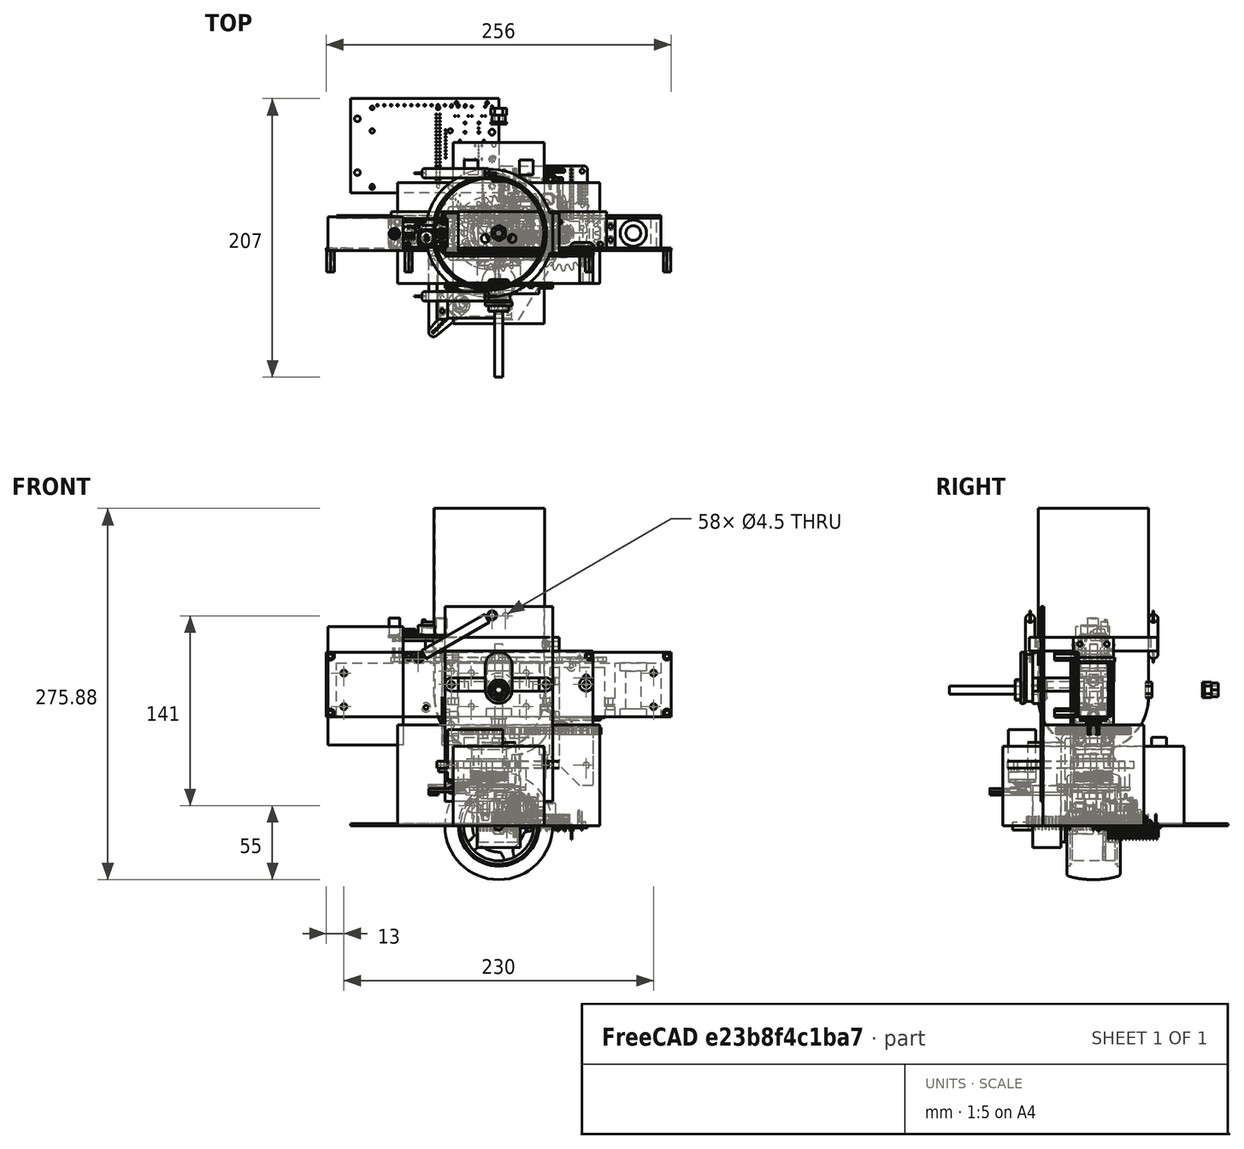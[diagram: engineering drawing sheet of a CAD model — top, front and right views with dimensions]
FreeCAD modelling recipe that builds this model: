
FCSTD DOCUMENT  (FreeCAD 0.19R24276 (Git))
Label: new_wheel_assy
License: All rights reserved
LicenseURL: http://en.wikipedia.org/wiki/All_rights_reserved
objects: Part::Feature×283, Sketcher::SketchObject×273, PartDesign::Pad×176, PartDesign::Body×146, App::Part×107, PartDesign::Pocket×72, PartDesign::FeatureBase×19, PartDesign::Revolution×11, PartDesign::Groove×8, Part::Part2DObjectPython×6, PartDesign::Chamfer×6, TechDraw::DrawViewPart×6, PartDesign::CoordinateSystem×5, TechDraw::DrawViewDimension×5, PartDesign::Plane×4, PartDesign::PolarPattern×4, TechDraw::DrawSVGTemplate×3, TechDraw::DrawPage×3, TechDraw::DrawViewSymbol×2, Mesh::Feature×1, +1 more types
note: 1288 computed .brp shape members not serialized (recipe doc carries the construction recipe); baked Part::Feature solids carry a one-line shape summary decoded from their .brp

FEATURE [Sketcher::SketchObject] Sketch
  FullyConstrained = false
  MapMode = 5
  Placement = pos=(0,0,0) rot=(0.57735,0.57735,0.57735;2.0944rad)
  Support = -> [YZ_Plane]
  sketch-geometry (17):
    g0: LineSegment StartX=16 StartY=28.5 StartZ=0 EndX=16 EndY=26 EndZ=0
    g1: LineSegment StartX=16 StartY=26 StartZ=0 EndX=-16 EndY=26 EndZ=0
    g2: LineSegment StartX=-16 StartY=26 StartZ=0 EndX=-16 EndY=28.5 EndZ=0
    g3: LineSegment StartX=-16 StartY=28.5 StartZ=0 EndX=-17.5 EndY=28.5 EndZ=0
    g4: LineSegment StartX=-17.5 StartY=28.5 StartZ=0 EndX=-17.5 EndY=30 EndZ=0
    g5: LineSegment StartX=-17.5 StartY=30 StartZ=0 EndX=-17.85 EndY=30 EndZ=0
    g6: LineSegment StartX=-19.85 StartY=32 StartZ=0 EndX=-19.85 EndY=35.5078 EndZ=0
    g7: LineSegment StartX=19.85 StartY=35.5078 StartZ=0 EndX=19.85 EndY=32 EndZ=0
    g8: LineSegment StartX=17.85 StartY=30 StartZ=0 EndX=17.5 EndY=30 EndZ=0
    g9: LineSegment StartX=17.5 StartY=30 StartZ=0 EndX=17.5 EndY=28.5 EndZ=0
    g10: LineSegment StartX=17.5 StartY=28.5 StartZ=0 EndX=16 EndY=28.5 EndZ=0
    g11: ArcOfCircle CenterX=5.199e-13 CenterY=-27.17 CenterZ=0 NormalX=0 NormalY=0 NormalZ=1 AngleXU=0 Radius=67.17 StartAngle=1.5708 EndAngle=1.84824
    g12: ArcOfCircle CenterX=5.199e-13 CenterY=-27.17 CenterZ=0 NormalX=0 NormalY=0 NormalZ=1 AngleXU=0 Radius=67.17 StartAngle=1.29335 EndAngle=1.5708
    g13: ArcOfCircle CenterX=-17.85 CenterY=32 CenterZ=0 NormalX=0 NormalY=0 NormalZ=1 AngleXU=0 Radius=2 StartAngle=3.14159 EndAngle=4.71239
    g14: ArcOfCircle CenterX=17.85 CenterY=32 CenterZ=0 NormalX=0 NormalY=0 NormalZ=1 AngleXU=0 Radius=2 StartAngle=4.71239 EndAngle=6.28319
    g15: ArcOfCircle CenterX=-17.85 CenterY=35.5078 CenterZ=0 NormalX=0 NormalY=0 NormalZ=1 AngleXU=0 Radius=2 StartAngle=1.84824 EndAngle=3.14159
    g16: ArcOfCircle CenterX=17.85 CenterY=35.5078 CenterZ=0 NormalX=0 NormalY=0 NormalZ=1 AngleXU=0 Radius=2 StartAngle=-9e-16 EndAngle=1.29335
  constraints (44):
    c: Coincident(g0,g1)
    c: Coincident(g1,g2)
    c: Coincident(g2,g3)
    c: Coincident(g3,g4)
    c: Coincident(g4,g5)
    c: Coincident(g8,g9)
    c: Coincident(g9,g10)
    c: Coincident(g10,g0)
    c: Vertical(g0)
    c: Vertical(g9)
    c: Vertical(g7)
    c: Horizontal(g8)
    c: Horizontal(g10)
    c: Horizontal(g1)
    c: Vertical(g2)
    c: Horizontal(g3)
    c: Horizontal(g5)
    c: Symmetric(g4,g8,g-2)
    c: DistanceX(g4,g8) = 35
    c: Equal(g3,g10)
    c: DistanceX(g10,g10) = 1.5
    c: DistanceY(g-1,g1) = 26
    c: DistanceY(g-1,g3) = 28.5
    c: DistanceY(g-1,g4) = 30
    c: Symmetric(g2,g0,g-2)
    c: Tangent(g11,g12) = -1.5708
    c: PointOnObject(g11,g-2)
    c: Coincident(g12,g11)
    c: DistanceY(g-1,g11) = 40
    c: Tangent(g5,g13) = 1.5708
    c: Tangent(g6,g13) = 1.5708
    c: Tangent(g7,g14) = 1.5708
    c: Tangent(g8,g14) = 1.5708
    c: Radius(g14) = 2
    c: DistanceX(g6,g7) = 39.7
    c: DistanceY(g11,g-1) = 27.17
    c: Tangent(g11,g15) = -1.5708
    c: Tangent(g6,g15) = 1.5708
    c: Tangent(g12,g16) = -1.5708
    c: Tangent(g7,g16) = 1.5708
    c: Symmetric(g6,g7,g-2)
    c: Equal(g16,g15)
    c: Radius(g16) = 2
    c: Symmetric(g6,g7,g-2)
FEATURE [PartDesign::Revolution] Revolution
  AllowMultiFace = false
  Angle = 360
  Axis = (3e-16,1,-2e-16)
  Base = (0,0,0)
  Placement = pos=(0,0,0) rot=(0.57735,0.57735,0.57735;2.0944rad)
  Profile = -> Sketch
  ReferenceAxis = -> Sketch [H_Axis]
FEATURE [PartDesign::Plane] DatumPlane
  AttachmentOffset = pos=(0,0,7) rot=(0,0,1;0rad)
  Length = 95.8516
  MapMode = 4
  Placement = pos=(0,7,0) rot=(0.57735,0.57735,0.57735;4.18879rad)
  ResizeMode = 0
  Support = -> [Revolution]
  Width = 95.8986
FEATURE [Sketcher::SketchObject] Sketch001
  FullyConstrained = false
  MapMode = 5
  Placement = pos=(0,7,0) rot=(0.57735,0.57735,0.57735;4.18879rad)
  Support = -> [DatumPlane]
  sketch-geometry (26):
    g0: LineSegment StartX=7 StartY=-18.2003 StartZ=0 EndX=19.4726 EndY=1.0332 EndZ=0
    g1: LineSegment StartX=19.4726 StartY=1.0332 StartZ=0 EndX=5.03473 EndY=18.8388 EndZ=0
    g2: LineSegment StartX=5.03473 StartY=18.8388 StartZ=0 EndX=-16.361 EndY=10.6098 EndZ=0
    g3: LineSegment StartX=-16.361 StartY=10.6098 StartZ=0 EndX=-15.1464 EndY=-12.2816 EndZ=0
    g4: LineSegment StartX=-15.1464 StartY=-12.2816 StartZ=0 EndX=7 EndY=-18.2003 EndZ=0
    g5: Circle CenterX=0 CenterY=0 CenterZ=0 NormalX=0 NormalY=0 NormalZ=1 AngleXU=0 Radius=19.5
    g6: ArcOfCircle CenterX=0 CenterY=0 CenterZ=0 NormalX=0 NormalY=0 NormalZ=1 AngleXU=0 Radius=19.5 StartAngle=5.60186 EndAngle=6.33619
    g7: ArcOfCircle CenterX=0 CenterY=0 CenterZ=0 NormalX=0 NormalY=0 NormalZ=1 AngleXU=0 Radius=19.5 StartAngle=4.34522 EndAngle=5.07956
    g8: ArcOfCircle CenterX=0 CenterY=0 CenterZ=0 NormalX=0 NormalY=0 NormalZ=1 AngleXU=0 Radius=19.5 StartAngle=3.08858 EndAngle=3.82292
    g9: ArcOfCircle CenterX=0 CenterY=0 CenterZ=0 NormalX=0 NormalY=0 NormalZ=1 AngleXU=0 Radius=19.5 StartAngle=1.83195 EndAngle=2.56628
    g10: ArcOfCircle CenterX=0 CenterY=0 CenterZ=0 NormalX=0 NormalY=0 NormalZ=1 AngleXU=0 Radius=19.5 StartAngle=0.575309 EndAngle=1.30965
    g11: ArcOfCircle CenterX=17.7078 CenterY=24.3726 CenterZ=0 NormalX=0 NormalY=0 NormalZ=1 AngleXU=0 Radius=13.8285 StartAngle=3.00933 EndAngle=3.5533
    g12: ArcOfCircle CenterX=17.7078 CenterY=24.3726 CenterZ=0 NormalX=0 NormalY=0 NormalZ=1 AngleXU=0 Radius=13.8285 StartAngle=4.61484 EndAngle=5.15882
    g13: ArcOfCircle CenterX=0 CenterY=0 CenterZ=0 NormalX=0 NormalY=0 NormalZ=1 AngleXU=0 Radius=26.5 StartAngle=0.162637 EndAngle=0.465682
    g14: ArcOfCircle CenterX=0 CenterY=0 CenterZ=0 NormalX=0 NormalY=0 NormalZ=1 AngleXU=0 Radius=26.5 StartAngle=1.41927 EndAngle=1.72232
    g15: ArcOfCircle CenterX=-17.7078 CenterY=24.3726 CenterZ=0 NormalX=0 NormalY=0 NormalZ=1 AngleXU=0 Radius=13.8285 StartAngle=5.87148 EndAngle=6.41545
    g16: ArcOfCircle CenterX=-17.7078 CenterY=24.3726 CenterZ=0 NormalX=0 NormalY=0 NormalZ=1 AngleXU=0 Radius=13.8285 StartAngle=4.26596 EndAngle=4.80994
    g17: ArcOfCircle CenterX=-28.6518 CenterY=-9.30952 CenterZ=0 NormalX=0 NormalY=0 NormalZ=1 AngleXU=0 Radius=13.8285 StartAngle=0.844931 EndAngle=1.3889
    g18: ArcOfCircle CenterX=-28.6518 CenterY=-9.30952 CenterZ=0 NormalX=0 NormalY=0 NormalZ=1 AngleXU=0 Radius=13.8285 StartAngle=5.5226 EndAngle=6.06657
    g19: ArcOfCircle CenterX=3.8e-15 CenterY=-30.1262 CenterZ=0 NormalX=0 NormalY=0 NormalZ=1 AngleXU=0 Radius=13.8285 StartAngle=2.10157 EndAngle=2.64554
    g20: ArcOfCircle CenterX=3.8e-15 CenterY=-30.1262 CenterZ=0 NormalX=0 NormalY=0 NormalZ=1 AngleXU=0 Radius=13.8285 StartAngle=0.496052 EndAngle=1.04002
    g21: ArcOfCircle CenterX=28.6518 CenterY=-9.30952 CenterZ=0 NormalX=0 NormalY=0 NormalZ=1 AngleXU=0 Radius=13.8285 StartAngle=3.35821 EndAngle=3.90218
    g22: ArcOfCircle CenterX=28.6518 CenterY=-9.30952 CenterZ=0 NormalX=0 NormalY=0 NormalZ=1 AngleXU=0 Radius=13.8285 StartAngle=1.75269 EndAngle=2.29666
    g23: ArcOfCircle CenterX=0 CenterY=0 CenterZ=0 NormalX=0 NormalY=0 NormalZ=1 AngleXU=0 Radius=26.5 StartAngle=2.67591 EndAngle=2.97896
    g24: ArcOfCircle CenterX=0 CenterY=0 CenterZ=0 NormalX=0 NormalY=0 NormalZ=1 AngleXU=0 Radius=26.5 StartAngle=3.93255 EndAngle=4.23559
    g25: ArcOfCircle CenterX=0 CenterY=0 CenterZ=0 NormalX=0 NormalY=0 NormalZ=1 AngleXU=0 Radius=26.5 StartAngle=5.18918 EndAngle=5.49223
  constraints (74):
    c: Coincident(g0,g1)
    c: Coincident(g1,g2)
    c: Coincident(g2,g3)
    c: Coincident(g3,g4)
    c: Coincident(g4,g0)
    c: Equal(g0, g1-g4) x4
    c: PointOnObject(g0,g5)
    c: PointOnObject(g1,g5)
    c: PointOnObject(g2,g5)
    c: PointOnObject(g3,g5)
    c: PointOnObject(g4,g5)
    c: Coincident(g5,g-1)
    c: Coincident(g10,g6)
    c: Coincident(g10,g7)
    c: Coincident(g10,g8)
    c: Coincident(g10,g9)
    c: Coincident(g10,g-1)
    c: Coincident(g10,g1)
    c: Coincident(g6,g0)
    c: Coincident(g7,g0)
    c: Coincident(g8,g3)
    c: Coincident(g9,g2)
    c: Distance(g8,g8) = 14
    c: Distance(g9,g9) = 14
    c: Distance(g10,g10) = 14
    c: Distance(g6,g6) = 14
    c: Distance(g7,g7) = 14
    c: Diameter(g5) = 39
    c: DistanceX(g-2,g7) = -7
    c: Coincident(g11,g10)
    c: Coincident(g12,g10)
    c: Coincident(g12,g11)
    c: Coincident(g14,g13)
    c: Coincident(g14,g6)
    c: Coincident(g14,g11)
    c: Coincident(g13,g12)
    c: Equal(g14,g13)
    c: Diameter(g14) = 53
    c: Equal(g12,g11)
    c: Coincident(g15,g16)
    c: Coincident(g15,g14)
    c: Coincident(g15,g9)
    c: Coincident(g16,g9)
    c: Coincident(g17,g8)
    c: Coincident(g17,g18)
    c: Coincident(g18,g8)
    c: Equal(g18,g17)
    c: Equal(g17,g16)
    c: Equal(g16,g15)
    c: Equal(g15,g11)
    c: Coincident(g22,g21)
    c: Coincident(g20,g19)
    c: Coincident(g19,g7)
    c: Coincident(g20,g7)
    c: Coincident(g21,g6)
    c: Coincident(g22,g6)
    c: Coincident(g22,g13)
    c: Equal(g19,g20)
    c: Equal(g20,g21)
    c: Equal(g21,g22)
    c: Equal(g22,g12)
    c: Coincident(g25,g23)
    c: Coincident(g25,g24)
    c: Coincident(g25,g6)
    c: Coincident(g20,g25)
    c: Coincident(g21,g25)
    c: Coincident(g24,g19)
    c: Coincident(g24,g18)
    c: Coincident(g23,g17)
    c: Coincident(g23,g16)
    c: Equal(g23,g24)
    c: Equal(g24,g25)
    c: Equal(g25,g13)
    c: Distance(g16,g17) = 8
FEATURE [PartDesign::Pad] Pad
  AllowMultiFace = false
  BaseFeature = -> Revolution
  Direction = (1,1,1)
  Length = 2
  Length2 = 100
  Placement = pos=(0,0,0) rot=(0.57735,0.57735,0.57735;2.0944rad)
  Profile = -> Sketch001
  Type = 0
FEATURE [Sketcher::SketchObject] Sketch002
  FullyConstrained = false
  MapMode = 5
  Placement = pos=(0,7,0) rot=(0.57735,0.57735,-0.57735;2.0944rad)
  Support = -> [Pad]
  sketch-geometry (1):
    g0: Circle CenterX=0 CenterY=0 CenterZ=0 NormalX=0 NormalY=0 NormalZ=1 AngleXU=0 Radius=8.5
  constraints (2):
    c: Coincident(g0,g-1)
    c: Diameter(g0) = 17
FEATURE [Sketcher::SketchObject] Sketch004
  FullyConstrained = false
  MapMode = 5
  Placement = pos=(0,0,0) rot=(0.57735,0.57735,0.57735;2.0944rad)
  Support = -> [YZ_Plane]
  sketch-geometry (9):
    g0: LineSegment StartX=9 StartY=-2 StartZ=0 EndX=9 EndY=-19.5 EndZ=0
    g1: LineSegment StartX=9 StartY=-19.5 StartZ=0 EndX=9.5 EndY=-19.5 EndZ=0
    g2: LineSegment StartX=9.5 StartY=-19.5 StartZ=0 EndX=12 EndY=-12.5 EndZ=0
    g3: LineSegment StartX=12 StartY=-12.5 StartZ=0 EndX=11 EndY=-7 EndZ=0
    g4: LineSegment StartX=11 StartY=-7 StartZ=0 EndX=14 EndY=-7 EndZ=0
    g5: LineSegment StartX=14 StartY=-7 StartZ=0 EndX=14 EndY=-5 EndZ=0
    g6: LineSegment StartX=14 StartY=-5 StartZ=0 EndX=12 EndY=-5 EndZ=0
    g7: LineSegment StartX=12 StartY=-5 StartZ=0 EndX=12 EndY=-2 EndZ=0
    g8: LineSegment StartX=12 StartY=-2 StartZ=0 EndX=9 EndY=-2 EndZ=0
  constraints (27):
    c: Coincident(g0,g1)
    c: Coincident(g1,g2)
    c: Coincident(g2,g3)
    c: Coincident(g3,g4)
    c: Coincident(g4,g5)
    c: Coincident(g5,g6)
    c: Coincident(g6,g7)
    c: Coincident(g7,g8)
    c: Coincident(g0,g8)
    c: Vertical(g0)
    c: DistanceX(g-1,g0) = 9
    c: DistanceY(g0,g-1) = 19.5
    c: Horizontal(g1)
    c: DistanceY(g0,g-1) = 2
    c: Horizontal(g8)
    c: Vertical(g7)
    c: DistanceX(g8,g8) = 3
    c: Horizontal(g6)
    c: DistanceX(g6,g6) = 2
    c: DistanceY(g5,g-1) = 5
    c: DistanceY(g4,g-1) = 7
    c: Vertical(g5)
    c: DistanceX(g0,g2) = 3
    c: DistanceX(g1,g1) = 0.5
    c: Horizontal(g4)
    c: DistanceX(g4,g4) = 3
    c: DistanceY(g2,g-1) = 12.5
FEATURE [PartDesign::Revolution] Revolution001
  AllowMultiFace = false
  Angle = 360
  Axis = (3e-16,1,-2e-16)
  Base = (0,0,0)
  BaseFeature = -> Pad
  Placement = pos=(0,0,0) rot=(0.57735,0.57735,0.57735;2.0944rad)
  Profile = -> Sketch004
  ReferenceAxis = -> Sketch004 [H_Axis]
  Reversed = true
FEATURE [Sketcher::SketchObject] Sketch005
  FullyConstrained = false
  MapMode = 5
  Support = -> [XY_Plane]
  sketch-geometry (3):
    g0: LineSegment StartX=7.5 StartY=7 StartZ=0 EndX=17.5 EndY=7 EndZ=0
    g1: LineSegment StartX=17.5 StartY=7 StartZ=0 EndX=12.5 EndY=10 EndZ=0
    g2: LineSegment StartX=12.5 StartY=10 StartZ=0 EndX=7.5 EndY=7 EndZ=0
  constraints (9):
    c: Coincident(g0,g1)
    c: Coincident(g1,g2)
    c: Coincident(g0,g2)
    c: DistanceY(g-1,g0) = 7
    c: Horizontal(g0)
    c: DistanceY(g0,g1) = 3
    c: DistanceX(g-1,g0) = 17.5
    c: DistanceX(g-1,g1) = 12.5
    c: DistanceX(g-1,g0) = 7.5
FEATURE [PartDesign::Groove] Groove
  AllowMultiFace = false
  Angle = 360
  Axis = (0,1,0)
  Base = (0,0,0)
  BaseFeature = -> Revolution001
  Placement = pos=(0,0,0) rot=(0.57735,0.57735,0.57735;2.0944rad)
  Profile = -> Sketch005
  ReferenceAxis = -> Sketch005 [V_Axis]
FEATURE [PartDesign::Pad] Pad001
  AllowMultiFace = false
  BaseFeature = -> Groove
  Direction = (1,1,1)
  Length = 1.5
  Length2 = 100
  Placement = pos=(0,0,0) rot=(0.57735,0.57735,0.57735;2.0944rad)
  Profile = -> Sketch002
  Type = 0
FEATURE [Sketcher::SketchObject] Sketch003
  FullyConstrained = false
  MapMode = 5
  Placement = pos=(0,5.5,0) rot=(0.57735,0.57735,-0.57735;2.0944rad)
  Support = -> [Pad001]
  sketch-geometry (7):
    g0: LineSegment StartX=6 StartY=-3.4641 StartZ=0 EndX=6 EndY=3.4641 EndZ=0
    g1: LineSegment StartX=6 StartY=3.4641 StartZ=0 EndX=9e-16 EndY=6.9282 EndZ=0
    g2: LineSegment StartX=9e-16 StartY=6.9282 StartZ=0 EndX=-6 EndY=3.4641 EndZ=0
    g3: LineSegment StartX=-6 StartY=3.4641 StartZ=0 EndX=-6 EndY=-3.4641 EndZ=0
    g4: LineSegment StartX=-6 StartY=-3.4641 StartZ=0 EndX=0 EndY=-6.9282 EndZ=0
    g5: LineSegment StartX=0 StartY=-6.9282 StartZ=0 EndX=6 EndY=-3.4641 EndZ=0
    g6: Circle CenterX=0 CenterY=0 CenterZ=0 NormalX=0 NormalY=0 NormalZ=1 AngleXU=0 Radius=6.9282
  constraints (16):
    c: Coincident(g0,g1)
    c: Coincident(g1,g2)
    c: Coincident(g2,g3)
    c: Coincident(g3,g4)
    c: Coincident(g4,g5)
    c: Coincident(g5,g0)
    c: Equal(g0, g1-g5) x5
    c: PointOnObject(g0,g6)
    c: PointOnObject(g1,g6)
    c: PointOnObject(g2,g6)
    c: PointOnObject(g3,g6)
    c: PointOnObject(g4,g6)
    c: PointOnObject(g5,g6)
    c: Coincident(g6,g-1)
    c: Vertical(g3)
    c: DistanceX(g2,g0) = 12
FEATURE [Sketcher::SketchObject] Sketch006
  FullyConstrained = false
  MapMode = 5
  Support = -> [XY_Plane]
  sketch-geometry (6):
    g0: LineSegment StartX=26.5 StartY=-6 StartZ=0 EndX=26.5 EndY=8 EndZ=0
    g1: LineSegment StartX=26.5 StartY=8 StartZ=0 EndX=17.5 EndY=8 EndZ=0
    g2: LineSegment StartX=17.5 StartY=8 StartZ=0 EndX=12.5 EndY=12 EndZ=0
    g3: LineSegment StartX=12.5 StartY=12 StartZ=0 EndX=6.25 EndY=14 EndZ=0
    g4: LineSegment StartX=6.25 StartY=14 StartZ=0 EndX=6.25 EndY=6 EndZ=0
    g5: ArcOfCircle CenterX=7.23279 CenterY=-15.4275 CenterZ=0 NormalX=0 NormalY=0 NormalZ=1 AngleXU=0 Radius=21.45 StartAngle=0.455052 EndAngle=1.61663
  constraints (19):
    c: Coincident(g0,g1)
    c: Coincident(g1,g2)
    c: Coincident(g2,g3)
    c: Coincident(g3,g4)
    c: Horizontal(g1)
    c: Vertical(g0)
    c: Vertical(g4)
    c: Coincident(g5,g0)
    c: Coincident(g5,g4)
    c: Diameter(g5) = 42.9
    c: DistanceY(g0,g0) = 14
    c: DistanceY(g4,g4) = 8
    c: DistanceY(g0,g-1) = 6
    c: DistanceX(g-1,g2) = 12.5
    c: DistanceX(g-1,g3) = 6.25
    c: DistanceX(g-1,g1) = 17.5
    c: DistanceX(g-1,g0) = 26.5
    c: DistanceY(g-1,g4) = 6
    c: DistanceY(g2,g3) = 2
FEATURE [PartDesign::Pad] Pad002
  AllowMultiFace = false
  BaseFeature = -> Pad001
  Direction = (1,1,1)
  Length = 1.5
  Length2 = 100
  Midplane = true
  Placement = pos=(0,0,0) rot=(0.57735,0.57735,0.57735;2.0944rad)
  Profile = -> Sketch006
  Type = 0
FEATURE [PartDesign::PolarPattern] PolarPattern
  Angle = 360
  Axis = -> Y_Axis
  BaseFeature = -> Pad002
  Occurrences = 5
  Originals = -> [Pad002]
  Placement = pos=(0,0,0) rot=(0.57735,0.57735,0.57735;2.0944rad)
FEATURE [PartDesign::Pocket] Pocket
  AllowMultiFace = false
  BaseFeature = -> PolarPattern
  Length = 4.8
  Length2 = 100
  Placement = pos=(0,0,0) rot=(0.57735,0.57735,0.57735;2.0944rad)
  Profile = -> Sketch003
  Type = 0
FEATURE [PartDesign::Body] Body  label="Wheel"
  Group = -> [Sketch,Revolution,DatumPlane,Sketch001,Pad,Sketch002,Sketch003,Sketch004,Sketch005,Revolution001,Groove,Pad001,Pad002,PolarPattern,Pocket,Sketch006]
  Origin = -> Origin
  Tip = -> Pad
FEATURE [Sketcher::SketchObject] Sketch007
  FullyConstrained = false
  MapMode = 5
  Support = -> [XY_Plane001]
  sketch-geometry (7):
    g0: LineSegment StartX=6 StartY=3.4641 StartZ=0 EndX=3.87264e-11 EndY=6.9282 EndZ=0
    g1: LineSegment StartX=3.8726e-11 StartY=6.9282 StartZ=0 EndX=-6 EndY=3.4641 EndZ=0
    g2: LineSegment StartX=-6 StartY=3.4641 StartZ=0 EndX=-6 EndY=-3.4641 EndZ=0
    g3: LineSegment StartX=-6 StartY=-3.4641 StartZ=0 EndX=1.74527e-11 EndY=-6.9282 EndZ=0
    g4: LineSegment StartX=1.74523e-11 StartY=-6.9282 StartZ=0 EndX=6 EndY=-3.4641 EndZ=0
    g5: LineSegment StartX=6 StartY=-3.4641 StartZ=0 EndX=6 EndY=3.4641 EndZ=0
    g6: Circle CenterX=0 CenterY=0 CenterZ=0 NormalX=0 NormalY=0 NormalZ=1 AngleXU=0 Radius=6.9282
  constraints (16):
    c: Coincident(g0,g1)
    c: Coincident(g1,g2)
    c: Coincident(g2,g3)
    c: Coincident(g3,g4)
    c: Coincident(g4,g5)
    c: Coincident(g5,g0)
    c: Equal(g0, g1-g5) x5
    c: PointOnObject(g0,g6)
    c: PointOnObject(g1,g6)
    c: PointOnObject(g2,g6)
    c: PointOnObject(g3,g6)
    c: PointOnObject(g4,g6)
    c: PointOnObject(g5,g6)
    c: Coincident(g6,g-1)
    c: Vertical(g5)
    c: DistanceX(g1,g0) = 12
FEATURE [PartDesign::Pad] Pad003
  AllowMultiFace = false
  Direction = (1,1,1)
  Length = 6
  Length2 = 100
  Profile = -> Sketch007
  Type = 0
FEATURE [Sketcher::SketchObject] Sketch008
  FullyConstrained = false
  MapMode = 5
  Placement = pos=(0,0,6) rot=(0,0,1;0rad)
  Support = -> [Pad003]
  sketch-geometry (1):
    g0: Circle CenterX=0 CenterY=0 CenterZ=0 NormalX=0 NormalY=0 NormalZ=1 AngleXU=0 Radius=6
  constraints (2):
    c: Coincident(g0,g-1)
    c: Diameter(g0) = 12
FEATURE [PartDesign::Pad] Pad004
  AllowMultiFace = false
  BaseFeature = -> Pad003
  Direction = (1,1,1)
  Length = 24
  Length2 = 100
  Profile = -> Sketch008
  Type = 0
FEATURE [Sketcher::SketchObject] Sketch009
  FullyConstrained = false
  MapMode = 5
  Placement = pos=(0,0,30) rot=(0,0,1;0rad)
  Support = -> [Pad004]
  sketch-geometry (1):
    g0: Circle CenterX=0 CenterY=0 CenterZ=0 NormalX=0 NormalY=0 NormalZ=1 AngleXU=0 Radius=3
  constraints (2):
    c: Coincident(g0,g-1)
    c: Diameter(g0) = 6
FEATURE [PartDesign::Pocket] Pocket001
  AllowMultiFace = false
  BaseFeature = -> Pad004
  Length = 24.5
  Length2 = 100
  Profile = -> Sketch009
  Type = 0
FEATURE [Sketcher::SketchObject] Sketch010
  FullyConstrained = false
  MapMode = 5
  Placement = pos=(0,0,0) rot=(1,0,0;3.14159rad)
  Support = -> [Pocket001]
  sketch-geometry (1):
    g0: Circle CenterX=0 CenterY=0 CenterZ=0 NormalX=0 NormalY=0 NormalZ=1 AngleXU=0 Radius=1.75
  constraints (2):
    c: Coincident(g0,g-1)
    c: Diameter(g0) = 3.5
FEATURE [PartDesign::Pocket] Pocket002
  AllowMultiFace = false
  BaseFeature = -> Pocket001
  Length = 6
  Length2 = 100
  Profile = -> Sketch010
  Type = 0
FEATURE [Sketcher::SketchObject] Sketch011
  FullyConstrained = false
  MapMode = 5
  Placement = pos=(0,0,0) rot=(1,0,0;1.5708rad)
  Support = -> [XZ_Plane001]
  sketch-geometry (1):
    g0: Circle CenterX=0 CenterY=24.5 CenterZ=0 NormalX=0 NormalY=0 NormalZ=1 AngleXU=0 Radius=1.75
  constraints (3):
    c: PointOnObject(g0,g-2)
    c: DistanceY(g-1,g0) = 24.5
    c: Diameter(g0) = 3.5
FEATURE [PartDesign::Pocket] Pocket003
  AllowMultiFace = false
  BaseFeature = -> Pocket002
  Length = 14
  Length2 = 100
  Midplane = true
  Profile = -> Sketch011
  Type = 0
FEATURE [PartDesign::Body] Body001  label="Axel"
  Group = -> [Sketch007,Pad003,Sketch008,Pad004,Sketch009,Pocket001,Sketch010,Pocket002,Sketch011,Pocket003]
  Origin = -> Origin001
  Placement = pos=(0,10.3,0) rot=(0.935113,-0.250563,0.250563;1.63783rad)
  Tip = -> Pocket003
FEATURE [Sketcher::SketchObject] Sketch026
  FullyConstrained = true
  MapMode = 5
  Support = -> [XY_Plane004]
  sketch-geometry (14):
    g0: LineSegment StartX=-150 StartY=112.5 StartZ=0 EndX=150 EndY=112.5 EndZ=0
    g1: LineSegment StartX=150 StartY=112.5 StartZ=0 EndX=150 EndY=-112.5 EndZ=0
    g2: LineSegment StartX=150 StartY=-112.5 StartZ=0 EndX=-150 EndY=-112.5 EndZ=0
    g3: LineSegment StartX=-150 StartY=-112.5 StartZ=0 EndX=-150 EndY=112.5 EndZ=0
    g4: LineSegment StartX=-150 StartY=1.13e-14 StartZ=0 EndX=150 EndY=1.13e-14 EndZ=0
    g5: LineSegment StartX=-2.91e-14 StartY=112.5 StartZ=0 EndX=-1.61e-14 EndY=-112.5 EndZ=0
    g6: LineSegment StartX=-250 StartY=112.5 StartZ=0 EndX=-150 EndY=112.5 EndZ=0
    g7: LineSegment StartX=-150 StartY=112.5 StartZ=0 EndX=-150 EndY=-112.5 EndZ=0
    g8: LineSegment StartX=-150 StartY=-112.5 StartZ=0 EndX=-250 EndY=-112.5 EndZ=0
    g9: LineSegment StartX=-250 StartY=-112.5 StartZ=0 EndX=-250 EndY=112.5 EndZ=0
    g10: LineSegment StartX=-350 StartY=162.5 StartZ=0 EndX=150 EndY=162.5 EndZ=0
    g11: LineSegment StartX=150 StartY=162.5 StartZ=0 EndX=150 EndY=-162.5 EndZ=0
    g12: LineSegment StartX=150 StartY=-162.5 StartZ=0 EndX=-350 EndY=-162.5 EndZ=0
    g13: LineSegment StartX=-350 StartY=-162.5 StartZ=0 EndX=-350 EndY=162.5 EndZ=0
  constraints (37):
    c: Coincident(g0,g1)
    c: Coincident(g1,g2)
    c: Coincident(g2,g3)
    c: Coincident(g3,g0)
    c: Horizontal(g0)
    c: Horizontal(g2)
    c: Vertical(g1)
    c: Vertical(g3)
    c: DistanceX(g0,g0) = 300
    c: DistanceY(g3,g3) = 225
    c: Symmetric(g0,g1,g4)
    c: Symmetric(g0,g2,g4)
    c: Symmetric(g2,g1,g5)
    c: Symmetric(g0,g0,g5)
    c: Symmetric(g0,g1,g-1)
    c: Coincident(g6,g7)
    c: Coincident(g7,g8)
    c: Coincident(g8,g9)
    c: Coincident(g9,g6)
    c: Horizontal(g6)
    c: Horizontal(g8)
    c: Vertical(g9)
    c: Coincident(g10,g11)
    c: Coincident(g11,g12)
    c: Coincident(g12,g13)
    c: Coincident(g13,g10)
    c: Horizontal(g10)
    c: Horizontal(g12)
    c: Vertical(g11)
    c: Vertical(g13)
    c: Coincident(g7,g2)
    c: Coincident(g0,g6)
    c: DistanceX(g6,g6) = 100
    c: PointOnObject(g0,g11)
    c: DistanceX(g10,g10) = 500
    c: DistanceY(g0,g10) = 50
    c: DistanceY(g11,g1) = 50
FEATURE [PartDesign::Body] Body004  label="Rules"
  Group = -> [Sketch026]
  Origin = -> Origin004
FEATURE [Sketcher::SketchObject] Sketch029
  FullyConstrained = false
  MapMode = 5
  Support = -> [XY_Plane007]
  sketch-geometry (4):
    g0: LineSegment StartX=-16 StartY=16 StartZ=0 EndX=30 EndY=16 EndZ=0
    g1: LineSegment StartX=30 StartY=16 StartZ=0 EndX=30 EndY=-16 EndZ=0
    g2: LineSegment StartX=30 StartY=-16 StartZ=0 EndX=-16 EndY=-16 EndZ=0
    g3: LineSegment StartX=-16 StartY=-16 StartZ=0 EndX=-16 EndY=16 EndZ=0
  constraints (11):
    c: Coincident(g0,g1)
    c: Coincident(g1,g2)
    c: Coincident(g2,g3)
    c: Coincident(g3,g0)
    c: Horizontal(g0)
    c: Horizontal(g2)
    c: Vertical(g1)
    c: DistanceX(g0,g0) = 46
    c: DistanceY(g3,g3) = 32
    c: Symmetric(g0,g2,g-1)
    c: DistanceX(g2,g-1) = 16
FEATURE [PartDesign::Pad] Pad013
  AllowMultiFace = false
  Direction = (1,1,1)
  Length = 21
  Length2 = 100
  Profile = -> Sketch029
  Type = 0
FEATURE [Sketcher::SketchObject] Sketch030
  FullyConstrained = false
  MapMode = 5
  Placement = pos=(30,0,0) rot=(0.57735,0.57735,0.57735;2.0944rad)
  Support = -> [Pad013]
  sketch-geometry (1):
    g0: Circle CenterX=0 CenterY=12.5 CenterZ=0 NormalX=0 NormalY=0 NormalZ=1 AngleXU=0 Radius=12.5
  constraints (3):
    c: Diameter(g0) = 25
    c: PointOnObject(g0,g-2)
    c: DistanceY(g-1,g0) = 12.5
FEATURE [PartDesign::Pad] Pad014
  AllowMultiFace = false
  BaseFeature = -> Pad013
  Direction = (1,1,1)
  Length = 32
  Length2 = 100
  Profile = -> Sketch030
  Type = 0
FEATURE [Sketcher::SketchObject] Sketch031
  FullyConstrained = false
  MapMode = 5
  Placement = pos=(0,0,0) rot=(1,0,0;3.14159rad)
  Support = -> [Pad014]
  sketch-geometry (2):
    g0: ArcOfCircle CenterX=0 CenterY=0 CenterZ=0 NormalX=0 NormalY=0 NormalZ=1 AngleXU=0 Radius=3 StartAngle=0.585686 EndAngle=5.6975
    g1: LineSegment StartX=2.5 StartY=1.65831 StartZ=0 EndX=2.5 EndY=-1.65831 EndZ=0
  constraints (6):
    c: Coincident(g0,g-1)
    c: Diameter(g0) = 6
    c: Coincident(g1,g0)
    c: Coincident(g1,g0)
    c: Vertical(g1)
    c: DistanceX(g0,g0) = 2.5
FEATURE [PartDesign::Pad] Pad015
  AllowMultiFace = false
  BaseFeature = -> Pad014
  Direction = (1,1,1)
  Length = 15
  Length2 = 100
  Profile = -> Sketch031
  Type = 0
FEATURE [Sketcher::SketchObject] Sketch032
  FullyConstrained = false
  MapMode = 5
  Placement = pos=(0,0,21) rot=(0,0,1;0rad)
  Support = -> [Pad015]
  sketch-geometry (2):
    g0: ArcOfCircle CenterX=0 CenterY=0 CenterZ=0 NormalX=0 NormalY=0 NormalZ=1 AngleXU=0 Radius=3 StartAngle=0.585686 EndAngle=5.6975
    g1: LineSegment StartX=2.5 StartY=1.65831 StartZ=0 EndX=2.5 EndY=-1.65831 EndZ=0
  constraints (6):
    c: Coincident(g0,g-1)
    c: Coincident(g1,g0)
    c: Coincident(g1,g0)
    c: Vertical(g1)
    c: DistanceX(g0,g0) = 2.5
    c: Diameter(g0) = 6
FEATURE [PartDesign::Pad] Pad016
  AllowMultiFace = false
  BaseFeature = -> Pad015
  Direction = (1,1,1)
  Length = 15
  Length2 = 100
  Profile = -> Sketch032
  Type = 0
FEATURE [PartDesign::Body] Body007  label="Motor"
  Group = -> [Sketch029,Pad013,Sketch030,Pad014,Sketch031,Pad015,Sketch032,Pad016]
  Origin = -> Origin007
  Placement = pos=(-1.1e-14,-24,0) rot=(0.57735,-0.57735,0.57735;2.0944rad)
  Tip = -> Pad016
FEATURE [Sketcher::SketchObject] Sketch033
  FullyConstrained = false
  MapMode = 5
  Placement = pos=(0,0,0) rot=(0.57735,0.57735,0.57735;2.0944rad)
  Support = -> [YZ_Plane008]
  sketch-geometry (8):
    g0: LineSegment StartX=-24 StartY=64 StartZ=0 EndX=-24 EndY=-12 EndZ=0
    g1: LineSegment StartX=-24 StartY=-12 StartZ=0 EndX=-21 EndY=-12 EndZ=0
    g2: LineSegment StartX=-21 StartY=-12 StartZ=0 EndX=-21 EndY=64 EndZ=0
    g3: LineSegment StartX=-20 StartY=65 StartZ=0 EndX=16 EndY=65 EndZ=0
    g4: LineSegment StartX=16 StartY=65 StartZ=0 EndX=16 EndY=68 EndZ=0
    g5: LineSegment StartX=16 StartY=68 StartZ=0 EndX=-20 EndY=68 EndZ=0
    g6: ArcOfCircle CenterX=-20 CenterY=64 CenterZ=0 NormalX=0 NormalY=0 NormalZ=1 AngleXU=0 Radius=4 StartAngle=1.5708 EndAngle=3.14159
    g7: ArcOfCircle CenterX=-20 CenterY=64 CenterZ=0 NormalX=0 NormalY=0 NormalZ=1 AngleXU=0 Radius=1 StartAngle=1.5708 EndAngle=3.14159
  constraints (21):
    c: Coincident(g0,g1)
    c: Coincident(g1,g2)
    c: Coincident(g3,g4)
    c: Coincident(g4,g5)
    c: Vertical(g0)
    c: Horizontal(g1)
    c: Tangent(g7,g2) = 1.5708
    c: Tangent(g7,g3) = 1.5708
    c: Tangent(g6,g0) = -1.5708
    c: Tangent(g6,g5) = -1.5708
    c: Horizontal(g5)
    c: Vertical(g4)
    c: Equal(g1,g4)
    c: DistanceY(g4,g4) = 3
    c: Diameter(g7) = 2
    c: Horizontal(g3)
    c: DistanceY(g1,g-1) = 12
    c: DistanceY(g-1,g3) = 65
    c: Coincident(g6,g7)
    c: DistanceX(g0,g-1) = 24
    c: DistanceX(g0,g4) = 40
FEATURE [PartDesign::Pad] Pad017
  AllowMultiFace = false
  Direction = (1,1,1)
  Length = 30
  Length2 = 100
  Midplane = true
  Placement = pos=(0,0,0) rot=(0.57735,0.57735,0.57735;2.0944rad)
  Profile = -> Sketch033
  Type = 0
FEATURE [Sketcher::SketchObject] Sketch034
  FullyConstrained = false
  MapMode = 5
  Placement = pos=(-1.9e-14,2.99e-14,68) rot=(0,0,-1;1.5708rad)
  Support = -> [Pad017]
  sketch-geometry (9):
    g0: Circle CenterX=0 CenterY=0 CenterZ=0 NormalX=0 NormalY=0 NormalZ=1 AngleXU=0 Radius=3.25
    g1: LineSegment StartX=-10 StartY=10 StartZ=0 EndX=10 EndY=10 EndZ=0
    g2: LineSegment StartX=10 StartY=10 StartZ=0 EndX=10 EndY=-10 EndZ=0
    g3: LineSegment StartX=10 StartY=-10 StartZ=0 EndX=-10 EndY=-10 EndZ=0
    g4: LineSegment StartX=-10 StartY=-10 StartZ=0 EndX=-10 EndY=10 EndZ=0
    g5: Circle CenterX=10 CenterY=10 CenterZ=0 NormalX=0 NormalY=0 NormalZ=1 AngleXU=0 Radius=1.75
    g6: Circle CenterX=10 CenterY=-10 CenterZ=0 NormalX=0 NormalY=0 NormalZ=1 AngleXU=0 Radius=1.75
    g7: Circle CenterX=-10 CenterY=-10 CenterZ=0 NormalX=0 NormalY=0 NormalZ=1 AngleXU=0 Radius=1.75
    g8: Circle CenterX=-10 CenterY=10 CenterZ=0 NormalX=0 NormalY=0 NormalZ=1 AngleXU=0 Radius=1.75
  constraints (21):
    c: Coincident(g0,g-1)
    c: Diameter(g0) = 6.5
    c: Coincident(g1,g2)
    c: Coincident(g2,g3)
    c: Coincident(g3,g4)
    c: Coincident(g4,g1)
    c: Horizontal(g1)
    c: Horizontal(g3)
    c: Vertical(g2)
    c: Vertical(g4)
    c: DistanceX(g1,g1) = 20
    c: DistanceY(g4,g4) = 20
    c: Symmetric(g1,g2,g0)
    c: Coincident(g8,g1)
    c: Coincident(g5,g1)
    c: Coincident(g6,g2)
    c: Coincident(g7,g3)
    c: Diameter(g7) = 3.5
    c: Equal(g7,g6)
    c: Equal(g7,g5)
    c: Equal(g7,g8)
FEATURE [PartDesign::Pocket] Pocket009
  AllowMultiFace = false
  BaseFeature = -> Pad017
  Length = 5
  Length2 = 100
  Placement = pos=(0,0,0) rot=(0.57735,0.57735,0.57735;2.0944rad)
  Profile = -> Sketch034
  Type = 0
FEATURE [PartDesign::Body] Body008  label="Wheel Bracket"
  Group = -> [Sketch033,Pad017,Sketch034,Pocket009]
  Origin = -> Origin008
  Tip = -> Pocket009
FEATURE [Part::Part2DObjectPython] InvoluteGear  # Draft 2D object (typed FeaturePython)
  ExternalGear = true
  HighPrecision = true
  Modules = 2
  NumberOfTeeth = 26
  PressureAngle = 20
FEATURE [PartDesign::Pad] Pad018
  AllowMultiFace = false
  Direction = (1,1,1)
  Length = 5
  Length2 = 100
  Profile = -> InvoluteGear
  Type = 0
FEATURE [Part::Part2DObjectPython] InvoluteGear001  # Draft 2D object (typed FeaturePython)
  ExternalGear = true
  HighPrecision = true
  Modules = 2
  NumberOfTeeth = 26
  PressureAngle = 20
FEATURE [PartDesign::Pad] Pad019
  AllowMultiFace = false
  Direction = (1,1,1)
  Length = 5
  Length2 = 100
  Profile = -> InvoluteGear001
  Type = 0
FEATURE [Sketcher::SketchObject] Sketch036
  FullyConstrained = false
  MapMode = 5
  Placement = pos=(0,0,5) rot=(0,0,1;0rad)
  Support = -> [Pad019]
  sketch-geometry (1):
    g0: Circle CenterX=0 CenterY=0 CenterZ=0 NormalX=0 NormalY=0 NormalZ=1 AngleXU=0 Radius=18
  constraints (2):
    c: Coincident(g0,g-1)
    c: Diameter(g0) = 36
FEATURE [PartDesign::Pocket] Pocket010
  AllowMultiFace = false
  BaseFeature = -> Pad019
  Length = 2
  Length2 = 100
  Profile = -> Sketch036
  Type = 0
FEATURE [Sketcher::SketchObject] Sketch037
  FullyConstrained = false
  MapMode = 5
  Placement = pos=(0,0,3) rot=(0,0,1;0rad)
  Support = -> [Pocket010]
  sketch-geometry (1):
    g0: Circle CenterX=0 CenterY=0 CenterZ=0 NormalX=0 NormalY=0 NormalZ=1 AngleXU=0 Radius=5.5
  constraints (2):
    c: Coincident(g0,g-1)
    c: Diameter(g0) = 11
FEATURE [PartDesign::Pocket] Pocket011
  AllowMultiFace = false
  BaseFeature = -> Pocket010
  Length = 0.5
  Length2 = 100
  Profile = -> Sketch037
  Type = 0
FEATURE [Sketcher::SketchObject] Sketch038
  FullyConstrained = false
  MapMode = 5
  Placement = pos=(0,0,0) rot=(1,0,0;3.14159rad)
  Support = -> [Pocket011]
  sketch-geometry (6):
    g0: Circle CenterX=0 CenterY=0 CenterZ=0 NormalX=0 NormalY=0 NormalZ=1 AngleXU=0 Radius=4
    g1: Circle CenterX=12.5 CenterY=0 CenterZ=0 NormalX=0 NormalY=0 NormalZ=1 AngleXU=0 Radius=1.75
    g2: Circle CenterX=0 CenterY=-12.5 CenterZ=0 NormalX=0 NormalY=0 NormalZ=1 AngleXU=0 Radius=1.75
    g3: Circle CenterX=-12.5 CenterY=0 CenterZ=0 NormalX=0 NormalY=0 NormalZ=1 AngleXU=0 Radius=1.75
    g4: Circle CenterX=0 CenterY=12.5 CenterZ=0 NormalX=0 NormalY=0 NormalZ=1 AngleXU=0 Radius=1.75
    g5: Circle CenterX=0 CenterY=0 CenterZ=0 NormalX=0 NormalY=0 NormalZ=1 AngleXU=0 Radius=12.5
  constraints (16):
    c: Coincident(g0,g-1)
    c: Diameter(g0) = 8
    c: PointOnObject(g1,g-1)
    c: PointOnObject(g4,g-2)
    c: PointOnObject(g3,g-1)
    c: PointOnObject(g2,g-2)
    c: Diameter(g2) = 3.5
    c: Equal(g2,g1)
    c: Equal(g2,g4)
    c: Equal(g2,g3)
    c: Coincident(g5,g0)
    c: PointOnObject(g1,g5)
    c: PointOnObject(g4,g5)
    c: PointOnObject(g3,g5)
    c: PointOnObject(g2,g5)
    c: Diameter(g5) = 25
FEATURE [PartDesign::Pocket] Pocket012
  AllowMultiFace = false
  BaseFeature = -> Pocket011
  Length = 5
  Length2 = 100
  Profile = -> Sketch038
  Type = 0
FEATURE [PartDesign::Body] Body010  label="Servo Gear"
  Group = -> [InvoluteGear001,Pad019,Sketch036,Pocket010,Sketch037,Pocket011,Sketch038,Pocket012]
  Origin = -> Origin010
  Placement = pos=(-48,-2.22e-14,68) rot=(0,0,-1;1.5708rad)
  Tip = -> Pocket012
FEATURE [Sketcher::SketchObject] Sketch039
  FullyConstrained = false
  MapMode = 5
  Placement = pos=(0,0,0) rot=(1,0,0;1.5708rad)
  Support = -> [XZ_Plane012]
  sketch-geometry (15):
    g0: LineSegment StartX=-1.5 StartY=0 StartZ=0 EndX=-1.5 EndY=-0.85 EndZ=0
    g1: LineSegment StartX=-1.5 StartY=-0.85 StartZ=0 EndX=-3.85 EndY=-0.85 EndZ=0
    g2: LineSegment StartX=-3.85 StartY=-0.85 StartZ=0 EndX=-3.85 EndY=-1.85 EndZ=0
    g3: LineSegment StartX=-3.85 StartY=-1.85 StartZ=0 EndX=-4.85 EndY=-1.85 EndZ=0
    g4: LineSegment StartX=-4.85 StartY=-1.85 StartZ=0 EndX=-5.35 EndY=-1.35 EndZ=0
    g5: LineSegment StartX=-5.35 StartY=-1.35 StartZ=0 EndX=-17.9 EndY=-1.35 EndZ=0
    g6: LineSegment StartX=-17.9 StartY=-1.35 StartZ=0 EndX=-17.9 EndY=0.65 EndZ=0
    g7: LineSegment StartX=-17.9 StartY=0.65 StartZ=0 EndX=-8 EndY=0.65 EndZ=0
    g8: LineSegment StartX=-8 StartY=0.65 StartZ=0 EndX=-6 EndY=1.45 EndZ=0
    g9: LineSegment StartX=-6 StartY=1.45 StartZ=0 EndX=-4.825 EndY=1.45 EndZ=0
    g10: LineSegment StartX=-4.825 StartY=1.45 StartZ=0 EndX=-4.825 EndY=2.625 EndZ=0
    g11: LineSegment StartX=-4.825 StartY=2.625 StartZ=0 EndX=-4 EndY=3.45 EndZ=0
    g12: LineSegment StartX=-4 StartY=3.45 StartZ=0 EndX=-2.85 EndY=3.45 EndZ=0
    g13: LineSegment StartX=-2.85 StartY=3.45 StartZ=0 EndX=-2.85 EndY=0 EndZ=0
    g14: LineSegment StartX=-2.85 StartY=0 StartZ=0 EndX=-1.5 EndY=0 EndZ=0
  constraints (45):
    c: Coincident(g0,g1)
    c: Coincident(g1,g2)
    c: Coincident(g2,g3)
    c: Coincident(g3,g4)
    c: Coincident(g4,g5)
    c: Coincident(g5,g6)
    c: Coincident(g6,g7)
    c: Coincident(g7,g8)
    c: Coincident(g8,g9)
    c: Coincident(g9,g10)
    c: Coincident(g10,g11)
    c: Coincident(g11,g12)
    c: Coincident(g12,g13)
    c: Coincident(g13,g14)
    c: Coincident(g14,g0)
    c: Horizontal(g5)
    c: Horizontal(g7)
    c: Horizontal(g9)
    c: Horizontal(g12)
    c: Vertical(g13)
    c: Horizontal(g14)
    c: Vertical(g0)
    c: Horizontal(g1)
    c: Vertical(g2)
    c: Horizontal(g3)
    c: Vertical(g10)
    c: Vertical(g6)
    c: DistanceY(g6,g6) = 2
    c: DistanceX(g6,g-1) = 17.9
    c: DistanceY(g3,g4) = 0.5
    c: DistanceX(g3,g3) = 1
    c: DistanceY(g2,g2) = 1
    c: DistanceX(g4,g3) = 0.5
    c: DistanceX(g1,g-1) = 3.85
    c: DistanceX(g0,g-1) = 1.5
    c: DistanceX(g7,g-1) = 8
    c: DistanceX(g8,g-1) = 6
    c: DistanceY(g7,g8) = 0.8
    c: DistanceX(g10,g-1) = 4.825
    c: DistanceX(g12,g-1) = 2.85
    c: DistanceX(g11,g-1) = 4
    c: DistanceY(g2,g12) = 5.3
    c: DistanceY(g13,g13) = 3.45
    c: Angle(g11,g12) = 2.35619
    c: PointOnObject(g0,g-1)
FEATURE [PartDesign::Revolution] Revolution004
  AllowMultiFace = false
  Angle = 360
  Axis = (0,2e-16,1)
  Base = (0,0,0)
  Placement = pos=(0,0,0) rot=(1,0,0;1.5708rad)
  Profile = -> Sketch039
  ReferenceAxis = -> Sketch039 [V_Axis]
FEATURE [PartDesign::Body] Body012  label="Servo Horn"
  Group = -> [Sketch039,Revolution004]
  Origin = -> Origin012
  Placement = pos=(-48,0,72.5) rot=(0,0,1;0rad)
  Tip = -> Revolution004
FEATURE [Sketcher::SketchObject] Sketch040
  FullyConstrained = false
  MapMode = 5
  Support = -> [XY_Plane013]
  sketch-geometry (4):
    g0: LineSegment StartX=-20.35 StartY=10.075 StartZ=0 EndX=20.35 EndY=10.075 EndZ=0
    g1: LineSegment StartX=20.35 StartY=10.075 StartZ=0 EndX=20.35 EndY=-10.075 EndZ=0
    g2: LineSegment StartX=20.35 StartY=-10.075 StartZ=0 EndX=-20.35 EndY=-10.075 EndZ=0
    g3: LineSegment StartX=-20.35 StartY=-10.075 StartZ=0 EndX=-20.35 EndY=10.075 EndZ=0
  constraints (11):
    c: Coincident(g0,g1)
    c: Coincident(g1,g2)
    c: Coincident(g2,g3)
    c: Coincident(g3,g0)
    c: Horizontal(g0)
    c: Horizontal(g2)
    c: Vertical(g1)
    c: Vertical(g3)
    c: Symmetric(g0,g1,g-1)
    c: DistanceX(g0,g0) = 40.7
    c: DistanceY(g3,g3) = 20.15
FEATURE [PartDesign::Pad] Pad020
  AllowMultiFace = false
  Direction = (1,1,1)
  Length = 29
  Length2 = 100
  Profile = -> Sketch040
  Reversed = true
  Type = 0
FEATURE [Sketcher::SketchObject] Sketch041
  FullyConstrained = false
  MapMode = 5
  Support = -> [Pad020]
  sketch-geometry (16):
    g0: LineSegment StartX=-27.2 StartY=10.075 StartZ=0 EndX=27.2 EndY=10.075 EndZ=0
    g1: LineSegment StartX=27.2 StartY=10.075 StartZ=0 EndX=27.2 EndY=6 EndZ=0
    g2: LineSegment StartX=-27.2 StartY=10.075 StartZ=0 EndX=-27.2 EndY=6 EndZ=0
    g3: LineSegment StartX=-27.2 StartY=4 StartZ=0 EndX=-27.2 EndY=-4 EndZ=0
    g4: LineSegment StartX=27.2 StartY=4 StartZ=0 EndX=27.2 EndY=-4 EndZ=0
    g5: LineSegment StartX=27.2 StartY=-6 StartZ=0 EndX=27.2 EndY=-10.075 EndZ=0
    g6: LineSegment StartX=27.2 StartY=-10.075 StartZ=0 EndX=-27.2 EndY=-10.075 EndZ=0
    g7: LineSegment StartX=-27.2 StartY=-10.075 StartZ=0 EndX=-27.2 EndY=-6 EndZ=0
    g8: ArcOfCircle CenterX=-24.5 CenterY=5 CenterZ=0 NormalX=0 NormalY=0 NormalZ=1 AngleXU=0 Radius=2.87924 StartAngle=3.4963 EndAngle=9.07007
    g9: ArcOfCircle CenterX=-24.5 CenterY=-5 CenterZ=0 NormalX=0 NormalY=0 NormalZ=1 AngleXU=0 Radius=2.87924 StartAngle=3.4963 EndAngle=9.07007
    g10: ArcOfCircle CenterX=24.5 CenterY=5 CenterZ=0 NormalX=0 NormalY=0 NormalZ=1 AngleXU=0 Radius=2.87924 StartAngle=0.354706 EndAngle=5.92848
    g11: ArcOfCircle CenterX=24.5 CenterY=-5 CenterZ=0 NormalX=0 NormalY=0 NormalZ=1 AngleXU=0 Radius=2.87924 StartAngle=0.354706 EndAngle=5.92848
    g12: LineSegment StartX=-24.5 StartY=5 StartZ=0 EndX=24.5 EndY=5 EndZ=0
    g13: LineSegment StartX=24.5 StartY=5 StartZ=0 EndX=24.5 EndY=-5 EndZ=0
    g14: LineSegment StartX=24.5 StartY=-5 StartZ=0 EndX=-24.5 EndY=-5 EndZ=0
    g15: LineSegment StartX=-24.5 StartY=-5 StartZ=0 EndX=-24.5 EndY=5 EndZ=0
  constraints (46):
    c: Coincident(g0,g1)
    c: Coincident(g5,g6)
    c: Coincident(g6,g7)
    c: Horizontal(g0)
    c: Horizontal(g6)
    c: Vertical(g4)
    c: Vertical(g1)
    c: Vertical(g5)
    c: Vertical(g7)
    c: Vertical(g3)
    c: Vertical(g2)
    c: Vertical(g7,g3)
    c: Vertical(g3,g2)
    c: Coincident(g2,g0)
    c: Vertical(g1,g4)
    c: Vertical(g4,g5)
    c: DistanceX(g0,g0) = 54.4
    c: Coincident(g10,g1)
    c: Coincident(g10,g4)
    c: Coincident(g11,g4)
    c: Coincident(g11,g5)
    c: Coincident(g9,g7)
    c: Coincident(g9,g3)
    c: Coincident(g8,g3)
    c: Coincident(g8,g2)
    c: Symmetric(g0,g5,g-1)
    c: DistanceY(g6,g0) = 20.15
    c: Equal(g9,g8)
    c: Equal(g8,g10)
    c: Equal(g10,g11)
    c: Coincident(g12,g13)
    c: Coincident(g13,g14)
    c: Coincident(g14,g15)
    c: Coincident(g15,g12)
    c: Horizontal(g12)
    c: Horizontal(g14)
    c: Vertical(g13)
    c: Vertical(g15)
    c: Symmetric(g12,g13,g-1)
    c: DistanceX(g12,g12) = 49
    c: Coincident(g8,g12)
    c: Coincident(g9,g14)
    c: Coincident(g11,g13)
    c: Coincident(g10,g12)
    c: DistanceY(g15,g15) = 10
    c: DistanceY(g3,g2) = 2
FEATURE [PartDesign::Pad] Pad021
  AllowMultiFace = false
  BaseFeature = -> Pad020
  Direction = (1,1,1)
  Length = 2.55
  Length2 = 100
  Profile = -> Sketch041
  Type = 0
FEATURE [Sketcher::SketchObject] Sketch042
  FullyConstrained = false
  MapMode = 5
  Placement = pos=(0,0,2.55) rot=(0,0,1;0rad)
  Support = -> [Pad021]
  sketch-geometry (4):
    g0: LineSegment StartX=-20.35 StartY=10.075 StartZ=0 EndX=20.35 EndY=10.075 EndZ=0
    g1: LineSegment StartX=20.35 StartY=10.075 StartZ=0 EndX=20.35 EndY=-10.075 EndZ=0
    g2: LineSegment StartX=20.35 StartY=-10.075 StartZ=0 EndX=-20.35 EndY=-10.075 EndZ=0
    g3: LineSegment StartX=-20.35 StartY=-10.075 StartZ=0 EndX=-20.35 EndY=10.075 EndZ=0
  constraints (11):
    c: Coincident(g0,g1)
    c: Coincident(g1,g2)
    c: Coincident(g2,g3)
    c: Coincident(g3,g0)
    c: Horizontal(g0)
    c: Horizontal(g2)
    c: Vertical(g1)
    c: Vertical(g3)
    c: Symmetric(g1,g0,g-1)
    c: DistanceX(g0,g0) = 40.7
    c: DistanceY(g3,g3) = 20.15
FEATURE [PartDesign::Pad] Pad022
  AllowMultiFace = false
  BaseFeature = -> Pad021
  Direction = (1,1,1)
  Length = 5.5
  Length2 = 100
  Profile = -> Sketch042
  Type = 0
FEATURE [Sketcher::SketchObject] Sketch043
  FullyConstrained = false
  MapMode = 5
  Placement = pos=(0,0,8.05) rot=(0,0,1;0rad)
  Support = -> [Pad022]
  sketch-geometry (7):
    g0: ArcOfCircle CenterX=10.35 CenterY=0 CenterZ=0 NormalX=0 NormalY=0 NormalZ=1 AngleXU=0 Radius=10 StartAngle=4.26136 EndAngle=8.30501
    g1: LineSegment StartX=5.9911 StartY=9 StartZ=0 EndX=-14.85 EndY=9 EndZ=0
    g2: LineSegment StartX=-14.85 StartY=9 StartZ=0 EndX=-14.85 EndY=5 EndZ=0
    g3: LineSegment StartX=-14.85 StartY=-5 StartZ=0 EndX=-14.85 EndY=-9 EndZ=0
    g4: LineSegment StartX=-14.85 StartY=-9 StartZ=0 EndX=5.9911 EndY=-9 EndZ=0
    g5: ArcOfCircle CenterX=-11.1 CenterY=0 CenterZ=0 NormalX=0 NormalY=0 NormalZ=1 AngleXU=0 Radius=6.25 StartAngle=3.14159 EndAngle=4.06889
    g6: ArcOfCircle CenterX=-11.1 CenterY=0 CenterZ=0 NormalX=0 NormalY=0 NormalZ=1 AngleXU=0 Radius=6.25 StartAngle=2.2143 EndAngle=3.14159
  constraints (23):
    c: PointOnObject(g0,g-1)
    c: Diameter(g0) = 20
    c: DistanceX(g-1,g0) = 10.35
    c: Coincident(g1,g2)
    c: Coincident(g3,g4)
    c: Coincident(g1,g0)
    c: Coincident(g4,g0)
    c: Horizontal(g4)
    c: Horizontal(g1)
    c: Vertical(g2)
    c: Vertical(g3)
    c: DistanceX(g3,g-1) = 14.85
    c: Equal(g1,g4)
    c: Vertical(g3,g2)
    c: DistanceY(g3,g1) = 18
    c: Coincident(g6,g2)
    c: Coincident(g5,g3)
    c: Coincident(g6,g5)
    c: Tangent(g6,g5) = -1.5708
    c: PointOnObject(g5,g-1)
    c: PointOnObject(g5,g-1)
    c: DistanceX(g5,g-1) = 17.35
    c: DistanceY(g3,g2) = 10
FEATURE [PartDesign::Pad] Pad023
  AllowMultiFace = false
  BaseFeature = -> Pad022
  Direction = (1,1,1)
  Length = 2
  Length2 = 100
  Profile = -> Sketch043
  Type = 0
FEATURE [Sketcher::SketchObject] Sketch044
  FullyConstrained = false
  MapMode = 5
  Placement = pos=(0,0,10.05) rot=(0,0,1;0rad)
  Support = -> [Pad023]
  sketch-geometry (1):
    g0: Circle CenterX=10.35 CenterY=0 CenterZ=0 NormalX=0 NormalY=0 NormalZ=1 AngleXU=0 Radius=6.5
  constraints (3):
    c: PointOnObject(g0,g-1)
    c: DistanceX(g-1,g0) = 10.35
    c: Diameter(g0) = 13
FEATURE [PartDesign::Pad] Pad024
  AllowMultiFace = false
  BaseFeature = -> Pad023
  Direction = (1,1,1)
  Length = 1.3
  Length2 = 100
  Profile = -> Sketch044
  Type = 0
FEATURE [Sketcher::SketchObject] Sketch045
  FullyConstrained = false
  MapMode = 5
  Placement = pos=(0,0,11.35) rot=(0,0,1;0rad)
  Support = -> [Pad024]
  sketch-geometry (1):
    g0: Circle CenterX=10.35 CenterY=0 CenterZ=0 NormalX=0 NormalY=0 NormalZ=1 AngleXU=0 Radius=5.5
  constraints (3):
    c: PointOnObject(g0,g-1)
    c: Diameter(g0) = 11
    c: DistanceX(g-1,g0) = 10.35
FEATURE [PartDesign::Pad] Pad025
  AllowMultiFace = false
  BaseFeature = -> Pad024
  Direction = (1,1,1)
  Length = 0.7
  Length2 = 100
  Profile = -> Sketch045
  Type = 0
FEATURE [Sketcher::SketchObject] Sketch046
  FullyConstrained = false
  MapMode = 5
  Placement = pos=(0,0,12.05) rot=(0,0,1;0rad)
  Support = -> [Pad025]
  sketch-geometry (1):
    g0: Circle CenterX=10.35 CenterY=0 CenterZ=0 NormalX=0 NormalY=0 NormalZ=1 AngleXU=0 Radius=3
  constraints (3):
    c: PointOnObject(g0,g-1)
    c: DistanceX(g-1,g0) = 10.35
    c: Diameter(g0) = 6
FEATURE [PartDesign::Pad] Pad026
  AllowMultiFace = false
  BaseFeature = -> Pad025
  Direction = (1,1,1)
  Length = 3.5
  Length2 = 100
  Profile = -> Sketch046
  Type = 0
FEATURE [PartDesign::Body] Body013  label="MG996"
  Group = -> [Sketch040,Pad020,Sketch041,Pad021,Sketch042,Pad022,Sketch043,Pad023,Sketch044,Pad024,Sketch045,Pad025,Sketch046,Pad026]
  Origin = -> Origin013
  Placement = pos=(-58.5,-1e-15,88.5) rot=(1,0,0;3.14159rad)
  Tip = -> Pad026
FEATURE [Sketcher::SketchObject] Sketch047
  FullyConstrained = false
  MapMode = 5
  Placement = pos=(0,0,5) rot=(0,0,1;0rad)
  Support = -> [Pad018]
  sketch-geometry (9):
    g0: Circle CenterX=0 CenterY=0 CenterZ=0 NormalX=0 NormalY=0 NormalZ=1 AngleXU=0 Radius=3.25
    g1: LineSegment StartX=-10 StartY=10 StartZ=0 EndX=10 EndY=10 EndZ=0
    g2: LineSegment StartX=10 StartY=10 StartZ=0 EndX=10 EndY=-10 EndZ=0
    g3: LineSegment StartX=10 StartY=-10 StartZ=0 EndX=-10 EndY=-10 EndZ=0
    g4: LineSegment StartX=-10 StartY=-10 StartZ=0 EndX=-10 EndY=10 EndZ=0
    g5: Circle CenterX=-10 CenterY=10 CenterZ=0 NormalX=0 NormalY=0 NormalZ=1 AngleXU=0 Radius=1.75
    g6: Circle CenterX=10 CenterY=10 CenterZ=0 NormalX=0 NormalY=0 NormalZ=1 AngleXU=0 Radius=1.75
    g7: Circle CenterX=10 CenterY=-10 CenterZ=0 NormalX=0 NormalY=0 NormalZ=1 AngleXU=0 Radius=1.75
    g8: Circle CenterX=-10 CenterY=-10 CenterZ=0 NormalX=0 NormalY=0 NormalZ=1 AngleXU=0 Radius=1.75
  constraints (21):
    c: Coincident(g0,g-1)
    c: Diameter(g0) = 6.5
    c: Coincident(g1,g2)
    c: Coincident(g2,g3)
    c: Coincident(g3,g4)
    c: Coincident(g4,g1)
    c: Horizontal(g1)
    c: Horizontal(g3)
    c: Vertical(g2)
    c: Vertical(g4)
    c: DistanceX(g3,g3) = 20
    c: DistanceY(g4,g4) = 20
    c: Symmetric(g2,g1,g0)
    c: Coincident(g8,g3)
    c: Coincident(g7,g2)
    c: Coincident(g6,g1)
    c: Coincident(g5,g1)
    c: Diameter(g5) = 3.5
    c: Equal(g5,g8)
    c: Equal(g5,g6)
    c: Equal(g5,g7)
FEATURE [PartDesign::Pocket] Pocket013
  AllowMultiFace = false
  BaseFeature = -> Pad018
  Length = 5
  Length2 = 100
  Profile = -> Sketch047
  Type = 0
FEATURE [PartDesign::Body] Body009  label="Wheel Gear"
  Group = -> [InvoluteGear,Pad018,Sketch047,Pocket013]
  Origin = -> Origin009
  Placement = pos=(0,0,68) rot=(0,0,1;0rad)
  Tip = -> Pocket013
FEATURE [Sketcher::SketchObject] Sketch048
  FullyConstrained = false
  MapMode = 5
  Support = -> [XY_Plane014]
  sketch-geometry (1):
    g0: Circle CenterX=0 CenterY=0 CenterZ=0 NormalX=0 NormalY=0 NormalZ=1 AngleXU=0 Radius=2.95
  constraints (2):
    c: Coincident(g0,g-1)
    c: Diameter(g0) = 5.9
FEATURE [PartDesign::Pad] Pad027
  AllowMultiFace = false
  Direction = (1,1,1)
  Length = 70
  Length2 = 100
  Profile = -> Sketch048
  Type = 0
FEATURE [Sketcher::SketchObject] Sketch049
  FullyConstrained = false
  MapMode = 5
  Placement = pos=(0,0,0) rot=(1,0,0;3.14159rad)
  Support = -> [Pad027]
  sketch-geometry (7):
    g0: LineSegment StartX=-3.917e-13 StartY=5.7735 StartZ=0 EndX=-5 EndY=2.88675 EndZ=0
    g1: LineSegment StartX=-5 StartY=2.88675 StartZ=0 EndX=-5 EndY=-2.88675 EndZ=0
    g2: LineSegment StartX=-5 StartY=-2.88675 StartZ=0 EndX=0 EndY=-5.7735 EndZ=0
    g3: LineSegment StartX=0 StartY=-5.7735 StartZ=0 EndX=5 EndY=-2.88675 EndZ=0
    g4: LineSegment StartX=5 StartY=-2.88675 StartZ=0 EndX=5 EndY=2.88675 EndZ=0
    g5: LineSegment StartX=5 StartY=2.88675 StartZ=0 EndX=-3.917e-13 EndY=5.7735 EndZ=0
    g6: Circle CenterX=0 CenterY=0 CenterZ=0 NormalX=0 NormalY=0 NormalZ=1 AngleXU=0 Radius=5.7735
  constraints (16):
    c: Coincident(g0,g1)
    c: Coincident(g1,g2)
    c: Coincident(g2,g3)
    c: Coincident(g3,g4)
    c: Coincident(g4,g5)
    c: Coincident(g5,g0)
    c: Equal(g0, g1-g5) x5
    c: PointOnObject(g0,g6)
    c: PointOnObject(g1,g6)
    c: PointOnObject(g2,g6)
    c: PointOnObject(g3,g6)
    c: PointOnObject(g4,g6)
    c: PointOnObject(g5,g6)
    c: Coincident(g6,g-1)
    c: Distance(g0,g4) = 10
    c: PointOnObject(g2,g-2)
FEATURE [PartDesign::Pad] Pad028
  AllowMultiFace = false
  BaseFeature = -> Pad027
  Direction = (1,1,1)
  Length = 4
  Length2 = 100
  Profile = -> Sketch049
  Type = 0
FEATURE [PartDesign::Body] Body014  label="M6x70_Hex_Head"
  Group = -> [Sketch048,Pad027,Sketch049,Pad028]
  Origin = -> Origin014
  Placement = pos=(0,0,65) rot=(0,0,1;0rad)
  Tip = -> Pad028
FEATURE [Sketcher::SketchObject] Sketch050
  FullyConstrained = false
  MapMode = 5
  Support = -> [XY_Plane015]
  sketch-geometry (2):
    g0: Circle CenterX=0 CenterY=0 CenterZ=0 NormalX=0 NormalY=0 NormalZ=1 AngleXU=0 Radius=5.85
    g1: Circle CenterX=0 CenterY=0 CenterZ=0 NormalX=0 NormalY=0 NormalZ=1 AngleXU=0 Radius=3
  constraints (4):
    c: Coincident(g1,g0)
    c: Coincident(g1,g-1)
    c: Diameter(g1) = 6
    c: Diameter(g0) = 11.7
FEATURE [PartDesign::Pad] Pad029
  AllowMultiFace = false
  Direction = (1,1,1)
  Length = 1.5
  Length2 = 100
  Profile = -> Sketch050
  Type = 0
FEATURE [PartDesign::Body] Body015  label="M6_Washer"
  Group = -> [Sketch050,Pad029]
  Origin = -> Origin015
  Placement = pos=(0,0,73) rot=(0,0,1;0rad)
  Tip = -> Pad029
FEATURE [Sketcher::SketchObject] Sketch051
  FullyConstrained = false
  MapMode = 5
  Support = -> [XY_Plane016]
  sketch-geometry (8):
    g0: LineSegment StartX=0 StartY=5.7735 StartZ=0 EndX=-5 EndY=2.88675 EndZ=0
    g1: LineSegment StartX=-5 StartY=2.88675 StartZ=0 EndX=-5 EndY=-2.88675 EndZ=0
    g2: LineSegment StartX=-5 StartY=-2.88675 StartZ=0 EndX=-1.501e-13 EndY=-5.7735 EndZ=0
    g3: LineSegment StartX=-1.501e-13 StartY=-5.7735 StartZ=0 EndX=5 EndY=-2.88675 EndZ=0
    g4: LineSegment StartX=5 StartY=-2.88675 StartZ=0 EndX=5 EndY=2.88675 EndZ=0
    g5: LineSegment StartX=5 StartY=2.88675 StartZ=0 EndX=0 EndY=5.7735 EndZ=0
    g6: Circle CenterX=0 CenterY=0 CenterZ=0 NormalX=0 NormalY=0 NormalZ=1 AngleXU=0 Radius=5.7735
    g7: Circle CenterX=0 CenterY=0 CenterZ=0 NormalX=0 NormalY=0 NormalZ=1 AngleXU=0 Radius=3
  constraints (18):
    c: Coincident(g0,g1)
    c: Coincident(g1,g2)
    c: Coincident(g2,g3)
    c: Coincident(g3,g4)
    c: Coincident(g4,g5)
    c: Coincident(g5,g0)
    c: Equal(g0, g1-g5) x5
    c: PointOnObject(g0,g6)
    c: PointOnObject(g1,g6)
    c: PointOnObject(g2,g6)
    c: PointOnObject(g3,g6)
    c: PointOnObject(g4,g6)
    c: PointOnObject(g5,g6)
    c: Coincident(g6,g-1)
    c: PointOnObject(g0,g-2)
    c: Distance(g0,g4) = 10
    c: Coincident(g7,g-1)
    c: Diameter(g7) = 6
FEATURE [PartDesign::Pad] Pad030
  AllowMultiFace = false
  Direction = (1,1,1)
  Length = 5
  Length2 = 100
  Profile = -> Sketch051
  Type = 0
FEATURE [PartDesign::Body] Body016  label="M6_Full_Nut"
  Group = -> [Sketch051,Pad030]
  Origin = -> Origin016
  Placement = pos=(0,0,74.5) rot=(0,0,1;0rad)
  Tip = -> Pad030
FEATURE [Sketcher::SketchObject] Sketch052
  FullyConstrained = false
  MapMode = 5
  Support = -> [XY_Plane017]
  sketch-geometry (2):
    g0: Circle CenterX=0 CenterY=0 CenterZ=0 NormalX=0 NormalY=0 NormalZ=1 AngleXU=0 Radius=9.5
    g1: Circle CenterX=0 CenterY=0 CenterZ=0 NormalX=0 NormalY=0 NormalZ=1 AngleXU=0 Radius=3
  constraints (4):
    c: Coincident(g0,g-1)
    c: Coincident(g0,g1)
    c: Diameter(g1) = 6
    c: Diameter(g0) = 19
FEATURE [PartDesign::Pad] Pad031
  AllowMultiFace = false
  Direction = (1,1,1)
  Length = 6
  Length2 = 100
  Profile = -> Sketch052
  Type = 0
FEATURE [PartDesign::Body] Body017  label="6mm_bearing"
  Group = -> [Sketch052,Pad031]
  Origin = -> Origin017
  Placement = pos=(0,0,81) rot=(0,0,1;0rad)
  Tip = -> Pad031
FEATURE [Sketcher::SketchObject] Sketch053
  FullyConstrained = false
  MapMode = 5
  Support = -> [XY_Plane018]
  sketch-geometry (2):
    g0: Circle CenterX=0 CenterY=0 CenterZ=0 NormalX=0 NormalY=0 NormalZ=1 AngleXU=0 Radius=5.85
    g1: Circle CenterX=0 CenterY=0 CenterZ=0 NormalX=0 NormalY=0 NormalZ=1 AngleXU=0 Radius=3
  constraints (4):
    c: Coincident(g1,g0)
    c: Coincident(g1,g-1)
    c: Diameter(g1) = 6
    c: Diameter(g0) = 11.7
FEATURE [PartDesign::Pad] Pad032
  AllowMultiFace = false
  Direction = (1,1,1)
  Length = 1.5
  Length2 = 100
  Profile = -> Sketch053
  Type = 0
FEATURE [PartDesign::Body] Body018  label="M6_Washer001"
  Group = -> [Sketch053,Pad032]
  Origin = -> Origin018
  Placement = pos=(0,0,79.5) rot=(0,0,1;0rad)
  Tip = -> Pad032
FEATURE [Sketcher::SketchObject] Sketch054
  FullyConstrained = false
  MapMode = 5
  Placement = pos=(0,0,0) rot=(1,0,0;1.5708rad)
  Support = -> [XZ_Plane019]
  sketch-geometry (8):
    g0: LineSegment StartX=-20.5 StartY=40 StartZ=0 EndX=-20.5 EndY=0 EndZ=0
    g1: LineSegment StartX=-20.5 StartY=0 StartZ=0 EndX=13.5 EndY=0 EndZ=0
    g2: LineSegment StartX=13.5 StartY=0 StartZ=0 EndX=13.5 EndY=9 EndZ=0
    g3: LineSegment StartX=13.5 StartY=9 StartZ=0 EndX=20.8 EndY=9 EndZ=0
    g4: LineSegment StartX=20.8 StartY=9 StartZ=0 EndX=20.8 EndY=14 EndZ=0
    g5: LineSegment StartX=20.8 StartY=14 StartZ=0 EndX=13.5 EndY=14 EndZ=0
    g6: LineSegment StartX=13.5 StartY=14 StartZ=0 EndX=13.5 EndY=40 EndZ=0
    g7: LineSegment StartX=13.5 StartY=40 StartZ=0 EndX=-20.5 EndY=40 EndZ=0
  constraints (24):
    c: Coincident(g0,g1)
    c: Coincident(g1,g2)
    c: Coincident(g2,g3)
    c: Coincident(g3,g4)
    c: Coincident(g4,g5)
    c: Coincident(g5,g6)
    c: Coincident(g6,g7)
    c: Coincident(g7,g0)
    c: Horizontal(g7)
    c: Horizontal(g1)
    c: Horizontal(g3)
    c: Horizontal(g5)
    c: Vertical(g6)
    c: Vertical(g2)
    c: Vertical(g4)
    c: Vertical(g0)
    c: Equal(g1,g7)
    c: PointOnObject(g-1,g1)
    c: DistanceX(g1,g1) = 34
    c: DistanceY(g2,g2) = 9
    c: DistanceX(g-1,g1) = 13.5
    c: DistanceX(g3,g3) = 7.3
    c: DistanceY(g4,g4) = 5
    c: DistanceY(g0,g0) = 40
FEATURE [PartDesign::Pad] Pad033
  AllowMultiFace = false
  Direction = (1,1,1)
  Length = 22
  Length2 = 100
  Midplane = true
  Placement = pos=(0,0,0) rot=(1,0,0;1.5708rad)
  Profile = -> Sketch054
  Type = 0
FEATURE [Sketcher::SketchObject] Sketch055
  FullyConstrained = true
  MapMode = 5
  Placement = pos=(0,0,0) rot=(1,0,0;3.14159rad)
  Support = -> [Pad033]
  sketch-geometry (1):
    g0: Circle CenterX=0 CenterY=0 CenterZ=0 NormalX=0 NormalY=0 NormalZ=1 AngleXU=0 Radius=9.75
  constraints (2):
    c: Coincident(g0,g-1)
    c: Diameter(g0) = 19.5
FEATURE [PartDesign::Pocket] Pocket014
  AllowMultiFace = false
  BaseFeature = -> Pad033
  Length = 6
  Length2 = 100
  Placement = pos=(0,0,0) rot=(1,0,0;1.5708rad)
  Profile = -> Sketch055
  Type = 0
FEATURE [Sketcher::SketchObject] Sketch056
  FullyConstrained = true
  MapMode = 5
  Placement = pos=(0,2.6e-15,6) rot=(1,0,0;3.14159rad)
  Support = -> [Pocket014]
  sketch-geometry (1):
    g0: Circle CenterX=0 CenterY=0 CenterZ=0 NormalX=0 NormalY=0 NormalZ=1 AngleXU=0 Radius=5.5
  constraints (2):
    c: Coincident(g0,g-1)
    c: Diameter(g0) = 11
FEATURE [PartDesign::Pocket] Pocket015
  AllowMultiFace = false
  BaseFeature = -> Pocket014
  Length = 40
  Length2 = 100
  Placement = pos=(0,0,0) rot=(1,0,0;1.5708rad)
  Profile = -> Sketch056
  Type = 0
FEATURE [Sketcher::SketchObject] Sketch057
  FullyConstrained = true
  MapMode = 5
  Placement = pos=(0,1.76e-14,40) rot=(0,0,1;3.14159rad)
  Support = -> [Pocket015]
  sketch-geometry (1):
    g0: Circle CenterX=0 CenterY=0 CenterZ=0 NormalX=0 NormalY=0 NormalZ=1 AngleXU=0 Radius=9.75
  constraints (2):
    c: Coincident(g0,g-1)
    c: Diameter(g0) = 19.5
FEATURE [PartDesign::Pocket] Pocket016
  AllowMultiFace = false
  BaseFeature = -> Pocket015
  Length = 6
  Length2 = 100
  Placement = pos=(0,0,0) rot=(1,0,0;1.5708rad)
  Profile = -> Sketch057
  Type = 0
FEATURE [Sketcher::SketchObject] Sketch058
  FullyConstrained = true
  MapMode = 5
  Placement = pos=(0,-11,2.4e-15) rot=(1,0,0;1.5708rad)
  Support = -> [Pocket016]
  sketch-geometry (3):
    g0: Circle CenterX=-15 CenterY=32.5 CenterZ=0 NormalX=0 NormalY=0 NormalZ=1 AngleXU=0 Radius=2.25
    g1: Circle CenterX=-15 CenterY=7.5 CenterZ=0 NormalX=0 NormalY=0 NormalZ=1 AngleXU=0 Radius=2.25
    g2: LineSegment StartX=-15 StartY=32.5 StartZ=0 EndX=-15 EndY=7.5 EndZ=0
  constraints (8):
    c: Vertical(g2)
    c: Coincident(g2,g0)
    c: Coincident(g1,g2)
    c: DistanceY(g2,g2) = 25
    c: Diameter(g0) = 4.5
    c: Equal(g0,g1)
    c: DistanceX(g1,g-1) = 15
    c: DistanceY(g-1,g1) = 7.5
FEATURE [PartDesign::Pocket] Pocket017
  AllowMultiFace = false
  BaseFeature = -> Pocket016
  Length = 25
  Length2 = 100
  Placement = pos=(0,0,0) rot=(1,0,0;1.5708rad)
  Profile = -> Sketch058
  Type = 0
FEATURE [Sketcher::SketchObject] Sketch059
  FullyConstrained = true
  MapMode = 5
  Placement = pos=(0,4e-15,9) rot=(1,0,0;3.14159rad)
  Support = -> [Pocket017]
  sketch-geometry (6):
    g0: Circle CenterX=16.95 CenterY=5 CenterZ=0 NormalX=0 NormalY=0 NormalZ=1 AngleXU=0 Radius=1.5
    g1: Circle CenterX=16.95 CenterY=-5 CenterZ=0 NormalX=0 NormalY=0 NormalZ=1 AngleXU=0 Radius=1.5
    g2: LineSegment StartX=0 StartY=5 StartZ=0 EndX=16.95 EndY=5 EndZ=0
    g3: LineSegment StartX=16.95 StartY=5 StartZ=0 EndX=16.95 EndY=-5 EndZ=0
    g4: LineSegment StartX=16.95 StartY=-5 StartZ=0 EndX=0 EndY=-5 EndZ=0
    g5: LineSegment StartX=0 StartY=-5 StartZ=0 EndX=0 EndY=5 EndZ=0
  constraints (15):
    c: Coincident(g2,g3)
    c: Coincident(g3,g4)
    c: Coincident(g4,g5)
    c: Coincident(g5,g2)
    c: Horizontal(g2)
    c: Horizontal(g4)
    c: Vertical(g3)
    c: Vertical(g5)
    c: Symmetric(g2,g4,g-1)
    c: DistanceY(g3,g3) = 10
    c: DistanceX(g2,g2) = 16.95
    c: Coincident(g0,g2)
    c: Coincident(g1,g3)
    c: Diameter(g1) = 3
    c: Equal(g1,g0)
FEATURE [PartDesign::Pocket] Pocket018
  AllowMultiFace = false
  BaseFeature = -> Pocket017
  Length = 5
  Length2 = 100
  Placement = pos=(0,0,0) rot=(1,0,0;1.5708rad)
  Profile = -> Sketch059
  Type = 0
FEATURE [PartDesign::Body] Body019  label="End_Bearing_Block"
  Group = -> [Sketch054,Pad033,Sketch055,Pocket014,Sketch056,Pocket015,Sketch057,Pocket016,Sketch058,Pocket017,Sketch059,Pocket018]
  Origin = -> Origin019
  Placement = pos=(-100,0,81) rot=(0,0,1;0rad)
  Tip = -> Pocket018
FEATURE [Sketcher::SketchObject] Sketch060
  FullyConstrained = false
  MapMode = 5
  Support = -> [XY_Plane020]
  sketch-geometry (2):
    g0: Circle CenterX=0 CenterY=0 CenterZ=0 NormalX=0 NormalY=0 NormalZ=1 AngleXU=0 Radius=9.5
    g1: Circle CenterX=0 CenterY=0 CenterZ=0 NormalX=0 NormalY=0 NormalZ=1 AngleXU=0 Radius=3
  constraints (4):
    c: Coincident(g0,g-1)
    c: Coincident(g0,g1)
    c: Diameter(g1) = 6
    c: Diameter(g0) = 19
FEATURE [PartDesign::Pad] Pad034
  AllowMultiFace = false
  Direction = (1,1,1)
  Length = 6
  Length2 = 100
  Profile = -> Sketch060
  Type = 0
FEATURE [PartDesign::Body] Body020  label="6mm_bearing001"
  Group = -> [Sketch060,Pad034]
  Origin = -> Origin020
  Placement = pos=(0,0,115) rot=(0,0,1;0rad)
  Tip = -> Pad034
FEATURE [Sketcher::SketchObject] Sketch061
  FullyConstrained = false
  MapMode = 5
  Support = -> [XY_Plane021]
  sketch-geometry (2):
    g0: Circle CenterX=0 CenterY=0 CenterZ=0 NormalX=0 NormalY=0 NormalZ=1 AngleXU=0 Radius=5.85
    g1: Circle CenterX=0 CenterY=0 CenterZ=0 NormalX=0 NormalY=0 NormalZ=1 AngleXU=0 Radius=3
  constraints (4):
    c: Coincident(g1,g0)
    c: Coincident(g1,g-1)
    c: Diameter(g1) = 6
    c: Diameter(g0) = 11.7
FEATURE [PartDesign::Pad] Pad035
  AllowMultiFace = false
  Direction = (1,1,1)
  Length = 1.5
  Length2 = 100
  Profile = -> Sketch061
  Type = 0
FEATURE [PartDesign::Body] Body021  label="M6_Washer002"
  Group = -> [Sketch061,Pad035]
  Origin = -> Origin021
  Placement = pos=(0,0,121) rot=(0,0,1;0rad)
  Tip = -> Pad035
FEATURE [Sketcher::SketchObject] Sketch062
  FullyConstrained = false
  MapMode = 5
  Support = -> [XY_Plane022]
  sketch-geometry (8):
    g0: LineSegment StartX=0 StartY=5.7735 StartZ=0 EndX=-5 EndY=2.88675 EndZ=0
    g1: LineSegment StartX=-5 StartY=2.88675 StartZ=0 EndX=-5 EndY=-2.88675 EndZ=0
    g2: LineSegment StartX=-5 StartY=-2.88675 StartZ=0 EndX=-1.501e-13 EndY=-5.7735 EndZ=0
    g3: LineSegment StartX=-1.501e-13 StartY=-5.7735 StartZ=0 EndX=5 EndY=-2.88675 EndZ=0
    g4: LineSegment StartX=5 StartY=-2.88675 StartZ=0 EndX=5 EndY=2.88675 EndZ=0
    g5: LineSegment StartX=5 StartY=2.88675 StartZ=0 EndX=0 EndY=5.7735 EndZ=0
    g6: Circle CenterX=0 CenterY=0 CenterZ=0 NormalX=0 NormalY=0 NormalZ=1 AngleXU=0 Radius=5.7735
    g7: Circle CenterX=0 CenterY=0 CenterZ=0 NormalX=0 NormalY=0 NormalZ=1 AngleXU=0 Radius=3
  constraints (18):
    c: Coincident(g0,g1)
    c: Coincident(g1,g2)
    c: Coincident(g2,g3)
    c: Coincident(g3,g4)
    c: Coincident(g4,g5)
    c: Coincident(g5,g0)
    c: Equal(g0, g1-g5) x5
    c: PointOnObject(g0,g6)
    c: PointOnObject(g1,g6)
    c: PointOnObject(g2,g6)
    c: PointOnObject(g3,g6)
    c: PointOnObject(g4,g6)
    c: PointOnObject(g5,g6)
    c: Coincident(g6,g-1)
    c: PointOnObject(g0,g-2)
    c: Distance(g0,g4) = 10
    c: Coincident(g7,g-1)
    c: Diameter(g7) = 6
FEATURE [PartDesign::Pad] Pad036
  AllowMultiFace = false
  Direction = (1,1,1)
  Length = 5
  Length2 = 100
  Profile = -> Sketch062
  Type = 0
FEATURE [PartDesign::Body] Body022  label="M6_Full_Nut001"
  Group = -> [Sketch062,Pad036]
  Origin = -> Origin022
  Placement = pos=(0,0,122.5) rot=(0,0,1;0rad)
  Tip = -> Pad036
FEATURE [Sketcher::SketchObject] Sketch063
  FullyConstrained = true
  MapMode = 5
  Placement = pos=(0,0,0) rot=(1,0,0;1.5708rad)
  Support = -> [XZ_Plane027]
  sketch-geometry (8):
    g0: LineSegment StartX=-1.5 StartY=40 StartZ=0 EndX=-1.5 EndY=0 EndZ=0
    g1: LineSegment StartX=-1.5 StartY=0 StartZ=0 EndX=13.5 EndY=0 EndZ=0
    g2: LineSegment StartX=13.5 StartY=0 StartZ=0 EndX=13.5 EndY=9 EndZ=0
    g3: LineSegment StartX=13.5 StartY=9 StartZ=0 EndX=20.8 EndY=9 EndZ=0
    g4: LineSegment StartX=20.8 StartY=9 StartZ=0 EndX=20.8 EndY=14 EndZ=0
    g5: LineSegment StartX=20.8 StartY=14 StartZ=0 EndX=13.5 EndY=14 EndZ=0
    g6: LineSegment StartX=13.5 StartY=14 StartZ=0 EndX=13.5 EndY=40 EndZ=0
    g7: LineSegment StartX=13.5 StartY=40 StartZ=0 EndX=-1.5 EndY=40 EndZ=0
  constraints (24):
    c: Coincident(g0,g1)
    c: Coincident(g1,g2)
    c: Coincident(g2,g3)
    c: Coincident(g3,g4)
    c: Coincident(g4,g5)
    c: Coincident(g5,g6)
    c: Coincident(g6,g7)
    c: Coincident(g7,g0)
    c: Horizontal(g7)
    c: Horizontal(g1)
    c: Horizontal(g3)
    c: Horizontal(g5)
    c: Vertical(g6)
    c: Vertical(g2)
    c: Vertical(g4)
    c: Vertical(g0)
    c: Equal(g1,g7)
    c: PointOnObject(g-1,g1)
    c: DistanceX(g1,g1) = 15
    c: DistanceY(g2,g2) = 9
    c: DistanceX(g-1,g1) = 13.5
    c: DistanceX(g3,g3) = 7.3
    c: DistanceY(g4,g4) = 5
    c: DistanceY(g0,g0) = 40
FEATURE [PartDesign::Pad] Pad037
  AllowMultiFace = false
  Direction = (1,1,1)
  Length = 22
  Length2 = 100
  Midplane = true
  Placement = pos=(0,0,0) rot=(1,0,0;1.5708rad)
  Profile = -> Sketch063
  Type = 0
FEATURE [Sketcher::SketchObject] Sketch064
  FullyConstrained = true
  MapMode = 5
  Placement = pos=(0,-11,-2.4e-15) rot=(1,0,0;1.5708rad)
  Support = -> [Pad037]
  sketch-geometry (3):
    g0: Circle CenterX=3.4 CenterY=32.5 CenterZ=0 NormalX=0 NormalY=0 NormalZ=1 AngleXU=0 Radius=2.25
    g1: Circle CenterX=3.4 CenterY=7.5 CenterZ=0 NormalX=0 NormalY=0 NormalZ=1 AngleXU=0 Radius=2.25
    g2: LineSegment StartX=3.4 StartY=32.5 StartZ=0 EndX=3.4 EndY=7.5 EndZ=0
  constraints (8):
    c: Vertical(g2)
    c: Coincident(g2,g0)
    c: Coincident(g1,g2)
    c: DistanceY(g2,g2) = 25
    c: Diameter(g0) = 4.5
    c: Equal(g0,g1)
    c: DistanceY(g-1,g1) = 7.5
    c: DistanceX(g-1,g1) = 3.4
FEATURE [PartDesign::Pocket] Pocket019
  AllowMultiFace = false
  BaseFeature = -> Pad037
  Length = 25
  Length2 = 100
  Placement = pos=(0,0,0) rot=(1,0,0;1.5708rad)
  Profile = -> Sketch064
  Type = 0
FEATURE [Sketcher::SketchObject] Sketch065
  FullyConstrained = true
  MapMode = 5
  Placement = pos=(0,0,9) rot=(1,0,0;3.14159rad)
  Support = -> [Pocket019]
  sketch-geometry (6):
    g0: Circle CenterX=16.95 CenterY=5 CenterZ=0 NormalX=0 NormalY=0 NormalZ=1 AngleXU=0 Radius=1.5
    g1: Circle CenterX=16.95 CenterY=-5 CenterZ=0 NormalX=0 NormalY=0 NormalZ=1 AngleXU=0 Radius=1.5
    g2: LineSegment StartX=0 StartY=5 StartZ=0 EndX=16.95 EndY=5 EndZ=0
    g3: LineSegment StartX=16.95 StartY=5 StartZ=0 EndX=16.95 EndY=-5 EndZ=0
    g4: LineSegment StartX=16.95 StartY=-5 StartZ=0 EndX=0 EndY=-5 EndZ=0
    g5: LineSegment StartX=0 StartY=-5 StartZ=0 EndX=0 EndY=5 EndZ=0
  constraints (15):
    c: Coincident(g2,g3)
    c: Coincident(g3,g4)
    c: Coincident(g4,g5)
    c: Coincident(g5,g2)
    c: Horizontal(g2)
    c: Horizontal(g4)
    c: Vertical(g3)
    c: Vertical(g5)
    c: Symmetric(g2,g4,g-1)
    c: DistanceY(g3,g3) = 10
    c: DistanceX(g2,g2) = 16.95
    c: Coincident(g0,g2)
    c: Coincident(g1,g3)
    c: Diameter(g1) = 3
    c: Equal(g1,g0)
FEATURE [PartDesign::Pocket] Pocket020
  AllowMultiFace = false
  BaseFeature = -> Pocket019
  Length = 5
  Length2 = 100
  Placement = pos=(0,0,0) rot=(1,0,0;1.5708rad)
  Profile = -> Sketch065
  Type = 0
FEATURE [PartDesign::Body] Body023  label="Servo_Mount_End"
  Group = -> [Sketch063,Pad037,Sketch064,Pocket019,Sketch065,Pocket020]
  Origin = -> Origin027
  Placement = pos=(-17,-1e-15,81) rot=(0,0,1;3.14159rad)
  Tip = -> Pocket020
FEATURE [Sketcher::SketchObject] Sketch066
  FullyConstrained = true
  MapMode = 5
  Placement = pos=(0,0,0) rot=(1,0,0;1.5708rad)
  Support = -> [XZ_Plane028]
  sketch-geometry (23):
    g0: LineSegment StartX=-120.4 StartY=121 StartZ=0 EndX=120.4 EndY=121 EndZ=0
    g1: LineSegment StartX=120.4 StartY=121 StartZ=0 EndX=120.4 EndY=81 EndZ=0
    g2: LineSegment StartX=120.4 StartY=81 StartZ=0 EndX=-120.4 EndY=81 EndZ=0
    g3: LineSegment StartX=-120.4 StartY=81 StartZ=0 EndX=-120.4 EndY=121 EndZ=0
    g4: LineSegment StartX=0 StartY=121 StartZ=0 EndX=0 EndY=81 EndZ=0
    g5: LineSegment StartX=-115 StartY=113.5 StartZ=0 EndX=-20.4 EndY=113.5 EndZ=0
    g6: LineSegment StartX=-20.4 StartY=113.5 StartZ=0 EndX=-20.4 EndY=88.5 EndZ=0
    g7: LineSegment StartX=-20.4 StartY=88.5 StartZ=0 EndX=-115 EndY=88.5 EndZ=0
    g8: LineSegment StartX=-115 StartY=88.5 StartZ=0 EndX=-115 EndY=113.5 EndZ=0
    g9: Circle CenterX=-115 CenterY=113.5 CenterZ=0 NormalX=0 NormalY=0 NormalZ=1 AngleXU=0 Radius=2.25
    g10: Circle CenterX=-115 CenterY=88.5 CenterZ=0 NormalX=0 NormalY=0 NormalZ=1 AngleXU=0 Radius=2.25
    g11: Circle CenterX=-20.4 CenterY=88.5 CenterZ=0 NormalX=0 NormalY=0 NormalZ=1 AngleXU=0 Radius=2.25
    g12: Circle CenterX=-20.4 CenterY=113.5 CenterZ=0 NormalX=0 NormalY=0 NormalZ=1 AngleXU=0 Radius=2.25
    g13: LineSegment StartX=20.4 StartY=113.5 StartZ=0 EndX=115 EndY=113.5 EndZ=0
    g14: LineSegment StartX=115 StartY=113.5 StartZ=0 EndX=115 EndY=88.5 EndZ=0
    g15: LineSegment StartX=115 StartY=88.5 StartZ=0 EndX=20.4 EndY=88.5 EndZ=0
    g16: LineSegment StartX=20.4 StartY=88.5 StartZ=0 EndX=20.4 EndY=113.5 EndZ=0
    g17: Circle CenterX=20.4 CenterY=113.5 CenterZ=0 NormalX=0 NormalY=0 NormalZ=1 AngleXU=0 Radius=2.25
    g18: Circle CenterX=115 CenterY=113.5 CenterZ=0 NormalX=0 NormalY=0 NormalZ=1 AngleXU=0 Radius=2.25
    g19: Circle CenterX=20.4 CenterY=88.5 CenterZ=0 NormalX=0 NormalY=0 NormalZ=1 AngleXU=0 Radius=2.25
    g20: Circle CenterX=115 CenterY=88.5 CenterZ=0 NormalX=0 NormalY=0 NormalZ=1 AngleXU=0 Radius=2.25
    g21: LineSegment StartX=-20.4 StartY=88.5 StartZ=0 EndX=20.4 EndY=113.5 EndZ=0
    g22: Circle CenterX=0 CenterY=101 CenterZ=0 NormalX=0 NormalY=0 NormalZ=1 AngleXU=0 Radius=3.25
  constraints (58):
    c: Coincident(g0,g1)
    c: Coincident(g1,g2)
    c: Coincident(g2,g3)
    c: Coincident(g3,g0)
    c: Horizontal(g0)
    c: Horizontal(g2)
    c: Vertical(g1)
    c: Vertical(g3)
    c: Symmetric(g0,g0,g4)
    c: Symmetric(g2,g1,g4)
    c: DistanceX(g2,g4) = 120.4
    c: DistanceY(g4,g4) = 40
    c: DistanceY(g-1,g4) = 81
    c: Coincident(g5,g6)
    c: Coincident(g6,g7)
    c: Coincident(g7,g8)
    c: Coincident(g8,g5)
    c: Horizontal(g5)
    c: Horizontal(g7)
    c: Vertical(g6)
    c: Vertical(g8)
    c: DistanceX(g5,g5) = 94.6
    c: DistanceY(g6,g6) = 25
    c: DistanceX(g2,g7) = 5.4
    c: Coincident(g12,g5)
    c: Coincident(g11,g6)
    c: Coincident(g10,g7)
    c: Coincident(g9,g5)
    c: Diameter(g10) = 4.5
    c: Equal(g10,g9)
    c: Equal(g10,g11)
    c: Equal(g10,g12)
    c: DistanceY(g2,g10) = 7.5
    c: Coincident(g13,g14)
    c: Coincident(g14,g15)
    c: Coincident(g15,g16)
    c: Coincident(g16,g13)
    c: Horizontal(g13)
    c: Horizontal(g15)
    c: Vertical(g14)
    c: Vertical(g16)
    c: Symmetric(g13,g12,g4)
    c: Symmetric(g14,g10,g4)
    c: Coincident(g19,g15)
    c: Coincident(g17,g13)
    c: Coincident(g18,g13)
    c: Coincident(g20,g14)
    c: Diameter(g17) = 4.5
    c: Equal(g17,g19)
    c: Equal(g17,g20)
    c: Equal(g17,g18)
    c: Coincident(g21,g11)
    c: Coincident(g21,g17)
    c: PointOnObject(g22,g21)
    c: PointOnObject(g22,g4)
    c: Diameter(g22) = 6.5
    c: PointOnObject(g22,g-2)
    c: DistanceX(g11,g19) = 40.8
FEATURE [PartDesign::Pad] Pad038
  AllowMultiFace = false
  Direction = (1,1,1)
  Length = 2
  Length2 = 100
  Placement = pos=(0,0,0) rot=(1,0,0;1.5708rad)
  Profile = -> Sketch066
  Type = 0
FEATURE [PartDesign::Body] Body024  label="Outer_Side_Plate"
  Group = -> [Sketch066,Pad038]
  Origin = -> Origin028
  Placement = pos=(0,13,0) rot=(0,0,1;0rad)
  Tip = -> Pad038
FEATURE [PartDesign::CoordinateSystem] Local_CS_d4f3
  AttacherType = Attacher::AttachEngine3D
FEATURE [Part::Feature] Pcb_d4f3
  Placement = pos=(-90,100,0) rot=(0,0,1;0rad)
  shape: bbox 66 x 50 x 1.6 mm, 84 faces (baked)
FEATURE [Sketcher::SketchObject] PCB_Sketch_d4f3
  FullyConstrained = false
  sketch-geometry (8):
    g0: LineSegment StartX=4e-16 StartY=3 StartZ=0 EndX=-3.6e-15 EndY=47 EndZ=0
    g1: LineSegment StartX=63 StartY=8.4e-15 StartZ=0 EndX=3 EndY=4e-16 EndZ=0
    g2: LineSegment StartX=66 StartY=47 StartZ=0 EndX=66 EndY=3 EndZ=0
    g3: LineSegment StartX=3 StartY=50 StartZ=0 EndX=63 EndY=50 EndZ=0
    g4: ArcOfCircle CenterX=63 CenterY=47 CenterZ=0 NormalX=0 NormalY=0 NormalZ=1 AngleXU=0 Radius=3 StartAngle=0 EndAngle=1.5708
    g5: ArcOfCircle CenterX=63 CenterY=3 CenterZ=0 NormalX=0 NormalY=0 NormalZ=1 AngleXU=0 Radius=3 StartAngle=4.71239 EndAngle=6.28319
    g6: ArcOfCircle CenterX=3 CenterY=3 CenterZ=0 NormalX=0 NormalY=0 NormalZ=1 AngleXU=0 Radius=3 StartAngle=3.14159 EndAngle=4.71239
    g7: ArcOfCircle CenterX=3 CenterY=47 CenterZ=0 NormalX=0 NormalY=0 NormalZ=1 AngleXU=0 Radius=3 StartAngle=1.5708 EndAngle=3.14159
  constraints (8):
    c: Coincident(g0,g6)
    c: Coincident(g0,g7)
    c: Coincident(g1,g6)
    c: Coincident(g3,g7)
    c: Coincident(g1,g5)
    c: Coincident(g3,g4)
    c: Coincident(g2,g5)
    c: Coincident(g2,g4)
FEATURE [App::Part] Board_Geoms_d4f3
  Group = -> [Local_CS_d4f3,Pcb_d4f3,PCB_Sketch_d4f3]
  Origin = -> Origin029
FEATURE [Part::Feature] Shape  label="C9_C_0603_1608Metric_5F754EF9"
  Placement = pos=(26,17.5,0) rot=(0,0,1;3.14159rad)
  shape: bbox 1.6 x 0.8 x 0.8 mm, 28 faces (baked)
FEATURE [Part::Feature] Shape001  label="C8_C_0603_1608Metric_5F7555CB"
  Placement = pos=(26,13,0) rot=(0,0,1;3.14159rad)
  shape: bbox 1.6 x 0.8 x 0.8 mm, 28 faces (baked)
FEATURE [Part::Feature] Shape002  label="J3_PinHeader_1x15_P254mm_Vertical_5F717813"
  Placement = pos=(54,47,-1.6) rot=(0,1,0;3.14159rad)
  shape: bbox 2.54 x 38.1 x 11.54 mm, 364 faces (baked)
FEATURE [Part::Feature] Shape003  label="U5_SOT_23_5_5F717A8C"
  Placement = pos=(4.5,23,0) rot=(0,0,1;1.5708rad)
  shape: bbox 2.9 x 2.8 x 1.55 mm, 109 faces (baked)
FEATURE [Part::Feature] Shape004  label="U4_SOIC_8_39x49mm_P127mm_5F717A77"
  Placement = pos=(40.25,11.5,0) rot=(0,0,1;0rad)
  shape: bbox 6 x 4.9 x 1.75 mm, 156 faces (baked)
FEATURE [Part::Feature] Shape005  label="U3_LQFP_32_7x7mm_P08mm_5F71845B"
  Placement = pos=(36.5,25.5,0) rot=(0,0,-1;1.5708rad)
  shape: bbox 9 x 9 x 1.5 mm, 516 faces (baked)
FEATURE [Part::Feature] Shape006  label="U2_SOT_353_SC_70_5_5F717A12"
  Placement = pos=(26,15.25,0) rot=(0,0,1;3.14159rad)
  shape: bbox 2 x 2 x 1.05 mm, 104 faces (baked)
FEATURE [Part::Feature] Shape007  label="U1_SOT_353_SC_70_5_5F7179FD"
  Placement = pos=(26,19.75,0) rot=(0,0,1;3.14159rad)
  shape: bbox 2 x 2 x 1.05 mm, 104 faces (baked)
FEATURE [Part::Feature] Shape008  label="SW1_SW_PUSH_6mm_5F7179E8"
  Placement = pos=(41.5,37.75,0) rot=(0,0,1;3.14159rad)
  shape: bbox 7.174 x 6 x 7.8 mm, 105 faces (baked)
FEATURE [Part::Feature] Shape009  label="R7_R_0603_1608Metric_5F7179C9"
  Placement = pos=(44.25,36.5,0) rot=(0,0,1;1.5708rad)
  shape: bbox 0.8 x 1.6 x 0.45 mm, 26 faces (baked)
FEATURE [Part::Feature] Shape010  label="R6_R_0603_1608Metric_5F7179B8"
  Placement = pos=(33.25,15.75,0) rot=(0,0,1;1.5708rad)
  shape: bbox 0.8 x 1.6 x 0.45 mm, 26 faces (baked)
FEATURE [Part::Feature] Shape011  label="R5_R_0603_1608Metric_5F7179A7"
  Placement = pos=(30.75,15.75,0) rot=(0,0,1;1.5708rad)
  shape: bbox 0.8 x 1.6 x 0.45 mm, 26 faces (baked)
FEATURE [Part::Feature] Shape012  label="R4_R_0603_1608Metric_5F717996"
  Placement = pos=(15.175,35.57,0) rot=(0,0,1;3.14159rad)
  shape: bbox 1.6 x 0.8 x 0.45 mm, 26 faces (baked)
FEATURE [Part::Feature] Shape013  label="R3_R_0603_1608Metric_5F717985"
  Placement = pos=(15.175,38.11,0) rot=(0,0,1;3.14159rad)
  shape: bbox 1.6 x 0.8 x 0.45 mm, 26 faces (baked)
FEATURE [Part::Feature] Shape014  label="R2_R_0603_1608Metric_5F717974"
  Placement = pos=(15.175,40.65,0) rot=(0,0,1;3.14159rad)
  shape: bbox 1.6 x 0.8 x 0.45 mm, 26 faces (baked)
FEATURE [Part::Feature] Shape015  label="R1_R_0603_1608Metric_5F717963"
  Placement = pos=(15.175,43.19,0) rot=(0,0,1;3.14159rad)
  shape: bbox 1.6 x 0.8 x 0.45 mm, 26 faces (baked)
FEATURE [Part::Feature] Shape016  label="J13_MSTBA_01x02_G_5_08mm_5F717952"
  Placement = pos=(44,3.5,0) rot=(0,0,1;0rad)
  shape: bbox 12.16 x 12 x 12.6 mm, 63 faces (baked)
FEATURE [Part::Feature] Shape017  label="J12_PinHeader_1x06_P254mm_Vertical_5F71792E"
  Placement = pos=(34.95,46.25,0) rot=(0,0,1;1.5708rad)
  shape: bbox 15.24 x 2.54 x 11.54 mm, 148 faces (baked)
FEATURE [Part::Feature] Shape018  label="J11_PinHeader_1x03_P254mm_Vertical_5F717914"
  Placement = pos=(1.84,13.98,0) rot=(0,0,1;1.5708rad)
  shape: bbox 7.62 x 2.54 x 11.54 mm, 76 faces (baked)
FEATURE [Part::Feature] Shape019  label="J10_PinHeader_1x03_P254mm_Vertical_5F7178FD"
  Placement = pos=(1.84,16.52,0) rot=(0,0,1;1.5708rad)
  shape: bbox 7.62 x 2.54 x 11.54 mm, 76 faces (baked)
FEATURE [Part::Feature] Shape020  label="J9_MSTBA_01x04_G_5_08mm_5F7178E6"
  Placement = pos=(20.5,3.5,0) rot=(0,0,1;0rad)
  shape: bbox 22.32 x 12 x 12.6 mm, 113 faces (baked)
FEATURE [Part::Feature] Shape021  label="J8_PinSocket_1x15_P254mm_Vertical_5F7178B8"
  Placement = pos=(12,47,-1.6) rot=(0,1,0;3.14159rad)
  shape: bbox 2.54 x 38.1 x 10.1 mm, 475 faces (baked)
FEATURE [App::Part] Bot_d4f3
  Group = -> [Shape002,Shape021]
  Origin = -> Origin033
FEATURE [Part::Feature] Shape022  label="J7_SHF-105-01-L-D-SM-K-TR_5F717895"
  Placement = pos=(48,17.25,0) rot=(0.57735,0.57735,0.57735;2.0944rad)
  shape: bbox 6.502 x 12.7 x 5.588 mm, 207 faces, 4 solids (baked)
FEATURE [Part::Feature] Shape023  label="J6_PinHeader_1x03_P254mm_Vertical_5F717875"
  Placement = pos=(1.84,33.03,0) rot=(0,0,1;1.5708rad)
  shape: bbox 7.62 x 2.54 x 11.54 mm, 76 faces (baked)
FEATURE [Part::Feature] Shape024  label="J5_PinHeader_1x03_P254mm_Vertical_5F722997"
  Placement = pos=(1.84,35.57,0) rot=(0,0,1;1.5708rad)
  shape: bbox 7.62 x 2.54 x 11.54 mm, 76 faces (baked)
FEATURE [Part::Feature] Shape025  label="J4_Molex_AE_6410_06A_5F717847"
  Placement = pos=(61.62,35.57,0) rot=(0,0,-1;1.5708rad)
  shape: bbox 5.8 x 15.24 x 15.26 mm, 169 faces (baked)
FEATURE [Part::Feature] Shape026  label="J2_PinHeader_1x03_P254mm_Vertical_5F7177F0"
  Placement = pos=(1.84,38.11,0) rot=(0,0,1;1.5708rad)
  shape: bbox 7.62 x 2.54 x 11.54 mm, 76 faces (baked)
FEATURE [Part::Feature] Shape027  label="J1_PinHeader_1x03_P254mm_Vertical_5F7228CA"
  Placement = pos=(1.84,40.65,0) rot=(0,0,1;1.5708rad)
  shape: bbox 7.62 x 2.54 x 11.54 mm, 76 faces (baked)
FEATURE [Part::Feature] Shape028  label="D6_LED_0603_1608Metric_5F71855F"
  Placement = pos=(33.25,12.25,0) rot=(0,0,1;1.5708rad)
  shape: bbox 0.8 x 1.6 x 1.1 mm, 50 faces (baked)
FEATURE [Part::Feature] Shape029  label="D5_LED_0603_1608Metric_5F71778F"
  Placement = pos=(30.75,12.25,0) rot=(0,0,1;1.5708rad)
  shape: bbox 0.8 x 1.6 x 1.1 mm, 50 faces (baked)
FEATURE [Part::Feature] Shape030  label="D4_SOT_23_5F71777C"
  Placement = pos=(18.985,35.57,0) rot=(0,0,1;0rad)
  shape: bbox 2.5 x 3 x 1.2 mm, 76 faces (baked)
FEATURE [Part::Feature] Shape031  label="D3_SOT_23_5F717767"
  Placement = pos=(22.795,38.11,0) rot=(0,0,1;0rad)
  shape: bbox 2.5 x 3 x 1.2 mm, 76 faces (baked)
FEATURE [Part::Feature] Shape032  label="D2_SOT_23_5F717752"
  Placement = pos=(18.985,40.65,0) rot=(0,0,1;0rad)
  shape: bbox 2.5 x 3 x 1.2 mm, 76 faces (baked)
FEATURE [Part::Feature] Shape033  label="D1_SOT_23_5F71773D"
  Placement = pos=(22.795,43.19,0) rot=(0,0,1;0rad)
  shape: bbox 2.5 x 3 x 1.2 mm, 76 faces (baked)
FEATURE [Part::Feature] Shape034  label="C7_C_0603_1608Metric_5F717728"
  Placement = pos=(4.5,27.5,0) rot=(0,0,1;0rad)
  shape: bbox 1.6 x 0.8 x 0.8 mm, 28 faces (baked)
FEATURE [Part::Feature] Shape035  label="C6_C_0603_1608Metric_5F717717"
  Placement = pos=(6.25,25.75,0) rot=(0,0,1;0rad)
  shape: bbox 1.6 x 0.8 x 0.8 mm, 28 faces (baked)
FEATURE [Part::Feature] Shape036  label="C5_C_0603_1608Metric_5F717706"
  Placement = pos=(4.5,20.25,0) rot=(0,0,1;0rad)
  shape: bbox 1.6 x 0.8 x 0.8 mm, 28 faces (baked)
FEATURE [Part::Feature] Shape037  label="C4_C_0603_1608Metric_5F7176F5"
  Placement = pos=(41.5,15.25,0) rot=(0,0,1;0rad)
  shape: bbox 1.6 x 0.8 x 0.8 mm, 28 faces (baked)
FEATURE [Part::Feature] Shape038  label="C3_C_0603_1608Metric_5F7176E4"
  Placement = pos=(32.5,39.75,0) rot=(0,0,1;1.5708rad)
  shape: bbox 0.8 x 1.6 x 0.8 mm, 28 faces (baked)
FEATURE [Part::Feature] Shape039  label="C2_C_0603_1608Metric_5F7176D3"
  Placement = pos=(38.25,33,0) rot=(0,0,1;0rad)
  shape: bbox 1.6 x 0.8 x 0.8 mm, 28 faces (baked)
FEATURE [Part::Feature] Shape040  label="C1_C_0805_2012Metric_5F7176C2"
  Placement = pos=(38.25,35,0) rot=(0,0,1;0rad)
  shape: bbox 2 x 1.25 x 1.25 mm, 28 faces (baked)
FEATURE [App::Part] Top_d4f3
  Group = -> [Shape,Shape001,Shape003,Shape004,Shape005,Shape006,Shape007,Shape008,Shape009,Shape010,Shape011,Shape012,Shape013,Shape014,Shape015,Shape016,Shape017,Shape018,Shape019,Shape020,Shape022,Shape023,Shape024,Shape025,Shape026,Shape027,Shape028,Shape029,Shape030,Shape031,Shape032,Shape033,Shape034,Shape035,Shape036,Shape037,Shape038,Shape039,Shape040]
  Origin = -> Origin032
FEATURE [App::Part] Step_Models_d4f3
  Group = -> [Top_d4f3,Bot_d4f3]
  Origin = -> Origin031
FEATURE [App::Part] Board_d4f3  label="motor_board"
  Group = -> [Board_Geoms_d4f3,Step_Models_d4f3]
  Origin = -> Origin030
FEATURE [Sketcher::SketchObject] Sketch067
  FullyConstrained = false
  MapMode = 5
  Support = -> [XY_Plane035]
  sketch-geometry (66):
    g0: LineSegment StartX=0 StartY=41.4 StartZ=0 EndX=47.35 EndY=41.4 EndZ=0
    g1: LineSegment StartX=47.35 StartY=41.4 StartZ=0 EndX=47.35 EndY=0 EndZ=0
    g2: LineSegment StartX=47.35 StartY=0 StartZ=0 EndX=0 EndY=0 EndZ=0
    g3: LineSegment StartX=0 StartY=0 StartZ=0 EndX=0 EndY=41.4 EndZ=0
    g4: LineSegment StartX=2.72 StartY=2.92 StartZ=0 EndX=2.72 EndY=5.46 EndZ=0
    g5: LineSegment StartX=2.72 StartY=5.46 StartZ=0 EndX=2.72 EndY=8 EndZ=0
    g6: LineSegment StartX=2.72 StartY=8 StartZ=0 EndX=2.72 EndY=10.54 EndZ=0
    g7: LineSegment StartX=2.72 StartY=10.54 StartZ=0 EndX=2.72 EndY=13.08 EndZ=0
    g8: LineSegment StartX=2.72 StartY=13.08 StartZ=0 EndX=2.72 EndY=15.62 EndZ=0
    g9: LineSegment StartX=2.72 StartY=15.62 StartZ=0 EndX=2.72 EndY=18.16 EndZ=0
    g10: LineSegment StartX=2.72 StartY=18.16 StartZ=0 EndX=2.72 EndY=20.7 EndZ=0
    g11: LineSegment StartX=2.72 StartY=20.7 StartZ=0 EndX=2.72 EndY=23.24 EndZ=0
    g12: LineSegment StartX=2.72 StartY=23.24 StartZ=0 EndX=2.72 EndY=25.78 EndZ=0
    g13: LineSegment StartX=2.72 StartY=25.78 StartZ=0 EndX=2.72 EndY=28.32 EndZ=0
    g14: LineSegment StartX=2.72 StartY=28.32 StartZ=0 EndX=2.72 EndY=30.86 EndZ=0
    g15: LineSegment StartX=2.72 StartY=30.86 StartZ=0 EndX=2.72 EndY=33.4 EndZ=0
    g16: LineSegment StartX=2.72 StartY=33.4 StartZ=0 EndX=2.72 EndY=35.94 EndZ=0
    g17: LineSegment StartX=2.72 StartY=35.94 StartZ=0 EndX=2.72 EndY=38.48 EndZ=0
    g18: LineSegment StartX=44.63 StartY=2.92 StartZ=0 EndX=44.63 EndY=5.46 EndZ=0
    g19: LineSegment StartX=44.63 StartY=5.46 StartZ=0 EndX=44.63 EndY=8 EndZ=0
    g20: LineSegment StartX=44.63 StartY=8 StartZ=0 EndX=44.63 EndY=10.54 EndZ=0
    g21: LineSegment StartX=44.63 StartY=10.54 StartZ=0 EndX=44.63 EndY=13.08 EndZ=0
    g22: LineSegment StartX=44.63 StartY=13.08 StartZ=0 EndX=44.63 EndY=15.62 EndZ=0
    g23: LineSegment StartX=44.63 StartY=15.62 StartZ=0 EndX=44.63 EndY=18.16 EndZ=0
    g24: LineSegment StartX=44.63 StartY=18.16 StartZ=0 EndX=44.63 EndY=20.7 EndZ=0
    g25: LineSegment StartX=44.63 StartY=20.7 StartZ=0 EndX=44.63 EndY=23.24 EndZ=0
    g26: LineSegment StartX=44.63 StartY=23.24 StartZ=0 EndX=44.63 EndY=25.78 EndZ=0
    g27: LineSegment StartX=44.63 StartY=25.78 StartZ=0 EndX=44.63 EndY=28.32 EndZ=0
    g28: LineSegment StartX=44.63 StartY=28.32 StartZ=0 EndX=44.63 EndY=30.86 EndZ=0
    g29: LineSegment StartX=44.63 StartY=30.86 StartZ=0 EndX=44.63 EndY=33.4 EndZ=0
    g30: LineSegment StartX=44.63 StartY=33.4 StartZ=0 EndX=44.63 EndY=35.94 EndZ=0
    g31: LineSegment StartX=44.63 StartY=35.94 StartZ=0 EndX=44.63 EndY=38.48 EndZ=0
    g32: LineSegment StartX=0 StartY=0 StartZ=0 EndX=2.72 EndY=2.92 EndZ=0
    g33: LineSegment StartX=44.63 StartY=2.92 StartZ=0 EndX=47.35 EndY=0 EndZ=0
    g34: LineSegment StartX=44.63 StartY=38.48 StartZ=0 EndX=47.35 EndY=41.4 EndZ=0
    g35: LineSegment StartX=2.72 StartY=38.48 StartZ=0 EndX=0 EndY=41.4 EndZ=0
    g36: Circle CenterX=2.72 CenterY=38.48 CenterZ=0 NormalX=0 NormalY=0 NormalZ=1 AngleXU=0 Radius=0.5
    g37: Circle CenterX=2.72 CenterY=35.94 CenterZ=0 NormalX=0 NormalY=0 NormalZ=1 AngleXU=0 Radius=0.5
    g38: Circle CenterX=2.72 CenterY=33.4 CenterZ=0 NormalX=0 NormalY=0 NormalZ=1 AngleXU=0 Radius=0.5
    g39: Circle CenterX=2.72 CenterY=30.86 CenterZ=0 NormalX=0 NormalY=0 NormalZ=1 AngleXU=0 Radius=0.5
    g40: Circle CenterX=2.72 CenterY=28.32 CenterZ=0 NormalX=0 NormalY=0 NormalZ=1 AngleXU=0 Radius=0.5
    g41: Circle CenterX=2.72 CenterY=25.78 CenterZ=0 NormalX=0 NormalY=0 NormalZ=1 AngleXU=0 Radius=0.5
    g42: Circle CenterX=2.72 CenterY=23.24 CenterZ=0 NormalX=0 NormalY=0 NormalZ=1 AngleXU=0 Radius=0.5
    g43: Circle CenterX=2.72 CenterY=20.7 CenterZ=0 NormalX=0 NormalY=0 NormalZ=1 AngleXU=0 Radius=0.5
    g44: Circle CenterX=2.72 CenterY=18.16 CenterZ=0 NormalX=0 NormalY=0 NormalZ=1 AngleXU=0 Radius=0.5
    g45: Circle CenterX=2.72 CenterY=15.62 CenterZ=0 NormalX=0 NormalY=0 NormalZ=1 AngleXU=0 Radius=0.5
    g46: Circle CenterX=2.72 CenterY=13.08 CenterZ=0 NormalX=0 NormalY=0 NormalZ=1 AngleXU=0 Radius=0.5
    g47: Circle CenterX=2.72 CenterY=10.54 CenterZ=0 NormalX=0 NormalY=0 NormalZ=1 AngleXU=0 Radius=0.5
    g48: Circle CenterX=2.72 CenterY=8 CenterZ=0 NormalX=0 NormalY=0 NormalZ=1 AngleXU=0 Radius=0.5
    g49: Circle CenterX=2.72 CenterY=5.46 CenterZ=0 NormalX=0 NormalY=0 NormalZ=1 AngleXU=0 Radius=0.5
    g50: Circle CenterX=2.72 CenterY=2.92 CenterZ=0 NormalX=0 NormalY=0 NormalZ=1 AngleXU=0 Radius=0.5
    g51: Circle CenterX=44.63 CenterY=38.48 CenterZ=0 NormalX=0 NormalY=0 NormalZ=1 AngleXU=0 Radius=0.5
    g52: Circle CenterX=44.63 CenterY=35.94 CenterZ=0 NormalX=0 NormalY=0 NormalZ=1 AngleXU=0 Radius=0.5
    g53: Circle CenterX=44.63 CenterY=33.4 CenterZ=0 NormalX=0 NormalY=0 NormalZ=1 AngleXU=0 Radius=0.5
    g54: Circle CenterX=44.63 CenterY=30.86 CenterZ=0 NormalX=0 NormalY=0 NormalZ=1 AngleXU=0 Radius=0.5
    g55: Circle CenterX=44.63 CenterY=28.32 CenterZ=0 NormalX=0 NormalY=0 NormalZ=1 AngleXU=0 Radius=0.5
    g56: Circle CenterX=44.63 CenterY=25.78 CenterZ=0 NormalX=0 NormalY=0 NormalZ=1 AngleXU=0 Radius=0.5
    g57: Circle CenterX=44.63 CenterY=23.24 CenterZ=0 NormalX=0 NormalY=0 NormalZ=1 AngleXU=0 Radius=0.5
    g58: Circle CenterX=44.63 CenterY=20.7 CenterZ=0 NormalX=0 NormalY=0 NormalZ=1 AngleXU=0 Radius=0.5
    g59: Circle CenterX=44.63 CenterY=18.16 CenterZ=0 NormalX=0 NormalY=0 NormalZ=1 AngleXU=0 Radius=0.5
    g60: Circle CenterX=44.63 CenterY=15.62 CenterZ=0 NormalX=0 NormalY=0 NormalZ=1 AngleXU=0 Radius=0.5
    g61: Circle CenterX=44.63 CenterY=13.08 CenterZ=0 NormalX=0 NormalY=0 NormalZ=1 AngleXU=0 Radius=0.5
    g62: Circle CenterX=44.63 CenterY=10.54 CenterZ=0 NormalX=0 NormalY=0 NormalZ=1 AngleXU=0 Radius=0.5
    g63: Circle CenterX=44.63 CenterY=8 CenterZ=0 NormalX=0 NormalY=0 NormalZ=1 AngleXU=0 Radius=0.5
    g64: Circle CenterX=44.63 CenterY=5.46 CenterZ=0 NormalX=0 NormalY=0 NormalZ=1 AngleXU=0 Radius=0.5
    g65: Circle CenterX=44.63 CenterY=2.92 CenterZ=0 NormalX=0 NormalY=0 NormalZ=1 AngleXU=0 Radius=0.5
  constraints (152):
    c: Coincident(g0,g1)
    c: Coincident(g1,g2)
    c: Coincident(g2,g3)
    c: Coincident(g3,g0)
    c: Horizontal(g0)
    c: Horizontal(g2)
    c: Vertical(g1)
    c: Vertical(g3)
    c: DistanceX(g0,g0) = 47.35
    c: DistanceY(g1,g1) = 41.4
    c: Coincident(g2,g-1)
    c: Coincident(g4,g5)
    c: Coincident(g5,g6)
    c: Coincident(g6,g7)
    c: Coincident(g7,g8)
    c: Coincident(g8,g9)
    c: Coincident(g9,g10)
    c: Coincident(g10,g11)
    c: Coincident(g11,g12)
    c: Coincident(g12,g13)
    c: Coincident(g13,g14)
    c: Coincident(g14,g15)
    c: Coincident(g15,g16)
    c: Coincident(g16,g17)
    c: Coincident(g18,g19)
    c: Coincident(g19,g20)
    c: Coincident(g20,g21)
    c: Coincident(g21,g22)
    c: Coincident(g22,g23)
    c: Coincident(g23,g24)
    c: Coincident(g24,g25)
    c: Coincident(g25,g26)
    c: Coincident(g26,g27)
    c: Coincident(g27,g28)
    c: Coincident(g28,g29)
    c: Coincident(g29,g30)
    c: Coincident(g30,g31)
    c: Vertical(g17)
    c: Vertical(g16)
    c: Vertical(g15)
    c: Vertical(g14)
    c: Vertical(g13)
    c: Vertical(g12)
    c: Vertical(g11)
    c: Vertical(g10)
    c: Vertical(g9)
    c: Vertical(g8)
    c: Vertical(g7)
    c: Vertical(g6)
    c: Vertical(g5)
    c: Vertical(g4)
    c: Equal(g17,g16)
    c: Equal(g16,g15)
    c: Equal(g15,g14)
    c: Equal(g14,g13)
    c: Equal(g13,g12)
    c: Equal(g12,g11)
    c: Equal(g11,g10)
    c: Equal(g10,g9)
    c: Equal(g9,g8)
    c: Equal(g8,g7)
    c: Equal(g7,g6)
    c: Equal(g6,g5)
    c: Equal(g5,g4)
    c: DistanceY(g4,g4) = 2.54
    c: Vertical(g18)
    c: Vertical(g19)
    c: Vertical(g20)
    c: Vertical(g21)
    c: Vertical(g22)
    c: Vertical(g23)
    c: Vertical(g24)
    c: Vertical(g25)
    c: Vertical(g26)
    c: Vertical(g27)
    c: Vertical(g28)
    c: Vertical(g29)
    c: Vertical(g30)
    c: Vertical(g31)
    c: Equal(g31,g30)
    c: Equal(g30,g29)
    c: Equal(g29,g28)
    c: Equal(g28,g27)
    c: Equal(g27,g26)
    c: Equal(g26,g25)
    c: Equal(g25,g24)
    c: Equal(g24,g23)
    c: Equal(g23,g22)
    c: Equal(g22,g21)
    c: Equal(g21,g20)
    c: Equal(g20,g19)
    c: Equal(g19,g18)
    c: Equal(g18,g4)
    c: DistanceX(g4,g18) = 41.91
    c: Coincident(g33,g1)
    c: Coincident(g33,g18)
    c: Coincident(g4,g32)
    c: Coincident(g32,g2)
    c: Equal(g32,g33)
    c: Coincident(g35,g17)
    c: Coincident(g35,g0)
    c: Coincident(g34,g31)
    c: Coincident(g34,g0)
    c: Equal(g34,g33)
    c: Equal(g33,g35)
    c: Coincident(g50,g4)
    c: Coincident(g49,g4)
    c: Coincident(g48,g5)
    c: Coincident(g47,g6)
    c: Coincident(g46,g7)
    c: Coincident(g45,g8)
    c: Coincident(g44,g9)
    c: Coincident(g43,g10)
    c: Coincident(g42,g11)
    c: Coincident(g41,g12)
    c: Coincident(g40,g13)
    c: Coincident(g39,g14)
    c: Coincident(g38,g15)
    c: Coincident(g37,g16)
    c: Coincident(g36,g17)
    c: Coincident(g65,g18)
    c: Coincident(g64,g18)
    c: Coincident(g63,g19)
    c: Coincident(g62,g20)
    c: Coincident(g61,g21)
    c: Coincident(g60,g22)
    c: Coincident(g59,g23)
    c: Coincident(g58,g24)
    c: Coincident(g57,g25)
    c: Coincident(g56,g26)
    c: Coincident(g55,g27)
    c: Coincident(g54,g28)
    c: Coincident(g53,g29)
    c: Coincident(g52,g30)
    c: Coincident(g51,g31)
    c: Diameter(g36) = 1
    c: Equal(g36, g37-g50) x14
    c: Equal(g36,g65)
    c: Equal(g36,g64)
    c: Equal(g36,g63)
    c: Equal(g36,g62)
    c: Equal(g36,g61)
    c: Equal(g36,g60)
    c: Equal(g36,g59)
    c: Equal(g36,g58)
    c: Equal(g36,g57)
    c: Equal(g36,g56)
    c: Equal(g36,g55)
    c: Equal(g36,g54)
    c: Equal(g36,g53)
    c: Equal(g36,g52)
    c: Equal(g36,g51)
FEATURE [PartDesign::Pad] Pad039
  AllowMultiFace = false
  Direction = (1,1,1)
  Length = 1.6
  Length2 = 100
  Profile = -> Sketch067
  Reversed = true
  Type = 0
FEATURE [PartDesign::Body] Body025  label="PCB"
  Group = -> [Sketch067,Pad039]
  Origin = -> Origin035
  Tip = -> Pad039
FEATURE [Part::Feature] Shape041  label="J3_PinHeader_1x15_P254mm_Vertical_5F717814"
  Placement = pos=(2.75,38.5,-5.2e-15) rot=(0,0,1;0rad)
  shape: bbox 2.54 x 38.1 x 11.54 mm, 364 faces (baked)
FEATURE [Part::Feature] Shape042  label="J8_PinSocket_1x15_P254mm_Vertical_5F7178B009"
  Placement = pos=(44.65,38.5,4e-15) rot=(0,0,1;0rad)
  shape: bbox 2.54 x 38.1 x 10.1 mm, 475 faces (baked)
FEATURE [Sketcher::SketchObject] Sketch068
  FullyConstrained = false
  MapMode = 5
  Support = -> [XY_Plane036]
  sketch-geometry (1):
    g0: Circle CenterX=0 CenterY=0 CenterZ=0 NormalX=0 NormalY=0 NormalZ=1 AngleXU=0 Radius=4.15
  constraints (2):
    c: Coincident(g0,g-1)
    c: Diameter(g0) = 8.3
FEATURE [PartDesign::Pad] Pad040
  AllowMultiFace = false
  Direction = (1,1,1)
  Length = 10.5
  Length2 = 100
  Profile = -> Sketch068
  Type = 0
FEATURE [PartDesign::Body] Body026  label="Capacitor"
  Group = -> [Sketch068,Pad040]
  Origin = -> Origin036
  Placement = pos=(10,14.5,-1.6) rot=(0,1,0;3.14159rad)
  Tip = -> Pad040
FEATURE [Sketcher::SketchObject] Sketch069
  FullyConstrained = false
  MapMode = 5
  Support = -> [XY_Plane039]
  sketch-geometry (4):
    g0: LineSegment StartX=-33.75 StartY=67.25 StartZ=0 EndX=33.75 EndY=67.25 EndZ=0
    g1: LineSegment StartX=33.75 StartY=67.25 StartZ=0 EndX=33.75 EndY=-67.25 EndZ=0
    g2: LineSegment StartX=33.75 StartY=-67.25 StartZ=0 EndX=-33.75 EndY=-67.25 EndZ=0
    g3: LineSegment StartX=-33.75 StartY=-67.25 StartZ=0 EndX=-33.75 EndY=67.25 EndZ=0
  constraints (11):
    c: Coincident(g0,g1)
    c: Coincident(g1,g2)
    c: Coincident(g2,g3)
    c: Coincident(g3,g0)
    c: Horizontal(g0)
    c: Horizontal(g2)
    c: Vertical(g1)
    c: Vertical(g3)
    c: Symmetric(g0,g1,g-1)
    c: DistanceX(g0,g0) = 67.5
    c: DistanceY(g3,g3) = 134.5
FEATURE [PartDesign::Pad] Pad041
  AllowMultiFace = false
  Direction = (1,1,1)
  Length = 59
  Length2 = 100
  Profile = -> Sketch069
  Type = 0
FEATURE [Sketcher::SketchObject] Sketch070
  FullyConstrained = false
  MapMode = 5
  Placement = pos=(0,0,59) rot=(0,0,1;0rad)
  Support = -> [Pad041]
  sketch-geometry (8):
    g0: LineSegment StartX=-25.5 StartY=54.25 StartZ=0 EndX=-15.5 EndY=54.25 EndZ=0
    g1: LineSegment StartX=-15.5 StartY=54.25 StartZ=0 EndX=-15.5 EndY=43.25 EndZ=0
    g2: LineSegment StartX=-15.5 StartY=43.25 StartZ=0 EndX=-25.5 EndY=43.25 EndZ=0
    g3: LineSegment StartX=-25.5 StartY=43.25 StartZ=0 EndX=-25.5 EndY=54.25 EndZ=0
    g4: LineSegment StartX=15.5 StartY=54.25 StartZ=0 EndX=25.5 EndY=54.25 EndZ=0
    g5: LineSegment StartX=25.5 StartY=54.25 StartZ=0 EndX=25.5 EndY=43.25 EndZ=0
    g6: LineSegment StartX=25.5 StartY=43.25 StartZ=0 EndX=15.5 EndY=43.25 EndZ=0
    g7: LineSegment StartX=15.5 StartY=43.25 StartZ=0 EndX=15.5 EndY=54.25 EndZ=0
  constraints (22):
    c: Coincident(g0,g1)
    c: Coincident(g1,g2)
    c: Coincident(g2,g3)
    c: Coincident(g3,g0)
    c: Horizontal(g0)
    c: Horizontal(g2)
    c: Vertical(g1)
    c: Vertical(g3)
    c: Coincident(g4,g5)
    c: Coincident(g5,g6)
    c: Coincident(g6,g7)
    c: Coincident(g7,g4)
    c: Horizontal(g4)
    c: Horizontal(g6)
    c: Vertical(g5)
    c: Vertical(g7)
    c: Symmetric(g1,g6,g-2)
    c: Symmetric(g0,g4,g-2)
    c: DistanceX(g0,g4) = 31
    c: DistanceX(g0,g4) = 51
    c: DistanceY(g3,g3) = 11
    c: DistanceY(g-1,g0) = 54.25
FEATURE [PartDesign::Pad] Pad042
  AllowMultiFace = false
  BaseFeature = -> Pad041
  Direction = (1,1,1)
  Length = 6.7
  Length2 = 100
  Profile = -> Sketch070
  Type = 0
FEATURE [PartDesign::Body] Body027
  Group = -> [Sketch069,Pad041,Sketch070,Pad042]
  Origin = -> Origin039
  Tip = -> Pad042
FEATURE [App::Part] Part002  label="Battery"
  Group = -> [Body027]
  Origin = -> Origin038
  Placement = pos=(29.5,0,92.6) rot=(-0.57735,0.57735,0.57735;4.18879rad)
FEATURE [Sketcher::SketchObject] Sketch071
  FullyConstrained = true
  MapMode = 5
  Placement = pos=(0,0,0) rot=(1,0,0;1.5708rad)
  Support = -> [XZ_Plane040]
  sketch-geometry (35):
    g0: LineSegment StartX=-128 StartY=129 StartZ=0 EndX=128 EndY=129 EndZ=0
    g1: LineSegment StartX=128 StartY=129 StartZ=0 EndX=128 EndY=81 EndZ=0
    g2: LineSegment StartX=128 StartY=81 StartZ=0 EndX=-128 EndY=81 EndZ=0
    g3: LineSegment StartX=-128 StartY=81 StartZ=0 EndX=-128 EndY=129 EndZ=0
    g4: LineSegment StartX=0 StartY=129 StartZ=0 EndX=0 EndY=81 EndZ=0
    g5: LineSegment StartX=-115 StartY=113.5 StartZ=0 EndX=-20.4 EndY=113.5 EndZ=0
    g6: LineSegment StartX=-20.4 StartY=113.5 StartZ=0 EndX=-20.4 EndY=88.5 EndZ=0
    g7: LineSegment StartX=-20.4 StartY=88.5 StartZ=0 EndX=-115 EndY=88.5 EndZ=0
    g8: LineSegment StartX=-115 StartY=88.5 StartZ=0 EndX=-115 EndY=113.5 EndZ=0
    g9: Circle CenterX=-115 CenterY=113.5 CenterZ=0 NormalX=0 NormalY=0 NormalZ=1 AngleXU=0 Radius=2.25
    g10: Circle CenterX=-115 CenterY=88.5 CenterZ=0 NormalX=0 NormalY=0 NormalZ=1 AngleXU=0 Radius=2.25
    g11: Circle CenterX=-20.4 CenterY=88.5 CenterZ=0 NormalX=0 NormalY=0 NormalZ=1 AngleXU=0 Radius=2.25
    g12: Circle CenterX=-20.4 CenterY=113.5 CenterZ=0 NormalX=0 NormalY=0 NormalZ=1 AngleXU=0 Radius=2.25
    g13: LineSegment StartX=20.4 StartY=113.5 StartZ=0 EndX=115 EndY=113.5 EndZ=0
    g14: LineSegment StartX=115 StartY=113.5 StartZ=0 EndX=115 EndY=88.5 EndZ=0
    g15: LineSegment StartX=115 StartY=88.5 StartZ=0 EndX=20.4 EndY=88.5 EndZ=0
    g16: LineSegment StartX=20.4 StartY=88.5 StartZ=0 EndX=20.4 EndY=113.5 EndZ=0
    g17: Circle CenterX=20.4 CenterY=113.5 CenterZ=0 NormalX=0 NormalY=0 NormalZ=1 AngleXU=0 Radius=2.25
    g18: Circle CenterX=115 CenterY=113.5 CenterZ=0 NormalX=0 NormalY=0 NormalZ=1 AngleXU=0 Radius=2.25
    g19: Circle CenterX=20.4 CenterY=88.5 CenterZ=0 NormalX=0 NormalY=0 NormalZ=1 AngleXU=0 Radius=2.25
    g20: Circle CenterX=115 CenterY=88.5 CenterZ=0 NormalX=0 NormalY=0 NormalZ=1 AngleXU=0 Radius=2.25
    g21: Circle CenterX=-125 CenterY=126 CenterZ=0 NormalX=0 NormalY=0 NormalZ=1 AngleXU=0 Radius=1.75
    g22: Circle CenterX=-125 CenterY=84 CenterZ=0 NormalX=0 NormalY=0 NormalZ=1 AngleXU=0 Radius=1.75
    g23: Circle CenterX=-67 CenterY=126 CenterZ=0 NormalX=0 NormalY=0 NormalZ=1 AngleXU=0 Radius=1.75
    g24: Circle CenterX=67 CenterY=126 CenterZ=0 NormalX=0 NormalY=0 NormalZ=1 AngleXU=0 Radius=1.75
    g25: Circle CenterX=125 CenterY=126 CenterZ=0 NormalX=0 NormalY=0 NormalZ=1 AngleXU=0 Radius=1.75
    g26: Circle CenterX=125 CenterY=84 CenterZ=0 NormalX=0 NormalY=0 NormalZ=1 AngleXU=0 Radius=1.75
    g27: Circle CenterX=0 CenterY=101 CenterZ=0 NormalX=0 NormalY=0 NormalZ=1 AngleXU=0 Radius=3.25
    g28: LineSegment StartX=-20.4 StartY=88.5 StartZ=0 EndX=20.4 EndY=113.5 EndZ=0
    g29: Circle CenterX=60 CenterY=124 CenterZ=0 NormalX=0 NormalY=0 NormalZ=1 AngleXU=0 Radius=2.25
    g30: Circle CenterX=-60 CenterY=124 CenterZ=0 NormalX=0 NormalY=0 NormalZ=1 AngleXU=0 Radius=2.25
    g31: Circle CenterX=-37.5 CenterY=118.5 CenterZ=0 NormalX=0 NormalY=0 NormalZ=1 AngleXU=0 Radius=1.6
    g32: Circle CenterX=-54 CenterY=88 CenterZ=0 NormalX=0 NormalY=0 NormalZ=1 AngleXU=0 Radius=1.6
    g33: Circle CenterX=37.5 CenterY=88 CenterZ=0 NormalX=0 NormalY=0 NormalZ=1 AngleXU=0 Radius=1.6
    g34: Circle CenterX=54 CenterY=118.5 CenterZ=0 NormalX=0 NormalY=0 NormalZ=1 AngleXU=0 Radius=1.6
  constraints (89):
    c: Coincident(g0,g1)
    c: Coincident(g1,g2)
    c: Coincident(g2,g3)
    c: Coincident(g3,g0)
    c: Horizontal(g0)
    c: Horizontal(g2)
    c: Vertical(g1)
    c: Vertical(g3)
    c: Symmetric(g0,g0,g4)
    c: Symmetric(g2,g1,g4)
    c: DistanceX(g2,g4) = 128
    c: DistanceY(g4,g4) = 48
    c: DistanceY(g-1,g4) = 81
    c: Coincident(g5,g6)
    c: Coincident(g6,g7)
    c: Coincident(g7,g8)
    c: Coincident(g8,g5)
    c: Horizontal(g5)
    c: Horizontal(g7)
    c: Vertical(g6)
    c: Vertical(g8)
    c: DistanceX(g5,g5) = 94.6
    c: DistanceY(g6,g6) = 25
    c: DistanceX(g2,g7) = 13
    c: Coincident(g12,g5)
    c: Coincident(g11,g6)
    c: Coincident(g10,g7)
    c: Coincident(g9,g5)
    c: Diameter(g10) = 4.5
    c: Equal(g10,g9)
    c: Equal(g10,g11)
    c: Equal(g10,g12)
    c: DistanceY(g2,g10) = 7.5
    c: Coincident(g13,g14)
    c: Coincident(g14,g15)
    c: Coincident(g15,g16)
    c: Coincident(g16,g13)
    c: Horizontal(g13)
    c: Horizontal(g15)
    c: Vertical(g14)
    c: Vertical(g16)
    c: Symmetric(g13,g12,g4)
    c: Symmetric(g14,g10,g4)
    c: Coincident(g19,g15)
    c: Coincident(g17,g13)
    c: Coincident(g18,g13)
    c: Coincident(g20,g14)
    c: Diameter(g17) = 4.5
    c: Equal(g17,g19)
    c: Equal(g17,g20)
    c: Equal(g17,g18)
    c: DistanceY(g22,g21) = 42
    c: Horizontal(g23,g21)
    c: DistanceX(g21,g23) = 58
    c: Vertical(g22,g21)
    c: DistanceX(g22,g10) = 10
    c: DistanceY(g2,g22) = 3
    c: Diameter(g23) = 3.5
    c: Equal(g23,g21)
    c: Equal(g23,g22)
    c: Diameter(g24) = 3.5
    c: Equal(g24,g25)
    c: Equal(g24,g26)
    c: Symmetric(g24,g23,g4)
    c: Symmetric(g25,g21,g4)
    c: Symmetric(g26,g22,g4)
    c: PointOnObject(g27,g4)
    c: Coincident(g28,g11)
    c: Coincident(g28,g17)
    c: PointOnObject(g27,g28)
    c: Diameter(g27) = 6.5
    c: PointOnObject(g27,g-2)
    c: Diameter(g29) = 4.5
    c: DistanceX(g-1,g29) = 60
    c: DistanceY(g-1,g29) = 124
    c: Equal(g29,g30)
    c: Symmetric(g29,g30,g-2)
    c: Diameter(g32) = 3.2
    c: Equal(g32,g31)
    c: Equal(g32,g34)
    c: Equal(g32,g33)
    c: DistanceY(g-1,g32) = 88
    c: DistanceY(g32,g31) = 30.5
    c: DistanceX(g32,g31) = 16.5
    c: DistanceX(g31,g-1) = 37.5
    c: DistanceX(g33,g34) = 16.5
    c: DistanceY(g33,g34) = 30.5
    c: DistanceX(g-1,g33) = 37.5
    c: DistanceY(g-1,g33) = 88
FEATURE [PartDesign::Pad] Pad043
  AllowMultiFace = false
  Direction = (1,1,1)
  Length = 2
  Length2 = 100
  Placement = pos=(0,0,0) rot=(1,0,0;1.5708rad)
  Profile = -> Sketch071
  Type = 0
FEATURE [Sketcher::SketchObject] Sketch072
  FullyConstrained = false
  MapMode = 5
  Support = -> [XY_Plane041]
  sketch-geometry (8):
    g0: LineSegment StartX=2.75 StartY=1.58771 StartZ=0 EndX=-4e-16 EndY=3.17543 EndZ=0
    g1: LineSegment StartX=-4e-16 StartY=3.17543 StartZ=0 EndX=-2.75 EndY=1.58771 EndZ=0
    g2: LineSegment StartX=-2.75 StartY=1.58771 StartZ=0 EndX=-2.75 EndY=-1.58771 EndZ=0
    g3: LineSegment StartX=-2.75 StartY=-1.58771 StartZ=0 EndX=4e-16 EndY=-3.17543 EndZ=0
    g4: LineSegment StartX=4e-16 StartY=-3.17543 StartZ=0 EndX=2.75 EndY=-1.58771 EndZ=0
    g5: LineSegment StartX=2.75 StartY=-1.58771 StartZ=0 EndX=2.75 EndY=1.58771 EndZ=0
    g6: Circle CenterX=0 CenterY=0 CenterZ=0 NormalX=0 NormalY=0 NormalZ=1 AngleXU=0 Radius=3.17543
    g7: Circle CenterX=0 CenterY=0 CenterZ=0 NormalX=0 NormalY=0 NormalZ=1 AngleXU=0 Radius=1.75
  constraints (18):
    c: Coincident(g0,g1)
    c: Coincident(g1,g2)
    c: Coincident(g2,g3)
    c: Coincident(g3,g4)
    c: Coincident(g4,g5)
    c: Coincident(g5,g0)
    c: Equal(g0, g1-g5) x5
    c: PointOnObject(g0,g6)
    c: PointOnObject(g1,g6)
    c: PointOnObject(g2,g6)
    c: PointOnObject(g3,g6)
    c: PointOnObject(g4,g6)
    c: PointOnObject(g5,g6)
    c: Coincident(g6,g-1)
    c: Vertical(g5)
    c: Distance(g1,g0) = 5.5
    c: Coincident(g7,g-1)
    c: Diameter(g7) = 3.5
FEATURE [PartDesign::Pad] Pad044
  AllowMultiFace = false
  Direction = (1,1,1)
  Length = 16
  Length2 = 100
  Profile = -> Sketch072
  Type = 0
FEATURE [PartDesign::Body] Body029  label="16mm Standoff"
  Group = -> [Sketch072,Pad044]
  Origin = -> Origin041
  Placement = pos=(-125,-13,84) rot=(1,0,0;1.5708rad)
  Tip = -> Pad044
FEATURE [Sketcher::SketchObject] Sketch073
  FullyConstrained = false
  MapMode = 5
  Support = -> [XY_Plane042]
  sketch-geometry (8):
    g0: LineSegment StartX=2.75 StartY=1.58771 StartZ=0 EndX=-4e-16 EndY=3.17543 EndZ=0
    g1: LineSegment StartX=-4e-16 StartY=3.17543 StartZ=0 EndX=-2.75 EndY=1.58771 EndZ=0
    g2: LineSegment StartX=-2.75 StartY=1.58771 StartZ=0 EndX=-2.75 EndY=-1.58771 EndZ=0
    g3: LineSegment StartX=-2.75 StartY=-1.58771 StartZ=0 EndX=4e-16 EndY=-3.17543 EndZ=0
    g4: LineSegment StartX=4e-16 StartY=-3.17543 StartZ=0 EndX=2.75 EndY=-1.58771 EndZ=0
    g5: LineSegment StartX=2.75 StartY=-1.58771 StartZ=0 EndX=2.75 EndY=1.58771 EndZ=0
    g6: Circle CenterX=0 CenterY=0 CenterZ=0 NormalX=0 NormalY=0 NormalZ=1 AngleXU=0 Radius=3.17543
    g7: Circle CenterX=0 CenterY=0 CenterZ=0 NormalX=0 NormalY=0 NormalZ=1 AngleXU=0 Radius=1.75
  constraints (18):
    c: Coincident(g0,g1)
    c: Coincident(g1,g2)
    c: Coincident(g2,g3)
    c: Coincident(g3,g4)
    c: Coincident(g4,g5)
    c: Coincident(g5,g0)
    c: Equal(g0, g1-g5) x5
    c: PointOnObject(g0,g6)
    c: PointOnObject(g1,g6)
    c: PointOnObject(g2,g6)
    c: PointOnObject(g3,g6)
    c: PointOnObject(g4,g6)
    c: PointOnObject(g5,g6)
    c: Coincident(g6,g-1)
    c: Vertical(g5)
    c: Distance(g1,g0) = 5.5
    c: Coincident(g7,g-1)
    c: Diameter(g7) = 3.5
FEATURE [PartDesign::Pad] Pad045
  AllowMultiFace = false
  Direction = (1,1,1)
  Length = 16
  Length2 = 100
  Profile = -> Sketch073
  Type = 0
FEATURE [PartDesign::Body] Body030  label="16mm Standoff001"
  Group = -> [Sketch073,Pad045]
  Origin = -> Origin042
  Placement = pos=(-125,-13,126) rot=(1,0,0;1.5708rad)
  Tip = -> Pad045
FEATURE [Sketcher::SketchObject] Sketch074
  FullyConstrained = false
  MapMode = 5
  Support = -> [XY_Plane043]
  sketch-geometry (8):
    g0: LineSegment StartX=2.75 StartY=1.58771 StartZ=0 EndX=-4e-16 EndY=3.17543 EndZ=0
    g1: LineSegment StartX=-4e-16 StartY=3.17543 StartZ=0 EndX=-2.75 EndY=1.58771 EndZ=0
    g2: LineSegment StartX=-2.75 StartY=1.58771 StartZ=0 EndX=-2.75 EndY=-1.58771 EndZ=0
    g3: LineSegment StartX=-2.75 StartY=-1.58771 StartZ=0 EndX=4e-16 EndY=-3.17543 EndZ=0
    g4: LineSegment StartX=4e-16 StartY=-3.17543 StartZ=0 EndX=2.75 EndY=-1.58771 EndZ=0
    g5: LineSegment StartX=2.75 StartY=-1.58771 StartZ=0 EndX=2.75 EndY=1.58771 EndZ=0
    g6: Circle CenterX=0 CenterY=0 CenterZ=0 NormalX=0 NormalY=0 NormalZ=1 AngleXU=0 Radius=3.17543
    g7: Circle CenterX=0 CenterY=0 CenterZ=0 NormalX=0 NormalY=0 NormalZ=1 AngleXU=0 Radius=1.75
  constraints (18):
    c: Coincident(g0,g1)
    c: Coincident(g1,g2)
    c: Coincident(g2,g3)
    c: Coincident(g3,g4)
    c: Coincident(g4,g5)
    c: Coincident(g5,g0)
    c: Equal(g0, g1-g5) x5
    c: PointOnObject(g0,g6)
    c: PointOnObject(g1,g6)
    c: PointOnObject(g2,g6)
    c: PointOnObject(g3,g6)
    c: PointOnObject(g4,g6)
    c: PointOnObject(g5,g6)
    c: Coincident(g6,g-1)
    c: Vertical(g5)
    c: Distance(g1,g0) = 5.5
    c: Coincident(g7,g-1)
    c: Diameter(g7) = 3.5
FEATURE [PartDesign::Pad] Pad046
  AllowMultiFace = false
  Direction = (1,1,1)
  Length = 16
  Length2 = 100
  Profile = -> Sketch074
  Type = 0
FEATURE [PartDesign::Body] Body031  label="16mm Standoff002"
  Group = -> [Sketch074,Pad046]
  Origin = -> Origin043
  Placement = pos=(-67,-13,126) rot=(1,0,0;1.5708rad)
  Tip = -> Pad046
FEATURE [Sketcher::SketchObject] Sketch077
  FullyConstrained = false
  MapMode = 5
  Support = -> [XY_Plane045]
  sketch-geometry (2):
    g0: Circle CenterX=0 CenterY=0 CenterZ=0 NormalX=0 NormalY=0 NormalZ=1 AngleXU=0 Radius=5.85
    g1: Circle CenterX=0 CenterY=0 CenterZ=0 NormalX=0 NormalY=0 NormalZ=1 AngleXU=0 Radius=3
  constraints (4):
    c: Coincident(g1,g0)
    c: Coincident(g1,g-1)
    c: Diameter(g1) = 6
    c: Diameter(g0) = 11.7
FEATURE [PartDesign::Pad] Pad049
  AllowMultiFace = false
  Direction = (1,1,1)
  Length = 1.5
  Length2 = 100
  Profile = -> Sketch077
  Type = 0
FEATURE [PartDesign::Body] Body033  label="M6_Washer003"
  Group = -> [Sketch077,Pad049]
  Origin = -> Origin045
  Placement = pos=(0,81,101) rot=(-1,0,0;1.5708rad)
  Tip = -> Pad049
FEATURE [Sketcher::SketchObject] Sketch078
  FullyConstrained = false
  MapMode = 5
  Support = -> [XY_Plane046]
  sketch-geometry (8):
    g0: LineSegment StartX=0 StartY=5.7735 StartZ=0 EndX=-5 EndY=2.88675 EndZ=0
    g1: LineSegment StartX=-5 StartY=2.88675 StartZ=0 EndX=-5 EndY=-2.88675 EndZ=0
    g2: LineSegment StartX=-5 StartY=-2.88675 StartZ=0 EndX=-1.501e-13 EndY=-5.7735 EndZ=0
    g3: LineSegment StartX=-1.501e-13 StartY=-5.7735 StartZ=0 EndX=5 EndY=-2.88675 EndZ=0
    g4: LineSegment StartX=5 StartY=-2.88675 StartZ=0 EndX=5 EndY=2.88675 EndZ=0
    g5: LineSegment StartX=5 StartY=2.88675 StartZ=0 EndX=0 EndY=5.7735 EndZ=0
    g6: Circle CenterX=0 CenterY=0 CenterZ=0 NormalX=0 NormalY=0 NormalZ=1 AngleXU=0 Radius=5.7735
    g7: Circle CenterX=0 CenterY=0 CenterZ=0 NormalX=0 NormalY=0 NormalZ=1 AngleXU=0 Radius=3
  constraints (18):
    c: Coincident(g0,g1)
    c: Coincident(g1,g2)
    c: Coincident(g2,g3)
    c: Coincident(g3,g4)
    c: Coincident(g4,g5)
    c: Coincident(g5,g0)
    c: Equal(g0, g1-g5) x5
    c: PointOnObject(g0,g6)
    c: PointOnObject(g1,g6)
    c: PointOnObject(g2,g6)
    c: PointOnObject(g3,g6)
    c: PointOnObject(g4,g6)
    c: PointOnObject(g5,g6)
    c: Coincident(g6,g-1)
    c: PointOnObject(g0,g-2)
    c: Distance(g0,g4) = 10
    c: Coincident(g7,g-1)
    c: Diameter(g7) = 6
FEATURE [PartDesign::Pad] Pad050
  AllowMultiFace = false
  Direction = (1,1,1)
  Length = 5
  Length2 = 100
  Profile = -> Sketch078
  Type = 0
FEATURE [PartDesign::Body] Body034  label="M6_Full_Nut002"
  Group = -> [Sketch078,Pad050]
  Origin = -> Origin046
  Placement = pos=(0,82.6,101) rot=(-1,0,0;1.5708rad)
  Tip = -> Pad050
FEATURE [Sketcher::SketchObject] Sketch079
  FullyConstrained = false
  MapMode = 5
  Support = -> [XY_Plane047]
  sketch-geometry (8):
    g0: LineSegment StartX=0 StartY=5.7735 StartZ=0 EndX=-5 EndY=2.88675 EndZ=0
    g1: LineSegment StartX=-5 StartY=2.88675 StartZ=0 EndX=-5 EndY=-2.88675 EndZ=0
    g2: LineSegment StartX=-5 StartY=-2.88675 StartZ=0 EndX=-1.501e-13 EndY=-5.7735 EndZ=0
    g3: LineSegment StartX=-1.501e-13 StartY=-5.7735 StartZ=0 EndX=5 EndY=-2.88675 EndZ=0
    g4: LineSegment StartX=5 StartY=-2.88675 StartZ=0 EndX=5 EndY=2.88675 EndZ=0
    g5: LineSegment StartX=5 StartY=2.88675 StartZ=0 EndX=0 EndY=5.7735 EndZ=0
    g6: Circle CenterX=0 CenterY=0 CenterZ=0 NormalX=0 NormalY=0 NormalZ=1 AngleXU=0 Radius=5.7735
    g7: Circle CenterX=0 CenterY=0 CenterZ=0 NormalX=0 NormalY=0 NormalZ=1 AngleXU=0 Radius=3
  constraints (18):
    c: Coincident(g0,g1)
    c: Coincident(g1,g2)
    c: Coincident(g2,g3)
    c: Coincident(g3,g4)
    c: Coincident(g4,g5)
    c: Coincident(g5,g0)
    c: Equal(g0, g1-g5) x5
    c: PointOnObject(g0,g6)
    c: PointOnObject(g1,g6)
    c: PointOnObject(g2,g6)
    c: PointOnObject(g3,g6)
    c: PointOnObject(g4,g6)
    c: PointOnObject(g5,g6)
    c: Coincident(g6,g-1)
    c: PointOnObject(g0,g-2)
    c: Distance(g0,g4) = 10
    c: Coincident(g7,g-1)
    c: Diameter(g7) = 6
FEATURE [PartDesign::Pad] Pad051
  AllowMultiFace = false
  Direction = (1,1,1)
  Length = 5
  Length2 = 100
  Profile = -> Sketch079
  Type = 0
FEATURE [PartDesign::Body] Body035  label="M6_Full_Nut003"
  Group = -> [Sketch079,Pad051]
  Origin = -> Origin047
  Placement = pos=(0,87.6,101) rot=(-0.935113,-0.250563,-0.250563;1.63783rad)
  Tip = -> Pad051
FEATURE [Sketcher::SketchObject] Sketch080
  FullyConstrained = true
  MapMode = 5
  Placement = pos=(0,0,0) rot=(1,0,0;1.5708rad)
  Support = -> [XZ_Plane048]
  sketch-geometry (20):
    g0: LineSegment StartX=-40 StartY=163 StartZ=0 EndX=40 EndY=163 EndZ=0
    g1: LineSegment StartX=40 StartY=163 StartZ=0 EndX=40 EndY=18 EndZ=0
    g2: LineSegment StartX=40 StartY=18 StartZ=0 EndX=-40 EndY=18 EndZ=0
    g3: LineSegment StartX=-40 StartY=18 StartZ=0 EndX=-40 EndY=163 EndZ=0
    g4: Circle CenterX=0 CenterY=101 CenterZ=0 NormalX=0 NormalY=0 NormalZ=1 AngleXU=0 Radius=3.25
    g5: Circle CenterX=-15 CenterY=23 CenterZ=0 NormalX=0 NormalY=0 NormalZ=1 AngleXU=0 Radius=2.25
    g6: Circle CenterX=15 CenterY=23 CenterZ=0 NormalX=0 NormalY=0 NormalZ=1 AngleXU=0 Radius=2.25
    g7: LineSegment StartX=-40 StartY=23 StartZ=0 EndX=-15 EndY=23 EndZ=0
    g8: LineSegment StartX=-15 StartY=23 StartZ=0 EndX=15 EndY=23 EndZ=0
    g9: LineSegment StartX=15 StartY=23 StartZ=0 EndX=40 EndY=23 EndZ=0
    g10: LineSegment StartX=-35 StartY=105 StartZ=0 EndX=35 EndY=105 EndZ=0
    g11: LineSegment StartX=35 StartY=105 StartZ=0 EndX=35 EndY=45 EndZ=0
    g12: LineSegment StartX=35 StartY=45 StartZ=0 EndX=-35 EndY=45 EndZ=0
    g13: LineSegment StartX=-35 StartY=45 StartZ=0 EndX=-35 EndY=105 EndZ=0
    g14: Circle CenterX=-35 CenterY=105 CenterZ=0 NormalX=0 NormalY=0 NormalZ=1 AngleXU=0 Radius=2.25
    g15: Circle CenterX=35 CenterY=105 CenterZ=0 NormalX=0 NormalY=0 NormalZ=1 AngleXU=0 Radius=2.25
    g16: Circle CenterX=35 CenterY=45 CenterZ=0 NormalX=0 NormalY=0 NormalZ=1 AngleXU=0 Radius=2.25
    g17: Circle CenterX=-35 CenterY=45 CenterZ=0 NormalX=0 NormalY=0 NormalZ=1 AngleXU=0 Radius=2.25
    g18: Circle CenterX=5 CenterY=156 CenterZ=0 NormalX=0 NormalY=0 NormalZ=1 AngleXU=0 Radius=2.25
    g19: Circle CenterX=-5 CenterY=156 CenterZ=0 NormalX=0 NormalY=0 NormalZ=1 AngleXU=0 Radius=2.25
  constraints (53):
    c: Coincident(g0,g1)
    c: Coincident(g1,g2)
    c: Coincident(g2,g3)
    c: Coincident(g3,g0)
    c: Horizontal(g0)
    c: Vertical(g1)
    c: Vertical(g3)
    c: DistanceY(g-1,g2) = 18
    c: Coincident(g7,g8)
    c: Coincident(g8,g9)
    c: Horizontal(g9)
    c: Horizontal(g8)
    c: Horizontal(g7)
    c: Equal(g7,g9)
    c: PointOnObject(g7,g3)
    c: PointOnObject(g9,g1)
    c: Diameter(g5) = 4.5
    c: Equal(g5,g6)
    c: Coincident(g5,g7)
    c: Coincident(g6,g8)
    c: DistanceX(g8,g8) = 30
    c: DistanceY(g1,g9) = 5
    c: DistanceX(g2,g2) = 80
    c: DistanceY(g1,g1) = 145
    c: DistanceY(g2,g4) = 83
    c: DistanceX(g2,g4) = 40
    c: Diameter(g4) = 6.5
    c: Coincident(g10,g11)
    c: Coincident(g11,g12)
    c: Coincident(g12,g13)
    c: Coincident(g13,g10)
    c: Horizontal(g10)
    c: Horizontal(g12)
    c: Vertical(g11)
    c: Vertical(g13)
    c: Coincident(g16,g11)
    c: Coincident(g15,g10)
    c: Coincident(g14,g10)
    c: Coincident(g12,g17)
    c: Diameter(g17) = 4.5
    c: Equal(g17,g14)
    c: Equal(g17,g15)
    c: Equal(g17,g16)
    c: DistanceX(g12,g12) = 70
    c: DistanceY(g13,g13) = 60
    c: DistanceY(g2,g17) = 27
    c: DistanceX(g2,g17) = 5
    c: Symmetric(g2,g1,g-2)
    c: DistanceX(g-1,g18) = 5
    c: DistanceY(g-1,g18) = 156
    c: Diameter(g18) = 4.5
    c: Equal(g19,g18)
    c: Symmetric(g19,g18,g-2)
FEATURE [PartDesign::Pad] Pad052
  AllowMultiFace = false
  Direction = (1,1,1)
  Length = 2
  Length2 = 100
  Placement = pos=(0,0,0) rot=(1,0,0;1.5708rad)
  Profile = -> Sketch080
  Type = 0
FEATURE [PartDesign::Body] Body036  label="Battery_Side_Plate"
  Group = -> [Sketch080,Pad052]
  Origin = -> Origin048
  Placement = pos=(0,39,0) rot=(0,0,1;0rad)
  Tip = -> Pad052
FEATURE [Sketcher::SketchObject] Sketch084
  FullyConstrained = false
  MapMode = 5
  Support = -> [XY_Plane051]
  sketch-geometry (8):
    g0: LineSegment StartX=0 StartY=5.7735 StartZ=0 EndX=-5 EndY=2.88675 EndZ=0
    g1: LineSegment StartX=-5 StartY=2.88675 StartZ=0 EndX=-5 EndY=-2.88675 EndZ=0
    g2: LineSegment StartX=-5 StartY=-2.88675 StartZ=0 EndX=-1.501e-13 EndY=-5.7735 EndZ=0
    g3: LineSegment StartX=-1.501e-13 StartY=-5.7735 StartZ=0 EndX=5 EndY=-2.88675 EndZ=0
    g4: LineSegment StartX=5 StartY=-2.88675 StartZ=0 EndX=5 EndY=2.88675 EndZ=0
    g5: LineSegment StartX=5 StartY=2.88675 StartZ=0 EndX=0 EndY=5.7735 EndZ=0
    g6: Circle CenterX=0 CenterY=0 CenterZ=0 NormalX=0 NormalY=0 NormalZ=1 AngleXU=0 Radius=5.7735
    g7: Circle CenterX=0 CenterY=0 CenterZ=0 NormalX=0 NormalY=0 NormalZ=1 AngleXU=0 Radius=3
  constraints (18):
    c: Coincident(g0,g1)
    c: Coincident(g1,g2)
    c: Coincident(g2,g3)
    c: Coincident(g3,g4)
    c: Coincident(g4,g5)
    c: Coincident(g5,g0)
    c: Equal(g0, g1-g5) x5
    c: PointOnObject(g0,g6)
    c: PointOnObject(g1,g6)
    c: PointOnObject(g2,g6)
    c: PointOnObject(g3,g6)
    c: PointOnObject(g4,g6)
    c: PointOnObject(g5,g6)
    c: Coincident(g6,g-1)
    c: PointOnObject(g0,g-2)
    c: Distance(g0,g4) = 10
    c: Coincident(g7,g-1)
    c: Diameter(g7) = 6
FEATURE [PartDesign::Pad] Pad056
  AllowMultiFace = false
  Direction = (1,1,1)
  Length = 5
  Length2 = 100
  Profile = -> Sketch084
  Type = 0
FEATURE [PartDesign::Body] Body039  label="M6_Full_Nut004"
  Group = -> [Sketch084,Pad056]
  Origin = -> Origin051
  Placement = pos=(1e-15,38.6,101) rot=(-1,0,0;1.5708rad)
  Tip = -> Pad056
FEATURE [Sketcher::SketchObject] Sketch085
  FullyConstrained = false
  MapMode = 5
  Placement = pos=(0,0,0) rot=(1,0,0;1.5708rad)
  Support = -> [XZ_Plane052]
  sketch-geometry (15):
    g0: LineSegment StartX=-40 StartY=130 StartZ=0 EndX=70 EndY=130 EndZ=0
    g1: LineSegment StartX=70 StartY=130 StartZ=0 EndX=70 EndY=30 EndZ=0
    g2: LineSegment StartX=70 StartY=30 StartZ=0 EndX=60 EndY=30 EndZ=0
    g3: LineSegment StartX=60 StartY=30 StartZ=0 EndX=30 EndY=60 EndZ=0
    g4: LineSegment StartX=30 StartY=60 StartZ=0 EndX=-40 EndY=60 EndZ=0
    g5: LineSegment StartX=-40 StartY=60 StartZ=0 EndX=-40 EndY=130 EndZ=0
    g6: Circle CenterX=65 CenterY=110 CenterZ=0 NormalX=0 NormalY=0 NormalZ=1 AngleXU=0 Radius=2.25
    g7: Circle CenterX=65 CenterY=45 CenterZ=0 NormalX=0 NormalY=0 NormalZ=1 AngleXU=0 Radius=2.25
    g8: LineSegment StartX=65 StartY=105 StartZ=0 EndX=65 EndY=45 EndZ=0
    g9: LineSegment StartX=65 StartY=45 StartZ=0 EndX=70 EndY=30 EndZ=0
    g10: LineSegment StartX=-40 StartY=130 StartZ=0 EndX=-35 EndY=115 EndZ=0
    g11: LineSegment StartX=-35 StartY=115 StartZ=0 EndX=-35 EndY=74.9999 EndZ=0
    g12: LineSegment StartX=-35 StartY=74.9999 StartZ=0 EndX=-40 EndY=59.9999 EndZ=0
    g13: Circle CenterX=-35 CenterY=115 CenterZ=0 NormalX=0 NormalY=0 NormalZ=1 AngleXU=0 Radius=2.25
    g14: Circle CenterX=-35 CenterY=74.9999 CenterZ=0 NormalX=0 NormalY=0 NormalZ=1 AngleXU=0 Radius=2.25
  constraints (37):
    c: Coincident(g0,g1)
    c: Coincident(g1,g2)
    c: Coincident(g2,g3)
    c: Coincident(g3,g4)
    c: Coincident(g5,g0)
    c: Vertical(g5)
    c: Horizontal(g0)
    c: Horizontal(g4)
    c: Horizontal(g2)
    c: Vertical(g1)
    c: DistanceY(g-1,g0) = 130
    c: DistanceY(g5,g5) = 70
    c: DistanceX(g0,g0) = 110
    c: DistanceY(g1,g1) = 100
    c: DistanceX(g2,g2) = 10
    c: DistanceX(g4,g4) = 70
    c: DistanceX(g4,g-1) = 40
    c: Diameter(g6) = 4.5
    c: Equal(g6,g7)
    c: Coincident(g8,g9)
    c: Coincident(g9,g1)
    c: Vertical(g8)
    c: DistanceX(g8,g1) = 5
    c: DistanceY(g8,g8) = 60
    c: Coincident(g7,g8)
    c: Coincident(g10,g11)
    c: Coincident(g11,g12)
    c: Coincident(g10,g0)
    c: Vertical(g11)
    c: Equal(g10,g12)
    c: DistanceX(g0,g10) = 5
    c: DistanceY(g11,g11) = 40
    c: Coincident(g11,g14)
    c: Coincident(g13,g10)
    c: Diameter(g13) = 4.5
    c: Equal(g13,g14)
    c: DistanceY(g1,g7) = 15
FEATURE [PartDesign::Pad] Pad057
  AllowMultiFace = false
  Direction = (1,1,1)
  Length = 2
  Length2 = 100
  Placement = pos=(0,0,0) rot=(1,0,0;1.5708rad)
  Profile = -> Sketch085
  Type = 0
FEATURE [PartDesign::Body] Body040  label="attach_plate"
  Group = -> [Sketch085,Pad057]
  Origin = -> Origin052
  Placement = pos=(0,17,0) rot=(0,0,1;0rad)
  Tip = -> Pad057
FEATURE [PartDesign::FeatureBase] Clone
  BaseFeature = -> Body040
FEATURE [PartDesign::Body] Body041  label="attach_plate2"
  BaseFeature = -> Body040
  Group = -> [Clone]
  Origin = -> Origin054
  Placement = pos=(0,-15,0) rot=(0,0,1;0rad)
  Tip = -> Clone
FEATURE [PartDesign::FeatureBase] Clone001
  BaseFeature = -> Body036
FEATURE [PartDesign::Body] Body042  label="Battery_Side_Plate2"
  BaseFeature = -> Body036
  Group = -> [Clone001]
  Origin = -> Origin056
  Placement = pos=(0,-37,0) rot=(0,0,1;0rad)
  Tip = -> Clone001
FEATURE [Sketcher::SketchObject] Sketch086
  FullyConstrained = false
  MapMode = 5
  Placement = pos=(0,0,0) rot=(1,0,0;1.5708rad)
  Support = -> [XZ_Plane058]
  sketch-geometry (9):
    g0: LineSegment StartX=-5.01868 StartY=40 StartZ=0 EndX=4.98132 EndY=40 EndZ=0
    g1: LineSegment StartX=4.98132 StartY=40 StartZ=0 EndX=4.98132 EndY=-30 EndZ=0
    g2: LineSegment StartX=4.98132 StartY=-30 StartZ=0 EndX=-5.01868 EndY=-30 EndZ=0
    g3: LineSegment StartX=-5.01868 StartY=-30 StartZ=0 EndX=-5.01868 EndY=40 EndZ=0
    g4: LineSegment StartX=-5.01868 StartY=40 StartZ=0 EndX=-0.0186846 EndY=25 EndZ=0
    g5: LineSegment StartX=-0.0186846 StartY=25 StartZ=0 EndX=-0.0186846 EndY=-15 EndZ=0
    g6: LineSegment StartX=-0.0186846 StartY=-15 StartZ=0 EndX=-5.01868 EndY=-30 EndZ=0
    g7: Circle CenterX=-0.0186846 CenterY=25 CenterZ=0 NormalX=0 NormalY=0 NormalZ=1 AngleXU=0 Radius=2.25
    g8: Circle CenterX=-0.0186846 CenterY=-15 CenterZ=0 NormalX=0 NormalY=0 NormalZ=1 AngleXU=0 Radius=2.25
  constraints (23):
    c: Coincident(g0,g1)
    c: Coincident(g1,g2)
    c: Coincident(g2,g3)
    c: Coincident(g3,g0)
    c: Horizontal(g0)
    c: Horizontal(g2)
    c: Vertical(g1)
    c: Vertical(g3)
    c: DistanceY(g3,g3) = 70
    c: DistanceX(g2,g2) = 10
    c: Coincident(g4,g5)
    c: Coincident(g5,g6)
    c: Coincident(g6,g2)
    c: Coincident(g4,g0)
    c: Equal(g4,g6)
    c: DistanceX(g2,g5) = 5
    c: Vertical(g5)
    c: DistanceY(g5,g5) = 40
    c: Coincident(g7,g4)
    c: Coincident(g8,g5)
    c: Diameter(g8) = 4.5
    c: Equal(g8,g7)
    c: DistanceY(g2,g-1) = 30
FEATURE [PartDesign::Pad] Pad058
  AllowMultiFace = false
  Direction = (1,1,1)
  Length = 30
  Length2 = 100
  Midplane = true
  Placement = pos=(0,0,0) rot=(1,0,0;1.5708rad)
  Profile = -> Sketch086
  Type = 0
FEATURE [Sketcher::SketchObject] Sketch087
  FullyConstrained = false
  MapMode = 5
  Placement = pos=(-5.01868,0,0) rot=(0.707107,0,-0.707107;3.14159rad)
  Support = -> [Pad058]
  sketch-geometry (10):
    g0: Circle CenterX=-17.5 CenterY=0 CenterZ=0 NormalX=0 NormalY=0 NormalZ=1 AngleXU=0 Radius=2.25
    g1: Circle CenterX=7.5 CenterY=0 CenterZ=0 NormalX=0 NormalY=0 NormalZ=1 AngleXU=0 Radius=2.25
    g2: Circle CenterX=-35 CenterY=10 CenterZ=0 NormalX=0 NormalY=0 NormalZ=1 AngleXU=0 Radius=1.75
    g3: Circle CenterX=-35 CenterY=-10 CenterZ=0 NormalX=0 NormalY=0 NormalZ=1 AngleXU=0 Radius=1.75
    g4: Circle CenterX=25 CenterY=10 CenterZ=0 NormalX=0 NormalY=0 NormalZ=1 AngleXU=0 Radius=1.75
    g5: Circle CenterX=25 CenterY=-10 CenterZ=0 NormalX=0 NormalY=0 NormalZ=1 AngleXU=0 Radius=1.75
    g6: LineSegment StartX=-35 StartY=10 StartZ=0 EndX=25 EndY=10 EndZ=0
    g7: LineSegment StartX=25 StartY=10 StartZ=0 EndX=25 EndY=-10 EndZ=0
    g8: LineSegment StartX=25 StartY=-10 StartZ=0 EndX=-35 EndY=-10 EndZ=0
    g9: LineSegment StartX=-35 StartY=-10 StartZ=0 EndX=-35 EndY=10 EndZ=0
  constraints (25):
    c: Diameter(g0) = 4.5
    c: Equal(g0,g1)
    c: PointOnObject(g1,g-1)
    c: DistanceX(g0,g1) = 25
    c: DistanceX(g-1,g1) = 7.5
    c: Coincident(g6,g7)
    c: Coincident(g7,g8)
    c: Coincident(g8,g9)
    c: Coincident(g9,g6)
    c: Horizontal(g6)
    c: Horizontal(g8)
    c: Vertical(g7)
    c: Coincident(g6,g4)
    c: Coincident(g7,g5)
    c: Coincident(g3,g8)
    c: Coincident(g2,g6)
    c: Symmetric(g2,g3,g-1)
    c: DistanceX(g8,g8) = 60
    c: DistanceX(g-1,g5) = 25
    c: Diameter(g3) = 3.5
    c: Equal(g3,g2)
    c: Equal(g3,g4)
    c: Equal(g3,g5)
    c: DistanceY(g9,g9) = 20
    c: PointOnObject(g0,g-1)
FEATURE [PartDesign::Pocket] Pocket021
  AllowMultiFace = false
  BaseFeature = -> Pad058
  Length = 25
  Length2 = 100
  Placement = pos=(0,0,0) rot=(1,0,0;1.5708rad)
  Profile = -> Sketch087
  Type = 0
FEATURE [Sketcher::SketchObject] Sketch088
  FullyConstrained = false
  MapMode = 5
  Support = -> [XY_Plane059]
  sketch-geometry (4):
    g0: LineSegment StartX=-75 StartY=37.5 StartZ=0 EndX=75 EndY=37.5 EndZ=0
    g1: LineSegment StartX=75 StartY=37.5 StartZ=0 EndX=75 EndY=-37.5 EndZ=0
    g2: LineSegment StartX=75 StartY=-37.5 StartZ=0 EndX=-75 EndY=-37.5 EndZ=0
    g3: LineSegment StartX=-75 StartY=-37.5 StartZ=0 EndX=-75 EndY=37.5 EndZ=0
  constraints (11):
    c: Coincident(g0,g1)
    c: Coincident(g1,g2)
    c: Coincident(g2,g3)
    c: Coincident(g3,g0)
    c: Horizontal(g0)
    c: Horizontal(g2)
    c: Vertical(g1)
    c: Vertical(g3)
    c: DistanceX(g0,g0) = 150
    c: DistanceY(g3,g3) = 75
    c: Symmetric(g0,g1,g-1)
FEATURE [PartDesign::Pad] Pad059
  AllowMultiFace = false
  Direction = (1,1,1)
  Length = 75
  Length2 = 100
  Profile = -> Sketch088
  Type = 0
FEATURE [PartDesign::Body] Body044  label="Sheep001"
  Group = -> [Sketch088,Pad059]
  Origin = -> Origin059
  Tip = -> Pad059
FEATURE [App::Part] Part005  label="Sheep"
  Group = -> [Body044]
  Origin = -> Origin057
  Placement = pos=(-225,0,-39) rot=(0,0,1;0rad)
FEATURE [PartDesign::FeatureBase] Clone002
  BaseFeature = -> Body023
  Placement = pos=(-17,-1e-15,81) rot=(0,0,1;3.14159rad)
FEATURE [PartDesign::Body] Body045  label="Servo_Mount_End2"
  BaseFeature = -> Body023
  Group = -> [Clone002]
  Origin = -> Origin061
  Placement = pos=(0,0,0) rot=(0,0,1;3.14159rad)
  Tip = -> Clone002
FEATURE [PartDesign::FeatureBase] Clone003
  BaseFeature = -> Body013
  Placement = pos=(-58.5,-1e-15,88.5) rot=(1,0,0;3.14159rad)
FEATURE [PartDesign::Body] Body046  label="MG996_2"
  BaseFeature = -> Body013
  Group = -> [Clone003]
  Origin = -> Origin062
  Placement = pos=(0,0,0) rot=(0,0,1;3.14159rad)
  Tip = -> Clone003
FEATURE [PartDesign::FeatureBase] Clone004
  BaseFeature = -> Body019
  Placement = pos=(-100,0,81) rot=(0,0,1;0rad)
FEATURE [PartDesign::Body] Body047  label="End_Bearing_Block2"
  BaseFeature = -> Body019
  Group = -> [Clone004]
  Origin = -> Origin063
  Placement = pos=(0,0,0) rot=(0,0,1;3.14159rad)
  Tip = -> Clone004
FEATURE [PartDesign::FeatureBase] Clone005
  BaseFeature = -> Body010
  Placement = pos=(-48,-2.22e-14,68) rot=(0,0,-1;1.5708rad)
FEATURE [PartDesign::Body] Body048  label="Servo Gear2"
  BaseFeature = -> Body010
  Group = -> [Clone005]
  Origin = -> Origin064
  Placement = pos=(96,0,0) rot=(0,0,1;0rad)
  Tip = -> Clone005
FEATURE [PartDesign::FeatureBase] Clone006
  BaseFeature = -> Body012
  Placement = pos=(-48,0,72.5) rot=(0,0,1;0rad)
FEATURE [PartDesign::Body] Body049  label="Servo Horn2"
  BaseFeature = -> Body012
  Group = -> [Clone006]
  Origin = -> Origin065
  Placement = pos=(96,0,0) rot=(0,0,1;0rad)
  Tip = -> Clone006
FEATURE [Sketcher::SketchObject] Sketch089
  FullyConstrained = false
  MapMode = 5
  Support = -> [XY_Plane067]
  sketch-geometry (1):
    g0: Circle CenterX=0 CenterY=0 CenterZ=0 NormalX=0 NormalY=0 NormalZ=1 AngleXU=0 Radius=41.6542
  constraints (1):
    c: Coincident(g0,g-1)
FEATURE [PartDesign::Body] Body050
  Group = -> [Sketch089]
  Origin = -> Origin067
FEATURE [App::Part] Part007  label="wheel"
  Group = -> [Body,Body001,Body007,Body008,Body009,Body014,Body017,Body020,Body015,Body016,Body018,Body021,Body022,Body050]
  Origin = -> Origin066
  Placement = pos=(-100,72,0) rot=(0,0,1;0rad)
FEATURE [Sketcher::SketchObject] Sketch090
  FullyConstrained = false
  MapMode = 5
  Support = -> [XY_Plane068]
  sketch-geometry (1):
    g0: Circle CenterX=0 CenterY=0 CenterZ=0 NormalX=0 NormalY=0 NormalZ=1 AngleXU=0 Radius=7.5
  constraints (2):
    c: Coincident(g0,g-1)
    c: Diameter(g0) = 15
FEATURE [PartDesign::Pad] Pad060
  AllowMultiFace = false
  Direction = (1,1,1)
  Length = 2.5
  Length2 = 100
  Profile = -> Sketch090
  Type = 0
FEATURE [PartDesign::Chamfer] Chamfer
  Angle = 45
  Base = -> Pad060 [Edge3]
  BaseFeature = -> Pad060
  ChamferType = 0
  FlipDirection = false
  Size = 1
  Size2 = 1
  SupportTransform = false
FEATURE [Sketcher::SketchObject] Sketch091
  FullyConstrained = false
  MapMode = 5
  Placement = pos=(0,0,2.5) rot=(0,0,1;0rad)
  Support = -> [Chamfer]
  sketch-geometry (7):
    g0: LineSegment StartX=1.1547 StartY=2 StartZ=0 EndX=-1.1547 EndY=2 EndZ=0
    g1: LineSegment StartX=-1.1547 StartY=2 StartZ=0 EndX=-2.3094 EndY=7.81568e-11 EndZ=0
    g2: LineSegment StartX=-2.3094 StartY=7.81569e-11 StartZ=0 EndX=-1.1547 EndY=-2 EndZ=0
    g3: LineSegment StartX=-1.1547 StartY=-2 StartZ=0 EndX=1.1547 EndY=-2 EndZ=0
    g4: LineSegment StartX=1.1547 StartY=-2 StartZ=0 EndX=2.3094 EndY=0 EndZ=0
    g5: LineSegment StartX=2.3094 StartY=0 StartZ=0 EndX=1.1547 EndY=2 EndZ=0
    g6: Circle CenterX=0 CenterY=0 CenterZ=0 NormalX=0 NormalY=0 NormalZ=1 AngleXU=0 Radius=2.3094
  constraints (16):
    c: Coincident(g0,g1)
    c: Coincident(g1,g2)
    c: Coincident(g2,g3)
    c: Coincident(g3,g4)
    c: Coincident(g4,g5)
    c: Coincident(g5,g0)
    c: Equal(g0, g1-g5) x5
    c: PointOnObject(g0,g6)
    c: PointOnObject(g1,g6)
    c: PointOnObject(g2,g6)
    c: PointOnObject(g3,g6)
    c: PointOnObject(g4,g6)
    c: PointOnObject(g5,g6)
    c: Coincident(g6,g-1)
    c: Distance(g0,g4) = 4
    c: PointOnObject(g4,g-1)
FEATURE [PartDesign::Pocket] Pocket022
  AllowMultiFace = false
  BaseFeature = -> Chamfer
  Length = 2
  Length2 = 100
  Profile = -> Sketch091
  Type = 0
FEATURE [Sketcher::SketchObject] Sketch092
  FullyConstrained = false
  MapMode = 5
  Placement = pos=(0,0,0) rot=(1,0,0;3.14159rad)
  Support = -> [Pocket022]
  sketch-geometry (1):
    g0: Circle CenterX=0 CenterY=0 CenterZ=0 NormalX=0 NormalY=0 NormalZ=1 AngleXU=0 Radius=3
  constraints (2):
    c: Coincident(g0,g-1)
    c: Diameter(g0) = 6
FEATURE [PartDesign::Pad] Pad061
  AllowMultiFace = false
  BaseFeature = -> Pocket022
  Direction = (1,1,1)
  Length = 70
  Length2 = 100
  Profile = -> Sketch092
  Type = 0
FEATURE [PartDesign::Body] Body051  label="M6x70_Furniture_Bolt"
  Group = -> [Sketch090,Pad060,Chamfer,Sketch091,Pocket022,Sketch092,Pad061]
  Origin = -> Origin068
  Placement = pos=(0,37,101) rot=(1,0,0;1.5708rad)
  Tip = -> Pad061
FEATURE [PartDesign::FeatureBase] Clone007
  BaseFeature = -> Body051
  Placement = pos=(0,37,101) rot=(1,0,0;1.5708rad)
FEATURE [PartDesign::Body] Body052  label="M6x70_Furniture_Bolt2"
  BaseFeature = -> Body051
  Group = -> [Clone007]
  Origin = -> Origin069
  Placement = pos=(0,0,0) rot=(0,0,1;3.14159rad)
  Tip = -> Clone007
FEATURE [Sketcher::SketchObject] Sketch093
  FullyConstrained = false
  MapMode = 5
  Placement = pos=(0,0,0) rot=(0.57735,0.57735,0.57735;2.0944rad)
  Support = -> [YZ_Plane070]
  sketch-geometry (17):
    g0: LineSegment StartX=16 StartY=28.5 StartZ=0 EndX=16 EndY=26 EndZ=0
    g1: LineSegment StartX=16 StartY=26 StartZ=0 EndX=-16 EndY=26 EndZ=0
    g2: LineSegment StartX=-16 StartY=26 StartZ=0 EndX=-16 EndY=28.5 EndZ=0
    g3: LineSegment StartX=-16 StartY=28.5 StartZ=0 EndX=-17.5 EndY=28.5 EndZ=0
    g4: LineSegment StartX=-17.5 StartY=28.5 StartZ=0 EndX=-17.5 EndY=30 EndZ=0
    g5: LineSegment StartX=-17.5 StartY=30 StartZ=0 EndX=-17.85 EndY=30 EndZ=0
    g6: LineSegment StartX=-19.85 StartY=32 StartZ=0 EndX=-19.85 EndY=35.5078 EndZ=0
    g7: LineSegment StartX=19.85 StartY=35.5078 StartZ=0 EndX=19.85 EndY=32 EndZ=0
    g8: LineSegment StartX=17.85 StartY=30 StartZ=0 EndX=17.5 EndY=30 EndZ=0
    g9: LineSegment StartX=17.5 StartY=30 StartZ=0 EndX=17.5 EndY=28.5 EndZ=0
    g10: LineSegment StartX=17.5 StartY=28.5 StartZ=0 EndX=16 EndY=28.5 EndZ=0
    g11: ArcOfCircle CenterX=5.199e-13 CenterY=-27.17 CenterZ=0 NormalX=0 NormalY=0 NormalZ=1 AngleXU=0 Radius=67.17 StartAngle=1.5708 EndAngle=1.84824
    g12: ArcOfCircle CenterX=5.199e-13 CenterY=-27.17 CenterZ=0 NormalX=0 NormalY=0 NormalZ=1 AngleXU=0 Radius=67.17 StartAngle=1.29335 EndAngle=1.5708
    g13: ArcOfCircle CenterX=-17.85 CenterY=32 CenterZ=0 NormalX=0 NormalY=0 NormalZ=1 AngleXU=0 Radius=2 StartAngle=3.14159 EndAngle=4.71239
    g14: ArcOfCircle CenterX=17.85 CenterY=32 CenterZ=0 NormalX=0 NormalY=0 NormalZ=1 AngleXU=0 Radius=2 StartAngle=4.71239 EndAngle=6.28319
    g15: ArcOfCircle CenterX=-17.85 CenterY=35.5078 CenterZ=0 NormalX=0 NormalY=0 NormalZ=1 AngleXU=0 Radius=2 StartAngle=1.84824 EndAngle=3.14159
    g16: ArcOfCircle CenterX=17.85 CenterY=35.5078 CenterZ=0 NormalX=0 NormalY=0 NormalZ=1 AngleXU=0 Radius=2 StartAngle=-9e-16 EndAngle=1.29335
  constraints (44):
    c: Coincident(g0,g1)
    c: Coincident(g1,g2)
    c: Coincident(g2,g3)
    c: Coincident(g3,g4)
    c: Coincident(g4,g5)
    c: Coincident(g8,g9)
    c: Coincident(g9,g10)
    c: Coincident(g10,g0)
    c: Vertical(g0)
    c: Vertical(g9)
    c: Vertical(g7)
    c: Horizontal(g8)
    c: Horizontal(g10)
    c: Horizontal(g1)
    c: Vertical(g2)
    c: Horizontal(g3)
    c: Horizontal(g5)
    c: Symmetric(g4,g8,g-2)
    c: DistanceX(g4,g8) = 35
    c: Equal(g3,g10)
    c: DistanceX(g10,g10) = 1.5
    c: DistanceY(g-1,g1) = 26
    c: DistanceY(g-1,g3) = 28.5
    c: DistanceY(g-1,g4) = 30
    c: Symmetric(g2,g0,g-2)
    c: Tangent(g11,g12) = -1.5708
    c: PointOnObject(g11,g-2)
    c: Coincident(g12,g11)
    c: DistanceY(g-1,g11) = 40
    c: Tangent(g5,g13) = 1.5708
    c: Tangent(g6,g13) = 1.5708
    c: Tangent(g7,g14) = 1.5708
    c: Tangent(g8,g14) = 1.5708
    c: Radius(g14) = 2
    c: DistanceX(g6,g7) = 39.7
    c: DistanceY(g11,g-1) = 27.17
    c: Tangent(g11,g15) = -1.5708
    c: Tangent(g6,g15) = 1.5708
    c: Tangent(g12,g16) = -1.5708
    c: Tangent(g7,g16) = 1.5708
    c: Symmetric(g6,g7,g-2)
    c: Equal(g16,g15)
    c: Radius(g16) = 2
    c: Symmetric(g6,g7,g-2)
FEATURE [PartDesign::Revolution] Revolution005
  AllowMultiFace = false
  Angle = 360
  Axis = (3e-16,1,-2e-16)
  Base = (0,0,0)
  Placement = pos=(0,0,0) rot=(0.57735,0.57735,0.57735;2.0944rad)
  Profile = -> Sketch093
  ReferenceAxis = -> Sketch093 [H_Axis]
FEATURE [PartDesign::Plane] DatumPlane001
  AttachmentOffset = pos=(0,0,7) rot=(0,0,1;0rad)
  Length = 95.8516
  MapMode = 4
  Placement = pos=(0,7,0) rot=(0.57735,0.57735,0.57735;4.18879rad)
  ResizeMode = 0
  Support = -> [Revolution005]
  Width = 95.8986
FEATURE [Sketcher::SketchObject] Sketch094
  FullyConstrained = false
  MapMode = 5
  Placement = pos=(0,7,0) rot=(0.57735,0.57735,0.57735;4.18879rad)
  Support = -> [DatumPlane001]
  sketch-geometry (26):
    g0: LineSegment StartX=7 StartY=-18.2003 StartZ=0 EndX=19.4726 EndY=1.0332 EndZ=0
    g1: LineSegment StartX=19.4726 StartY=1.0332 StartZ=0 EndX=5.03473 EndY=18.8388 EndZ=0
    g2: LineSegment StartX=5.03473 StartY=18.8388 StartZ=0 EndX=-16.361 EndY=10.6098 EndZ=0
    g3: LineSegment StartX=-16.361 StartY=10.6098 StartZ=0 EndX=-15.1464 EndY=-12.2816 EndZ=0
    g4: LineSegment StartX=-15.1464 StartY=-12.2816 StartZ=0 EndX=7 EndY=-18.2003 EndZ=0
    g5: Circle CenterX=0 CenterY=0 CenterZ=0 NormalX=0 NormalY=0 NormalZ=1 AngleXU=0 Radius=19.5
    g6: ArcOfCircle CenterX=0 CenterY=0 CenterZ=0 NormalX=0 NormalY=0 NormalZ=1 AngleXU=0 Radius=19.5 StartAngle=5.60186 EndAngle=6.33619
    g7: ArcOfCircle CenterX=0 CenterY=0 CenterZ=0 NormalX=0 NormalY=0 NormalZ=1 AngleXU=0 Radius=19.5 StartAngle=4.34522 EndAngle=5.07956
    g8: ArcOfCircle CenterX=0 CenterY=0 CenterZ=0 NormalX=0 NormalY=0 NormalZ=1 AngleXU=0 Radius=19.5 StartAngle=3.08858 EndAngle=3.82292
    g9: ArcOfCircle CenterX=0 CenterY=0 CenterZ=0 NormalX=0 NormalY=0 NormalZ=1 AngleXU=0 Radius=19.5 StartAngle=1.83195 EndAngle=2.56628
    g10: ArcOfCircle CenterX=0 CenterY=0 CenterZ=0 NormalX=0 NormalY=0 NormalZ=1 AngleXU=0 Radius=19.5 StartAngle=0.575309 EndAngle=1.30965
    g11: ArcOfCircle CenterX=17.7078 CenterY=24.3726 CenterZ=0 NormalX=0 NormalY=0 NormalZ=1 AngleXU=0 Radius=13.8285 StartAngle=3.00933 EndAngle=3.5533
    g12: ArcOfCircle CenterX=17.7078 CenterY=24.3726 CenterZ=0 NormalX=0 NormalY=0 NormalZ=1 AngleXU=0 Radius=13.8285 StartAngle=4.61484 EndAngle=5.15882
    g13: ArcOfCircle CenterX=0 CenterY=0 CenterZ=0 NormalX=0 NormalY=0 NormalZ=1 AngleXU=0 Radius=26.5 StartAngle=0.162637 EndAngle=0.465682
    g14: ArcOfCircle CenterX=0 CenterY=0 CenterZ=0 NormalX=0 NormalY=0 NormalZ=1 AngleXU=0 Radius=26.5 StartAngle=1.41927 EndAngle=1.72232
    g15: ArcOfCircle CenterX=-17.7078 CenterY=24.3726 CenterZ=0 NormalX=0 NormalY=0 NormalZ=1 AngleXU=0 Radius=13.8285 StartAngle=5.87148 EndAngle=6.41545
    g16: ArcOfCircle CenterX=-17.7078 CenterY=24.3726 CenterZ=0 NormalX=0 NormalY=0 NormalZ=1 AngleXU=0 Radius=13.8285 StartAngle=4.26596 EndAngle=4.80994
    g17: ArcOfCircle CenterX=-28.6518 CenterY=-9.30952 CenterZ=0 NormalX=0 NormalY=0 NormalZ=1 AngleXU=0 Radius=13.8285 StartAngle=0.844931 EndAngle=1.3889
    g18: ArcOfCircle CenterX=-28.6518 CenterY=-9.30952 CenterZ=0 NormalX=0 NormalY=0 NormalZ=1 AngleXU=0 Radius=13.8285 StartAngle=5.5226 EndAngle=6.06657
    g19: ArcOfCircle CenterX=3.8e-15 CenterY=-30.1262 CenterZ=0 NormalX=0 NormalY=0 NormalZ=1 AngleXU=0 Radius=13.8285 StartAngle=2.10157 EndAngle=2.64554
    g20: ArcOfCircle CenterX=3.8e-15 CenterY=-30.1262 CenterZ=0 NormalX=0 NormalY=0 NormalZ=1 AngleXU=0 Radius=13.8285 StartAngle=0.496052 EndAngle=1.04002
    g21: ArcOfCircle CenterX=28.6518 CenterY=-9.30952 CenterZ=0 NormalX=0 NormalY=0 NormalZ=1 AngleXU=0 Radius=13.8285 StartAngle=3.35821 EndAngle=3.90218
    g22: ArcOfCircle CenterX=28.6518 CenterY=-9.30952 CenterZ=0 NormalX=0 NormalY=0 NormalZ=1 AngleXU=0 Radius=13.8285 StartAngle=1.75269 EndAngle=2.29666
    g23: ArcOfCircle CenterX=0 CenterY=0 CenterZ=0 NormalX=0 NormalY=0 NormalZ=1 AngleXU=0 Radius=26.5 StartAngle=2.67591 EndAngle=2.97896
    g24: ArcOfCircle CenterX=0 CenterY=0 CenterZ=0 NormalX=0 NormalY=0 NormalZ=1 AngleXU=0 Radius=26.5 StartAngle=3.93255 EndAngle=4.23559
    g25: ArcOfCircle CenterX=0 CenterY=0 CenterZ=0 NormalX=0 NormalY=0 NormalZ=1 AngleXU=0 Radius=26.5 StartAngle=5.18918 EndAngle=5.49223
  constraints (74):
    c: Coincident(g0,g1)
    c: Coincident(g1,g2)
    c: Coincident(g2,g3)
    c: Coincident(g3,g4)
    c: Coincident(g4,g0)
    c: Equal(g0, g1-g4) x4
    c: PointOnObject(g0,g5)
    c: PointOnObject(g1,g5)
    c: PointOnObject(g2,g5)
    c: PointOnObject(g3,g5)
    c: PointOnObject(g4,g5)
    c: Coincident(g5,g-1)
    c: Coincident(g10,g6)
    c: Coincident(g10,g7)
    c: Coincident(g10,g8)
    c: Coincident(g10,g9)
    c: Coincident(g10,g-1)
    c: Coincident(g10,g1)
    c: Coincident(g6,g0)
    c: Coincident(g7,g0)
    c: Coincident(g8,g3)
    c: Coincident(g9,g2)
    c: Distance(g8,g8) = 14
    c: Distance(g9,g9) = 14
    c: Distance(g10,g10) = 14
    c: Distance(g6,g6) = 14
    c: Distance(g7,g7) = 14
    c: Diameter(g5) = 39
    c: DistanceX(g-2,g7) = -7
    c: Coincident(g11,g10)
    c: Coincident(g12,g10)
    c: Coincident(g12,g11)
    c: Coincident(g14,g13)
    c: Coincident(g14,g6)
    c: Coincident(g14,g11)
    c: Coincident(g13,g12)
    c: Equal(g14,g13)
    c: Diameter(g14) = 53
    c: Equal(g12,g11)
    c: Coincident(g15,g16)
    c: Coincident(g15,g14)
    c: Coincident(g15,g9)
    c: Coincident(g16,g9)
    c: Coincident(g17,g8)
    c: Coincident(g17,g18)
    c: Coincident(g18,g8)
    c: Equal(g18,g17)
    c: Equal(g17,g16)
    c: Equal(g16,g15)
    c: Equal(g15,g11)
    c: Coincident(g22,g21)
    c: Coincident(g20,g19)
    c: Coincident(g19,g7)
    c: Coincident(g20,g7)
    c: Coincident(g21,g6)
    c: Coincident(g22,g6)
    c: Coincident(g22,g13)
    c: Equal(g19,g20)
    c: Equal(g20,g21)
    c: Equal(g21,g22)
    c: Equal(g22,g12)
    c: Coincident(g25,g23)
    c: Coincident(g25,g24)
    c: Coincident(g25,g6)
    c: Coincident(g20,g25)
    c: Coincident(g21,g25)
    c: Coincident(g24,g19)
    c: Coincident(g24,g18)
    c: Coincident(g23,g17)
    c: Coincident(g23,g16)
    c: Equal(g23,g24)
    c: Equal(g24,g25)
    c: Equal(g25,g13)
    c: Distance(g16,g17) = 8
FEATURE [PartDesign::Pad] Pad062
  AllowMultiFace = false
  BaseFeature = -> Revolution005
  Direction = (1,1,1)
  Length = 2
  Length2 = 100
  Placement = pos=(0,0,0) rot=(0.57735,0.57735,0.57735;2.0944rad)
  Profile = -> Sketch094
  Type = 0
FEATURE [Sketcher::SketchObject] Sketch095
  FullyConstrained = false
  MapMode = 5
  Placement = pos=(0,7,0) rot=(0.57735,0.57735,-0.57735;2.0944rad)
  Support = -> [Pad062]
  sketch-geometry (1):
    g0: Circle CenterX=0 CenterY=0 CenterZ=0 NormalX=0 NormalY=0 NormalZ=1 AngleXU=0 Radius=8.5
  constraints (2):
    c: Coincident(g0,g-1)
    c: Diameter(g0) = 17
FEATURE [Sketcher::SketchObject] Sketch097
  FullyConstrained = false
  MapMode = 5
  Placement = pos=(0,0,0) rot=(0.57735,0.57735,0.57735;2.0944rad)
  Support = -> [YZ_Plane070]
  sketch-geometry (9):
    g0: LineSegment StartX=9 StartY=-2 StartZ=0 EndX=9 EndY=-19.5 EndZ=0
    g1: LineSegment StartX=9 StartY=-19.5 StartZ=0 EndX=9.5 EndY=-19.5 EndZ=0
    g2: LineSegment StartX=9.5 StartY=-19.5 StartZ=0 EndX=12 EndY=-12.5 EndZ=0
    g3: LineSegment StartX=12 StartY=-12.5 StartZ=0 EndX=11 EndY=-7 EndZ=0
    g4: LineSegment StartX=11 StartY=-7 StartZ=0 EndX=14 EndY=-7 EndZ=0
    g5: LineSegment StartX=14 StartY=-7 StartZ=0 EndX=14 EndY=-5 EndZ=0
    g6: LineSegment StartX=14 StartY=-5 StartZ=0 EndX=12 EndY=-5 EndZ=0
    g7: LineSegment StartX=12 StartY=-5 StartZ=0 EndX=12 EndY=-2 EndZ=0
    g8: LineSegment StartX=12 StartY=-2 StartZ=0 EndX=9 EndY=-2 EndZ=0
  constraints (27):
    c: Coincident(g0,g1)
    c: Coincident(g1,g2)
    c: Coincident(g2,g3)
    c: Coincident(g3,g4)
    c: Coincident(g4,g5)
    c: Coincident(g5,g6)
    c: Coincident(g6,g7)
    c: Coincident(g7,g8)
    c: Coincident(g0,g8)
    c: Vertical(g0)
    c: DistanceX(g-1,g0) = 9
    c: DistanceY(g0,g-1) = 19.5
    c: Horizontal(g1)
    c: DistanceY(g0,g-1) = 2
    c: Horizontal(g8)
    c: Vertical(g7)
    c: DistanceX(g8,g8) = 3
    c: Horizontal(g6)
    c: DistanceX(g6,g6) = 2
    c: DistanceY(g5,g-1) = 5
    c: DistanceY(g4,g-1) = 7
    c: Vertical(g5)
    c: DistanceX(g0,g2) = 3
    c: DistanceX(g1,g1) = 0.5
    c: Horizontal(g4)
    c: DistanceX(g4,g4) = 3
    c: DistanceY(g2,g-1) = 12.5
FEATURE [PartDesign::Revolution] Revolution006
  AllowMultiFace = false
  Angle = 360
  Axis = (3e-16,1,-2e-16)
  Base = (0,0,0)
  BaseFeature = -> Pad062
  Placement = pos=(0,0,0) rot=(0.57735,0.57735,0.57735;2.0944rad)
  Profile = -> Sketch097
  ReferenceAxis = -> Sketch097 [H_Axis]
  Reversed = true
FEATURE [Sketcher::SketchObject] Sketch098
  FullyConstrained = false
  MapMode = 5
  Support = -> [XY_Plane070]
  sketch-geometry (3):
    g0: LineSegment StartX=7.5 StartY=7 StartZ=0 EndX=17.5 EndY=7 EndZ=0
    g1: LineSegment StartX=17.5 StartY=7 StartZ=0 EndX=12.5 EndY=10 EndZ=0
    g2: LineSegment StartX=12.5 StartY=10 StartZ=0 EndX=7.5 EndY=7 EndZ=0
  constraints (9):
    c: Coincident(g0,g1)
    c: Coincident(g1,g2)
    c: Coincident(g0,g2)
    c: DistanceY(g-1,g0) = 7
    c: Horizontal(g0)
    c: DistanceY(g0,g1) = 3
    c: DistanceX(g-1,g0) = 17.5
    c: DistanceX(g-1,g1) = 12.5
    c: DistanceX(g-1,g0) = 7.5
FEATURE [PartDesign::Groove] Groove001
  AllowMultiFace = false
  Angle = 360
  Axis = (0,1,0)
  Base = (0,0,0)
  BaseFeature = -> Revolution006
  Placement = pos=(0,0,0) rot=(0.57735,0.57735,0.57735;2.0944rad)
  Profile = -> Sketch098
  ReferenceAxis = -> Sketch098 [V_Axis]
FEATURE [PartDesign::Pad] Pad063
  AllowMultiFace = false
  BaseFeature = -> Groove001
  Direction = (1,1,1)
  Length = 1.5
  Length2 = 100
  Placement = pos=(0,0,0) rot=(0.57735,0.57735,0.57735;2.0944rad)
  Profile = -> Sketch095
  Type = 0
FEATURE [Sketcher::SketchObject] Sketch096
  FullyConstrained = false
  MapMode = 5
  Placement = pos=(0,5.5,0) rot=(0.57735,0.57735,-0.57735;2.0944rad)
  Support = -> [Pad063]
  sketch-geometry (7):
    g0: LineSegment StartX=6 StartY=-3.4641 StartZ=0 EndX=6 EndY=3.4641 EndZ=0
    g1: LineSegment StartX=6 StartY=3.4641 StartZ=0 EndX=9e-16 EndY=6.9282 EndZ=0
    g2: LineSegment StartX=9e-16 StartY=6.9282 StartZ=0 EndX=-6 EndY=3.4641 EndZ=0
    g3: LineSegment StartX=-6 StartY=3.4641 StartZ=0 EndX=-6 EndY=-3.4641 EndZ=0
    g4: LineSegment StartX=-6 StartY=-3.4641 StartZ=0 EndX=0 EndY=-6.9282 EndZ=0
    g5: LineSegment StartX=0 StartY=-6.9282 StartZ=0 EndX=6 EndY=-3.4641 EndZ=0
    g6: Circle CenterX=0 CenterY=0 CenterZ=0 NormalX=0 NormalY=0 NormalZ=1 AngleXU=0 Radius=6.9282
  constraints (16):
    c: Coincident(g0,g1)
    c: Coincident(g1,g2)
    c: Coincident(g2,g3)
    c: Coincident(g3,g4)
    c: Coincident(g4,g5)
    c: Coincident(g5,g0)
    c: Equal(g0, g1-g5) x5
    c: PointOnObject(g0,g6)
    c: PointOnObject(g1,g6)
    c: PointOnObject(g2,g6)
    c: PointOnObject(g3,g6)
    c: PointOnObject(g4,g6)
    c: PointOnObject(g5,g6)
    c: Coincident(g6,g-1)
    c: Vertical(g3)
    c: DistanceX(g2,g0) = 12
FEATURE [Sketcher::SketchObject] Sketch099
  FullyConstrained = false
  MapMode = 5
  Support = -> [XY_Plane070]
  sketch-geometry (6):
    g0: LineSegment StartX=26.5 StartY=-6 StartZ=0 EndX=26.5 EndY=8 EndZ=0
    g1: LineSegment StartX=26.5 StartY=8 StartZ=0 EndX=17.5 EndY=8 EndZ=0
    g2: LineSegment StartX=17.5 StartY=8 StartZ=0 EndX=12.5 EndY=12 EndZ=0
    g3: LineSegment StartX=12.5 StartY=12 StartZ=0 EndX=6.25 EndY=14 EndZ=0
    g4: LineSegment StartX=6.25 StartY=14 StartZ=0 EndX=6.25 EndY=6 EndZ=0
    g5: ArcOfCircle CenterX=7.23279 CenterY=-15.4275 CenterZ=0 NormalX=0 NormalY=0 NormalZ=1 AngleXU=0 Radius=21.45 StartAngle=0.455052 EndAngle=1.61663
  constraints (19):
    c: Coincident(g0,g1)
    c: Coincident(g1,g2)
    c: Coincident(g2,g3)
    c: Coincident(g3,g4)
    c: Horizontal(g1)
    c: Vertical(g0)
    c: Vertical(g4)
    c: Coincident(g5,g0)
    c: Coincident(g5,g4)
    c: Diameter(g5) = 42.9
    c: DistanceY(g0,g0) = 14
    c: DistanceY(g4,g4) = 8
    c: DistanceY(g0,g-1) = 6
    c: DistanceX(g-1,g2) = 12.5
    c: DistanceX(g-1,g3) = 6.25
    c: DistanceX(g-1,g1) = 17.5
    c: DistanceX(g-1,g0) = 26.5
    c: DistanceY(g-1,g4) = 6
    c: DistanceY(g2,g3) = 2
FEATURE [PartDesign::Pad] Pad064
  AllowMultiFace = false
  BaseFeature = -> Pad063
  Direction = (1,1,1)
  Length = 1.5
  Length2 = 100
  Midplane = true
  Placement = pos=(0,0,0) rot=(0.57735,0.57735,0.57735;2.0944rad)
  Profile = -> Sketch099
  Type = 0
FEATURE [PartDesign::PolarPattern] PolarPattern001
  Angle = 360
  Axis = -> Y_Axis070
  BaseFeature = -> Pad064
  Occurrences = 5
  Originals = -> [Pad064]
  Placement = pos=(0,0,0) rot=(0.57735,0.57735,0.57735;2.0944rad)
FEATURE [PartDesign::Pocket] Pocket023
  AllowMultiFace = false
  BaseFeature = -> PolarPattern001
  Length = 4.8
  Length2 = 100
  Placement = pos=(0,0,0) rot=(0.57735,0.57735,0.57735;2.0944rad)
  Profile = -> Sketch096
  Type = 0
FEATURE [PartDesign::Body] Body056  label="Wheel001"
  Group = -> [Sketch093,Revolution005,DatumPlane001,Sketch094,Pad062,Sketch095,Sketch096,Sketch097,Sketch098,Revolution006,Groove001,Pad063,Pad064,PolarPattern001,Pocket023,Sketch099]
  Origin = -> Origin071
  Tip = -> Pad062
FEATURE [Sketcher::SketchObject] Sketch100
  FullyConstrained = false
  MapMode = 5
  Support = -> [XY_Plane071]
  sketch-geometry (7):
    g0: LineSegment StartX=6 StartY=3.4641 StartZ=0 EndX=3.87264e-11 EndY=6.9282 EndZ=0
    g1: LineSegment StartX=3.8726e-11 StartY=6.9282 StartZ=0 EndX=-6 EndY=3.4641 EndZ=0
    g2: LineSegment StartX=-6 StartY=3.4641 StartZ=0 EndX=-6 EndY=-3.4641 EndZ=0
    g3: LineSegment StartX=-6 StartY=-3.4641 StartZ=0 EndX=1.74527e-11 EndY=-6.9282 EndZ=0
    g4: LineSegment StartX=1.74523e-11 StartY=-6.9282 StartZ=0 EndX=6 EndY=-3.4641 EndZ=0
    g5: LineSegment StartX=6 StartY=-3.4641 StartZ=0 EndX=6 EndY=3.4641 EndZ=0
    g6: Circle CenterX=0 CenterY=0 CenterZ=0 NormalX=0 NormalY=0 NormalZ=1 AngleXU=0 Radius=6.9282
  constraints (16):
    c: Coincident(g0,g1)
    c: Coincident(g1,g2)
    c: Coincident(g2,g3)
    c: Coincident(g3,g4)
    c: Coincident(g4,g5)
    c: Coincident(g5,g0)
    c: Equal(g0, g1-g5) x5
    c: PointOnObject(g0,g6)
    c: PointOnObject(g1,g6)
    c: PointOnObject(g2,g6)
    c: PointOnObject(g3,g6)
    c: PointOnObject(g4,g6)
    c: PointOnObject(g5,g6)
    c: Coincident(g6,g-1)
    c: Vertical(g5)
    c: DistanceX(g1,g0) = 12
FEATURE [PartDesign::Pad] Pad065
  AllowMultiFace = false
  Direction = (1,1,1)
  Length = 6
  Length2 = 100
  Profile = -> Sketch100
  Type = 0
FEATURE [Sketcher::SketchObject] Sketch101
  FullyConstrained = false
  MapMode = 5
  Placement = pos=(0,0,6) rot=(0,0,1;0rad)
  Support = -> [Pad065]
  sketch-geometry (1):
    g0: Circle CenterX=0 CenterY=0 CenterZ=0 NormalX=0 NormalY=0 NormalZ=1 AngleXU=0 Radius=6
  constraints (2):
    c: Coincident(g0,g-1)
    c: Diameter(g0) = 12
FEATURE [PartDesign::Pad] Pad066
  AllowMultiFace = false
  BaseFeature = -> Pad065
  Direction = (1,1,1)
  Length = 24
  Length2 = 100
  Profile = -> Sketch101
  Type = 0
FEATURE [Sketcher::SketchObject] Sketch102
  FullyConstrained = false
  MapMode = 5
  Placement = pos=(0,0,30) rot=(0,0,1;0rad)
  Support = -> [Pad066]
  sketch-geometry (1):
    g0: Circle CenterX=0 CenterY=0 CenterZ=0 NormalX=0 NormalY=0 NormalZ=1 AngleXU=0 Radius=3
  constraints (2):
    c: Coincident(g0,g-1)
    c: Diameter(g0) = 6
FEATURE [PartDesign::Pocket] Pocket024
  AllowMultiFace = false
  BaseFeature = -> Pad066
  Length = 24.5
  Length2 = 100
  Profile = -> Sketch102
  Type = 0
FEATURE [Sketcher::SketchObject] Sketch103
  FullyConstrained = false
  MapMode = 5
  Placement = pos=(0,0,0) rot=(1,0,0;3.14159rad)
  Support = -> [Pocket024]
  sketch-geometry (1):
    g0: Circle CenterX=0 CenterY=0 CenterZ=0 NormalX=0 NormalY=0 NormalZ=1 AngleXU=0 Radius=1.75
  constraints (2):
    c: Coincident(g0,g-1)
    c: Diameter(g0) = 3.5
FEATURE [PartDesign::Pocket] Pocket025
  AllowMultiFace = false
  BaseFeature = -> Pocket024
  Length = 6
  Length2 = 100
  Profile = -> Sketch103
  Type = 0
FEATURE [Sketcher::SketchObject] Sketch104
  FullyConstrained = false
  MapMode = 5
  Placement = pos=(0,0,0) rot=(1,0,0;1.5708rad)
  Support = -> [XZ_Plane071]
  sketch-geometry (1):
    g0: Circle CenterX=0 CenterY=24.5 CenterZ=0 NormalX=0 NormalY=0 NormalZ=1 AngleXU=0 Radius=1.75
  constraints (3):
    c: PointOnObject(g0,g-2)
    c: DistanceY(g-1,g0) = 24.5
    c: Diameter(g0) = 3.5
FEATURE [PartDesign::Pocket] Pocket026
  AllowMultiFace = false
  BaseFeature = -> Pocket025
  Length = 14
  Length2 = 100
  Midplane = true
  Profile = -> Sketch104
  Type = 0
FEATURE [PartDesign::Body] Body057  label="Axel001"
  Group = -> [Sketch100,Pad065,Sketch101,Pad066,Sketch102,Pocket024,Sketch103,Pocket025,Sketch104,Pocket026]
  Origin = -> Origin070
  Placement = pos=(0,10.3,0) rot=(0.935113,-0.250563,0.250563;1.63783rad)
  Tip = -> Pocket026
FEATURE [Sketcher::SketchObject] Sketch105
  FullyConstrained = false
  MapMode = 5
  Support = -> [XY_Plane072]
  sketch-geometry (4):
    g0: LineSegment StartX=-16 StartY=16 StartZ=0 EndX=30 EndY=16 EndZ=0
    g1: LineSegment StartX=30 StartY=16 StartZ=0 EndX=30 EndY=-16 EndZ=0
    g2: LineSegment StartX=30 StartY=-16 StartZ=0 EndX=-16 EndY=-16 EndZ=0
    g3: LineSegment StartX=-16 StartY=-16 StartZ=0 EndX=-16 EndY=16 EndZ=0
  constraints (11):
    c: Coincident(g0,g1)
    c: Coincident(g1,g2)
    c: Coincident(g2,g3)
    c: Coincident(g3,g0)
    c: Horizontal(g0)
    c: Horizontal(g2)
    c: Vertical(g1)
    c: DistanceX(g0,g0) = 46
    c: DistanceY(g3,g3) = 32
    c: Symmetric(g0,g2,g-1)
    c: DistanceX(g2,g-1) = 16
FEATURE [PartDesign::Pad] Pad067
  AllowMultiFace = false
  Direction = (1,1,1)
  Length = 21
  Length2 = 100
  Profile = -> Sketch105
  Type = 0
FEATURE [Sketcher::SketchObject] Sketch106
  FullyConstrained = false
  MapMode = 5
  Placement = pos=(30,0,0) rot=(0.57735,0.57735,0.57735;2.0944rad)
  Support = -> [Pad067]
  sketch-geometry (1):
    g0: Circle CenterX=0 CenterY=12.5 CenterZ=0 NormalX=0 NormalY=0 NormalZ=1 AngleXU=0 Radius=12.5
  constraints (3):
    c: Diameter(g0) = 25
    c: PointOnObject(g0,g-2)
    c: DistanceY(g-1,g0) = 12.5
FEATURE [PartDesign::Pad] Pad068
  AllowMultiFace = false
  BaseFeature = -> Pad067
  Direction = (1,1,1)
  Length = 32
  Length2 = 100
  Profile = -> Sketch106
  Type = 0
FEATURE [Sketcher::SketchObject] Sketch107
  FullyConstrained = false
  MapMode = 5
  Placement = pos=(0,0,0) rot=(1,0,0;3.14159rad)
  Support = -> [Pad068]
  sketch-geometry (2):
    g0: ArcOfCircle CenterX=0 CenterY=0 CenterZ=0 NormalX=0 NormalY=0 NormalZ=1 AngleXU=0 Radius=3 StartAngle=0.585686 EndAngle=5.6975
    g1: LineSegment StartX=2.5 StartY=1.65831 StartZ=0 EndX=2.5 EndY=-1.65831 EndZ=0
  constraints (6):
    c: Coincident(g0,g-1)
    c: Diameter(g0) = 6
    c: Coincident(g1,g0)
    c: Coincident(g1,g0)
    c: Vertical(g1)
    c: DistanceX(g0,g0) = 2.5
FEATURE [PartDesign::Pad] Pad069
  AllowMultiFace = false
  BaseFeature = -> Pad068
  Direction = (1,1,1)
  Length = 15
  Length2 = 100
  Profile = -> Sketch107
  Type = 0
FEATURE [Sketcher::SketchObject] Sketch108
  FullyConstrained = false
  MapMode = 5
  Placement = pos=(0,0,21) rot=(0,0,1;0rad)
  Support = -> [Pad069]
  sketch-geometry (2):
    g0: ArcOfCircle CenterX=0 CenterY=0 CenterZ=0 NormalX=0 NormalY=0 NormalZ=1 AngleXU=0 Radius=3 StartAngle=0.585686 EndAngle=5.6975
    g1: LineSegment StartX=2.5 StartY=1.65831 StartZ=0 EndX=2.5 EndY=-1.65831 EndZ=0
  constraints (6):
    c: Coincident(g0,g-1)
    c: Coincident(g1,g0)
    c: Coincident(g1,g0)
    c: Vertical(g1)
    c: DistanceX(g0,g0) = 2.5
    c: Diameter(g0) = 6
FEATURE [PartDesign::Pad] Pad070
  AllowMultiFace = false
  BaseFeature = -> Pad069
  Direction = (1,1,1)
  Length = 15
  Length2 = 100
  Profile = -> Sketch108
  Type = 0
FEATURE [PartDesign::Body] Body054  label="Motor001"
  Group = -> [Sketch105,Pad067,Sketch106,Pad068,Sketch107,Pad069,Sketch108,Pad070]
  Origin = -> Origin073
  Placement = pos=(-1.1e-14,-24,0) rot=(0.57735,-0.57735,0.57735;2.0944rad)
  Tip = -> Pad070
FEATURE [Sketcher::SketchObject] Sketch109
  FullyConstrained = false
  MapMode = 5
  Placement = pos=(0,0,0) rot=(0.57735,0.57735,0.57735;2.0944rad)
  Support = -> [YZ_Plane073]
  sketch-geometry (8):
    g0: LineSegment StartX=-24 StartY=64 StartZ=0 EndX=-24 EndY=-12 EndZ=0
    g1: LineSegment StartX=-24 StartY=-12 StartZ=0 EndX=-21 EndY=-12 EndZ=0
    g2: LineSegment StartX=-21 StartY=-12 StartZ=0 EndX=-21 EndY=64 EndZ=0
    g3: LineSegment StartX=-20 StartY=65 StartZ=0 EndX=16 EndY=65 EndZ=0
    g4: LineSegment StartX=16 StartY=65 StartZ=0 EndX=16 EndY=68 EndZ=0
    g5: LineSegment StartX=16 StartY=68 StartZ=0 EndX=-20 EndY=68 EndZ=0
    g6: ArcOfCircle CenterX=-20 CenterY=64 CenterZ=0 NormalX=0 NormalY=0 NormalZ=1 AngleXU=0 Radius=4 StartAngle=1.5708 EndAngle=3.14159
    g7: ArcOfCircle CenterX=-20 CenterY=64 CenterZ=0 NormalX=0 NormalY=0 NormalZ=1 AngleXU=0 Radius=1 StartAngle=1.5708 EndAngle=3.14159
  constraints (21):
    c: Coincident(g0,g1)
    c: Coincident(g1,g2)
    c: Coincident(g3,g4)
    c: Coincident(g4,g5)
    c: Vertical(g0)
    c: Horizontal(g1)
    c: Tangent(g7,g2) = 1.5708
    c: Tangent(g7,g3) = 1.5708
    c: Tangent(g6,g0) = -1.5708
    c: Tangent(g6,g5) = -1.5708
    c: Horizontal(g5)
    c: Vertical(g4)
    c: Equal(g1,g4)
    c: DistanceY(g4,g4) = 3
    c: Diameter(g7) = 2
    c: Horizontal(g3)
    c: DistanceY(g1,g-1) = 12
    c: DistanceY(g-1,g3) = 65
    c: Coincident(g6,g7)
    c: DistanceX(g0,g-1) = 24
    c: DistanceX(g0,g4) = 40
FEATURE [PartDesign::Pad] Pad071
  AllowMultiFace = false
  Direction = (1,1,1)
  Length = 30
  Length2 = 100
  Midplane = true
  Placement = pos=(0,0,0) rot=(0.57735,0.57735,0.57735;2.0944rad)
  Profile = -> Sketch109
  Type = 0
FEATURE [Sketcher::SketchObject] Sketch110
  FullyConstrained = false
  MapMode = 5
  Placement = pos=(-1.9e-14,2.99e-14,68) rot=(0,0,-1;1.5708rad)
  Support = -> [Pad071]
  sketch-geometry (9):
    g0: Circle CenterX=0 CenterY=0 CenterZ=0 NormalX=0 NormalY=0 NormalZ=1 AngleXU=0 Radius=3.25
    g1: LineSegment StartX=-10 StartY=10 StartZ=0 EndX=10 EndY=10 EndZ=0
    g2: LineSegment StartX=10 StartY=10 StartZ=0 EndX=10 EndY=-10 EndZ=0
    g3: LineSegment StartX=10 StartY=-10 StartZ=0 EndX=-10 EndY=-10 EndZ=0
    g4: LineSegment StartX=-10 StartY=-10 StartZ=0 EndX=-10 EndY=10 EndZ=0
    g5: Circle CenterX=10 CenterY=10 CenterZ=0 NormalX=0 NormalY=0 NormalZ=1 AngleXU=0 Radius=1.75
    g6: Circle CenterX=10 CenterY=-10 CenterZ=0 NormalX=0 NormalY=0 NormalZ=1 AngleXU=0 Radius=1.75
    g7: Circle CenterX=-10 CenterY=-10 CenterZ=0 NormalX=0 NormalY=0 NormalZ=1 AngleXU=0 Radius=1.75
    g8: Circle CenterX=-10 CenterY=10 CenterZ=0 NormalX=0 NormalY=0 NormalZ=1 AngleXU=0 Radius=1.75
  constraints (21):
    c: Coincident(g0,g-1)
    c: Diameter(g0) = 6.5
    c: Coincident(g1,g2)
    c: Coincident(g2,g3)
    c: Coincident(g3,g4)
    c: Coincident(g4,g1)
    c: Horizontal(g1)
    c: Horizontal(g3)
    c: Vertical(g2)
    c: Vertical(g4)
    c: DistanceX(g1,g1) = 20
    c: DistanceY(g4,g4) = 20
    c: Symmetric(g1,g2,g0)
    c: Coincident(g8,g1)
    c: Coincident(g5,g1)
    c: Coincident(g6,g2)
    c: Coincident(g7,g3)
    c: Diameter(g7) = 3.5
    c: Equal(g7,g6)
    c: Equal(g7,g5)
    c: Equal(g7,g8)
FEATURE [PartDesign::Pocket] Pocket027
  AllowMultiFace = false
  BaseFeature = -> Pad071
  Length = 5
  Length2 = 100
  Placement = pos=(0,0,0) rot=(0.57735,0.57735,0.57735;2.0944rad)
  Profile = -> Sketch110
  Type = 0
FEATURE [PartDesign::Body] Body055  label="Wheel Bracket001"
  Group = -> [Sketch109,Pad071,Sketch110,Pocket027]
  Origin = -> Origin072
  Tip = -> Pocket027
FEATURE [Part::Part2DObjectPython] InvoluteGear002  # Draft 2D object (typed FeaturePython)
  ExternalGear = true
  HighPrecision = true
  Modules = 2
  NumberOfTeeth = 26
  PressureAngle = 20
FEATURE [PartDesign::Pad] Pad072
  AllowMultiFace = false
  Direction = (1,1,1)
  Length = 5
  Length2 = 100
  Profile = -> InvoluteGear002
  Type = 0
FEATURE [Sketcher::SketchObject] Sketch111
  FullyConstrained = false
  MapMode = 5
  Placement = pos=(0,0,5) rot=(0,0,1;0rad)
  Support = -> [Pad072]
  sketch-geometry (9):
    g0: Circle CenterX=0 CenterY=0 CenterZ=0 NormalX=0 NormalY=0 NormalZ=1 AngleXU=0 Radius=3.25
    g1: LineSegment StartX=-10 StartY=10 StartZ=0 EndX=10 EndY=10 EndZ=0
    g2: LineSegment StartX=10 StartY=10 StartZ=0 EndX=10 EndY=-10 EndZ=0
    g3: LineSegment StartX=10 StartY=-10 StartZ=0 EndX=-10 EndY=-10 EndZ=0
    g4: LineSegment StartX=-10 StartY=-10 StartZ=0 EndX=-10 EndY=10 EndZ=0
    g5: Circle CenterX=-10 CenterY=10 CenterZ=0 NormalX=0 NormalY=0 NormalZ=1 AngleXU=0 Radius=1.75
    g6: Circle CenterX=10 CenterY=10 CenterZ=0 NormalX=0 NormalY=0 NormalZ=1 AngleXU=0 Radius=1.75
    g7: Circle CenterX=10 CenterY=-10 CenterZ=0 NormalX=0 NormalY=0 NormalZ=1 AngleXU=0 Radius=1.75
    g8: Circle CenterX=-10 CenterY=-10 CenterZ=0 NormalX=0 NormalY=0 NormalZ=1 AngleXU=0 Radius=1.75
  constraints (21):
    c: Coincident(g0,g-1)
    c: Diameter(g0) = 6.5
    c: Coincident(g1,g2)
    c: Coincident(g2,g3)
    c: Coincident(g3,g4)
    c: Coincident(g4,g1)
    c: Horizontal(g1)
    c: Horizontal(g3)
    c: Vertical(g2)
    c: Vertical(g4)
    c: DistanceX(g3,g3) = 20
    c: DistanceY(g4,g4) = 20
    c: Symmetric(g2,g1,g0)
    c: Coincident(g8,g3)
    c: Coincident(g7,g2)
    c: Coincident(g6,g1)
    c: Coincident(g5,g1)
    c: Diameter(g5) = 3.5
    c: Equal(g5,g8)
    c: Equal(g5,g6)
    c: Equal(g5,g7)
FEATURE [PartDesign::Pocket] Pocket028
  AllowMultiFace = false
  BaseFeature = -> Pad072
  Length = 5
  Length2 = 100
  Profile = -> Sketch111
  Type = 0
FEATURE [PartDesign::Body] Body053  label="Wheel Gear001"
  Group = -> [InvoluteGear002,Pad072,Sketch111,Pocket028]
  Origin = -> Origin074
  Placement = pos=(0,0,68) rot=(0,0,1;0rad)
  Tip = -> Pocket028
FEATURE [Sketcher::SketchObject] Sketch112
  FullyConstrained = false
  MapMode = 5
  Support = -> [XY_Plane075]
  sketch-geometry (1):
    g0: Circle CenterX=0 CenterY=0 CenterZ=0 NormalX=0 NormalY=0 NormalZ=1 AngleXU=0 Radius=2.95
  constraints (2):
    c: Coincident(g0,g-1)
    c: Diameter(g0) = 5.9
FEATURE [PartDesign::Pad] Pad073
  AllowMultiFace = false
  Direction = (1,1,1)
  Length = 70
  Length2 = 100
  Profile = -> Sketch112
  Type = 0
FEATURE [Sketcher::SketchObject] Sketch113
  FullyConstrained = false
  MapMode = 5
  Placement = pos=(0,0,0) rot=(1,0,0;3.14159rad)
  Support = -> [Pad073]
  sketch-geometry (7):
    g0: LineSegment StartX=-3.917e-13 StartY=5.7735 StartZ=0 EndX=-5 EndY=2.88675 EndZ=0
    g1: LineSegment StartX=-5 StartY=2.88675 StartZ=0 EndX=-5 EndY=-2.88675 EndZ=0
    g2: LineSegment StartX=-5 StartY=-2.88675 StartZ=0 EndX=0 EndY=-5.7735 EndZ=0
    g3: LineSegment StartX=0 StartY=-5.7735 StartZ=0 EndX=5 EndY=-2.88675 EndZ=0
    g4: LineSegment StartX=5 StartY=-2.88675 StartZ=0 EndX=5 EndY=2.88675 EndZ=0
    g5: LineSegment StartX=5 StartY=2.88675 StartZ=0 EndX=-3.917e-13 EndY=5.7735 EndZ=0
    g6: Circle CenterX=0 CenterY=0 CenterZ=0 NormalX=0 NormalY=0 NormalZ=1 AngleXU=0 Radius=5.7735
  constraints (16):
    c: Coincident(g0,g1)
    c: Coincident(g1,g2)
    c: Coincident(g2,g3)
    c: Coincident(g3,g4)
    c: Coincident(g4,g5)
    c: Coincident(g5,g0)
    c: Equal(g0, g1-g5) x5
    c: PointOnObject(g0,g6)
    c: PointOnObject(g1,g6)
    c: PointOnObject(g2,g6)
    c: PointOnObject(g3,g6)
    c: PointOnObject(g4,g6)
    c: PointOnObject(g5,g6)
    c: Coincident(g6,g-1)
    c: Distance(g0,g4) = 10
    c: PointOnObject(g2,g-2)
FEATURE [PartDesign::Pad] Pad074
  AllowMultiFace = false
  BaseFeature = -> Pad073
  Direction = (1,1,1)
  Length = 4
  Length2 = 100
  Profile = -> Sketch113
  Type = 0
FEATURE [PartDesign::Body] Body058  label="M6x70_Hex_Head001"
  Group = -> [Sketch112,Pad073,Sketch113,Pad074]
  Origin = -> Origin075
  Placement = pos=(0,0,65) rot=(0,0,1;0rad)
  Tip = -> Pad074
FEATURE [Sketcher::SketchObject] Sketch114
  FullyConstrained = false
  MapMode = 5
  Support = -> [XY_Plane076]
  sketch-geometry (2):
    g0: Circle CenterX=0 CenterY=0 CenterZ=0 NormalX=0 NormalY=0 NormalZ=1 AngleXU=0 Radius=5.85
    g1: Circle CenterX=0 CenterY=0 CenterZ=0 NormalX=0 NormalY=0 NormalZ=1 AngleXU=0 Radius=3
  constraints (4):
    c: Coincident(g1,g0)
    c: Coincident(g1,g-1)
    c: Diameter(g1) = 6
    c: Diameter(g0) = 11.7
FEATURE [PartDesign::Pad] Pad075
  AllowMultiFace = false
  Direction = (1,1,1)
  Length = 1.5
  Length2 = 100
  Profile = -> Sketch114
  Type = 0
FEATURE [PartDesign::Body] Body059  label="M6_Washer004"
  Group = -> [Sketch114,Pad075]
  Origin = -> Origin076
  Placement = pos=(0,0,73) rot=(0,0,1;0rad)
  Tip = -> Pad075
FEATURE [Sketcher::SketchObject] Sketch115
  FullyConstrained = false
  MapMode = 5
  Support = -> [XY_Plane077]
  sketch-geometry (8):
    g0: LineSegment StartX=0 StartY=5.7735 StartZ=0 EndX=-5 EndY=2.88675 EndZ=0
    g1: LineSegment StartX=-5 StartY=2.88675 StartZ=0 EndX=-5 EndY=-2.88675 EndZ=0
    g2: LineSegment StartX=-5 StartY=-2.88675 StartZ=0 EndX=-1.501e-13 EndY=-5.7735 EndZ=0
    g3: LineSegment StartX=-1.501e-13 StartY=-5.7735 StartZ=0 EndX=5 EndY=-2.88675 EndZ=0
    g4: LineSegment StartX=5 StartY=-2.88675 StartZ=0 EndX=5 EndY=2.88675 EndZ=0
    g5: LineSegment StartX=5 StartY=2.88675 StartZ=0 EndX=0 EndY=5.7735 EndZ=0
    g6: Circle CenterX=0 CenterY=0 CenterZ=0 NormalX=0 NormalY=0 NormalZ=1 AngleXU=0 Radius=5.7735
    g7: Circle CenterX=0 CenterY=0 CenterZ=0 NormalX=0 NormalY=0 NormalZ=1 AngleXU=0 Radius=3
  constraints (18):
    c: Coincident(g0,g1)
    c: Coincident(g1,g2)
    c: Coincident(g2,g3)
    c: Coincident(g3,g4)
    c: Coincident(g4,g5)
    c: Coincident(g5,g0)
    c: Equal(g0, g1-g5) x5
    c: PointOnObject(g0,g6)
    c: PointOnObject(g1,g6)
    c: PointOnObject(g2,g6)
    c: PointOnObject(g3,g6)
    c: PointOnObject(g4,g6)
    c: PointOnObject(g5,g6)
    c: Coincident(g6,g-1)
    c: PointOnObject(g0,g-2)
    c: Distance(g0,g4) = 10
    c: Coincident(g7,g-1)
    c: Diameter(g7) = 6
FEATURE [PartDesign::Pad] Pad076
  AllowMultiFace = false
  Direction = (1,1,1)
  Length = 5
  Length2 = 100
  Profile = -> Sketch115
  Type = 0
FEATURE [PartDesign::Body] Body060  label="M6_Full_Nut005"
  Group = -> [Sketch115,Pad076]
  Origin = -> Origin077
  Placement = pos=(0,0,74.5) rot=(0,0,1;0rad)
  Tip = -> Pad076
FEATURE [Sketcher::SketchObject] Sketch116
  FullyConstrained = false
  MapMode = 5
  Support = -> [XY_Plane078]
  sketch-geometry (2):
    g0: Circle CenterX=0 CenterY=0 CenterZ=0 NormalX=0 NormalY=0 NormalZ=1 AngleXU=0 Radius=9.5
    g1: Circle CenterX=0 CenterY=0 CenterZ=0 NormalX=0 NormalY=0 NormalZ=1 AngleXU=0 Radius=3
  constraints (4):
    c: Coincident(g0,g-1)
    c: Coincident(g0,g1)
    c: Diameter(g1) = 6
    c: Diameter(g0) = 19
FEATURE [PartDesign::Pad] Pad077
  AllowMultiFace = false
  Direction = (1,1,1)
  Length = 6
  Length2 = 100
  Profile = -> Sketch116
  Type = 0
FEATURE [PartDesign::Body] Body061  label="6mm_bearing002"
  Group = -> [Sketch116,Pad077]
  Origin = -> Origin078
  Placement = pos=(0,0,81) rot=(0,0,1;0rad)
  Tip = -> Pad077
FEATURE [Sketcher::SketchObject] Sketch117
  FullyConstrained = false
  MapMode = 5
  Support = -> [XY_Plane079]
  sketch-geometry (2):
    g0: Circle CenterX=0 CenterY=0 CenterZ=0 NormalX=0 NormalY=0 NormalZ=1 AngleXU=0 Radius=5.85
    g1: Circle CenterX=0 CenterY=0 CenterZ=0 NormalX=0 NormalY=0 NormalZ=1 AngleXU=0 Radius=3
  constraints (4):
    c: Coincident(g1,g0)
    c: Coincident(g1,g-1)
    c: Diameter(g1) = 6
    c: Diameter(g0) = 11.7
FEATURE [PartDesign::Pad] Pad078
  AllowMultiFace = false
  Direction = (1,1,1)
  Length = 1.5
  Length2 = 100
  Profile = -> Sketch117
  Type = 0
FEATURE [PartDesign::Body] Body062  label="M6_Washer005"
  Group = -> [Sketch117,Pad078]
  Origin = -> Origin079
  Placement = pos=(0,0,79.5) rot=(0,0,1;0rad)
  Tip = -> Pad078
FEATURE [Sketcher::SketchObject] Sketch118
  FullyConstrained = false
  MapMode = 5
  Support = -> [XY_Plane080]
  sketch-geometry (2):
    g0: Circle CenterX=0 CenterY=0 CenterZ=0 NormalX=0 NormalY=0 NormalZ=1 AngleXU=0 Radius=9.5
    g1: Circle CenterX=0 CenterY=0 CenterZ=0 NormalX=0 NormalY=0 NormalZ=1 AngleXU=0 Radius=3
  constraints (4):
    c: Coincident(g0,g-1)
    c: Coincident(g0,g1)
    c: Diameter(g1) = 6
    c: Diameter(g0) = 19
FEATURE [PartDesign::Pad] Pad079
  AllowMultiFace = false
  Direction = (1,1,1)
  Length = 6
  Length2 = 100
  Profile = -> Sketch118
  Type = 0
FEATURE [PartDesign::Body] Body063  label="6mm_bearing003"
  Group = -> [Sketch118,Pad079]
  Origin = -> Origin080
  Placement = pos=(0,0,115) rot=(0,0,1;0rad)
  Tip = -> Pad079
FEATURE [Sketcher::SketchObject] Sketch119
  FullyConstrained = false
  MapMode = 5
  Support = -> [XY_Plane081]
  sketch-geometry (2):
    g0: Circle CenterX=0 CenterY=0 CenterZ=0 NormalX=0 NormalY=0 NormalZ=1 AngleXU=0 Radius=5.85
    g1: Circle CenterX=0 CenterY=0 CenterZ=0 NormalX=0 NormalY=0 NormalZ=1 AngleXU=0 Radius=3
  constraints (4):
    c: Coincident(g1,g0)
    c: Coincident(g1,g-1)
    c: Diameter(g1) = 6
    c: Diameter(g0) = 11.7
FEATURE [PartDesign::Pad] Pad080
  AllowMultiFace = false
  Direction = (1,1,1)
  Length = 1.5
  Length2 = 100
  Profile = -> Sketch119
  Type = 0
FEATURE [PartDesign::Body] Body064  label="M6_Washer006"
  Group = -> [Sketch119,Pad080]
  Origin = -> Origin081
  Placement = pos=(0,0,121) rot=(0,0,1;0rad)
  Tip = -> Pad080
FEATURE [Sketcher::SketchObject] Sketch120
  FullyConstrained = false
  MapMode = 5
  Support = -> [XY_Plane082]
  sketch-geometry (8):
    g0: LineSegment StartX=0 StartY=5.7735 StartZ=0 EndX=-5 EndY=2.88675 EndZ=0
    g1: LineSegment StartX=-5 StartY=2.88675 StartZ=0 EndX=-5 EndY=-2.88675 EndZ=0
    g2: LineSegment StartX=-5 StartY=-2.88675 StartZ=0 EndX=-1.501e-13 EndY=-5.7735 EndZ=0
    g3: LineSegment StartX=-1.501e-13 StartY=-5.7735 StartZ=0 EndX=5 EndY=-2.88675 EndZ=0
    g4: LineSegment StartX=5 StartY=-2.88675 StartZ=0 EndX=5 EndY=2.88675 EndZ=0
    g5: LineSegment StartX=5 StartY=2.88675 StartZ=0 EndX=0 EndY=5.7735 EndZ=0
    g6: Circle CenterX=0 CenterY=0 CenterZ=0 NormalX=0 NormalY=0 NormalZ=1 AngleXU=0 Radius=5.7735
    g7: Circle CenterX=0 CenterY=0 CenterZ=0 NormalX=0 NormalY=0 NormalZ=1 AngleXU=0 Radius=3
  constraints (18):
    c: Coincident(g0,g1)
    c: Coincident(g1,g2)
    c: Coincident(g2,g3)
    c: Coincident(g3,g4)
    c: Coincident(g4,g5)
    c: Coincident(g5,g0)
    c: Equal(g0, g1-g5) x5
    c: PointOnObject(g0,g6)
    c: PointOnObject(g1,g6)
    c: PointOnObject(g2,g6)
    c: PointOnObject(g3,g6)
    c: PointOnObject(g4,g6)
    c: PointOnObject(g5,g6)
    c: Coincident(g6,g-1)
    c: PointOnObject(g0,g-2)
    c: Distance(g0,g4) = 10
    c: Coincident(g7,g-1)
    c: Diameter(g7) = 6
FEATURE [PartDesign::Pad] Pad081
  AllowMultiFace = false
  Direction = (1,1,1)
  Length = 5
  Length2 = 100
  Profile = -> Sketch120
  Type = 0
FEATURE [PartDesign::Body] Body065  label="M6_Full_Nut006"
  Group = -> [Sketch120,Pad081]
  Origin = -> Origin082
  Placement = pos=(0,0,122.5) rot=(0,0,1;0rad)
  Tip = -> Pad081
FEATURE [Sketcher::SketchObject] Sketch121
  FullyConstrained = false
  MapMode = 5
  Support = -> [XY_Plane084]
  sketch-geometry (1):
    g0: Circle CenterX=0 CenterY=0 CenterZ=0 NormalX=0 NormalY=0 NormalZ=1 AngleXU=0 Radius=41.6542
  constraints (1):
    c: Coincident(g0,g-1)
FEATURE [PartDesign::Body] Body066
  Group = -> [Sketch121]
  Origin = -> Origin084
FEATURE [App::Part] Part008  label="wheel001"
  Group = -> [Body056,Body057,Body054,Body055,Body053,Body058,Body061,Body063,Body059,Body060,Body062,Body064,Body065,Body066]
  Origin = -> Origin083
  Placement = pos=(100,72,0) rot=(0,0,1;0rad)
FEATURE [Sketcher::SketchObject] Sketch149
  FullyConstrained = false
  MapMode = 5
  Placement = pos=(0,0,0) rot=(0.57735,0.57735,0.57735;2.0944rad)
  Support = -> [YZ_Plane110]
  sketch-geometry (17):
    g0: LineSegment StartX=16 StartY=28.5 StartZ=0 EndX=16 EndY=26 EndZ=0
    g1: LineSegment StartX=16 StartY=26 StartZ=0 EndX=-16 EndY=26 EndZ=0
    g2: LineSegment StartX=-16 StartY=26 StartZ=0 EndX=-16 EndY=28.5 EndZ=0
    g3: LineSegment StartX=-16 StartY=28.5 StartZ=0 EndX=-17.5 EndY=28.5 EndZ=0
    g4: LineSegment StartX=-17.5 StartY=28.5 StartZ=0 EndX=-17.5 EndY=30 EndZ=0
    g5: LineSegment StartX=-17.5 StartY=30 StartZ=0 EndX=-17.85 EndY=30 EndZ=0
    g6: LineSegment StartX=-19.85 StartY=32 StartZ=0 EndX=-19.85 EndY=35.5078 EndZ=0
    g7: LineSegment StartX=19.85 StartY=35.5078 StartZ=0 EndX=19.85 EndY=32 EndZ=0
    g8: LineSegment StartX=17.85 StartY=30 StartZ=0 EndX=17.5 EndY=30 EndZ=0
    g9: LineSegment StartX=17.5 StartY=30 StartZ=0 EndX=17.5 EndY=28.5 EndZ=0
    g10: LineSegment StartX=17.5 StartY=28.5 StartZ=0 EndX=16 EndY=28.5 EndZ=0
    g11: ArcOfCircle CenterX=5.199e-13 CenterY=-27.17 CenterZ=0 NormalX=0 NormalY=0 NormalZ=1 AngleXU=0 Radius=67.17 StartAngle=1.5708 EndAngle=1.84824
    g12: ArcOfCircle CenterX=5.199e-13 CenterY=-27.17 CenterZ=0 NormalX=0 NormalY=0 NormalZ=1 AngleXU=0 Radius=67.17 StartAngle=1.29335 EndAngle=1.5708
    g13: ArcOfCircle CenterX=-17.85 CenterY=32 CenterZ=0 NormalX=0 NormalY=0 NormalZ=1 AngleXU=0 Radius=2 StartAngle=3.14159 EndAngle=4.71239
    g14: ArcOfCircle CenterX=17.85 CenterY=32 CenterZ=0 NormalX=0 NormalY=0 NormalZ=1 AngleXU=0 Radius=2 StartAngle=4.71239 EndAngle=6.28319
    g15: ArcOfCircle CenterX=-17.85 CenterY=35.5078 CenterZ=0 NormalX=0 NormalY=0 NormalZ=1 AngleXU=0 Radius=2 StartAngle=1.84824 EndAngle=3.14159
    g16: ArcOfCircle CenterX=17.85 CenterY=35.5078 CenterZ=0 NormalX=0 NormalY=0 NormalZ=1 AngleXU=0 Radius=2 StartAngle=-9e-16 EndAngle=1.29335
  constraints (44):
    c: Coincident(g0,g1)
    c: Coincident(g1,g2)
    c: Coincident(g2,g3)
    c: Coincident(g3,g4)
    c: Coincident(g4,g5)
    c: Coincident(g8,g9)
    c: Coincident(g9,g10)
    c: Coincident(g10,g0)
    c: Vertical(g0)
    c: Vertical(g9)
    c: Vertical(g7)
    c: Horizontal(g8)
    c: Horizontal(g10)
    c: Horizontal(g1)
    c: Vertical(g2)
    c: Horizontal(g3)
    c: Horizontal(g5)
    c: Symmetric(g4,g8,g-2)
    c: DistanceX(g4,g8) = 35
    c: Equal(g3,g10)
    c: DistanceX(g10,g10) = 1.5
    c: DistanceY(g-1,g1) = 26
    c: DistanceY(g-1,g3) = 28.5
    c: DistanceY(g-1,g4) = 30
    c: Symmetric(g2,g0,g-2)
    c: Tangent(g11,g12) = -1.5708
    c: PointOnObject(g11,g-2)
    c: Coincident(g12,g11)
    c: DistanceY(g-1,g11) = 40
    c: Tangent(g5,g13) = 1.5708
    c: Tangent(g6,g13) = 1.5708
    c: Tangent(g7,g14) = 1.5708
    c: Tangent(g8,g14) = 1.5708
    c: Radius(g14) = 2
    c: DistanceX(g6,g7) = 39.7
    c: DistanceY(g11,g-1) = 27.17
    c: Tangent(g11,g15) = -1.5708
    c: Tangent(g6,g15) = 1.5708
    c: Tangent(g12,g16) = -1.5708
    c: Tangent(g7,g16) = 1.5708
    c: Symmetric(g6,g7,g-2)
    c: Equal(g16,g15)
    c: Radius(g16) = 2
    c: Symmetric(g6,g7,g-2)
FEATURE [PartDesign::Revolution] Revolution008
  AllowMultiFace = false
  Angle = 360
  Axis = (3e-16,1,-2e-16)
  Base = (0,0,0)
  Placement = pos=(0,0,0) rot=(0.57735,0.57735,0.57735;2.0944rad)
  Profile = -> Sketch149
  ReferenceAxis = -> Sketch149 [H_Axis]
FEATURE [PartDesign::Plane] DatumPlane002
  AttachmentOffset = pos=(0,0,7) rot=(0,0,1;0rad)
  Length = 95.8516
  MapMode = 4
  Placement = pos=(0,7,0) rot=(0.57735,0.57735,0.57735;4.18879rad)
  ResizeMode = 0
  Support = -> [Revolution008]
  Width = 95.8986
FEATURE [Sketcher::SketchObject] Sketch150
  FullyConstrained = false
  MapMode = 5
  Placement = pos=(0,7,0) rot=(0.57735,0.57735,0.57735;4.18879rad)
  Support = -> [DatumPlane002]
  sketch-geometry (26):
    g0: LineSegment StartX=7 StartY=-18.2003 StartZ=0 EndX=19.4726 EndY=1.0332 EndZ=0
    g1: LineSegment StartX=19.4726 StartY=1.0332 StartZ=0 EndX=5.03473 EndY=18.8388 EndZ=0
    g2: LineSegment StartX=5.03473 StartY=18.8388 StartZ=0 EndX=-16.361 EndY=10.6098 EndZ=0
    g3: LineSegment StartX=-16.361 StartY=10.6098 StartZ=0 EndX=-15.1464 EndY=-12.2816 EndZ=0
    g4: LineSegment StartX=-15.1464 StartY=-12.2816 StartZ=0 EndX=7 EndY=-18.2003 EndZ=0
    g5: Circle CenterX=0 CenterY=0 CenterZ=0 NormalX=0 NormalY=0 NormalZ=1 AngleXU=0 Radius=19.5
    g6: ArcOfCircle CenterX=0 CenterY=0 CenterZ=0 NormalX=0 NormalY=0 NormalZ=1 AngleXU=0 Radius=19.5 StartAngle=5.60186 EndAngle=6.33619
    g7: ArcOfCircle CenterX=0 CenterY=0 CenterZ=0 NormalX=0 NormalY=0 NormalZ=1 AngleXU=0 Radius=19.5 StartAngle=4.34522 EndAngle=5.07956
    g8: ArcOfCircle CenterX=0 CenterY=0 CenterZ=0 NormalX=0 NormalY=0 NormalZ=1 AngleXU=0 Radius=19.5 StartAngle=3.08858 EndAngle=3.82292
    g9: ArcOfCircle CenterX=0 CenterY=0 CenterZ=0 NormalX=0 NormalY=0 NormalZ=1 AngleXU=0 Radius=19.5 StartAngle=1.83195 EndAngle=2.56628
    g10: ArcOfCircle CenterX=0 CenterY=0 CenterZ=0 NormalX=0 NormalY=0 NormalZ=1 AngleXU=0 Radius=19.5 StartAngle=0.575309 EndAngle=1.30965
    g11: ArcOfCircle CenterX=17.7078 CenterY=24.3726 CenterZ=0 NormalX=0 NormalY=0 NormalZ=1 AngleXU=0 Radius=13.8285 StartAngle=3.00933 EndAngle=3.5533
    g12: ArcOfCircle CenterX=17.7078 CenterY=24.3726 CenterZ=0 NormalX=0 NormalY=0 NormalZ=1 AngleXU=0 Radius=13.8285 StartAngle=4.61484 EndAngle=5.15882
    g13: ArcOfCircle CenterX=0 CenterY=0 CenterZ=0 NormalX=0 NormalY=0 NormalZ=1 AngleXU=0 Radius=26.5 StartAngle=0.162637 EndAngle=0.465682
    g14: ArcOfCircle CenterX=0 CenterY=0 CenterZ=0 NormalX=0 NormalY=0 NormalZ=1 AngleXU=0 Radius=26.5 StartAngle=1.41927 EndAngle=1.72232
    g15: ArcOfCircle CenterX=-17.7078 CenterY=24.3726 CenterZ=0 NormalX=0 NormalY=0 NormalZ=1 AngleXU=0 Radius=13.8285 StartAngle=5.87148 EndAngle=6.41545
    g16: ArcOfCircle CenterX=-17.7078 CenterY=24.3726 CenterZ=0 NormalX=0 NormalY=0 NormalZ=1 AngleXU=0 Radius=13.8285 StartAngle=4.26596 EndAngle=4.80994
    g17: ArcOfCircle CenterX=-28.6518 CenterY=-9.30952 CenterZ=0 NormalX=0 NormalY=0 NormalZ=1 AngleXU=0 Radius=13.8285 StartAngle=0.844931 EndAngle=1.3889
    g18: ArcOfCircle CenterX=-28.6518 CenterY=-9.30952 CenterZ=0 NormalX=0 NormalY=0 NormalZ=1 AngleXU=0 Radius=13.8285 StartAngle=5.5226 EndAngle=6.06657
    g19: ArcOfCircle CenterX=3.8e-15 CenterY=-30.1262 CenterZ=0 NormalX=0 NormalY=0 NormalZ=1 AngleXU=0 Radius=13.8285 StartAngle=2.10157 EndAngle=2.64554
    g20: ArcOfCircle CenterX=3.8e-15 CenterY=-30.1262 CenterZ=0 NormalX=0 NormalY=0 NormalZ=1 AngleXU=0 Radius=13.8285 StartAngle=0.496052 EndAngle=1.04002
    g21: ArcOfCircle CenterX=28.6518 CenterY=-9.30952 CenterZ=0 NormalX=0 NormalY=0 NormalZ=1 AngleXU=0 Radius=13.8285 StartAngle=3.35821 EndAngle=3.90218
    g22: ArcOfCircle CenterX=28.6518 CenterY=-9.30952 CenterZ=0 NormalX=0 NormalY=0 NormalZ=1 AngleXU=0 Radius=13.8285 StartAngle=1.75269 EndAngle=2.29666
    g23: ArcOfCircle CenterX=0 CenterY=0 CenterZ=0 NormalX=0 NormalY=0 NormalZ=1 AngleXU=0 Radius=26.5 StartAngle=2.67591 EndAngle=2.97896
    g24: ArcOfCircle CenterX=0 CenterY=0 CenterZ=0 NormalX=0 NormalY=0 NormalZ=1 AngleXU=0 Radius=26.5 StartAngle=3.93255 EndAngle=4.23559
    g25: ArcOfCircle CenterX=0 CenterY=0 CenterZ=0 NormalX=0 NormalY=0 NormalZ=1 AngleXU=0 Radius=26.5 StartAngle=5.18918 EndAngle=5.49223
  constraints (74):
    c: Coincident(g0,g1)
    c: Coincident(g1,g2)
    c: Coincident(g2,g3)
    c: Coincident(g3,g4)
    c: Coincident(g4,g0)
    c: Equal(g0, g1-g4) x4
    c: PointOnObject(g0,g5)
    c: PointOnObject(g1,g5)
    c: PointOnObject(g2,g5)
    c: PointOnObject(g3,g5)
    c: PointOnObject(g4,g5)
    c: Coincident(g5,g-1)
    c: Coincident(g10,g6)
    c: Coincident(g10,g7)
    c: Coincident(g10,g8)
    c: Coincident(g10,g9)
    c: Coincident(g10,g-1)
    c: Coincident(g10,g1)
    c: Coincident(g6,g0)
    c: Coincident(g7,g0)
    c: Coincident(g8,g3)
    c: Coincident(g9,g2)
    c: Distance(g8,g8) = 14
    c: Distance(g9,g9) = 14
    c: Distance(g10,g10) = 14
    c: Distance(g6,g6) = 14
    c: Distance(g7,g7) = 14
    c: Diameter(g5) = 39
    c: DistanceX(g-2,g7) = -7
    c: Coincident(g11,g10)
    c: Coincident(g12,g10)
    c: Coincident(g12,g11)
    c: Coincident(g14,g13)
    c: Coincident(g14,g6)
    c: Coincident(g14,g11)
    c: Coincident(g13,g12)
    c: Equal(g14,g13)
    c: Diameter(g14) = 53
    c: Equal(g12,g11)
    c: Coincident(g15,g16)
    c: Coincident(g15,g14)
    c: Coincident(g15,g9)
    c: Coincident(g16,g9)
    c: Coincident(g17,g8)
    c: Coincident(g17,g18)
    c: Coincident(g18,g8)
    c: Equal(g18,g17)
    c: Equal(g17,g16)
    c: Equal(g16,g15)
    c: Equal(g15,g11)
    c: Coincident(g22,g21)
    c: Coincident(g20,g19)
    c: Coincident(g19,g7)
    c: Coincident(g20,g7)
    c: Coincident(g21,g6)
    c: Coincident(g22,g6)
    c: Coincident(g22,g13)
    c: Equal(g19,g20)
    c: Equal(g20,g21)
    c: Equal(g21,g22)
    c: Equal(g22,g12)
    c: Coincident(g25,g23)
    c: Coincident(g25,g24)
    c: Coincident(g25,g6)
    c: Coincident(g20,g25)
    c: Coincident(g21,g25)
    c: Coincident(g24,g19)
    c: Coincident(g24,g18)
    c: Coincident(g23,g17)
    c: Coincident(g23,g16)
    c: Equal(g23,g24)
    c: Equal(g24,g25)
    c: Equal(g25,g13)
    c: Distance(g16,g17) = 8
FEATURE [PartDesign::Pad] Pad099
  AllowMultiFace = false
  BaseFeature = -> Revolution008
  Direction = (1,1,1)
  Length = 2
  Length2 = 100
  Placement = pos=(0,0,0) rot=(0.57735,0.57735,0.57735;2.0944rad)
  Profile = -> Sketch150
  Type = 0
FEATURE [Sketcher::SketchObject] Sketch151
  FullyConstrained = false
  MapMode = 5
  Placement = pos=(0,7,0) rot=(0.57735,0.57735,-0.57735;2.0944rad)
  Support = -> [Pad099]
  sketch-geometry (1):
    g0: Circle CenterX=0 CenterY=0 CenterZ=0 NormalX=0 NormalY=0 NormalZ=1 AngleXU=0 Radius=8.5
  constraints (2):
    c: Coincident(g0,g-1)
    c: Diameter(g0) = 17
FEATURE [Sketcher::SketchObject] Sketch153
  FullyConstrained = false
  MapMode = 5
  Placement = pos=(0,0,0) rot=(0.57735,0.57735,0.57735;2.0944rad)
  Support = -> [YZ_Plane110]
  sketch-geometry (9):
    g0: LineSegment StartX=9 StartY=-2 StartZ=0 EndX=9 EndY=-19.5 EndZ=0
    g1: LineSegment StartX=9 StartY=-19.5 StartZ=0 EndX=9.5 EndY=-19.5 EndZ=0
    g2: LineSegment StartX=9.5 StartY=-19.5 StartZ=0 EndX=12 EndY=-12.5 EndZ=0
    g3: LineSegment StartX=12 StartY=-12.5 StartZ=0 EndX=11 EndY=-7 EndZ=0
    g4: LineSegment StartX=11 StartY=-7 StartZ=0 EndX=14 EndY=-7 EndZ=0
    g5: LineSegment StartX=14 StartY=-7 StartZ=0 EndX=14 EndY=-5 EndZ=0
    g6: LineSegment StartX=14 StartY=-5 StartZ=0 EndX=12 EndY=-5 EndZ=0
    g7: LineSegment StartX=12 StartY=-5 StartZ=0 EndX=12 EndY=-2 EndZ=0
    g8: LineSegment StartX=12 StartY=-2 StartZ=0 EndX=9 EndY=-2 EndZ=0
  constraints (27):
    c: Coincident(g0,g1)
    c: Coincident(g1,g2)
    c: Coincident(g2,g3)
    c: Coincident(g3,g4)
    c: Coincident(g4,g5)
    c: Coincident(g5,g6)
    c: Coincident(g6,g7)
    c: Coincident(g7,g8)
    c: Coincident(g0,g8)
    c: Vertical(g0)
    c: DistanceX(g-1,g0) = 9
    c: DistanceY(g0,g-1) = 19.5
    c: Horizontal(g1)
    c: DistanceY(g0,g-1) = 2
    c: Horizontal(g8)
    c: Vertical(g7)
    c: DistanceX(g8,g8) = 3
    c: Horizontal(g6)
    c: DistanceX(g6,g6) = 2
    c: DistanceY(g5,g-1) = 5
    c: DistanceY(g4,g-1) = 7
    c: Vertical(g5)
    c: DistanceX(g0,g2) = 3
    c: DistanceX(g1,g1) = 0.5
    c: Horizontal(g4)
    c: DistanceX(g4,g4) = 3
    c: DistanceY(g2,g-1) = 12.5
FEATURE [PartDesign::Revolution] Revolution009
  AllowMultiFace = false
  Angle = 360
  Axis = (3e-16,1,-2e-16)
  Base = (0,0,0)
  BaseFeature = -> Pad099
  Placement = pos=(0,0,0) rot=(0.57735,0.57735,0.57735;2.0944rad)
  Profile = -> Sketch153
  ReferenceAxis = -> Sketch153 [H_Axis]
  Reversed = true
FEATURE [Sketcher::SketchObject] Sketch154
  FullyConstrained = false
  MapMode = 5
  Support = -> [XY_Plane110]
  sketch-geometry (3):
    g0: LineSegment StartX=7.5 StartY=7 StartZ=0 EndX=17.5 EndY=7 EndZ=0
    g1: LineSegment StartX=17.5 StartY=7 StartZ=0 EndX=12.5 EndY=10 EndZ=0
    g2: LineSegment StartX=12.5 StartY=10 StartZ=0 EndX=7.5 EndY=7 EndZ=0
  constraints (9):
    c: Coincident(g0,g1)
    c: Coincident(g1,g2)
    c: Coincident(g0,g2)
    c: DistanceY(g-1,g0) = 7
    c: Horizontal(g0)
    c: DistanceY(g0,g1) = 3
    c: DistanceX(g-1,g0) = 17.5
    c: DistanceX(g-1,g1) = 12.5
    c: DistanceX(g-1,g0) = 7.5
FEATURE [PartDesign::Groove] Groove002
  AllowMultiFace = false
  Angle = 360
  Axis = (0,1,0)
  Base = (0,0,0)
  BaseFeature = -> Revolution009
  Placement = pos=(0,0,0) rot=(0.57735,0.57735,0.57735;2.0944rad)
  Profile = -> Sketch154
  ReferenceAxis = -> Sketch154 [V_Axis]
FEATURE [PartDesign::Pad] Pad100
  AllowMultiFace = false
  BaseFeature = -> Groove002
  Direction = (1,1,1)
  Length = 1.5
  Length2 = 100
  Placement = pos=(0,0,0) rot=(0.57735,0.57735,0.57735;2.0944rad)
  Profile = -> Sketch151
  Type = 0
FEATURE [Sketcher::SketchObject] Sketch152
  FullyConstrained = false
  MapMode = 5
  Placement = pos=(0,5.5,0) rot=(0.57735,0.57735,-0.57735;2.0944rad)
  Support = -> [Pad100]
  sketch-geometry (7):
    g0: LineSegment StartX=6 StartY=-3.4641 StartZ=0 EndX=6 EndY=3.4641 EndZ=0
    g1: LineSegment StartX=6 StartY=3.4641 StartZ=0 EndX=9e-16 EndY=6.9282 EndZ=0
    g2: LineSegment StartX=9e-16 StartY=6.9282 StartZ=0 EndX=-6 EndY=3.4641 EndZ=0
    g3: LineSegment StartX=-6 StartY=3.4641 StartZ=0 EndX=-6 EndY=-3.4641 EndZ=0
    g4: LineSegment StartX=-6 StartY=-3.4641 StartZ=0 EndX=0 EndY=-6.9282 EndZ=0
    g5: LineSegment StartX=0 StartY=-6.9282 StartZ=0 EndX=6 EndY=-3.4641 EndZ=0
    g6: Circle CenterX=0 CenterY=0 CenterZ=0 NormalX=0 NormalY=0 NormalZ=1 AngleXU=0 Radius=6.9282
  constraints (16):
    c: Coincident(g0,g1)
    c: Coincident(g1,g2)
    c: Coincident(g2,g3)
    c: Coincident(g3,g4)
    c: Coincident(g4,g5)
    c: Coincident(g5,g0)
    c: Equal(g0, g1-g5) x5
    c: PointOnObject(g0,g6)
    c: PointOnObject(g1,g6)
    c: PointOnObject(g2,g6)
    c: PointOnObject(g3,g6)
    c: PointOnObject(g4,g6)
    c: PointOnObject(g5,g6)
    c: Coincident(g6,g-1)
    c: Vertical(g3)
    c: DistanceX(g2,g0) = 12
FEATURE [Sketcher::SketchObject] Sketch155
  FullyConstrained = false
  MapMode = 5
  Support = -> [XY_Plane110]
  sketch-geometry (6):
    g0: LineSegment StartX=26.5 StartY=-6 StartZ=0 EndX=26.5 EndY=8 EndZ=0
    g1: LineSegment StartX=26.5 StartY=8 StartZ=0 EndX=17.5 EndY=8 EndZ=0
    g2: LineSegment StartX=17.5 StartY=8 StartZ=0 EndX=12.5 EndY=12 EndZ=0
    g3: LineSegment StartX=12.5 StartY=12 StartZ=0 EndX=6.25 EndY=14 EndZ=0
    g4: LineSegment StartX=6.25 StartY=14 StartZ=0 EndX=6.25 EndY=6 EndZ=0
    g5: ArcOfCircle CenterX=7.23279 CenterY=-15.4275 CenterZ=0 NormalX=0 NormalY=0 NormalZ=1 AngleXU=0 Radius=21.45 StartAngle=0.455052 EndAngle=1.61663
  constraints (19):
    c: Coincident(g0,g1)
    c: Coincident(g1,g2)
    c: Coincident(g2,g3)
    c: Coincident(g3,g4)
    c: Horizontal(g1)
    c: Vertical(g0)
    c: Vertical(g4)
    c: Coincident(g5,g0)
    c: Coincident(g5,g4)
    c: Diameter(g5) = 42.9
    c: DistanceY(g0,g0) = 14
    c: DistanceY(g4,g4) = 8
    c: DistanceY(g0,g-1) = 6
    c: DistanceX(g-1,g2) = 12.5
    c: DistanceX(g-1,g3) = 6.25
    c: DistanceX(g-1,g1) = 17.5
    c: DistanceX(g-1,g0) = 26.5
    c: DistanceY(g-1,g4) = 6
    c: DistanceY(g2,g3) = 2
FEATURE [PartDesign::Pad] Pad101
  AllowMultiFace = false
  BaseFeature = -> Pad100
  Direction = (1,1,1)
  Length = 1.5
  Length2 = 100
  Midplane = true
  Placement = pos=(0,0,0) rot=(0.57735,0.57735,0.57735;2.0944rad)
  Profile = -> Sketch155
  Type = 0
FEATURE [PartDesign::PolarPattern] PolarPattern002
  Angle = 360
  Axis = -> Y_Axis110
  BaseFeature = -> Pad101
  Occurrences = 5
  Originals = -> [Pad101]
  Placement = pos=(0,0,0) rot=(0.57735,0.57735,0.57735;2.0944rad)
FEATURE [PartDesign::Pocket] Pocket039
  AllowMultiFace = false
  BaseFeature = -> PolarPattern002
  Length = 4.8
  Length2 = 100
  Placement = pos=(0,0,0) rot=(0.57735,0.57735,0.57735;2.0944rad)
  Profile = -> Sketch152
  Type = 0
FEATURE [PartDesign::Body] Body087  label="Wheel002"
  Group = -> [Sketch149,Revolution008,DatumPlane002,Sketch150,Pad099,Sketch151,Sketch152,Sketch153,Sketch154,Revolution009,Groove002,Pad100,Pad101,PolarPattern002,Pocket039,Sketch155]
  Origin = -> Origin111
  Tip = -> Pad099
FEATURE [Sketcher::SketchObject] Sketch156
  FullyConstrained = false
  MapMode = 5
  Support = -> [XY_Plane111]
  sketch-geometry (7):
    g0: LineSegment StartX=6 StartY=3.4641 StartZ=0 EndX=3.87264e-11 EndY=6.9282 EndZ=0
    g1: LineSegment StartX=3.8726e-11 StartY=6.9282 StartZ=0 EndX=-6 EndY=3.4641 EndZ=0
    g2: LineSegment StartX=-6 StartY=3.4641 StartZ=0 EndX=-6 EndY=-3.4641 EndZ=0
    g3: LineSegment StartX=-6 StartY=-3.4641 StartZ=0 EndX=1.74527e-11 EndY=-6.9282 EndZ=0
    g4: LineSegment StartX=1.74523e-11 StartY=-6.9282 StartZ=0 EndX=6 EndY=-3.4641 EndZ=0
    g5: LineSegment StartX=6 StartY=-3.4641 StartZ=0 EndX=6 EndY=3.4641 EndZ=0
    g6: Circle CenterX=0 CenterY=0 CenterZ=0 NormalX=0 NormalY=0 NormalZ=1 AngleXU=0 Radius=6.9282
  constraints (16):
    c: Coincident(g0,g1)
    c: Coincident(g1,g2)
    c: Coincident(g2,g3)
    c: Coincident(g3,g4)
    c: Coincident(g4,g5)
    c: Coincident(g5,g0)
    c: Equal(g0, g1-g5) x5
    c: PointOnObject(g0,g6)
    c: PointOnObject(g1,g6)
    c: PointOnObject(g2,g6)
    c: PointOnObject(g3,g6)
    c: PointOnObject(g4,g6)
    c: PointOnObject(g5,g6)
    c: Coincident(g6,g-1)
    c: Vertical(g5)
    c: DistanceX(g1,g0) = 12
FEATURE [PartDesign::Pad] Pad102
  AllowMultiFace = false
  Direction = (1,1,1)
  Length = 6
  Length2 = 100
  Profile = -> Sketch156
  Type = 0
FEATURE [Sketcher::SketchObject] Sketch157
  FullyConstrained = false
  MapMode = 5
  Placement = pos=(0,0,6) rot=(0,0,1;0rad)
  Support = -> [Pad102]
  sketch-geometry (1):
    g0: Circle CenterX=0 CenterY=0 CenterZ=0 NormalX=0 NormalY=0 NormalZ=1 AngleXU=0 Radius=6
  constraints (2):
    c: Coincident(g0,g-1)
    c: Diameter(g0) = 12
FEATURE [PartDesign::Pad] Pad103
  AllowMultiFace = false
  BaseFeature = -> Pad102
  Direction = (1,1,1)
  Length = 24
  Length2 = 100
  Profile = -> Sketch157
  Type = 0
FEATURE [Sketcher::SketchObject] Sketch158
  FullyConstrained = false
  MapMode = 5
  Placement = pos=(0,0,30) rot=(0,0,1;0rad)
  Support = -> [Pad103]
  sketch-geometry (1):
    g0: Circle CenterX=0 CenterY=0 CenterZ=0 NormalX=0 NormalY=0 NormalZ=1 AngleXU=0 Radius=3
  constraints (2):
    c: Coincident(g0,g-1)
    c: Diameter(g0) = 6
FEATURE [PartDesign::Pocket] Pocket040
  AllowMultiFace = false
  BaseFeature = -> Pad103
  Length = 24.5
  Length2 = 100
  Profile = -> Sketch158
  Type = 0
FEATURE [Sketcher::SketchObject] Sketch159
  FullyConstrained = false
  MapMode = 5
  Placement = pos=(0,0,0) rot=(1,0,0;3.14159rad)
  Support = -> [Pocket040]
  sketch-geometry (1):
    g0: Circle CenterX=0 CenterY=0 CenterZ=0 NormalX=0 NormalY=0 NormalZ=1 AngleXU=0 Radius=1.75
  constraints (2):
    c: Coincident(g0,g-1)
    c: Diameter(g0) = 3.5
FEATURE [PartDesign::Pocket] Pocket041
  AllowMultiFace = false
  BaseFeature = -> Pocket040
  Length = 6
  Length2 = 100
  Profile = -> Sketch159
  Type = 0
FEATURE [Sketcher::SketchObject] Sketch160
  FullyConstrained = false
  MapMode = 5
  Placement = pos=(0,0,0) rot=(1,0,0;1.5708rad)
  Support = -> [XZ_Plane111]
  sketch-geometry (1):
    g0: Circle CenterX=0 CenterY=24.5 CenterZ=0 NormalX=0 NormalY=0 NormalZ=1 AngleXU=0 Radius=1.75
  constraints (3):
    c: PointOnObject(g0,g-2)
    c: DistanceY(g-1,g0) = 24.5
    c: Diameter(g0) = 3.5
FEATURE [PartDesign::Pocket] Pocket042
  AllowMultiFace = false
  BaseFeature = -> Pocket041
  Length = 14
  Length2 = 100
  Midplane = true
  Profile = -> Sketch160
  Type = 0
FEATURE [PartDesign::Body] Body088  label="Axel002"
  Group = -> [Sketch156,Pad102,Sketch157,Pad103,Sketch158,Pocket040,Sketch159,Pocket041,Sketch160,Pocket042]
  Origin = -> Origin110
  Placement = pos=(0,10.3,0) rot=(0.935113,-0.250563,0.250563;1.63783rad)
  Tip = -> Pocket042
FEATURE [Sketcher::SketchObject] Sketch161
  FullyConstrained = false
  MapMode = 5
  Support = -> [XY_Plane112]
  sketch-geometry (4):
    g0: LineSegment StartX=-16 StartY=16 StartZ=0 EndX=30 EndY=16 EndZ=0
    g1: LineSegment StartX=30 StartY=16 StartZ=0 EndX=30 EndY=-16 EndZ=0
    g2: LineSegment StartX=30 StartY=-16 StartZ=0 EndX=-16 EndY=-16 EndZ=0
    g3: LineSegment StartX=-16 StartY=-16 StartZ=0 EndX=-16 EndY=16 EndZ=0
  constraints (11):
    c: Coincident(g0,g1)
    c: Coincident(g1,g2)
    c: Coincident(g2,g3)
    c: Coincident(g3,g0)
    c: Horizontal(g0)
    c: Horizontal(g2)
    c: Vertical(g1)
    c: DistanceX(g0,g0) = 46
    c: DistanceY(g3,g3) = 32
    c: Symmetric(g0,g2,g-1)
    c: DistanceX(g2,g-1) = 16
FEATURE [PartDesign::Pad] Pad104
  AllowMultiFace = false
  Direction = (1,1,1)
  Length = 21
  Length2 = 100
  Profile = -> Sketch161
  Type = 0
FEATURE [Sketcher::SketchObject] Sketch162
  FullyConstrained = false
  MapMode = 5
  Placement = pos=(30,0,0) rot=(0.57735,0.57735,0.57735;2.0944rad)
  Support = -> [Pad104]
  sketch-geometry (1):
    g0: Circle CenterX=0 CenterY=12.5 CenterZ=0 NormalX=0 NormalY=0 NormalZ=1 AngleXU=0 Radius=12.5
  constraints (3):
    c: Diameter(g0) = 25
    c: PointOnObject(g0,g-2)
    c: DistanceY(g-1,g0) = 12.5
FEATURE [PartDesign::Pad] Pad105
  AllowMultiFace = false
  BaseFeature = -> Pad104
  Direction = (1,1,1)
  Length = 32
  Length2 = 100
  Profile = -> Sketch162
  Type = 0
FEATURE [Sketcher::SketchObject] Sketch163
  FullyConstrained = false
  MapMode = 5
  Placement = pos=(0,0,0) rot=(1,0,0;3.14159rad)
  Support = -> [Pad105]
  sketch-geometry (2):
    g0: ArcOfCircle CenterX=0 CenterY=0 CenterZ=0 NormalX=0 NormalY=0 NormalZ=1 AngleXU=0 Radius=3 StartAngle=0.585686 EndAngle=5.6975
    g1: LineSegment StartX=2.5 StartY=1.65831 StartZ=0 EndX=2.5 EndY=-1.65831 EndZ=0
  constraints (6):
    c: Coincident(g0,g-1)
    c: Diameter(g0) = 6
    c: Coincident(g1,g0)
    c: Coincident(g1,g0)
    c: Vertical(g1)
    c: DistanceX(g0,g0) = 2.5
FEATURE [PartDesign::Pad] Pad106
  AllowMultiFace = false
  BaseFeature = -> Pad105
  Direction = (1,1,1)
  Length = 15
  Length2 = 100
  Profile = -> Sketch163
  Type = 0
FEATURE [Sketcher::SketchObject] Sketch164
  FullyConstrained = false
  MapMode = 5
  Placement = pos=(0,0,21) rot=(0,0,1;0rad)
  Support = -> [Pad106]
  sketch-geometry (2):
    g0: ArcOfCircle CenterX=0 CenterY=0 CenterZ=0 NormalX=0 NormalY=0 NormalZ=1 AngleXU=0 Radius=3 StartAngle=0.585686 EndAngle=5.6975
    g1: LineSegment StartX=2.5 StartY=1.65831 StartZ=0 EndX=2.5 EndY=-1.65831 EndZ=0
  constraints (6):
    c: Coincident(g0,g-1)
    c: Coincident(g1,g0)
    c: Coincident(g1,g0)
    c: Vertical(g1)
    c: DistanceX(g0,g0) = 2.5
    c: Diameter(g0) = 6
FEATURE [PartDesign::Pad] Pad107
  AllowMultiFace = false
  BaseFeature = -> Pad106
  Direction = (1,1,1)
  Length = 15
  Length2 = 100
  Profile = -> Sketch164
  Type = 0
FEATURE [PartDesign::Body] Body085  label="Motor002"
  Group = -> [Sketch161,Pad104,Sketch162,Pad105,Sketch163,Pad106,Sketch164,Pad107]
  Origin = -> Origin113
  Placement = pos=(-1.1e-14,-24,0) rot=(0.57735,-0.57735,0.57735;2.0944rad)
  Tip = -> Pad107
FEATURE [Sketcher::SketchObject] Sketch165
  FullyConstrained = false
  MapMode = 5
  Placement = pos=(0,0,0) rot=(0.57735,0.57735,0.57735;2.0944rad)
  Support = -> [YZ_Plane113]
  sketch-geometry (8):
    g0: LineSegment StartX=-24 StartY=64 StartZ=0 EndX=-24 EndY=-12 EndZ=0
    g1: LineSegment StartX=-24 StartY=-12 StartZ=0 EndX=-21 EndY=-12 EndZ=0
    g2: LineSegment StartX=-21 StartY=-12 StartZ=0 EndX=-21 EndY=64 EndZ=0
    g3: LineSegment StartX=-20 StartY=65 StartZ=0 EndX=16 EndY=65 EndZ=0
    g4: LineSegment StartX=16 StartY=65 StartZ=0 EndX=16 EndY=68 EndZ=0
    g5: LineSegment StartX=16 StartY=68 StartZ=0 EndX=-20 EndY=68 EndZ=0
    g6: ArcOfCircle CenterX=-20 CenterY=64 CenterZ=0 NormalX=0 NormalY=0 NormalZ=1 AngleXU=0 Radius=4 StartAngle=1.5708 EndAngle=3.14159
    g7: ArcOfCircle CenterX=-20 CenterY=64 CenterZ=0 NormalX=0 NormalY=0 NormalZ=1 AngleXU=0 Radius=1 StartAngle=1.5708 EndAngle=3.14159
  constraints (21):
    c: Coincident(g0,g1)
    c: Coincident(g1,g2)
    c: Coincident(g3,g4)
    c: Coincident(g4,g5)
    c: Vertical(g0)
    c: Horizontal(g1)
    c: Tangent(g7,g2) = 1.5708
    c: Tangent(g7,g3) = 1.5708
    c: Tangent(g6,g0) = -1.5708
    c: Tangent(g6,g5) = -1.5708
    c: Horizontal(g5)
    c: Vertical(g4)
    c: Equal(g1,g4)
    c: DistanceY(g4,g4) = 3
    c: Diameter(g7) = 2
    c: Horizontal(g3)
    c: DistanceY(g1,g-1) = 12
    c: DistanceY(g-1,g3) = 65
    c: Coincident(g6,g7)
    c: DistanceX(g0,g-1) = 24
    c: DistanceX(g0,g4) = 40
FEATURE [PartDesign::Pad] Pad108
  AllowMultiFace = false
  Direction = (1,1,1)
  Length = 30
  Length2 = 100
  Midplane = true
  Placement = pos=(0,0,0) rot=(0.57735,0.57735,0.57735;2.0944rad)
  Profile = -> Sketch165
  Type = 0
FEATURE [Sketcher::SketchObject] Sketch166
  FullyConstrained = false
  MapMode = 5
  Placement = pos=(-1.9e-14,2.99e-14,68) rot=(0,0,-1;1.5708rad)
  Support = -> [Pad108]
  sketch-geometry (9):
    g0: Circle CenterX=0 CenterY=0 CenterZ=0 NormalX=0 NormalY=0 NormalZ=1 AngleXU=0 Radius=3.25
    g1: LineSegment StartX=-10 StartY=10 StartZ=0 EndX=10 EndY=10 EndZ=0
    g2: LineSegment StartX=10 StartY=10 StartZ=0 EndX=10 EndY=-10 EndZ=0
    g3: LineSegment StartX=10 StartY=-10 StartZ=0 EndX=-10 EndY=-10 EndZ=0
    g4: LineSegment StartX=-10 StartY=-10 StartZ=0 EndX=-10 EndY=10 EndZ=0
    g5: Circle CenterX=10 CenterY=10 CenterZ=0 NormalX=0 NormalY=0 NormalZ=1 AngleXU=0 Radius=1.75
    g6: Circle CenterX=10 CenterY=-10 CenterZ=0 NormalX=0 NormalY=0 NormalZ=1 AngleXU=0 Radius=1.75
    g7: Circle CenterX=-10 CenterY=-10 CenterZ=0 NormalX=0 NormalY=0 NormalZ=1 AngleXU=0 Radius=1.75
    g8: Circle CenterX=-10 CenterY=10 CenterZ=0 NormalX=0 NormalY=0 NormalZ=1 AngleXU=0 Radius=1.75
  constraints (21):
    c: Coincident(g0,g-1)
    c: Diameter(g0) = 6.5
    c: Coincident(g1,g2)
    c: Coincident(g2,g3)
    c: Coincident(g3,g4)
    c: Coincident(g4,g1)
    c: Horizontal(g1)
    c: Horizontal(g3)
    c: Vertical(g2)
    c: Vertical(g4)
    c: DistanceX(g1,g1) = 20
    c: DistanceY(g4,g4) = 20
    c: Symmetric(g1,g2,g0)
    c: Coincident(g8,g1)
    c: Coincident(g5,g1)
    c: Coincident(g6,g2)
    c: Coincident(g7,g3)
    c: Diameter(g7) = 3.5
    c: Equal(g7,g6)
    c: Equal(g7,g5)
    c: Equal(g7,g8)
FEATURE [PartDesign::Pocket] Pocket043
  AllowMultiFace = false
  BaseFeature = -> Pad108
  Length = 5
  Length2 = 100
  Placement = pos=(0,0,0) rot=(0.57735,0.57735,0.57735;2.0944rad)
  Profile = -> Sketch166
  Type = 0
FEATURE [PartDesign::Body] Body086  label="Wheel Bracket002"
  Group = -> [Sketch165,Pad108,Sketch166,Pocket043]
  Origin = -> Origin112
  Tip = -> Pocket043
FEATURE [Part::Part2DObjectPython] InvoluteGear004  # Draft 2D object (typed FeaturePython)
  ExternalGear = true
  HighPrecision = true
  Modules = 2
  NumberOfTeeth = 26
  PressureAngle = 20
FEATURE [PartDesign::Pad] Pad109
  AllowMultiFace = false
  Direction = (1,1,1)
  Length = 5
  Length2 = 100
  Profile = -> InvoluteGear004
  Type = 0
FEATURE [Sketcher::SketchObject] Sketch167
  FullyConstrained = false
  MapMode = 5
  Placement = pos=(0,0,5) rot=(0,0,1;0rad)
  Support = -> [Pad109]
  sketch-geometry (9):
    g0: Circle CenterX=0 CenterY=0 CenterZ=0 NormalX=0 NormalY=0 NormalZ=1 AngleXU=0 Radius=3.25
    g1: LineSegment StartX=-10 StartY=10 StartZ=0 EndX=10 EndY=10 EndZ=0
    g2: LineSegment StartX=10 StartY=10 StartZ=0 EndX=10 EndY=-10 EndZ=0
    g3: LineSegment StartX=10 StartY=-10 StartZ=0 EndX=-10 EndY=-10 EndZ=0
    g4: LineSegment StartX=-10 StartY=-10 StartZ=0 EndX=-10 EndY=10 EndZ=0
    g5: Circle CenterX=-10 CenterY=10 CenterZ=0 NormalX=0 NormalY=0 NormalZ=1 AngleXU=0 Radius=1.75
    g6: Circle CenterX=10 CenterY=10 CenterZ=0 NormalX=0 NormalY=0 NormalZ=1 AngleXU=0 Radius=1.75
    g7: Circle CenterX=10 CenterY=-10 CenterZ=0 NormalX=0 NormalY=0 NormalZ=1 AngleXU=0 Radius=1.75
    g8: Circle CenterX=-10 CenterY=-10 CenterZ=0 NormalX=0 NormalY=0 NormalZ=1 AngleXU=0 Radius=1.75
  constraints (21):
    c: Coincident(g0,g-1)
    c: Diameter(g0) = 6.5
    c: Coincident(g1,g2)
    c: Coincident(g2,g3)
    c: Coincident(g3,g4)
    c: Coincident(g4,g1)
    c: Horizontal(g1)
    c: Horizontal(g3)
    c: Vertical(g2)
    c: Vertical(g4)
    c: DistanceX(g3,g3) = 20
    c: DistanceY(g4,g4) = 20
    c: Symmetric(g2,g1,g0)
    c: Coincident(g8,g3)
    c: Coincident(g7,g2)
    c: Coincident(g6,g1)
    c: Coincident(g5,g1)
    c: Diameter(g5) = 3.5
    c: Equal(g5,g8)
    c: Equal(g5,g6)
    c: Equal(g5,g7)
FEATURE [PartDesign::Pocket] Pocket044
  AllowMultiFace = false
  BaseFeature = -> Pad109
  Length = 5
  Length2 = 100
  Profile = -> Sketch167
  Type = 0
FEATURE [PartDesign::Body] Body084  label="Wheel Gear002"
  Group = -> [InvoluteGear004,Pad109,Sketch167,Pocket044]
  Origin = -> Origin114
  Placement = pos=(0,0,68) rot=(0,0,1;0rad)
  Tip = -> Pocket044
FEATURE [Sketcher::SketchObject] Sketch168
  FullyConstrained = false
  MapMode = 5
  Support = -> [XY_Plane115]
  sketch-geometry (1):
    g0: Circle CenterX=0 CenterY=0 CenterZ=0 NormalX=0 NormalY=0 NormalZ=1 AngleXU=0 Radius=2.95
  constraints (2):
    c: Coincident(g0,g-1)
    c: Diameter(g0) = 5.9
FEATURE [PartDesign::Pad] Pad110
  AllowMultiFace = false
  Direction = (1,1,1)
  Length = 70
  Length2 = 100
  Profile = -> Sketch168
  Type = 0
FEATURE [Sketcher::SketchObject] Sketch169
  FullyConstrained = false
  MapMode = 5
  Placement = pos=(0,0,0) rot=(1,0,0;3.14159rad)
  Support = -> [Pad110]
  sketch-geometry (7):
    g0: LineSegment StartX=-3.917e-13 StartY=5.7735 StartZ=0 EndX=-5 EndY=2.88675 EndZ=0
    g1: LineSegment StartX=-5 StartY=2.88675 StartZ=0 EndX=-5 EndY=-2.88675 EndZ=0
    g2: LineSegment StartX=-5 StartY=-2.88675 StartZ=0 EndX=0 EndY=-5.7735 EndZ=0
    g3: LineSegment StartX=0 StartY=-5.7735 StartZ=0 EndX=5 EndY=-2.88675 EndZ=0
    g4: LineSegment StartX=5 StartY=-2.88675 StartZ=0 EndX=5 EndY=2.88675 EndZ=0
    g5: LineSegment StartX=5 StartY=2.88675 StartZ=0 EndX=-3.917e-13 EndY=5.7735 EndZ=0
    g6: Circle CenterX=0 CenterY=0 CenterZ=0 NormalX=0 NormalY=0 NormalZ=1 AngleXU=0 Radius=5.7735
  constraints (16):
    c: Coincident(g0,g1)
    c: Coincident(g1,g2)
    c: Coincident(g2,g3)
    c: Coincident(g3,g4)
    c: Coincident(g4,g5)
    c: Coincident(g5,g0)
    c: Equal(g0, g1-g5) x5
    c: PointOnObject(g0,g6)
    c: PointOnObject(g1,g6)
    c: PointOnObject(g2,g6)
    c: PointOnObject(g3,g6)
    c: PointOnObject(g4,g6)
    c: PointOnObject(g5,g6)
    c: Coincident(g6,g-1)
    c: Distance(g0,g4) = 10
    c: PointOnObject(g2,g-2)
FEATURE [PartDesign::Pad] Pad111
  AllowMultiFace = false
  BaseFeature = -> Pad110
  Direction = (1,1,1)
  Length = 4
  Length2 = 100
  Profile = -> Sketch169
  Type = 0
FEATURE [PartDesign::Body] Body089  label="M6x70_Hex_Head002"
  Group = -> [Sketch168,Pad110,Sketch169,Pad111]
  Origin = -> Origin115
  Placement = pos=(0,0,65) rot=(0,0,1;0rad)
  Tip = -> Pad111
FEATURE [Sketcher::SketchObject] Sketch170
  FullyConstrained = false
  MapMode = 5
  Support = -> [XY_Plane116]
  sketch-geometry (2):
    g0: Circle CenterX=0 CenterY=0 CenterZ=0 NormalX=0 NormalY=0 NormalZ=1 AngleXU=0 Radius=5.85
    g1: Circle CenterX=0 CenterY=0 CenterZ=0 NormalX=0 NormalY=0 NormalZ=1 AngleXU=0 Radius=3
  constraints (4):
    c: Coincident(g1,g0)
    c: Coincident(g1,g-1)
    c: Diameter(g1) = 6
    c: Diameter(g0) = 11.7
FEATURE [PartDesign::Pad] Pad112
  AllowMultiFace = false
  Direction = (1,1,1)
  Length = 1.5
  Length2 = 100
  Profile = -> Sketch170
  Type = 0
FEATURE [PartDesign::Body] Body090  label="M6_Washer007"
  Group = -> [Sketch170,Pad112]
  Origin = -> Origin116
  Placement = pos=(0,0,73) rot=(0,0,1;0rad)
  Tip = -> Pad112
FEATURE [Sketcher::SketchObject] Sketch171
  FullyConstrained = false
  MapMode = 5
  Support = -> [XY_Plane117]
  sketch-geometry (8):
    g0: LineSegment StartX=0 StartY=5.7735 StartZ=0 EndX=-5 EndY=2.88675 EndZ=0
    g1: LineSegment StartX=-5 StartY=2.88675 StartZ=0 EndX=-5 EndY=-2.88675 EndZ=0
    g2: LineSegment StartX=-5 StartY=-2.88675 StartZ=0 EndX=-1.501e-13 EndY=-5.7735 EndZ=0
    g3: LineSegment StartX=-1.501e-13 StartY=-5.7735 StartZ=0 EndX=5 EndY=-2.88675 EndZ=0
    g4: LineSegment StartX=5 StartY=-2.88675 StartZ=0 EndX=5 EndY=2.88675 EndZ=0
    g5: LineSegment StartX=5 StartY=2.88675 StartZ=0 EndX=0 EndY=5.7735 EndZ=0
    g6: Circle CenterX=0 CenterY=0 CenterZ=0 NormalX=0 NormalY=0 NormalZ=1 AngleXU=0 Radius=5.7735
    g7: Circle CenterX=0 CenterY=0 CenterZ=0 NormalX=0 NormalY=0 NormalZ=1 AngleXU=0 Radius=3
  constraints (18):
    c: Coincident(g0,g1)
    c: Coincident(g1,g2)
    c: Coincident(g2,g3)
    c: Coincident(g3,g4)
    c: Coincident(g4,g5)
    c: Coincident(g5,g0)
    c: Equal(g0, g1-g5) x5
    c: PointOnObject(g0,g6)
    c: PointOnObject(g1,g6)
    c: PointOnObject(g2,g6)
    c: PointOnObject(g3,g6)
    c: PointOnObject(g4,g6)
    c: PointOnObject(g5,g6)
    c: Coincident(g6,g-1)
    c: PointOnObject(g0,g-2)
    c: Distance(g0,g4) = 10
    c: Coincident(g7,g-1)
    c: Diameter(g7) = 6
FEATURE [PartDesign::Pad] Pad113
  AllowMultiFace = false
  Direction = (1,1,1)
  Length = 5
  Length2 = 100
  Profile = -> Sketch171
  Type = 0
FEATURE [PartDesign::Body] Body091  label="M6_Full_Nut007"
  Group = -> [Sketch171,Pad113]
  Origin = -> Origin117
  Placement = pos=(0,0,74.5) rot=(0,0,1;0rad)
  Tip = -> Pad113
FEATURE [Sketcher::SketchObject] Sketch172
  FullyConstrained = false
  MapMode = 5
  Support = -> [XY_Plane118]
  sketch-geometry (2):
    g0: Circle CenterX=0 CenterY=0 CenterZ=0 NormalX=0 NormalY=0 NormalZ=1 AngleXU=0 Radius=9.5
    g1: Circle CenterX=0 CenterY=0 CenterZ=0 NormalX=0 NormalY=0 NormalZ=1 AngleXU=0 Radius=3
  constraints (4):
    c: Coincident(g0,g-1)
    c: Coincident(g0,g1)
    c: Diameter(g1) = 6
    c: Diameter(g0) = 19
FEATURE [PartDesign::Pad] Pad114
  AllowMultiFace = false
  Direction = (1,1,1)
  Length = 6
  Length2 = 100
  Profile = -> Sketch172
  Type = 0
FEATURE [PartDesign::Body] Body092  label="6mm_bearing004"
  Group = -> [Sketch172,Pad114]
  Origin = -> Origin118
  Placement = pos=(0,0,81) rot=(0,0,1;0rad)
  Tip = -> Pad114
FEATURE [Sketcher::SketchObject] Sketch173
  FullyConstrained = false
  MapMode = 5
  Support = -> [XY_Plane119]
  sketch-geometry (2):
    g0: Circle CenterX=0 CenterY=0 CenterZ=0 NormalX=0 NormalY=0 NormalZ=1 AngleXU=0 Radius=5.85
    g1: Circle CenterX=0 CenterY=0 CenterZ=0 NormalX=0 NormalY=0 NormalZ=1 AngleXU=0 Radius=3
  constraints (4):
    c: Coincident(g1,g0)
    c: Coincident(g1,g-1)
    c: Diameter(g1) = 6
    c: Diameter(g0) = 11.7
FEATURE [PartDesign::Pad] Pad115
  AllowMultiFace = false
  Direction = (1,1,1)
  Length = 1.5
  Length2 = 100
  Profile = -> Sketch173
  Type = 0
FEATURE [PartDesign::Body] Body093  label="M6_Washer008"
  Group = -> [Sketch173,Pad115]
  Origin = -> Origin119
  Placement = pos=(0,0,79.5) rot=(0,0,1;0rad)
  Tip = -> Pad115
FEATURE [Sketcher::SketchObject] Sketch174
  FullyConstrained = false
  MapMode = 5
  Support = -> [XY_Plane120]
  sketch-geometry (2):
    g0: Circle CenterX=0 CenterY=0 CenterZ=0 NormalX=0 NormalY=0 NormalZ=1 AngleXU=0 Radius=9.5
    g1: Circle CenterX=0 CenterY=0 CenterZ=0 NormalX=0 NormalY=0 NormalZ=1 AngleXU=0 Radius=3
  constraints (4):
    c: Coincident(g0,g-1)
    c: Coincident(g0,g1)
    c: Diameter(g1) = 6
    c: Diameter(g0) = 19
FEATURE [PartDesign::Pad] Pad116
  AllowMultiFace = false
  Direction = (1,1,1)
  Length = 6
  Length2 = 100
  Profile = -> Sketch174
  Type = 0
FEATURE [PartDesign::Body] Body094  label="6mm_bearing005"
  Group = -> [Sketch174,Pad116]
  Origin = -> Origin120
  Placement = pos=(0,0,115) rot=(0,0,1;0rad)
  Tip = -> Pad116
FEATURE [Sketcher::SketchObject] Sketch175
  FullyConstrained = false
  MapMode = 5
  Support = -> [XY_Plane121]
  sketch-geometry (2):
    g0: Circle CenterX=0 CenterY=0 CenterZ=0 NormalX=0 NormalY=0 NormalZ=1 AngleXU=0 Radius=5.85
    g1: Circle CenterX=0 CenterY=0 CenterZ=0 NormalX=0 NormalY=0 NormalZ=1 AngleXU=0 Radius=3
  constraints (4):
    c: Coincident(g1,g0)
    c: Coincident(g1,g-1)
    c: Diameter(g1) = 6
    c: Diameter(g0) = 11.7
FEATURE [PartDesign::Pad] Pad117
  AllowMultiFace = false
  Direction = (1,1,1)
  Length = 1.5
  Length2 = 100
  Profile = -> Sketch175
  Type = 0
FEATURE [PartDesign::Body] Body095  label="M6_Washer009"
  Group = -> [Sketch175,Pad117]
  Origin = -> Origin121
  Placement = pos=(0,0,121) rot=(0,0,1;0rad)
  Tip = -> Pad117
FEATURE [Sketcher::SketchObject] Sketch176
  FullyConstrained = false
  MapMode = 5
  Support = -> [XY_Plane122]
  sketch-geometry (8):
    g0: LineSegment StartX=0 StartY=5.7735 StartZ=0 EndX=-5 EndY=2.88675 EndZ=0
    g1: LineSegment StartX=-5 StartY=2.88675 StartZ=0 EndX=-5 EndY=-2.88675 EndZ=0
    g2: LineSegment StartX=-5 StartY=-2.88675 StartZ=0 EndX=-1.501e-13 EndY=-5.7735 EndZ=0
    g3: LineSegment StartX=-1.501e-13 StartY=-5.7735 StartZ=0 EndX=5 EndY=-2.88675 EndZ=0
    g4: LineSegment StartX=5 StartY=-2.88675 StartZ=0 EndX=5 EndY=2.88675 EndZ=0
    g5: LineSegment StartX=5 StartY=2.88675 StartZ=0 EndX=0 EndY=5.7735 EndZ=0
    g6: Circle CenterX=0 CenterY=0 CenterZ=0 NormalX=0 NormalY=0 NormalZ=1 AngleXU=0 Radius=5.7735
    g7: Circle CenterX=0 CenterY=0 CenterZ=0 NormalX=0 NormalY=0 NormalZ=1 AngleXU=0 Radius=3
  constraints (18):
    c: Coincident(g0,g1)
    c: Coincident(g1,g2)
    c: Coincident(g2,g3)
    c: Coincident(g3,g4)
    c: Coincident(g4,g5)
    c: Coincident(g5,g0)
    c: Equal(g0, g1-g5) x5
    c: PointOnObject(g0,g6)
    c: PointOnObject(g1,g6)
    c: PointOnObject(g2,g6)
    c: PointOnObject(g3,g6)
    c: PointOnObject(g4,g6)
    c: PointOnObject(g5,g6)
    c: Coincident(g6,g-1)
    c: PointOnObject(g0,g-2)
    c: Distance(g0,g4) = 10
    c: Coincident(g7,g-1)
    c: Diameter(g7) = 6
FEATURE [PartDesign::Pad] Pad118
  AllowMultiFace = false
  Direction = (1,1,1)
  Length = 5
  Length2 = 100
  Profile = -> Sketch176
  Type = 0
FEATURE [PartDesign::Body] Body096  label="M6_Full_Nut008"
  Group = -> [Sketch176,Pad118]
  Origin = -> Origin122
  Placement = pos=(0,0,122.5) rot=(0,0,1;0rad)
  Tip = -> Pad118
FEATURE [Sketcher::SketchObject] Sketch177
  FullyConstrained = false
  MapMode = 5
  Support = -> [XY_Plane124]
  sketch-geometry (1):
    g0: Circle CenterX=0 CenterY=0 CenterZ=0 NormalX=0 NormalY=0 NormalZ=1 AngleXU=0 Radius=41.6542
  constraints (1):
    c: Coincident(g0,g-1)
FEATURE [PartDesign::Body] Body097
  Group = -> [Sketch177]
  Origin = -> Origin124
FEATURE [App::Part] Part012  label="wheel002"
  Group = -> [Body087,Body088,Body085,Body086,Body084,Body089,Body092,Body094,Body090,Body091,Body093,Body095,Body096,Body097]
  Origin = -> Origin123
  Placement = pos=(-100,-72,0) rot=(0,0,1;3.14159rad)
FEATURE [Sketcher::SketchObject] Sketch178
  FullyConstrained = false
  MapMode = 5
  Placement = pos=(0,0,0) rot=(0.57735,0.57735,0.57735;2.0944rad)
  Support = -> [YZ_Plane125]
  sketch-geometry (17):
    g0: LineSegment StartX=16 StartY=28.5 StartZ=0 EndX=16 EndY=26 EndZ=0
    g1: LineSegment StartX=16 StartY=26 StartZ=0 EndX=-16 EndY=26 EndZ=0
    g2: LineSegment StartX=-16 StartY=26 StartZ=0 EndX=-16 EndY=28.5 EndZ=0
    g3: LineSegment StartX=-16 StartY=28.5 StartZ=0 EndX=-17.5 EndY=28.5 EndZ=0
    g4: LineSegment StartX=-17.5 StartY=28.5 StartZ=0 EndX=-17.5 EndY=30 EndZ=0
    g5: LineSegment StartX=-17.5 StartY=30 StartZ=0 EndX=-17.85 EndY=30 EndZ=0
    g6: LineSegment StartX=-19.85 StartY=32 StartZ=0 EndX=-19.85 EndY=35.5078 EndZ=0
    g7: LineSegment StartX=19.85 StartY=35.5078 StartZ=0 EndX=19.85 EndY=32 EndZ=0
    g8: LineSegment StartX=17.85 StartY=30 StartZ=0 EndX=17.5 EndY=30 EndZ=0
    g9: LineSegment StartX=17.5 StartY=30 StartZ=0 EndX=17.5 EndY=28.5 EndZ=0
    g10: LineSegment StartX=17.5 StartY=28.5 StartZ=0 EndX=16 EndY=28.5 EndZ=0
    g11: ArcOfCircle CenterX=5.199e-13 CenterY=-27.17 CenterZ=0 NormalX=0 NormalY=0 NormalZ=1 AngleXU=0 Radius=67.17 StartAngle=1.5708 EndAngle=1.84824
    g12: ArcOfCircle CenterX=5.199e-13 CenterY=-27.17 CenterZ=0 NormalX=0 NormalY=0 NormalZ=1 AngleXU=0 Radius=67.17 StartAngle=1.29335 EndAngle=1.5708
    g13: ArcOfCircle CenterX=-17.85 CenterY=32 CenterZ=0 NormalX=0 NormalY=0 NormalZ=1 AngleXU=0 Radius=2 StartAngle=3.14159 EndAngle=4.71239
    g14: ArcOfCircle CenterX=17.85 CenterY=32 CenterZ=0 NormalX=0 NormalY=0 NormalZ=1 AngleXU=0 Radius=2 StartAngle=4.71239 EndAngle=6.28319
    g15: ArcOfCircle CenterX=-17.85 CenterY=35.5078 CenterZ=0 NormalX=0 NormalY=0 NormalZ=1 AngleXU=0 Radius=2 StartAngle=1.84824 EndAngle=3.14159
    g16: ArcOfCircle CenterX=17.85 CenterY=35.5078 CenterZ=0 NormalX=0 NormalY=0 NormalZ=1 AngleXU=0 Radius=2 StartAngle=-9e-16 EndAngle=1.29335
  constraints (44):
    c: Coincident(g0,g1)
    c: Coincident(g1,g2)
    c: Coincident(g2,g3)
    c: Coincident(g3,g4)
    c: Coincident(g4,g5)
    c: Coincident(g8,g9)
    c: Coincident(g9,g10)
    c: Coincident(g10,g0)
    c: Vertical(g0)
    c: Vertical(g9)
    c: Vertical(g7)
    c: Horizontal(g8)
    c: Horizontal(g10)
    c: Horizontal(g1)
    c: Vertical(g2)
    c: Horizontal(g3)
    c: Horizontal(g5)
    c: Symmetric(g4,g8,g-2)
    c: DistanceX(g4,g8) = 35
    c: Equal(g3,g10)
    c: DistanceX(g10,g10) = 1.5
    c: DistanceY(g-1,g1) = 26
    c: DistanceY(g-1,g3) = 28.5
    c: DistanceY(g-1,g4) = 30
    c: Symmetric(g2,g0,g-2)
    c: Tangent(g11,g12) = -1.5708
    c: PointOnObject(g11,g-2)
    c: Coincident(g12,g11)
    c: DistanceY(g-1,g11) = 40
    c: Tangent(g5,g13) = 1.5708
    c: Tangent(g6,g13) = 1.5708
    c: Tangent(g7,g14) = 1.5708
    c: Tangent(g8,g14) = 1.5708
    c: Radius(g14) = 2
    c: DistanceX(g6,g7) = 39.7
    c: DistanceY(g11,g-1) = 27.17
    c: Tangent(g11,g15) = -1.5708
    c: Tangent(g6,g15) = 1.5708
    c: Tangent(g12,g16) = -1.5708
    c: Tangent(g7,g16) = 1.5708
    c: Symmetric(g6,g7,g-2)
    c: Equal(g16,g15)
    c: Radius(g16) = 2
    c: Symmetric(g6,g7,g-2)
FEATURE [PartDesign::Revolution] Revolution010
  AllowMultiFace = false
  Angle = 360
  Axis = (3e-16,1,-2e-16)
  Base = (0,0,0)
  Placement = pos=(0,0,0) rot=(0.57735,0.57735,0.57735;2.0944rad)
  Profile = -> Sketch178
  ReferenceAxis = -> Sketch178 [H_Axis]
FEATURE [PartDesign::Plane] DatumPlane003
  AttachmentOffset = pos=(0,0,7) rot=(0,0,1;0rad)
  Length = 95.8516
  MapMode = 4
  Placement = pos=(0,7,0) rot=(0.57735,0.57735,0.57735;4.18879rad)
  ResizeMode = 0
  Support = -> [Revolution010]
  Width = 95.8986
FEATURE [Sketcher::SketchObject] Sketch179
  FullyConstrained = false
  MapMode = 5
  Placement = pos=(0,7,0) rot=(0.57735,0.57735,0.57735;4.18879rad)
  Support = -> [DatumPlane003]
  sketch-geometry (26):
    g0: LineSegment StartX=7 StartY=-18.2003 StartZ=0 EndX=19.4726 EndY=1.0332 EndZ=0
    g1: LineSegment StartX=19.4726 StartY=1.0332 StartZ=0 EndX=5.03473 EndY=18.8388 EndZ=0
    g2: LineSegment StartX=5.03473 StartY=18.8388 StartZ=0 EndX=-16.361 EndY=10.6098 EndZ=0
    g3: LineSegment StartX=-16.361 StartY=10.6098 StartZ=0 EndX=-15.1464 EndY=-12.2816 EndZ=0
    g4: LineSegment StartX=-15.1464 StartY=-12.2816 StartZ=0 EndX=7 EndY=-18.2003 EndZ=0
    g5: Circle CenterX=0 CenterY=0 CenterZ=0 NormalX=0 NormalY=0 NormalZ=1 AngleXU=0 Radius=19.5
    g6: ArcOfCircle CenterX=0 CenterY=0 CenterZ=0 NormalX=0 NormalY=0 NormalZ=1 AngleXU=0 Radius=19.5 StartAngle=5.60186 EndAngle=6.33619
    g7: ArcOfCircle CenterX=0 CenterY=0 CenterZ=0 NormalX=0 NormalY=0 NormalZ=1 AngleXU=0 Radius=19.5 StartAngle=4.34522 EndAngle=5.07956
    g8: ArcOfCircle CenterX=0 CenterY=0 CenterZ=0 NormalX=0 NormalY=0 NormalZ=1 AngleXU=0 Radius=19.5 StartAngle=3.08858 EndAngle=3.82292
    g9: ArcOfCircle CenterX=0 CenterY=0 CenterZ=0 NormalX=0 NormalY=0 NormalZ=1 AngleXU=0 Radius=19.5 StartAngle=1.83195 EndAngle=2.56628
    g10: ArcOfCircle CenterX=0 CenterY=0 CenterZ=0 NormalX=0 NormalY=0 NormalZ=1 AngleXU=0 Radius=19.5 StartAngle=0.575309 EndAngle=1.30965
    g11: ArcOfCircle CenterX=17.7078 CenterY=24.3726 CenterZ=0 NormalX=0 NormalY=0 NormalZ=1 AngleXU=0 Radius=13.8285 StartAngle=3.00933 EndAngle=3.5533
    g12: ArcOfCircle CenterX=17.7078 CenterY=24.3726 CenterZ=0 NormalX=0 NormalY=0 NormalZ=1 AngleXU=0 Radius=13.8285 StartAngle=4.61484 EndAngle=5.15882
    g13: ArcOfCircle CenterX=0 CenterY=0 CenterZ=0 NormalX=0 NormalY=0 NormalZ=1 AngleXU=0 Radius=26.5 StartAngle=0.162637 EndAngle=0.465682
    g14: ArcOfCircle CenterX=0 CenterY=0 CenterZ=0 NormalX=0 NormalY=0 NormalZ=1 AngleXU=0 Radius=26.5 StartAngle=1.41927 EndAngle=1.72232
    g15: ArcOfCircle CenterX=-17.7078 CenterY=24.3726 CenterZ=0 NormalX=0 NormalY=0 NormalZ=1 AngleXU=0 Radius=13.8285 StartAngle=5.87148 EndAngle=6.41545
    g16: ArcOfCircle CenterX=-17.7078 CenterY=24.3726 CenterZ=0 NormalX=0 NormalY=0 NormalZ=1 AngleXU=0 Radius=13.8285 StartAngle=4.26596 EndAngle=4.80994
    g17: ArcOfCircle CenterX=-28.6518 CenterY=-9.30952 CenterZ=0 NormalX=0 NormalY=0 NormalZ=1 AngleXU=0 Radius=13.8285 StartAngle=0.844931 EndAngle=1.3889
    g18: ArcOfCircle CenterX=-28.6518 CenterY=-9.30952 CenterZ=0 NormalX=0 NormalY=0 NormalZ=1 AngleXU=0 Radius=13.8285 StartAngle=5.5226 EndAngle=6.06657
    g19: ArcOfCircle CenterX=3.8e-15 CenterY=-30.1262 CenterZ=0 NormalX=0 NormalY=0 NormalZ=1 AngleXU=0 Radius=13.8285 StartAngle=2.10157 EndAngle=2.64554
    g20: ArcOfCircle CenterX=3.8e-15 CenterY=-30.1262 CenterZ=0 NormalX=0 NormalY=0 NormalZ=1 AngleXU=0 Radius=13.8285 StartAngle=0.496052 EndAngle=1.04002
    g21: ArcOfCircle CenterX=28.6518 CenterY=-9.30952 CenterZ=0 NormalX=0 NormalY=0 NormalZ=1 AngleXU=0 Radius=13.8285 StartAngle=3.35821 EndAngle=3.90218
    g22: ArcOfCircle CenterX=28.6518 CenterY=-9.30952 CenterZ=0 NormalX=0 NormalY=0 NormalZ=1 AngleXU=0 Radius=13.8285 StartAngle=1.75269 EndAngle=2.29666
    g23: ArcOfCircle CenterX=0 CenterY=0 CenterZ=0 NormalX=0 NormalY=0 NormalZ=1 AngleXU=0 Radius=26.5 StartAngle=2.67591 EndAngle=2.97896
    g24: ArcOfCircle CenterX=0 CenterY=0 CenterZ=0 NormalX=0 NormalY=0 NormalZ=1 AngleXU=0 Radius=26.5 StartAngle=3.93255 EndAngle=4.23559
    g25: ArcOfCircle CenterX=0 CenterY=0 CenterZ=0 NormalX=0 NormalY=0 NormalZ=1 AngleXU=0 Radius=26.5 StartAngle=5.18918 EndAngle=5.49223
  constraints (74):
    c: Coincident(g0,g1)
    c: Coincident(g1,g2)
    c: Coincident(g2,g3)
    c: Coincident(g3,g4)
    c: Coincident(g4,g0)
    c: Equal(g0, g1-g4) x4
    c: PointOnObject(g0,g5)
    c: PointOnObject(g1,g5)
    c: PointOnObject(g2,g5)
    c: PointOnObject(g3,g5)
    c: PointOnObject(g4,g5)
    c: Coincident(g5,g-1)
    c: Coincident(g10,g6)
    c: Coincident(g10,g7)
    c: Coincident(g10,g8)
    c: Coincident(g10,g9)
    c: Coincident(g10,g-1)
    c: Coincident(g10,g1)
    c: Coincident(g6,g0)
    c: Coincident(g7,g0)
    c: Coincident(g8,g3)
    c: Coincident(g9,g2)
    c: Distance(g8,g8) = 14
    c: Distance(g9,g9) = 14
    c: Distance(g10,g10) = 14
    c: Distance(g6,g6) = 14
    c: Distance(g7,g7) = 14
    c: Diameter(g5) = 39
    c: DistanceX(g-2,g7) = -7
    c: Coincident(g11,g10)
    c: Coincident(g12,g10)
    c: Coincident(g12,g11)
    c: Coincident(g14,g13)
    c: Coincident(g14,g6)
    c: Coincident(g14,g11)
    c: Coincident(g13,g12)
    c: Equal(g14,g13)
    c: Diameter(g14) = 53
    c: Equal(g12,g11)
    c: Coincident(g15,g16)
    c: Coincident(g15,g14)
    c: Coincident(g15,g9)
    c: Coincident(g16,g9)
    c: Coincident(g17,g8)
    c: Coincident(g17,g18)
    c: Coincident(g18,g8)
    c: Equal(g18,g17)
    c: Equal(g17,g16)
    c: Equal(g16,g15)
    c: Equal(g15,g11)
    c: Coincident(g22,g21)
    c: Coincident(g20,g19)
    c: Coincident(g19,g7)
    c: Coincident(g20,g7)
    c: Coincident(g21,g6)
    c: Coincident(g22,g6)
    c: Coincident(g22,g13)
    c: Equal(g19,g20)
    c: Equal(g20,g21)
    c: Equal(g21,g22)
    c: Equal(g22,g12)
    c: Coincident(g25,g23)
    c: Coincident(g25,g24)
    c: Coincident(g25,g6)
    c: Coincident(g20,g25)
    c: Coincident(g21,g25)
    c: Coincident(g24,g19)
    c: Coincident(g24,g18)
    c: Coincident(g23,g17)
    c: Coincident(g23,g16)
    c: Equal(g23,g24)
    c: Equal(g24,g25)
    c: Equal(g25,g13)
    c: Distance(g16,g17) = 8
FEATURE [PartDesign::Pad] Pad119
  AllowMultiFace = false
  BaseFeature = -> Revolution010
  Direction = (1,1,1)
  Length = 2
  Length2 = 100
  Placement = pos=(0,0,0) rot=(0.57735,0.57735,0.57735;2.0944rad)
  Profile = -> Sketch179
  Type = 0
FEATURE [Sketcher::SketchObject] Sketch180
  FullyConstrained = false
  MapMode = 5
  Placement = pos=(0,7,0) rot=(0.57735,0.57735,-0.57735;2.0944rad)
  Support = -> [Pad119]
  sketch-geometry (1):
    g0: Circle CenterX=0 CenterY=0 CenterZ=0 NormalX=0 NormalY=0 NormalZ=1 AngleXU=0 Radius=8.5
  constraints (2):
    c: Coincident(g0,g-1)
    c: Diameter(g0) = 17
FEATURE [Sketcher::SketchObject] Sketch182
  FullyConstrained = false
  MapMode = 5
  Placement = pos=(0,0,0) rot=(0.57735,0.57735,0.57735;2.0944rad)
  Support = -> [YZ_Plane125]
  sketch-geometry (9):
    g0: LineSegment StartX=9 StartY=-2 StartZ=0 EndX=9 EndY=-19.5 EndZ=0
    g1: LineSegment StartX=9 StartY=-19.5 StartZ=0 EndX=9.5 EndY=-19.5 EndZ=0
    g2: LineSegment StartX=9.5 StartY=-19.5 StartZ=0 EndX=12 EndY=-12.5 EndZ=0
    g3: LineSegment StartX=12 StartY=-12.5 StartZ=0 EndX=11 EndY=-7 EndZ=0
    g4: LineSegment StartX=11 StartY=-7 StartZ=0 EndX=14 EndY=-7 EndZ=0
    g5: LineSegment StartX=14 StartY=-7 StartZ=0 EndX=14 EndY=-5 EndZ=0
    g6: LineSegment StartX=14 StartY=-5 StartZ=0 EndX=12 EndY=-5 EndZ=0
    g7: LineSegment StartX=12 StartY=-5 StartZ=0 EndX=12 EndY=-2 EndZ=0
    g8: LineSegment StartX=12 StartY=-2 StartZ=0 EndX=9 EndY=-2 EndZ=0
  constraints (27):
    c: Coincident(g0,g1)
    c: Coincident(g1,g2)
    c: Coincident(g2,g3)
    c: Coincident(g3,g4)
    c: Coincident(g4,g5)
    c: Coincident(g5,g6)
    c: Coincident(g6,g7)
    c: Coincident(g7,g8)
    c: Coincident(g0,g8)
    c: Vertical(g0)
    c: DistanceX(g-1,g0) = 9
    c: DistanceY(g0,g-1) = 19.5
    c: Horizontal(g1)
    c: DistanceY(g0,g-1) = 2
    c: Horizontal(g8)
    c: Vertical(g7)
    c: DistanceX(g8,g8) = 3
    c: Horizontal(g6)
    c: DistanceX(g6,g6) = 2
    c: DistanceY(g5,g-1) = 5
    c: DistanceY(g4,g-1) = 7
    c: Vertical(g5)
    c: DistanceX(g0,g2) = 3
    c: DistanceX(g1,g1) = 0.5
    c: Horizontal(g4)
    c: DistanceX(g4,g4) = 3
    c: DistanceY(g2,g-1) = 12.5
FEATURE [PartDesign::Revolution] Revolution011
  AllowMultiFace = false
  Angle = 360
  Axis = (3e-16,1,-2e-16)
  Base = (0,0,0)
  BaseFeature = -> Pad119
  Placement = pos=(0,0,0) rot=(0.57735,0.57735,0.57735;2.0944rad)
  Profile = -> Sketch182
  ReferenceAxis = -> Sketch182 [H_Axis]
  Reversed = true
FEATURE [Sketcher::SketchObject] Sketch183
  FullyConstrained = false
  MapMode = 5
  Support = -> [XY_Plane125]
  sketch-geometry (3):
    g0: LineSegment StartX=7.5 StartY=7 StartZ=0 EndX=17.5 EndY=7 EndZ=0
    g1: LineSegment StartX=17.5 StartY=7 StartZ=0 EndX=12.5 EndY=10 EndZ=0
    g2: LineSegment StartX=12.5 StartY=10 StartZ=0 EndX=7.5 EndY=7 EndZ=0
  constraints (9):
    c: Coincident(g0,g1)
    c: Coincident(g1,g2)
    c: Coincident(g0,g2)
    c: DistanceY(g-1,g0) = 7
    c: Horizontal(g0)
    c: DistanceY(g0,g1) = 3
    c: DistanceX(g-1,g0) = 17.5
    c: DistanceX(g-1,g1) = 12.5
    c: DistanceX(g-1,g0) = 7.5
FEATURE [PartDesign::Groove] Groove003
  AllowMultiFace = false
  Angle = 360
  Axis = (0,1,0)
  Base = (0,0,0)
  BaseFeature = -> Revolution011
  Placement = pos=(0,0,0) rot=(0.57735,0.57735,0.57735;2.0944rad)
  Profile = -> Sketch183
  ReferenceAxis = -> Sketch183 [V_Axis]
FEATURE [PartDesign::Pad] Pad120
  AllowMultiFace = false
  BaseFeature = -> Groove003
  Direction = (1,1,1)
  Length = 1.5
  Length2 = 100
  Placement = pos=(0,0,0) rot=(0.57735,0.57735,0.57735;2.0944rad)
  Profile = -> Sketch180
  Type = 0
FEATURE [Sketcher::SketchObject] Sketch181
  FullyConstrained = false
  MapMode = 5
  Placement = pos=(0,5.5,0) rot=(0.57735,0.57735,-0.57735;2.0944rad)
  Support = -> [Pad120]
  sketch-geometry (7):
    g0: LineSegment StartX=6 StartY=-3.4641 StartZ=0 EndX=6 EndY=3.4641 EndZ=0
    g1: LineSegment StartX=6 StartY=3.4641 StartZ=0 EndX=9e-16 EndY=6.9282 EndZ=0
    g2: LineSegment StartX=9e-16 StartY=6.9282 StartZ=0 EndX=-6 EndY=3.4641 EndZ=0
    g3: LineSegment StartX=-6 StartY=3.4641 StartZ=0 EndX=-6 EndY=-3.4641 EndZ=0
    g4: LineSegment StartX=-6 StartY=-3.4641 StartZ=0 EndX=0 EndY=-6.9282 EndZ=0
    g5: LineSegment StartX=0 StartY=-6.9282 StartZ=0 EndX=6 EndY=-3.4641 EndZ=0
    g6: Circle CenterX=0 CenterY=0 CenterZ=0 NormalX=0 NormalY=0 NormalZ=1 AngleXU=0 Radius=6.9282
  constraints (16):
    c: Coincident(g0,g1)
    c: Coincident(g1,g2)
    c: Coincident(g2,g3)
    c: Coincident(g3,g4)
    c: Coincident(g4,g5)
    c: Coincident(g5,g0)
    c: Equal(g0, g1-g5) x5
    c: PointOnObject(g0,g6)
    c: PointOnObject(g1,g6)
    c: PointOnObject(g2,g6)
    c: PointOnObject(g3,g6)
    c: PointOnObject(g4,g6)
    c: PointOnObject(g5,g6)
    c: Coincident(g6,g-1)
    c: Vertical(g3)
    c: DistanceX(g2,g0) = 12
FEATURE [Sketcher::SketchObject] Sketch184
  FullyConstrained = false
  MapMode = 5
  Support = -> [XY_Plane125]
  sketch-geometry (6):
    g0: LineSegment StartX=26.5 StartY=-6 StartZ=0 EndX=26.5 EndY=8 EndZ=0
    g1: LineSegment StartX=26.5 StartY=8 StartZ=0 EndX=17.5 EndY=8 EndZ=0
    g2: LineSegment StartX=17.5 StartY=8 StartZ=0 EndX=12.5 EndY=12 EndZ=0
    g3: LineSegment StartX=12.5 StartY=12 StartZ=0 EndX=6.25 EndY=14 EndZ=0
    g4: LineSegment StartX=6.25 StartY=14 StartZ=0 EndX=6.25 EndY=6 EndZ=0
    g5: ArcOfCircle CenterX=7.23279 CenterY=-15.4275 CenterZ=0 NormalX=0 NormalY=0 NormalZ=1 AngleXU=0 Radius=21.45 StartAngle=0.455052 EndAngle=1.61663
  constraints (19):
    c: Coincident(g0,g1)
    c: Coincident(g1,g2)
    c: Coincident(g2,g3)
    c: Coincident(g3,g4)
    c: Horizontal(g1)
    c: Vertical(g0)
    c: Vertical(g4)
    c: Coincident(g5,g0)
    c: Coincident(g5,g4)
    c: Diameter(g5) = 42.9
    c: DistanceY(g0,g0) = 14
    c: DistanceY(g4,g4) = 8
    c: DistanceY(g0,g-1) = 6
    c: DistanceX(g-1,g2) = 12.5
    c: DistanceX(g-1,g3) = 6.25
    c: DistanceX(g-1,g1) = 17.5
    c: DistanceX(g-1,g0) = 26.5
    c: DistanceY(g-1,g4) = 6
    c: DistanceY(g2,g3) = 2
FEATURE [PartDesign::Pad] Pad121
  AllowMultiFace = false
  BaseFeature = -> Pad120
  Direction = (1,1,1)
  Length = 1.5
  Length2 = 100
  Midplane = true
  Placement = pos=(0,0,0) rot=(0.57735,0.57735,0.57735;2.0944rad)
  Profile = -> Sketch184
  Type = 0
FEATURE [PartDesign::PolarPattern] PolarPattern003
  Angle = 360
  Axis = -> Y_Axis125
  BaseFeature = -> Pad121
  Occurrences = 5
  Originals = -> [Pad121]
  Placement = pos=(0,0,0) rot=(0.57735,0.57735,0.57735;2.0944rad)
FEATURE [PartDesign::Pocket] Pocket045
  AllowMultiFace = false
  BaseFeature = -> PolarPattern003
  Length = 4.8
  Length2 = 100
  Placement = pos=(0,0,0) rot=(0.57735,0.57735,0.57735;2.0944rad)
  Profile = -> Sketch181
  Type = 0
FEATURE [PartDesign::Body] Body101  label="Wheel003"
  Group = -> [Sketch178,Revolution010,DatumPlane003,Sketch179,Pad119,Sketch180,Sketch181,Sketch182,Sketch183,Revolution011,Groove003,Pad120,Pad121,PolarPattern003,Pocket045,Sketch184]
  Origin = -> Origin126
  Tip = -> Pad119
FEATURE [Sketcher::SketchObject] Sketch185
  FullyConstrained = false
  MapMode = 5
  Support = -> [XY_Plane126]
  sketch-geometry (7):
    g0: LineSegment StartX=6 StartY=3.4641 StartZ=0 EndX=3.87264e-11 EndY=6.9282 EndZ=0
    g1: LineSegment StartX=3.8726e-11 StartY=6.9282 StartZ=0 EndX=-6 EndY=3.4641 EndZ=0
    g2: LineSegment StartX=-6 StartY=3.4641 StartZ=0 EndX=-6 EndY=-3.4641 EndZ=0
    g3: LineSegment StartX=-6 StartY=-3.4641 StartZ=0 EndX=1.74527e-11 EndY=-6.9282 EndZ=0
    g4: LineSegment StartX=1.74523e-11 StartY=-6.9282 StartZ=0 EndX=6 EndY=-3.4641 EndZ=0
    g5: LineSegment StartX=6 StartY=-3.4641 StartZ=0 EndX=6 EndY=3.4641 EndZ=0
    g6: Circle CenterX=0 CenterY=0 CenterZ=0 NormalX=0 NormalY=0 NormalZ=1 AngleXU=0 Radius=6.9282
  constraints (16):
    c: Coincident(g0,g1)
    c: Coincident(g1,g2)
    c: Coincident(g2,g3)
    c: Coincident(g3,g4)
    c: Coincident(g4,g5)
    c: Coincident(g5,g0)
    c: Equal(g0, g1-g5) x5
    c: PointOnObject(g0,g6)
    c: PointOnObject(g1,g6)
    c: PointOnObject(g2,g6)
    c: PointOnObject(g3,g6)
    c: PointOnObject(g4,g6)
    c: PointOnObject(g5,g6)
    c: Coincident(g6,g-1)
    c: Vertical(g5)
    c: DistanceX(g1,g0) = 12
FEATURE [PartDesign::Pad] Pad122
  AllowMultiFace = false
  Direction = (1,1,1)
  Length = 6
  Length2 = 100
  Profile = -> Sketch185
  Type = 0
FEATURE [Sketcher::SketchObject] Sketch186
  FullyConstrained = false
  MapMode = 5
  Placement = pos=(0,0,6) rot=(0,0,1;0rad)
  Support = -> [Pad122]
  sketch-geometry (1):
    g0: Circle CenterX=0 CenterY=0 CenterZ=0 NormalX=0 NormalY=0 NormalZ=1 AngleXU=0 Radius=6
  constraints (2):
    c: Coincident(g0,g-1)
    c: Diameter(g0) = 12
FEATURE [PartDesign::Pad] Pad123
  AllowMultiFace = false
  BaseFeature = -> Pad122
  Direction = (1,1,1)
  Length = 24
  Length2 = 100
  Profile = -> Sketch186
  Type = 0
FEATURE [Sketcher::SketchObject] Sketch187
  FullyConstrained = false
  MapMode = 5
  Placement = pos=(0,0,30) rot=(0,0,1;0rad)
  Support = -> [Pad123]
  sketch-geometry (1):
    g0: Circle CenterX=0 CenterY=0 CenterZ=0 NormalX=0 NormalY=0 NormalZ=1 AngleXU=0 Radius=3
  constraints (2):
    c: Coincident(g0,g-1)
    c: Diameter(g0) = 6
FEATURE [PartDesign::Pocket] Pocket046
  AllowMultiFace = false
  BaseFeature = -> Pad123
  Length = 24.5
  Length2 = 100
  Profile = -> Sketch187
  Type = 0
FEATURE [Sketcher::SketchObject] Sketch188
  FullyConstrained = false
  MapMode = 5
  Placement = pos=(0,0,0) rot=(1,0,0;3.14159rad)
  Support = -> [Pocket046]
  sketch-geometry (1):
    g0: Circle CenterX=0 CenterY=0 CenterZ=0 NormalX=0 NormalY=0 NormalZ=1 AngleXU=0 Radius=1.75
  constraints (2):
    c: Coincident(g0,g-1)
    c: Diameter(g0) = 3.5
FEATURE [PartDesign::Pocket] Pocket047
  AllowMultiFace = false
  BaseFeature = -> Pocket046
  Length = 6
  Length2 = 100
  Profile = -> Sketch188
  Type = 0
FEATURE [Sketcher::SketchObject] Sketch189
  FullyConstrained = false
  MapMode = 5
  Placement = pos=(0,0,0) rot=(1,0,0;1.5708rad)
  Support = -> [XZ_Plane126]
  sketch-geometry (1):
    g0: Circle CenterX=0 CenterY=24.5 CenterZ=0 NormalX=0 NormalY=0 NormalZ=1 AngleXU=0 Radius=1.75
  constraints (3):
    c: PointOnObject(g0,g-2)
    c: DistanceY(g-1,g0) = 24.5
    c: Diameter(g0) = 3.5
FEATURE [PartDesign::Pocket] Pocket048
  AllowMultiFace = false
  BaseFeature = -> Pocket047
  Length = 14
  Length2 = 100
  Midplane = true
  Profile = -> Sketch189
  Type = 0
FEATURE [PartDesign::Body] Body102  label="Axel003"
  Group = -> [Sketch185,Pad122,Sketch186,Pad123,Sketch187,Pocket046,Sketch188,Pocket047,Sketch189,Pocket048]
  Origin = -> Origin125
  Placement = pos=(0,10.3,0) rot=(0.935113,-0.250563,0.250563;1.63783rad)
  Tip = -> Pocket048
FEATURE [Sketcher::SketchObject] Sketch190
  FullyConstrained = false
  MapMode = 5
  Support = -> [XY_Plane127]
  sketch-geometry (4):
    g0: LineSegment StartX=-16 StartY=16 StartZ=0 EndX=30 EndY=16 EndZ=0
    g1: LineSegment StartX=30 StartY=16 StartZ=0 EndX=30 EndY=-16 EndZ=0
    g2: LineSegment StartX=30 StartY=-16 StartZ=0 EndX=-16 EndY=-16 EndZ=0
    g3: LineSegment StartX=-16 StartY=-16 StartZ=0 EndX=-16 EndY=16 EndZ=0
  constraints (11):
    c: Coincident(g0,g1)
    c: Coincident(g1,g2)
    c: Coincident(g2,g3)
    c: Coincident(g3,g0)
    c: Horizontal(g0)
    c: Horizontal(g2)
    c: Vertical(g1)
    c: DistanceX(g0,g0) = 46
    c: DistanceY(g3,g3) = 32
    c: Symmetric(g0,g2,g-1)
    c: DistanceX(g2,g-1) = 16
FEATURE [PartDesign::Pad] Pad124
  AllowMultiFace = false
  Direction = (1,1,1)
  Length = 21
  Length2 = 100
  Profile = -> Sketch190
  Type = 0
FEATURE [Sketcher::SketchObject] Sketch191
  FullyConstrained = false
  MapMode = 5
  Placement = pos=(30,0,0) rot=(0.57735,0.57735,0.57735;2.0944rad)
  Support = -> [Pad124]
  sketch-geometry (1):
    g0: Circle CenterX=0 CenterY=12.5 CenterZ=0 NormalX=0 NormalY=0 NormalZ=1 AngleXU=0 Radius=12.5
  constraints (3):
    c: Diameter(g0) = 25
    c: PointOnObject(g0,g-2)
    c: DistanceY(g-1,g0) = 12.5
FEATURE [PartDesign::Pad] Pad125
  AllowMultiFace = false
  BaseFeature = -> Pad124
  Direction = (1,1,1)
  Length = 32
  Length2 = 100
  Profile = -> Sketch191
  Type = 0
FEATURE [Sketcher::SketchObject] Sketch192
  FullyConstrained = false
  MapMode = 5
  Placement = pos=(0,0,0) rot=(1,0,0;3.14159rad)
  Support = -> [Pad125]
  sketch-geometry (2):
    g0: ArcOfCircle CenterX=0 CenterY=0 CenterZ=0 NormalX=0 NormalY=0 NormalZ=1 AngleXU=0 Radius=3 StartAngle=0.585686 EndAngle=5.6975
    g1: LineSegment StartX=2.5 StartY=1.65831 StartZ=0 EndX=2.5 EndY=-1.65831 EndZ=0
  constraints (6):
    c: Coincident(g0,g-1)
    c: Diameter(g0) = 6
    c: Coincident(g1,g0)
    c: Coincident(g1,g0)
    c: Vertical(g1)
    c: DistanceX(g0,g0) = 2.5
FEATURE [PartDesign::Pad] Pad126
  AllowMultiFace = false
  BaseFeature = -> Pad125
  Direction = (1,1,1)
  Length = 15
  Length2 = 100
  Profile = -> Sketch192
  Type = 0
FEATURE [Sketcher::SketchObject] Sketch193
  FullyConstrained = false
  MapMode = 5
  Placement = pos=(0,0,21) rot=(0,0,1;0rad)
  Support = -> [Pad126]
  sketch-geometry (2):
    g0: ArcOfCircle CenterX=0 CenterY=0 CenterZ=0 NormalX=0 NormalY=0 NormalZ=1 AngleXU=0 Radius=3 StartAngle=0.585686 EndAngle=5.6975
    g1: LineSegment StartX=2.5 StartY=1.65831 StartZ=0 EndX=2.5 EndY=-1.65831 EndZ=0
  constraints (6):
    c: Coincident(g0,g-1)
    c: Coincident(g1,g0)
    c: Coincident(g1,g0)
    c: Vertical(g1)
    c: DistanceX(g0,g0) = 2.5
    c: Diameter(g0) = 6
FEATURE [PartDesign::Pad] Pad127
  AllowMultiFace = false
  BaseFeature = -> Pad126
  Direction = (1,1,1)
  Length = 15
  Length2 = 100
  Profile = -> Sketch193
  Type = 0
FEATURE [PartDesign::Body] Body099  label="Motor003"
  Group = -> [Sketch190,Pad124,Sketch191,Pad125,Sketch192,Pad126,Sketch193,Pad127]
  Origin = -> Origin128
  Placement = pos=(-1.1e-14,-24,0) rot=(0.57735,-0.57735,0.57735;2.0944rad)
  Tip = -> Pad127
FEATURE [Sketcher::SketchObject] Sketch194
  FullyConstrained = false
  MapMode = 5
  Placement = pos=(0,0,0) rot=(0.57735,0.57735,0.57735;2.0944rad)
  Support = -> [YZ_Plane128]
  sketch-geometry (8):
    g0: LineSegment StartX=-24 StartY=64 StartZ=0 EndX=-24 EndY=-12 EndZ=0
    g1: LineSegment StartX=-24 StartY=-12 StartZ=0 EndX=-21 EndY=-12 EndZ=0
    g2: LineSegment StartX=-21 StartY=-12 StartZ=0 EndX=-21 EndY=64 EndZ=0
    g3: LineSegment StartX=-20 StartY=65 StartZ=0 EndX=16 EndY=65 EndZ=0
    g4: LineSegment StartX=16 StartY=65 StartZ=0 EndX=16 EndY=68 EndZ=0
    g5: LineSegment StartX=16 StartY=68 StartZ=0 EndX=-20 EndY=68 EndZ=0
    g6: ArcOfCircle CenterX=-20 CenterY=64 CenterZ=0 NormalX=0 NormalY=0 NormalZ=1 AngleXU=0 Radius=4 StartAngle=1.5708 EndAngle=3.14159
    g7: ArcOfCircle CenterX=-20 CenterY=64 CenterZ=0 NormalX=0 NormalY=0 NormalZ=1 AngleXU=0 Radius=1 StartAngle=1.5708 EndAngle=3.14159
  constraints (21):
    c: Coincident(g0,g1)
    c: Coincident(g1,g2)
    c: Coincident(g3,g4)
    c: Coincident(g4,g5)
    c: Vertical(g0)
    c: Horizontal(g1)
    c: Tangent(g7,g2) = 1.5708
    c: Tangent(g7,g3) = 1.5708
    c: Tangent(g6,g0) = -1.5708
    c: Tangent(g6,g5) = -1.5708
    c: Horizontal(g5)
    c: Vertical(g4)
    c: Equal(g1,g4)
    c: DistanceY(g4,g4) = 3
    c: Diameter(g7) = 2
    c: Horizontal(g3)
    c: DistanceY(g1,g-1) = 12
    c: DistanceY(g-1,g3) = 65
    c: Coincident(g6,g7)
    c: DistanceX(g0,g-1) = 24
    c: DistanceX(g0,g4) = 40
FEATURE [PartDesign::Pad] Pad128
  AllowMultiFace = false
  Direction = (1,1,1)
  Length = 30
  Length2 = 100
  Midplane = true
  Placement = pos=(0,0,0) rot=(0.57735,0.57735,0.57735;2.0944rad)
  Profile = -> Sketch194
  Type = 0
FEATURE [Sketcher::SketchObject] Sketch195
  FullyConstrained = false
  MapMode = 5
  Placement = pos=(-1.9e-14,2.99e-14,68) rot=(0,0,-1;1.5708rad)
  Support = -> [Pad128]
  sketch-geometry (9):
    g0: Circle CenterX=0 CenterY=0 CenterZ=0 NormalX=0 NormalY=0 NormalZ=1 AngleXU=0 Radius=3.25
    g1: LineSegment StartX=-10 StartY=10 StartZ=0 EndX=10 EndY=10 EndZ=0
    g2: LineSegment StartX=10 StartY=10 StartZ=0 EndX=10 EndY=-10 EndZ=0
    g3: LineSegment StartX=10 StartY=-10 StartZ=0 EndX=-10 EndY=-10 EndZ=0
    g4: LineSegment StartX=-10 StartY=-10 StartZ=0 EndX=-10 EndY=10 EndZ=0
    g5: Circle CenterX=10 CenterY=10 CenterZ=0 NormalX=0 NormalY=0 NormalZ=1 AngleXU=0 Radius=1.75
    g6: Circle CenterX=10 CenterY=-10 CenterZ=0 NormalX=0 NormalY=0 NormalZ=1 AngleXU=0 Radius=1.75
    g7: Circle CenterX=-10 CenterY=-10 CenterZ=0 NormalX=0 NormalY=0 NormalZ=1 AngleXU=0 Radius=1.75
    g8: Circle CenterX=-10 CenterY=10 CenterZ=0 NormalX=0 NormalY=0 NormalZ=1 AngleXU=0 Radius=1.75
  constraints (21):
    c: Coincident(g0,g-1)
    c: Diameter(g0) = 6.5
    c: Coincident(g1,g2)
    c: Coincident(g2,g3)
    c: Coincident(g3,g4)
    c: Coincident(g4,g1)
    c: Horizontal(g1)
    c: Horizontal(g3)
    c: Vertical(g2)
    c: Vertical(g4)
    c: DistanceX(g1,g1) = 20
    c: DistanceY(g4,g4) = 20
    c: Symmetric(g1,g2,g0)
    c: Coincident(g8,g1)
    c: Coincident(g5,g1)
    c: Coincident(g6,g2)
    c: Coincident(g7,g3)
    c: Diameter(g7) = 3.5
    c: Equal(g7,g6)
    c: Equal(g7,g5)
    c: Equal(g7,g8)
FEATURE [PartDesign::Pocket] Pocket049
  AllowMultiFace = false
  BaseFeature = -> Pad128
  Length = 5
  Length2 = 100
  Placement = pos=(0,0,0) rot=(0.57735,0.57735,0.57735;2.0944rad)
  Profile = -> Sketch195
  Type = 0
FEATURE [PartDesign::Body] Body100  label="Wheel Bracket003"
  Group = -> [Sketch194,Pad128,Sketch195,Pocket049]
  Origin = -> Origin127
  Tip = -> Pocket049
FEATURE [Part::Part2DObjectPython] InvoluteGear005  # Draft 2D object (typed FeaturePython)
  ExternalGear = true
  HighPrecision = true
  Modules = 2
  NumberOfTeeth = 26
  PressureAngle = 20
FEATURE [PartDesign::Pad] Pad129
  AllowMultiFace = false
  Direction = (1,1,1)
  Length = 5
  Length2 = 100
  Profile = -> InvoluteGear005
  Type = 0
FEATURE [Sketcher::SketchObject] Sketch196
  FullyConstrained = false
  MapMode = 5
  Placement = pos=(0,0,5) rot=(0,0,1;0rad)
  Support = -> [Pad129]
  sketch-geometry (9):
    g0: Circle CenterX=0 CenterY=0 CenterZ=0 NormalX=0 NormalY=0 NormalZ=1 AngleXU=0 Radius=3.25
    g1: LineSegment StartX=-10 StartY=10 StartZ=0 EndX=10 EndY=10 EndZ=0
    g2: LineSegment StartX=10 StartY=10 StartZ=0 EndX=10 EndY=-10 EndZ=0
    g3: LineSegment StartX=10 StartY=-10 StartZ=0 EndX=-10 EndY=-10 EndZ=0
    g4: LineSegment StartX=-10 StartY=-10 StartZ=0 EndX=-10 EndY=10 EndZ=0
    g5: Circle CenterX=-10 CenterY=10 CenterZ=0 NormalX=0 NormalY=0 NormalZ=1 AngleXU=0 Radius=1.75
    g6: Circle CenterX=10 CenterY=10 CenterZ=0 NormalX=0 NormalY=0 NormalZ=1 AngleXU=0 Radius=1.75
    g7: Circle CenterX=10 CenterY=-10 CenterZ=0 NormalX=0 NormalY=0 NormalZ=1 AngleXU=0 Radius=1.75
    g8: Circle CenterX=-10 CenterY=-10 CenterZ=0 NormalX=0 NormalY=0 NormalZ=1 AngleXU=0 Radius=1.75
  constraints (21):
    c: Coincident(g0,g-1)
    c: Diameter(g0) = 6.5
    c: Coincident(g1,g2)
    c: Coincident(g2,g3)
    c: Coincident(g3,g4)
    c: Coincident(g4,g1)
    c: Horizontal(g1)
    c: Horizontal(g3)
    c: Vertical(g2)
    c: Vertical(g4)
    c: DistanceX(g3,g3) = 20
    c: DistanceY(g4,g4) = 20
    c: Symmetric(g2,g1,g0)
    c: Coincident(g8,g3)
    c: Coincident(g7,g2)
    c: Coincident(g6,g1)
    c: Coincident(g5,g1)
    c: Diameter(g5) = 3.5
    c: Equal(g5,g8)
    c: Equal(g5,g6)
    c: Equal(g5,g7)
FEATURE [PartDesign::Pocket] Pocket050
  AllowMultiFace = false
  BaseFeature = -> Pad129
  Length = 5
  Length2 = 100
  Profile = -> Sketch196
  Type = 0
FEATURE [PartDesign::Body] Body098  label="Wheel Gear003"
  Group = -> [InvoluteGear005,Pad129,Sketch196,Pocket050]
  Origin = -> Origin129
  Placement = pos=(0,0,68) rot=(0,0,1;0rad)
  Tip = -> Pocket050
FEATURE [Sketcher::SketchObject] Sketch197
  FullyConstrained = false
  MapMode = 5
  Support = -> [XY_Plane130]
  sketch-geometry (1):
    g0: Circle CenterX=0 CenterY=0 CenterZ=0 NormalX=0 NormalY=0 NormalZ=1 AngleXU=0 Radius=2.95
  constraints (2):
    c: Coincident(g0,g-1)
    c: Diameter(g0) = 5.9
FEATURE [PartDesign::Pad] Pad130
  AllowMultiFace = false
  Direction = (1,1,1)
  Length = 70
  Length2 = 100
  Profile = -> Sketch197
  Type = 0
FEATURE [Sketcher::SketchObject] Sketch198
  FullyConstrained = false
  MapMode = 5
  Placement = pos=(0,0,0) rot=(1,0,0;3.14159rad)
  Support = -> [Pad130]
  sketch-geometry (7):
    g0: LineSegment StartX=-3.917e-13 StartY=5.7735 StartZ=0 EndX=-5 EndY=2.88675 EndZ=0
    g1: LineSegment StartX=-5 StartY=2.88675 StartZ=0 EndX=-5 EndY=-2.88675 EndZ=0
    g2: LineSegment StartX=-5 StartY=-2.88675 StartZ=0 EndX=0 EndY=-5.7735 EndZ=0
    g3: LineSegment StartX=0 StartY=-5.7735 StartZ=0 EndX=5 EndY=-2.88675 EndZ=0
    g4: LineSegment StartX=5 StartY=-2.88675 StartZ=0 EndX=5 EndY=2.88675 EndZ=0
    g5: LineSegment StartX=5 StartY=2.88675 StartZ=0 EndX=-3.917e-13 EndY=5.7735 EndZ=0
    g6: Circle CenterX=0 CenterY=0 CenterZ=0 NormalX=0 NormalY=0 NormalZ=1 AngleXU=0 Radius=5.7735
  constraints (16):
    c: Coincident(g0,g1)
    c: Coincident(g1,g2)
    c: Coincident(g2,g3)
    c: Coincident(g3,g4)
    c: Coincident(g4,g5)
    c: Coincident(g5,g0)
    c: Equal(g0, g1-g5) x5
    c: PointOnObject(g0,g6)
    c: PointOnObject(g1,g6)
    c: PointOnObject(g2,g6)
    c: PointOnObject(g3,g6)
    c: PointOnObject(g4,g6)
    c: PointOnObject(g5,g6)
    c: Coincident(g6,g-1)
    c: Distance(g0,g4) = 10
    c: PointOnObject(g2,g-2)
FEATURE [PartDesign::Pad] Pad131
  AllowMultiFace = false
  BaseFeature = -> Pad130
  Direction = (1,1,1)
  Length = 4
  Length2 = 100
  Profile = -> Sketch198
  Type = 0
FEATURE [PartDesign::Body] Body103  label="M6x70_Hex_Head003"
  Group = -> [Sketch197,Pad130,Sketch198,Pad131]
  Origin = -> Origin130
  Placement = pos=(0,0,65) rot=(0,0,1;0rad)
  Tip = -> Pad131
FEATURE [Sketcher::SketchObject] Sketch199
  FullyConstrained = false
  MapMode = 5
  Support = -> [XY_Plane131]
  sketch-geometry (2):
    g0: Circle CenterX=0 CenterY=0 CenterZ=0 NormalX=0 NormalY=0 NormalZ=1 AngleXU=0 Radius=5.85
    g1: Circle CenterX=0 CenterY=0 CenterZ=0 NormalX=0 NormalY=0 NormalZ=1 AngleXU=0 Radius=3
  constraints (4):
    c: Coincident(g1,g0)
    c: Coincident(g1,g-1)
    c: Diameter(g1) = 6
    c: Diameter(g0) = 11.7
FEATURE [PartDesign::Pad] Pad132
  AllowMultiFace = false
  Direction = (1,1,1)
  Length = 1.5
  Length2 = 100
  Profile = -> Sketch199
  Type = 0
FEATURE [PartDesign::Body] Body104  label="M6_Washer010"
  Group = -> [Sketch199,Pad132]
  Origin = -> Origin131
  Placement = pos=(0,0,73) rot=(0,0,1;0rad)
  Tip = -> Pad132
FEATURE [Sketcher::SketchObject] Sketch200
  FullyConstrained = false
  MapMode = 5
  Support = -> [XY_Plane132]
  sketch-geometry (8):
    g0: LineSegment StartX=0 StartY=5.7735 StartZ=0 EndX=-5 EndY=2.88675 EndZ=0
    g1: LineSegment StartX=-5 StartY=2.88675 StartZ=0 EndX=-5 EndY=-2.88675 EndZ=0
    g2: LineSegment StartX=-5 StartY=-2.88675 StartZ=0 EndX=-1.501e-13 EndY=-5.7735 EndZ=0
    g3: LineSegment StartX=-1.501e-13 StartY=-5.7735 StartZ=0 EndX=5 EndY=-2.88675 EndZ=0
    g4: LineSegment StartX=5 StartY=-2.88675 StartZ=0 EndX=5 EndY=2.88675 EndZ=0
    g5: LineSegment StartX=5 StartY=2.88675 StartZ=0 EndX=0 EndY=5.7735 EndZ=0
    g6: Circle CenterX=0 CenterY=0 CenterZ=0 NormalX=0 NormalY=0 NormalZ=1 AngleXU=0 Radius=5.7735
    g7: Circle CenterX=0 CenterY=0 CenterZ=0 NormalX=0 NormalY=0 NormalZ=1 AngleXU=0 Radius=3
  constraints (18):
    c: Coincident(g0,g1)
    c: Coincident(g1,g2)
    c: Coincident(g2,g3)
    c: Coincident(g3,g4)
    c: Coincident(g4,g5)
    c: Coincident(g5,g0)
    c: Equal(g0, g1-g5) x5
    c: PointOnObject(g0,g6)
    c: PointOnObject(g1,g6)
    c: PointOnObject(g2,g6)
    c: PointOnObject(g3,g6)
    c: PointOnObject(g4,g6)
    c: PointOnObject(g5,g6)
    c: Coincident(g6,g-1)
    c: PointOnObject(g0,g-2)
    c: Distance(g0,g4) = 10
    c: Coincident(g7,g-1)
    c: Diameter(g7) = 6
FEATURE [PartDesign::Pad] Pad133
  AllowMultiFace = false
  Direction = (1,1,1)
  Length = 5
  Length2 = 100
  Profile = -> Sketch200
  Type = 0
FEATURE [PartDesign::Body] Body105  label="M6_Full_Nut009"
  Group = -> [Sketch200,Pad133]
  Origin = -> Origin132
  Placement = pos=(0,0,74.5) rot=(0,0,1;0rad)
  Tip = -> Pad133
FEATURE [Sketcher::SketchObject] Sketch201
  FullyConstrained = false
  MapMode = 5
  Support = -> [XY_Plane133]
  sketch-geometry (2):
    g0: Circle CenterX=0 CenterY=0 CenterZ=0 NormalX=0 NormalY=0 NormalZ=1 AngleXU=0 Radius=9.5
    g1: Circle CenterX=0 CenterY=0 CenterZ=0 NormalX=0 NormalY=0 NormalZ=1 AngleXU=0 Radius=3
  constraints (4):
    c: Coincident(g0,g-1)
    c: Coincident(g0,g1)
    c: Diameter(g1) = 6
    c: Diameter(g0) = 19
FEATURE [PartDesign::Pad] Pad134
  AllowMultiFace = false
  Direction = (1,1,1)
  Length = 6
  Length2 = 100
  Profile = -> Sketch201
  Type = 0
FEATURE [PartDesign::Body] Body106  label="6mm_bearing006"
  Group = -> [Sketch201,Pad134]
  Origin = -> Origin133
  Placement = pos=(0,0,81) rot=(0,0,1;0rad)
  Tip = -> Pad134
FEATURE [Sketcher::SketchObject] Sketch202
  FullyConstrained = false
  MapMode = 5
  Support = -> [XY_Plane134]
  sketch-geometry (2):
    g0: Circle CenterX=0 CenterY=0 CenterZ=0 NormalX=0 NormalY=0 NormalZ=1 AngleXU=0 Radius=5.85
    g1: Circle CenterX=0 CenterY=0 CenterZ=0 NormalX=0 NormalY=0 NormalZ=1 AngleXU=0 Radius=3
  constraints (4):
    c: Coincident(g1,g0)
    c: Coincident(g1,g-1)
    c: Diameter(g1) = 6
    c: Diameter(g0) = 11.7
FEATURE [PartDesign::Pad] Pad135
  AllowMultiFace = false
  Direction = (1,1,1)
  Length = 1.5
  Length2 = 100
  Profile = -> Sketch202
  Type = 0
FEATURE [PartDesign::Body] Body107  label="M6_Washer011"
  Group = -> [Sketch202,Pad135]
  Origin = -> Origin134
  Placement = pos=(0,0,79.5) rot=(0,0,1;0rad)
  Tip = -> Pad135
FEATURE [Sketcher::SketchObject] Sketch203
  FullyConstrained = false
  MapMode = 5
  Support = -> [XY_Plane135]
  sketch-geometry (2):
    g0: Circle CenterX=0 CenterY=0 CenterZ=0 NormalX=0 NormalY=0 NormalZ=1 AngleXU=0 Radius=9.5
    g1: Circle CenterX=0 CenterY=0 CenterZ=0 NormalX=0 NormalY=0 NormalZ=1 AngleXU=0 Radius=3
  constraints (4):
    c: Coincident(g0,g-1)
    c: Coincident(g0,g1)
    c: Diameter(g1) = 6
    c: Diameter(g0) = 19
FEATURE [PartDesign::Pad] Pad136
  AllowMultiFace = false
  Direction = (1,1,1)
  Length = 6
  Length2 = 100
  Profile = -> Sketch203
  Type = 0
FEATURE [PartDesign::Body] Body108  label="6mm_bearing007"
  Group = -> [Sketch203,Pad136]
  Origin = -> Origin135
  Placement = pos=(0,0,115) rot=(0,0,1;0rad)
  Tip = -> Pad136
FEATURE [Sketcher::SketchObject] Sketch204
  FullyConstrained = false
  MapMode = 5
  Support = -> [XY_Plane136]
  sketch-geometry (2):
    g0: Circle CenterX=0 CenterY=0 CenterZ=0 NormalX=0 NormalY=0 NormalZ=1 AngleXU=0 Radius=5.85
    g1: Circle CenterX=0 CenterY=0 CenterZ=0 NormalX=0 NormalY=0 NormalZ=1 AngleXU=0 Radius=3
  constraints (4):
    c: Coincident(g1,g0)
    c: Coincident(g1,g-1)
    c: Diameter(g1) = 6
    c: Diameter(g0) = 11.7
FEATURE [PartDesign::Pad] Pad137
  AllowMultiFace = false
  Direction = (1,1,1)
  Length = 1.5
  Length2 = 100
  Profile = -> Sketch204
  Type = 0
FEATURE [PartDesign::Body] Body109  label="M6_Washer012"
  Group = -> [Sketch204,Pad137]
  Origin = -> Origin136
  Placement = pos=(0,0,121) rot=(0,0,1;0rad)
  Tip = -> Pad137
FEATURE [Sketcher::SketchObject] Sketch205
  FullyConstrained = false
  MapMode = 5
  Support = -> [XY_Plane137]
  sketch-geometry (8):
    g0: LineSegment StartX=0 StartY=5.7735 StartZ=0 EndX=-5 EndY=2.88675 EndZ=0
    g1: LineSegment StartX=-5 StartY=2.88675 StartZ=0 EndX=-5 EndY=-2.88675 EndZ=0
    g2: LineSegment StartX=-5 StartY=-2.88675 StartZ=0 EndX=-1.501e-13 EndY=-5.7735 EndZ=0
    g3: LineSegment StartX=-1.501e-13 StartY=-5.7735 StartZ=0 EndX=5 EndY=-2.88675 EndZ=0
    g4: LineSegment StartX=5 StartY=-2.88675 StartZ=0 EndX=5 EndY=2.88675 EndZ=0
    g5: LineSegment StartX=5 StartY=2.88675 StartZ=0 EndX=0 EndY=5.7735 EndZ=0
    g6: Circle CenterX=0 CenterY=0 CenterZ=0 NormalX=0 NormalY=0 NormalZ=1 AngleXU=0 Radius=5.7735
    g7: Circle CenterX=0 CenterY=0 CenterZ=0 NormalX=0 NormalY=0 NormalZ=1 AngleXU=0 Radius=3
  constraints (18):
    c: Coincident(g0,g1)
    c: Coincident(g1,g2)
    c: Coincident(g2,g3)
    c: Coincident(g3,g4)
    c: Coincident(g4,g5)
    c: Coincident(g5,g0)
    c: Equal(g0, g1-g5) x5
    c: PointOnObject(g0,g6)
    c: PointOnObject(g1,g6)
    c: PointOnObject(g2,g6)
    c: PointOnObject(g3,g6)
    c: PointOnObject(g4,g6)
    c: PointOnObject(g5,g6)
    c: Coincident(g6,g-1)
    c: PointOnObject(g0,g-2)
    c: Distance(g0,g4) = 10
    c: Coincident(g7,g-1)
    c: Diameter(g7) = 6
FEATURE [PartDesign::Pad] Pad138
  AllowMultiFace = false
  Direction = (1,1,1)
  Length = 5
  Length2 = 100
  Profile = -> Sketch205
  Type = 0
FEATURE [PartDesign::Body] Body110  label="M6_Full_Nut010"
  Group = -> [Sketch205,Pad138]
  Origin = -> Origin137
  Placement = pos=(0,0,122.5) rot=(0,0,1;0rad)
  Tip = -> Pad138
FEATURE [Sketcher::SketchObject] Sketch206
  FullyConstrained = false
  MapMode = 5
  Support = -> [XY_Plane139]
  sketch-geometry (1):
    g0: Circle CenterX=0 CenterY=0 CenterZ=0 NormalX=0 NormalY=0 NormalZ=1 AngleXU=0 Radius=41.6542
  constraints (1):
    c: Coincident(g0,g-1)
FEATURE [PartDesign::Body] Body111
  Group = -> [Sketch206]
  Origin = -> Origin139
FEATURE [App::Part] Part013  label="wheel003"
  Group = -> [Body101,Body102,Body099,Body100,Body098,Body103,Body106,Body108,Body104,Body105,Body107,Body109,Body110,Body111]
  Origin = -> Origin138
  Placement = pos=(100,-72,0) rot=(0,0,1;3.14159rad)
FEATURE [Sketcher::SketchObject] Sketch207
  FullyConstrained = false
  MapMode = 5
  Support = -> [XY_Plane140]
  sketch-geometry (4):
    g0: LineSegment StartX=-44 StartY=28 StartZ=0 EndX=44 EndY=28 EndZ=0
    g1: LineSegment StartX=44 StartY=28 StartZ=0 EndX=44 EndY=-28 EndZ=0
    g2: LineSegment StartX=44 StartY=-28 StartZ=0 EndX=-44 EndY=-28 EndZ=0
    g3: LineSegment StartX=-44 StartY=-28 StartZ=0 EndX=-44 EndY=28 EndZ=0
  constraints (11):
    c: Coincident(g0,g1)
    c: Coincident(g1,g2)
    c: Coincident(g2,g3)
    c: Coincident(g3,g0)
    c: Horizontal(g0)
    c: Horizontal(g2)
    c: Vertical(g1)
    c: Vertical(g3)
    c: DistanceX(g0,g0) = 88
    c: DistanceY(g3,g3) = 56
    c: Symmetric(g0,g1,g-1)
FEATURE [PartDesign::Pad] Pad139
  AllowMultiFace = false
  Direction = (1,1,1)
  Length = 25
  Length2 = 100
  Profile = -> Sketch207
  Type = 0
FEATURE [PartDesign::Body] Body112
  Group = -> [Sketch207,Pad139]
  Origin = -> Origin140
  Placement = pos=(-99,12,104) rot=(0.57735,-0.57735,0.57735;2.0944rad)
  Tip = -> Pad139
FEATURE [Part::Feature] Shape086  label="C9_C_0603_1608Metric_5F754EF011"
  Placement = pos=(26,17.5,0) rot=(0,0,1;3.14159rad)
  shape: bbox 1.6 x 0.8 x 0.8 mm, 28 faces (baked)
FEATURE [Part::Feature] Shape087  label="U4_SOIC_8_39x49mm_P127mm_5F717A079"
  Placement = pos=(40.25,11.5,0) rot=(0,0,1;0rad)
  shape: bbox 6 x 4.9 x 1.75 mm, 156 faces (baked)
FEATURE [Part::Feature] Shape088  label="U3_LQFP_32_7x7mm_P08mm_5F71845B002"
  Placement = pos=(36.5,25.5,0) rot=(0,0,-1;1.5708rad)
  shape: bbox 9 x 9 x 1.5 mm, 516 faces (baked)
FEATURE [Part::Feature] Shape089  label="J3_PinHeader_1x15_P254mm_Vertical_5F717817"
  Placement = pos=(54,47,-1.6) rot=(0,1,0;3.14159rad)
  shape: bbox 2.54 x 38.1 x 11.54 mm, 364 faces (baked)
FEATURE [Part::Feature] Shape090  label="U5_SOT_23_5_5F717A8C002"
  Placement = pos=(4.5,23,0) rot=(0,0,1;1.5708rad)
  shape: bbox 2.9 x 2.8 x 1.55 mm, 109 faces (baked)
FEATURE [Part::Feature] Shape091  label="C8_C_0603_1608Metric_5F7555CB002"
  Placement = pos=(26,13,0) rot=(0,0,1;3.14159rad)
  shape: bbox 1.6 x 0.8 x 0.8 mm, 28 faces (baked)
FEATURE [PartDesign::CoordinateSystem] Local_CS_d4f005
  AttacherType = Attacher::AttachEngine3D
FEATURE [Part::Feature] Pcb_d4f005
  Placement = pos=(-90,100,0) rot=(0,0,1;0rad)
  shape: bbox 66 x 50 x 1.6 mm, 84 faces (baked)
FEATURE [Sketcher::SketchObject] PCB_Sketch_d4f005
  FullyConstrained = false
  sketch-geometry (8):
    g0: LineSegment StartX=4e-16 StartY=3 StartZ=0 EndX=-3.6e-15 EndY=47 EndZ=0
    g1: LineSegment StartX=63 StartY=8.4e-15 StartZ=0 EndX=3 EndY=4e-16 EndZ=0
    g2: LineSegment StartX=66 StartY=47 StartZ=0 EndX=66 EndY=3 EndZ=0
    g3: LineSegment StartX=3 StartY=50 StartZ=0 EndX=63 EndY=50 EndZ=0
    g4: ArcOfCircle CenterX=63 CenterY=47 CenterZ=0 NormalX=0 NormalY=0 NormalZ=1 AngleXU=0 Radius=3 StartAngle=0 EndAngle=1.5708
    g5: ArcOfCircle CenterX=63 CenterY=3 CenterZ=0 NormalX=0 NormalY=0 NormalZ=1 AngleXU=0 Radius=3 StartAngle=4.71239 EndAngle=6.28319
    g6: ArcOfCircle CenterX=3 CenterY=3 CenterZ=0 NormalX=0 NormalY=0 NormalZ=1 AngleXU=0 Radius=3 StartAngle=3.14159 EndAngle=4.71239
    g7: ArcOfCircle CenterX=3 CenterY=47 CenterZ=0 NormalX=0 NormalY=0 NormalZ=1 AngleXU=0 Radius=3 StartAngle=1.5708 EndAngle=3.14159
  constraints (8):
    c: Coincident(g0,g6)
    c: Coincident(g0,g7)
    c: Coincident(g1,g6)
    c: Coincident(g3,g7)
    c: Coincident(g1,g5)
    c: Coincident(g3,g4)
    c: Coincident(g2,g5)
    c: Coincident(g2,g4)
FEATURE [App::Part] Board_Geoms_d4f005  label="Board_Geoms_d4f007"
  Group = -> [Local_CS_d4f005,Pcb_d4f005,PCB_Sketch_d4f005]
  Origin = -> Origin177
FEATURE [Part::Feature] Shape092  label="U2_SOT_353_SC_70_5_5F717A014"
  Placement = pos=(26,15.25,0) rot=(0,0,1;3.14159rad)
  shape: bbox 2 x 2 x 1.05 mm, 104 faces (baked)
FEATURE [Part::Feature] Shape093  label="U1_SOT_353_SC_70_5_5F7179FD002"
  Placement = pos=(26,19.75,0) rot=(0,0,1;3.14159rad)
  shape: bbox 2 x 2 x 1.05 mm, 104 faces (baked)
FEATURE [Part::Feature] Shape094  label="SW1_SW_PUSH_6mm_5F7179E010"
  Placement = pos=(41.5,37.75,0) rot=(0,0,1;3.14159rad)
  shape: bbox 7.174 x 6 x 7.8 mm, 105 faces (baked)
FEATURE [Part::Feature] Shape095  label="R7_R_0603_1608Metric_5F7179C011"
  Placement = pos=(44.25,36.5,0) rot=(0,0,1;1.5708rad)
  shape: bbox 0.8 x 1.6 x 0.45 mm, 26 faces (baked)
FEATURE [Part::Feature] Shape096  label="R6_R_0603_1608Metric_5F7179B010"
  Placement = pos=(33.25,15.75,0) rot=(0,0,1;1.5708rad)
  shape: bbox 0.8 x 1.6 x 0.45 mm, 26 faces (baked)
FEATURE [Part::Feature] Shape097  label="R5_R_0603_1608Metric_5F7179A009"
  Placement = pos=(30.75,15.75,0) rot=(0,0,1;1.5708rad)
  shape: bbox 0.8 x 1.6 x 0.45 mm, 26 faces (baked)
FEATURE [Part::Feature] Shape098  label="R4_R_0603_1608Metric_5F717998"
  Placement = pos=(15.175,35.57,0) rot=(0,0,1;3.14159rad)
  shape: bbox 1.6 x 0.8 x 0.45 mm, 26 faces (baked)
FEATURE [Part::Feature] Shape099  label="R3_R_0603_1608Metric_5F717987"
  Placement = pos=(15.175,38.11,0) rot=(0,0,1;3.14159rad)
  shape: bbox 1.6 x 0.8 x 0.45 mm, 26 faces (baked)
FEATURE [Part::Feature] Shape100  label="R2_R_0603_1608Metric_5F717976"
  Placement = pos=(15.175,40.65,0) rot=(0,0,1;3.14159rad)
  shape: bbox 1.6 x 0.8 x 0.45 mm, 26 faces (baked)
FEATURE [Part::Feature] Shape101  label="R1_R_0603_1608Metric_5F717965"
  Placement = pos=(15.175,43.19,0) rot=(0,0,1;3.14159rad)
  shape: bbox 1.6 x 0.8 x 0.45 mm, 26 faces (baked)
FEATURE [Part::Feature] Shape102  label="J13_MSTBA_01x02_G_5_08mm_5F717954"
  Placement = pos=(44,3.5,0) rot=(0,0,1;0rad)
  shape: bbox 12.16 x 12 x 12.6 mm, 63 faces (baked)
FEATURE [Part::Feature] Shape103  label="J12_PinHeader_1x06_P254mm_Vertical_5F71792E002"
  Placement = pos=(34.95,46.25,0) rot=(0,0,1;1.5708rad)
  shape: bbox 15.24 x 2.54 x 11.54 mm, 148 faces (baked)
FEATURE [Part::Feature] Shape104  label="J11_PinHeader_1x03_P254mm_Vertical_5F717916"
  Placement = pos=(1.84,13.98,0) rot=(0,0,1;1.5708rad)
  shape: bbox 7.62 x 2.54 x 11.54 mm, 76 faces (baked)
FEATURE [Part::Feature] Shape105  label="J10_PinHeader_1x03_P254mm_Vertical_5F7178FD002"
  Placement = pos=(1.84,16.52,0) rot=(0,0,1;1.5708rad)
  shape: bbox 7.62 x 2.54 x 11.54 mm, 76 faces (baked)
FEATURE [Part::Feature] Shape106  label="J9_MSTBA_01x04_G_5_08mm_5F7178E008"
  Placement = pos=(20.5,3.5,0) rot=(0,0,1;0rad)
  shape: bbox 22.32 x 12 x 12.6 mm, 113 faces (baked)
FEATURE [Part::Feature] Shape107  label="J8_PinSocket_1x15_P254mm_Vertical_5F7178B012"
  Placement = pos=(12,47,-1.6) rot=(0,1,0;3.14159rad)
  shape: bbox 2.54 x 38.1 x 10.1 mm, 475 faces (baked)
FEATURE [App::Part] Bot_d4f005  label="Bot_d4f007"
  Group = -> [Shape089,Shape107]
  Origin = -> Origin181
FEATURE [Part::Feature] Shape108  label="J7_SHF-105-01-L-D-SM-K-TR_5F717897"
  Placement = pos=(48,17.25,0) rot=(0.57735,0.57735,0.57735;2.0944rad)
  shape: bbox 6.502 x 12.7 x 5.588 mm, 207 faces, 4 solids (baked)
FEATURE [Part::Feature] Shape109  label="J6_PinHeader_1x03_P254mm_Vertical_5F717877"
  Placement = pos=(1.84,33.03,0) rot=(0,0,1;1.5708rad)
  shape: bbox 7.62 x 2.54 x 11.54 mm, 76 faces (baked)
FEATURE [Part::Feature] Shape110  label="J5_PinHeader_1x03_P254mm_Vertical_5F722999"
  Placement = pos=(1.84,35.57,0) rot=(0,0,1;1.5708rad)
  shape: bbox 7.62 x 2.54 x 11.54 mm, 76 faces (baked)
FEATURE [Part::Feature] Shape111  label="J4_Molex_AE_6410_06A_5F717849"
  Placement = pos=(61.62,35.57,0) rot=(0,0,-1;1.5708rad)
  shape: bbox 5.8 x 15.24 x 15.26 mm, 169 faces (baked)
FEATURE [Part::Feature] Shape112  label="J2_PinHeader_1x03_P254mm_Vertical_5F7177F002"
  Placement = pos=(1.84,38.11,0) rot=(0,0,1;1.5708rad)
  shape: bbox 7.62 x 2.54 x 11.54 mm, 76 faces (baked)
FEATURE [Part::Feature] Shape113  label="J1_PinHeader_1x03_P254mm_Vertical_5F7228CA002"
  Placement = pos=(1.84,40.65,0) rot=(0,0,1;1.5708rad)
  shape: bbox 7.62 x 2.54 x 11.54 mm, 76 faces (baked)
FEATURE [Part::Feature] Shape114  label="D6_LED_0603_1608Metric_5F71855F002"
  Placement = pos=(33.25,12.25,0) rot=(0,0,1;1.5708rad)
  shape: bbox 0.8 x 1.6 x 1.1 mm, 50 faces (baked)
FEATURE [Part::Feature] Shape115  label="D5_LED_0603_1608Metric_5F71778F002"
  Placement = pos=(30.75,12.25,0) rot=(0,0,1;1.5708rad)
  shape: bbox 0.8 x 1.6 x 1.1 mm, 50 faces (baked)
FEATURE [Part::Feature] Shape116  label="D4_SOT_23_5F71777C002"
  Placement = pos=(18.985,35.57,0) rot=(0,0,1;0rad)
  shape: bbox 2.5 x 3 x 1.2 mm, 76 faces (baked)
FEATURE [Part::Feature] Shape117  label="D3_SOT_23_5F717769"
  Placement = pos=(22.795,38.11,0) rot=(0,0,1;0rad)
  shape: bbox 2.5 x 3 x 1.2 mm, 76 faces (baked)
FEATURE [Part::Feature] Shape118  label="D2_SOT_23_5F717754"
  Placement = pos=(18.985,40.65,0) rot=(0,0,1;0rad)
  shape: bbox 2.5 x 3 x 1.2 mm, 76 faces (baked)
FEATURE [Part::Feature] Shape119  label="D1_SOT_23_5F71773D002"
  Placement = pos=(22.795,43.19,0) rot=(0,0,1;0rad)
  shape: bbox 2.5 x 3 x 1.2 mm, 76 faces (baked)
FEATURE [Part::Feature] Shape120  label="C7_C_0603_1608Metric_5F717730"
  Placement = pos=(4.5,27.5,0) rot=(0,0,1;0rad)
  shape: bbox 1.6 x 0.8 x 0.8 mm, 28 faces (baked)
FEATURE [Part::Feature] Shape121  label="C6_C_0603_1608Metric_5F717719"
  Placement = pos=(6.25,25.75,0) rot=(0,0,1;0rad)
  shape: bbox 1.6 x 0.8 x 0.8 mm, 28 faces (baked)
FEATURE [Part::Feature] Shape122  label="C5_C_0603_1608Metric_5F717708"
  Placement = pos=(4.5,20.25,0) rot=(0,0,1;0rad)
  shape: bbox 1.6 x 0.8 x 0.8 mm, 28 faces (baked)
FEATURE [Part::Feature] Shape123  label="C4_C_0603_1608Metric_5F7176F007"
  Placement = pos=(41.5,15.25,0) rot=(0,0,1;0rad)
  shape: bbox 1.6 x 0.8 x 0.8 mm, 28 faces (baked)
FEATURE [Part::Feature] Shape124  label="C3_C_0603_1608Metric_5F7176E006"
  Placement = pos=(32.5,39.75,0) rot=(0,0,1;1.5708rad)
  shape: bbox 0.8 x 1.6 x 0.8 mm, 28 faces (baked)
FEATURE [Part::Feature] Shape125  label="C2_C_0603_1608Metric_5F7176D005"
  Placement = pos=(38.25,33,0) rot=(0,0,1;0rad)
  shape: bbox 1.6 x 0.8 x 0.8 mm, 28 faces (baked)
FEATURE [Part::Feature] Shape126  label="C1_C_0805_2012Metric_5F7176C004"
  Placement = pos=(38.25,35,0) rot=(0,0,1;0rad)
  shape: bbox 2 x 1.25 x 1.25 mm, 28 faces (baked)
FEATURE [App::Part] Top_d4f005  label="Top_d4f007"
  Group = -> [Shape086,Shape091,Shape090,Shape087,Shape088,Shape092,Shape093,Shape094,Shape095,Shape096,Shape097,Shape098,Shape099,Shape100,Shape101,Shape102,Shape103,Shape104,Shape105,Shape106,Shape108,Shape109,Shape110,Shape111,Shape112,Shape113,Shape114,Shape115,Shape116,Shape117,Shape118,Shape119,Shape120,Shape121,Shape122,Shape123,Shape124,Shape125,Shape126]
  Origin = -> Origin180
FEATURE [App::Part] Step_Models_d4f005  label="Step_Models_d4f007"
  Group = -> [Top_d4f005,Bot_d4f005]
  Origin = -> Origin179
FEATURE [App::Part] Board_d4f005  label="motor_board002"
  Group = -> [Board_Geoms_d4f005,Step_Models_d4f005]
  Origin = -> Origin178
FEATURE [Sketcher::SketchObject] Sketch208
  FullyConstrained = false
  MapMode = 5
  Support = -> [XY_Plane183]
  sketch-geometry (66):
    g0: LineSegment StartX=0 StartY=41.4 StartZ=0 EndX=47.35 EndY=41.4 EndZ=0
    g1: LineSegment StartX=47.35 StartY=41.4 StartZ=0 EndX=47.35 EndY=0 EndZ=0
    g2: LineSegment StartX=47.35 StartY=0 StartZ=0 EndX=0 EndY=0 EndZ=0
    g3: LineSegment StartX=0 StartY=0 StartZ=0 EndX=0 EndY=41.4 EndZ=0
    g4: LineSegment StartX=2.72 StartY=2.92 StartZ=0 EndX=2.72 EndY=5.46 EndZ=0
    g5: LineSegment StartX=2.72 StartY=5.46 StartZ=0 EndX=2.72 EndY=8 EndZ=0
    g6: LineSegment StartX=2.72 StartY=8 StartZ=0 EndX=2.72 EndY=10.54 EndZ=0
    g7: LineSegment StartX=2.72 StartY=10.54 StartZ=0 EndX=2.72 EndY=13.08 EndZ=0
    g8: LineSegment StartX=2.72 StartY=13.08 StartZ=0 EndX=2.72 EndY=15.62 EndZ=0
    g9: LineSegment StartX=2.72 StartY=15.62 StartZ=0 EndX=2.72 EndY=18.16 EndZ=0
    g10: LineSegment StartX=2.72 StartY=18.16 StartZ=0 EndX=2.72 EndY=20.7 EndZ=0
    g11: LineSegment StartX=2.72 StartY=20.7 StartZ=0 EndX=2.72 EndY=23.24 EndZ=0
    g12: LineSegment StartX=2.72 StartY=23.24 StartZ=0 EndX=2.72 EndY=25.78 EndZ=0
    g13: LineSegment StartX=2.72 StartY=25.78 StartZ=0 EndX=2.72 EndY=28.32 EndZ=0
    g14: LineSegment StartX=2.72 StartY=28.32 StartZ=0 EndX=2.72 EndY=30.86 EndZ=0
    g15: LineSegment StartX=2.72 StartY=30.86 StartZ=0 EndX=2.72 EndY=33.4 EndZ=0
    g16: LineSegment StartX=2.72 StartY=33.4 StartZ=0 EndX=2.72 EndY=35.94 EndZ=0
    g17: LineSegment StartX=2.72 StartY=35.94 StartZ=0 EndX=2.72 EndY=38.48 EndZ=0
    g18: LineSegment StartX=44.63 StartY=2.92 StartZ=0 EndX=44.63 EndY=5.46 EndZ=0
    g19: LineSegment StartX=44.63 StartY=5.46 StartZ=0 EndX=44.63 EndY=8 EndZ=0
    g20: LineSegment StartX=44.63 StartY=8 StartZ=0 EndX=44.63 EndY=10.54 EndZ=0
    g21: LineSegment StartX=44.63 StartY=10.54 StartZ=0 EndX=44.63 EndY=13.08 EndZ=0
    g22: LineSegment StartX=44.63 StartY=13.08 StartZ=0 EndX=44.63 EndY=15.62 EndZ=0
    g23: LineSegment StartX=44.63 StartY=15.62 StartZ=0 EndX=44.63 EndY=18.16 EndZ=0
    g24: LineSegment StartX=44.63 StartY=18.16 StartZ=0 EndX=44.63 EndY=20.7 EndZ=0
    g25: LineSegment StartX=44.63 StartY=20.7 StartZ=0 EndX=44.63 EndY=23.24 EndZ=0
    g26: LineSegment StartX=44.63 StartY=23.24 StartZ=0 EndX=44.63 EndY=25.78 EndZ=0
    g27: LineSegment StartX=44.63 StartY=25.78 StartZ=0 EndX=44.63 EndY=28.32 EndZ=0
    g28: LineSegment StartX=44.63 StartY=28.32 StartZ=0 EndX=44.63 EndY=30.86 EndZ=0
    g29: LineSegment StartX=44.63 StartY=30.86 StartZ=0 EndX=44.63 EndY=33.4 EndZ=0
    g30: LineSegment StartX=44.63 StartY=33.4 StartZ=0 EndX=44.63 EndY=35.94 EndZ=0
    g31: LineSegment StartX=44.63 StartY=35.94 StartZ=0 EndX=44.63 EndY=38.48 EndZ=0
    g32: LineSegment StartX=0 StartY=0 StartZ=0 EndX=2.72 EndY=2.92 EndZ=0
    g33: LineSegment StartX=44.63 StartY=2.92 StartZ=0 EndX=47.35 EndY=0 EndZ=0
    g34: LineSegment StartX=44.63 StartY=38.48 StartZ=0 EndX=47.35 EndY=41.4 EndZ=0
    g35: LineSegment StartX=2.72 StartY=38.48 StartZ=0 EndX=0 EndY=41.4 EndZ=0
    g36: Circle CenterX=2.72 CenterY=38.48 CenterZ=0 NormalX=0 NormalY=0 NormalZ=1 AngleXU=0 Radius=0.5
    g37: Circle CenterX=2.72 CenterY=35.94 CenterZ=0 NormalX=0 NormalY=0 NormalZ=1 AngleXU=0 Radius=0.5
    g38: Circle CenterX=2.72 CenterY=33.4 CenterZ=0 NormalX=0 NormalY=0 NormalZ=1 AngleXU=0 Radius=0.5
    g39: Circle CenterX=2.72 CenterY=30.86 CenterZ=0 NormalX=0 NormalY=0 NormalZ=1 AngleXU=0 Radius=0.5
    g40: Circle CenterX=2.72 CenterY=28.32 CenterZ=0 NormalX=0 NormalY=0 NormalZ=1 AngleXU=0 Radius=0.5
    g41: Circle CenterX=2.72 CenterY=25.78 CenterZ=0 NormalX=0 NormalY=0 NormalZ=1 AngleXU=0 Radius=0.5
    g42: Circle CenterX=2.72 CenterY=23.24 CenterZ=0 NormalX=0 NormalY=0 NormalZ=1 AngleXU=0 Radius=0.5
    g43: Circle CenterX=2.72 CenterY=20.7 CenterZ=0 NormalX=0 NormalY=0 NormalZ=1 AngleXU=0 Radius=0.5
    g44: Circle CenterX=2.72 CenterY=18.16 CenterZ=0 NormalX=0 NormalY=0 NormalZ=1 AngleXU=0 Radius=0.5
    g45: Circle CenterX=2.72 CenterY=15.62 CenterZ=0 NormalX=0 NormalY=0 NormalZ=1 AngleXU=0 Radius=0.5
    g46: Circle CenterX=2.72 CenterY=13.08 CenterZ=0 NormalX=0 NormalY=0 NormalZ=1 AngleXU=0 Radius=0.5
    g47: Circle CenterX=2.72 CenterY=10.54 CenterZ=0 NormalX=0 NormalY=0 NormalZ=1 AngleXU=0 Radius=0.5
    g48: Circle CenterX=2.72 CenterY=8 CenterZ=0 NormalX=0 NormalY=0 NormalZ=1 AngleXU=0 Radius=0.5
    g49: Circle CenterX=2.72 CenterY=5.46 CenterZ=0 NormalX=0 NormalY=0 NormalZ=1 AngleXU=0 Radius=0.5
    g50: Circle CenterX=2.72 CenterY=2.92 CenterZ=0 NormalX=0 NormalY=0 NormalZ=1 AngleXU=0 Radius=0.5
    g51: Circle CenterX=44.63 CenterY=38.48 CenterZ=0 NormalX=0 NormalY=0 NormalZ=1 AngleXU=0 Radius=0.5
    g52: Circle CenterX=44.63 CenterY=35.94 CenterZ=0 NormalX=0 NormalY=0 NormalZ=1 AngleXU=0 Radius=0.5
    g53: Circle CenterX=44.63 CenterY=33.4 CenterZ=0 NormalX=0 NormalY=0 NormalZ=1 AngleXU=0 Radius=0.5
    g54: Circle CenterX=44.63 CenterY=30.86 CenterZ=0 NormalX=0 NormalY=0 NormalZ=1 AngleXU=0 Radius=0.5
    g55: Circle CenterX=44.63 CenterY=28.32 CenterZ=0 NormalX=0 NormalY=0 NormalZ=1 AngleXU=0 Radius=0.5
    g56: Circle CenterX=44.63 CenterY=25.78 CenterZ=0 NormalX=0 NormalY=0 NormalZ=1 AngleXU=0 Radius=0.5
    g57: Circle CenterX=44.63 CenterY=23.24 CenterZ=0 NormalX=0 NormalY=0 NormalZ=1 AngleXU=0 Radius=0.5
    g58: Circle CenterX=44.63 CenterY=20.7 CenterZ=0 NormalX=0 NormalY=0 NormalZ=1 AngleXU=0 Radius=0.5
    g59: Circle CenterX=44.63 CenterY=18.16 CenterZ=0 NormalX=0 NormalY=0 NormalZ=1 AngleXU=0 Radius=0.5
    g60: Circle CenterX=44.63 CenterY=15.62 CenterZ=0 NormalX=0 NormalY=0 NormalZ=1 AngleXU=0 Radius=0.5
    g61: Circle CenterX=44.63 CenterY=13.08 CenterZ=0 NormalX=0 NormalY=0 NormalZ=1 AngleXU=0 Radius=0.5
    g62: Circle CenterX=44.63 CenterY=10.54 CenterZ=0 NormalX=0 NormalY=0 NormalZ=1 AngleXU=0 Radius=0.5
    g63: Circle CenterX=44.63 CenterY=8 CenterZ=0 NormalX=0 NormalY=0 NormalZ=1 AngleXU=0 Radius=0.5
    g64: Circle CenterX=44.63 CenterY=5.46 CenterZ=0 NormalX=0 NormalY=0 NormalZ=1 AngleXU=0 Radius=0.5
    g65: Circle CenterX=44.63 CenterY=2.92 CenterZ=0 NormalX=0 NormalY=0 NormalZ=1 AngleXU=0 Radius=0.5
  constraints (152):
    c: Coincident(g0,g1)
    c: Coincident(g1,g2)
    c: Coincident(g2,g3)
    c: Coincident(g3,g0)
    c: Horizontal(g0)
    c: Horizontal(g2)
    c: Vertical(g1)
    c: Vertical(g3)
    c: DistanceX(g0,g0) = 47.35
    c: DistanceY(g1,g1) = 41.4
    c: Coincident(g2,g-1)
    c: Coincident(g4,g5)
    c: Coincident(g5,g6)
    c: Coincident(g6,g7)
    c: Coincident(g7,g8)
    c: Coincident(g8,g9)
    c: Coincident(g9,g10)
    c: Coincident(g10,g11)
    c: Coincident(g11,g12)
    c: Coincident(g12,g13)
    c: Coincident(g13,g14)
    c: Coincident(g14,g15)
    c: Coincident(g15,g16)
    c: Coincident(g16,g17)
    c: Coincident(g18,g19)
    c: Coincident(g19,g20)
    c: Coincident(g20,g21)
    c: Coincident(g21,g22)
    c: Coincident(g22,g23)
    c: Coincident(g23,g24)
    c: Coincident(g24,g25)
    c: Coincident(g25,g26)
    c: Coincident(g26,g27)
    c: Coincident(g27,g28)
    c: Coincident(g28,g29)
    c: Coincident(g29,g30)
    c: Coincident(g30,g31)
    c: Vertical(g17)
    c: Vertical(g16)
    c: Vertical(g15)
    c: Vertical(g14)
    c: Vertical(g13)
    c: Vertical(g12)
    c: Vertical(g11)
    c: Vertical(g10)
    c: Vertical(g9)
    c: Vertical(g8)
    c: Vertical(g7)
    c: Vertical(g6)
    c: Vertical(g5)
    c: Vertical(g4)
    c: Equal(g17,g16)
    c: Equal(g16,g15)
    c: Equal(g15,g14)
    c: Equal(g14,g13)
    c: Equal(g13,g12)
    c: Equal(g12,g11)
    c: Equal(g11,g10)
    c: Equal(g10,g9)
    c: Equal(g9,g8)
    c: Equal(g8,g7)
    c: Equal(g7,g6)
    c: Equal(g6,g5)
    c: Equal(g5,g4)
    c: DistanceY(g4,g4) = 2.54
    c: Vertical(g18)
    c: Vertical(g19)
    c: Vertical(g20)
    c: Vertical(g21)
    c: Vertical(g22)
    c: Vertical(g23)
    c: Vertical(g24)
    c: Vertical(g25)
    c: Vertical(g26)
    c: Vertical(g27)
    c: Vertical(g28)
    c: Vertical(g29)
    c: Vertical(g30)
    c: Vertical(g31)
    c: Equal(g31,g30)
    c: Equal(g30,g29)
    c: Equal(g29,g28)
    c: Equal(g28,g27)
    c: Equal(g27,g26)
    c: Equal(g26,g25)
    c: Equal(g25,g24)
    c: Equal(g24,g23)
    c: Equal(g23,g22)
    c: Equal(g22,g21)
    c: Equal(g21,g20)
    c: Equal(g20,g19)
    c: Equal(g19,g18)
    c: Equal(g18,g4)
    c: DistanceX(g4,g18) = 41.91
    c: Coincident(g33,g1)
    c: Coincident(g33,g18)
    c: Coincident(g4,g32)
    c: Coincident(g32,g2)
    c: Equal(g32,g33)
    c: Coincident(g35,g17)
    c: Coincident(g35,g0)
    c: Coincident(g34,g31)
    c: Coincident(g34,g0)
    c: Equal(g34,g33)
    c: Equal(g33,g35)
    c: Coincident(g50,g4)
    c: Coincident(g49,g4)
    c: Coincident(g48,g5)
    c: Coincident(g47,g6)
    c: Coincident(g46,g7)
    c: Coincident(g45,g8)
    c: Coincident(g44,g9)
    c: Coincident(g43,g10)
    c: Coincident(g42,g11)
    c: Coincident(g41,g12)
    c: Coincident(g40,g13)
    c: Coincident(g39,g14)
    c: Coincident(g38,g15)
    c: Coincident(g37,g16)
    c: Coincident(g36,g17)
    c: Coincident(g65,g18)
    c: Coincident(g64,g18)
    c: Coincident(g63,g19)
    c: Coincident(g62,g20)
    c: Coincident(g61,g21)
    c: Coincident(g60,g22)
    c: Coincident(g59,g23)
    c: Coincident(g58,g24)
    c: Coincident(g57,g25)
    c: Coincident(g56,g26)
    c: Coincident(g55,g27)
    c: Coincident(g54,g28)
    c: Coincident(g53,g29)
    c: Coincident(g52,g30)
    c: Coincident(g51,g31)
    c: Diameter(g36) = 1
    c: Equal(g36, g37-g50) x14
    c: Equal(g36,g65)
    c: Equal(g36,g64)
    c: Equal(g36,g63)
    c: Equal(g36,g62)
    c: Equal(g36,g61)
    c: Equal(g36,g60)
    c: Equal(g36,g59)
    c: Equal(g36,g58)
    c: Equal(g36,g57)
    c: Equal(g36,g56)
    c: Equal(g36,g55)
    c: Equal(g36,g54)
    c: Equal(g36,g53)
    c: Equal(g36,g52)
    c: Equal(g36,g51)
FEATURE [PartDesign::Pad] Pad140
  AllowMultiFace = false
  Direction = (1,1,1)
  Length = 1.6
  Length2 = 100
  Profile = -> Sketch208
  Reversed = true
  Type = 0
FEATURE [PartDesign::Body] Body113  label="PCB002"
  Group = -> [Sketch208,Pad140]
  Origin = -> Origin183
  Tip = -> Pad140
FEATURE [Part::Feature] Shape127  label="J3_PinHeader_1x15_P254mm_Vertical_5F717818"
  Placement = pos=(2.75,38.5,-5.2e-15) rot=(0,0,1;0rad)
  shape: bbox 2.54 x 38.1 x 11.54 mm, 364 faces (baked)
FEATURE [Part::Feature] Shape128  label="J8_PinSocket_1x15_P254mm_Vertical_5F7178B013"
  Placement = pos=(44.65,38.5,4e-15) rot=(0,0,1;0rad)
  shape: bbox 2.54 x 38.1 x 10.1 mm, 475 faces (baked)
FEATURE [Sketcher::SketchObject] Sketch209
  FullyConstrained = false
  MapMode = 5
  Support = -> [XY_Plane184]
  sketch-geometry (1):
    g0: Circle CenterX=0 CenterY=0 CenterZ=0 NormalX=0 NormalY=0 NormalZ=1 AngleXU=0 Radius=4.15
  constraints (2):
    c: Coincident(g0,g-1)
    c: Diameter(g0) = 8.3
FEATURE [PartDesign::Pad] Pad141
  AllowMultiFace = false
  Direction = (1,1,1)
  Length = 10.5
  Length2 = 100
  Profile = -> Sketch209
  Type = 0
FEATURE [PartDesign::Body] Body114  label="Capacitor002"
  Group = -> [Sketch209,Pad141]
  Origin = -> Origin184
  Placement = pos=(10,14.5,-1.6) rot=(0,1,0;3.14159rad)
  Tip = -> Pad141
FEATURE [App::Part] Part014  label="H-bridge002"
  Group = -> [Body113,Shape127,Shape128,Body114]
  Origin = -> Origin182
  Placement = pos=(9.25,8.5,-11.2) rot=(0,0,1;0rad)
FEATURE [App::Part] Part015  label="motor_driver002"
  Group = -> [Board_d4f005,Part014]
  Origin = -> Origin185
  Placement = pos=(61.9,0.4,109.9) rot=(1,0,0;4.71239rad)
FEATURE [Part::Feature] Part__Feature067  label="COMPOUND"
  shape: bbox 43.84 x 21.3 x 19.8 mm, 3099 faces, 84 solids (baked)
FEATURE [App::Part] YAAJ_DCDC_StepDown_LM2596_PinHeaders_cp
  Group = -> [Part__Feature067]
  Origin = -> Origin222
  Placement = pos=(-11,28,-0.05) rot=(0.707107,0.707107,0;3.14159rad)
FEATURE [Part::Feature] Part__Feature068  label="SOLID056"
  shape: bbox 22.32 x 12 x 12.6 mm, 113 faces (baked)
FEATURE [App::Part] PhoenixContact_MSTBA_2_5_4_G_5_08_1x04_P5_08mm_Horizontal  label="PhoenixContact_MSTBA_2,5_4-G-5,08_1x04_P5.08mm_Horizontal"
  Group = -> [Part__Feature068]
  Origin = -> Origin223
  Placement = pos=(-40,95,-0.05) rot=(1,0,0;3.14159rad)
FEATURE [Part::Feature] Part__Feature069  label="SOLID057"
  shape: bbox 12.16 x 12 x 12.6 mm, 63 faces (baked)
FEATURE [App::Part] PhoenixContact_MSTBA_2_5_2_G_5_08_1x02_P5_08mm_Horizontal031  label="PhoenixContact_MSTBA_2,5_2-G-5,08_1x02_P5.08mm_Horizontal031"
  Group = -> [Part__Feature069]
  Origin = -> Origin224
  Placement = pos=(-55,95,-0.05) rot=(1,0,0;3.14159rad)
FEATURE [Part::Feature] Part__Feature070  label="SOLID058"
  shape: bbox 12.16 x 12 x 12.6 mm, 63 faces (baked)
FEATURE [App::Part] PhoenixContact_MSTBA_2_5_2_G_5_08_1x02_P5_08mm_Horizontal032  label="PhoenixContact_MSTBA_2,5_2-G-5,08_1x02_P5.08mm_Horizontal032"
  Group = -> [Part__Feature070]
  Origin = -> Origin225
  Placement = pos=(-70,95,-0.05) rot=(1,0,0;3.14159rad)
FEATURE [Part::Feature] Part__Feature071  label="SOLID059"
  shape: bbox 12.16 x 12 x 12.6 mm, 63 faces (baked)
FEATURE [App::Part] PhoenixContact_MSTBA_2_5_2_G_5_08_1x02_P5_08mm_Horizontal033  label="PhoenixContact_MSTBA_2,5_2-G-5,08_1x02_P5.08mm_Horizontal033"
  Group = -> [Part__Feature071]
  Origin = -> Origin226
  Placement = pos=(-85,95,-0.05) rot=(1,0,0;3.14159rad)
FEATURE [Part::Feature] Part__Feature088  label="COMPOUND005"
  shape: bbox 110 x 100 x 1.6 mm, 66 faces (baked)
FEATURE [App::Part] Open_CASCADE_STEP_translator_7_3_1  label="Open CASCADE STEP translator 7.3 1"
  Group = -> [YAAJ_DCDC_StepDown_LM2596_PinHeaders_cp,PhoenixContact_MSTBA_2_5_4_G_5_08_1x04_P5_08mm_Horizontal,PhoenixContact_MSTBA_2_5_2_G_5_08_1x02_P5_08mm_Horizontal031,PhoenixContact_MSTBA_2_5_2_G_5_08_1x02_P5_08mm_Horizontal032,PhoenixContact_MSTBA_2_5_2_G_5_08_1x02_P5_08mm_Horizontal033,Part__Feature088]
  Origin = -> Origin243
  Placement = pos=(30,15,30) rot=(0,0.707107,0.707107;3.14159rad)
FEATURE [Part::Feature] Part__Feature089  label="SOLID075"
  shape: bbox 6 x 4.9 x 1.75 mm, 156 faces (baked)
FEATURE [Part::Feature] Part__Feature090  label="SOLID076"
  shape: bbox 12.16 x 12 x 12.6 mm, 63 faces (baked)
FEATURE [Part::Feature] Part__Feature091  label="SOLID077"
  shape: bbox 6.3 x 3.2 x 0.6 mm, 26 faces (baked)
FEATURE [Part::Feature] Part__Feature092  label="SOLID078"
  shape: bbox 6.3 x 3.2 x 0.6 mm, 26 faces (baked)
FEATURE [Part::Feature] Part__Feature093  label="SOLID079"
  shape: bbox 2.54 x 10.16 x 11.54 mm, 100 faces (baked)
FEATURE [Part::Feature] Part__Feature095  label="COMPOUND006"
  shape: bbox 24.9 x 30.66 x 17.9 mm, 668 faces, 2 solids (baked)
FEATURE [App::Part] SDDJE30401
  Group = -> [Part__Feature095]
  Origin = -> Origin265
  Placement = pos=(-2.75,72.8,21.8) rot=(0,1,0;3.14159rad)
FEATURE [Part::Feature] Part__Feature096  label="SOLID081"
  shape: bbox 1.6 x 0.8 x 0.45 mm, 26 faces (baked)
FEATURE [Part::Feature] Part__Feature097  label="SOLID082"
  shape: bbox 8 x 14.25 x 0.8 mm, 21 faces (baked)
FEATURE [App::Part] SOIC_8_3_9x4_9mm_P1_27mm003  label="SOIC-8_3.9x4.9mm_P1.27mm003"
  Group = -> [Part__Feature089]
  Origin = -> Origin262
  Placement = pos=(-42,82,1.65) rot=(0,0,1;3.14159rad)
FEATURE [App::Part] R_2512_6332Metric015
  Group = -> [Part__Feature092]
  Origin = -> Origin245
  Placement = pos=(-50,80,1.65) rot=(0,0,-1;1.5708rad)
FEATURE [Part::Feature] Part__Feature101  label="SOLID085"
  shape: bbox 6.3 x 3.2 x 0.6 mm, 26 faces (baked)
FEATURE [App::Part] R_2512_6332Metric016
  Group = -> [Part__Feature101]
  Origin = -> Origin244
  Placement = pos=(-65,80,1.65) rot=(0,0,-1;1.5708rad)
FEATURE [Part::Feature] Part__Feature102  label="SOLID086"
  shape: bbox 8 x 14.25 x 0.8 mm, 21 faces (baked)
FEATURE [App::Part] blade_crimp_PCB002
  Group = -> [Part__Feature102]
  Origin = -> Origin247
  Placement = pos=(-15,55.4,1.65) rot=(1,0,0;1.5708rad)
FEATURE [App::Part] PhoenixContact_MSTBA_2_5_2_G_5_08_1x02_P5_08mm_Horizontal039  label="PhoenixContact_MSTBA_2,5_2-G-5,08_1x02_P5.08mm_Horizontal039"
  Group = -> [Part__Feature090]
  Origin = -> Origin253
  Placement = pos=(-70,95,1.65) rot=(0,0,1;3.14159rad)
FEATURE [App::Part] PinHeader_1x04_P2_54mm_Vertical003  label="PinHeader_1x04_P2.54mm_Vertical003"
  Group = -> [Part__Feature093]
  Origin = -> Origin260
  Placement = pos=(-16,9,1.65) rot=(0,0,1;3.92699rad)
FEATURE [Part::Feature] Part__Feature103  label="COMPOUND008"
  shape: bbox 110 x 100 x 1.6 mm, 66 faces (baked)
FEATURE [Part::Feature] Part__Feature105  label="SOLID088"
  shape: bbox 1.6 x 0.8 x 0.8 mm, 28 faces (baked)
FEATURE [App::Part] C_0603_1608Metric003
  Group = -> [Part__Feature105]
  Origin = -> Origin258
  Placement = pos=(-47,84,1.65) rot=(0,0,1;1.5708rad)
FEATURE [Part::Feature] Part__Feature106  label="SOLID089"
  shape: bbox 12.16 x 12 x 12.6 mm, 63 faces (baked)
FEATURE [Part::Feature] Part__Feature107  label="SOLID090"
  shape: bbox 1.6 x 0.8 x 0.45 mm, 26 faces (baked)
FEATURE [App::Part] blade_crimp_PCB003
  Group = -> [Part__Feature097]
  Origin = -> Origin256
  Placement = pos=(-15,65.4,1.65) rot=(1,0,0;1.5708rad)
FEATURE [App::Part] PhoenixContact_MSTBA_2_5_2_G_5_08_1x02_P5_08mm_Horizontal042  label="PhoenixContact_MSTBA_2,5_2-G-5,08_1x02_P5.08mm_Horizontal042"
  Group = -> [Part__Feature106]
  Origin = -> Origin246
  Placement = pos=(-55,95,1.65) rot=(0,0,1;3.14159rad)
FEATURE [Part::Feature] Part__Feature108  label="SOLID091"
  shape: bbox 12.16 x 12 x 12.6 mm, 63 faces (baked)
FEATURE [App::Part] PhoenixContact_MSTBA_2_5_2_G_5_08_1x02_P5_08mm_Horizontal040  label="PhoenixContact_MSTBA_2,5_2-G-5,08_1x02_P5.08mm_Horizontal040"
  Group = -> [Part__Feature108]
  Origin = -> Origin259
  Placement = pos=(-85,95,1.65) rot=(0,0,1;3.14159rad)
FEATURE [App::Part] R_0603_1608Metric007
  Group = -> [Part__Feature096]
  Origin = -> Origin261
  Placement = pos=(-36,80.5,1.65) rot=(0,0,1;3.14159rad)
FEATURE [Part::Feature] Part__Feature109  label="SOLID092"
  shape: bbox 12.16 x 12 x 12.6 mm, 63 faces (baked)
FEATURE [App::Part] PhoenixContact_MSTBA_2_5_2_G_5_08_1x02_P5_08mm_Horizontal041  label="PhoenixContact_MSTBA_2,5_2-G-5,08_1x02_P5.08mm_Horizontal041"
  Group = -> [Part__Feature109]
  Origin = -> Origin250
  Placement = pos=(-40,95,1.65) rot=(0,0,1;3.14159rad)
FEATURE [App::Part] R_2512_6332Metric018
  Group = -> [Part__Feature091]
  Origin = -> Origin254
  Placement = pos=(-60,80,1.65) rot=(0,0,-1;1.5708rad)
FEATURE [Part::Feature] Part__Feature110  label="SOLID093"
  shape: bbox 6.3 x 3.2 x 0.6 mm, 26 faces (baked)
FEATURE [App::Part] R_2512_6332Metric017
  Group = -> [Part__Feature110]
  Origin = -> Origin249
  Placement = pos=(-55,80,1.65) rot=(0,0,-1;1.5708rad)
FEATURE [App::Part] R_0603_1608Metric008
  Group = -> [Part__Feature107]
  Origin = -> Origin252
  Placement = pos=(-36,82.25,1.65) rot=(0,0,1;3.14159rad)
FEATURE [App::Part] Open_CASCADE_STEP_translator_7_3_1003  label="Open CASCADE STEP translator 7.3 005"
  Group = -> [SOIC_8_3_9x4_9mm_P1_27mm003,SDDJE30401,R_0603_1608Metric008,R_0603_1608Metric007,R_2512_6332Metric017,R_2512_6332Metric018,R_2512_6332Metric015,R_2512_6332Metric016,PhoenixContact_MSTBA_2_5_2_G_5_08_1x02_P5_08mm_Horizontal039,PhoenixContact_MSTBA_2_5_2_G_5_08_1x02_P5_08mm_Horizontal041,PhoenixContact_MSTBA_2_5_2_G_5_08_1x02_P5_08mm_Horizontal042,+6 more]
  Origin = -> Origin251
  Placement = pos=(30,-17,30) rot=(0,0.707107,0.707107;3.14159rad)
FEATURE [Sketcher::SketchObject] Sketch210
  FullyConstrained = false
  MapMode = 5
  Placement = pos=(0,0,0) rot=(1,0,0;1.5708rad)
  Support = -> [XZ_Plane264]
  sketch-geometry (1):
    g0: Circle CenterX=10 CenterY=-1.6 CenterZ=0 NormalX=0 NormalY=0 NormalZ=1 AngleXU=0 Radius=4.1
  constraints (3):
    c: DistanceX(g-1,g0) = 10
    c: DistanceY(g0,g-1) = 1.6
    c: Diameter(g0) = 8.2
FEATURE [PartDesign::Pad] Pad142
  AllowMultiFace = false
  Direction = (1,1,1)
  Length = 12
  Length2 = 100
  Placement = pos=(0,0,0) rot=(1,0,0;1.5708rad)
  Profile = -> Sketch210
  Type = 0
FEATURE [PartDesign::Body] Body115  label="AltCap"
  Group = -> [Sketch210,Pad142]
  Origin = -> Origin266
  Tip = -> Pad142
FEATURE [App::Part] Part  label="H-bridge"
  Group = -> [Body025,Shape041,Shape042,Body026,Body115]
  Origin = -> Origin034
  Placement = pos=(9.25,8.5,-11.2) rot=(0,0,1;0rad)
FEATURE [App::Part] Part001  label="motor_driver"
  Group = -> [Board_d4f3,Part]
  Origin = -> Origin037
  Placement = pos=(-63.1,-30.6,129.9) rot=(0,0.707107,-0.707107;3.14159rad)
FEATURE [Sketcher::SketchObject] Sketch211
  FullyConstrained = false
  MapMode = 5
  Support = -> [XY_Plane267]
  sketch-geometry (8):
    g0: LineSegment StartX=2.75 StartY=1.58771 StartZ=0 EndX=-4e-16 EndY=3.17543 EndZ=0
    g1: LineSegment StartX=-4e-16 StartY=3.17543 StartZ=0 EndX=-2.75 EndY=1.58771 EndZ=0
    g2: LineSegment StartX=-2.75 StartY=1.58771 StartZ=0 EndX=-2.75 EndY=-1.58771 EndZ=0
    g3: LineSegment StartX=-2.75 StartY=-1.58771 StartZ=0 EndX=4e-16 EndY=-3.17543 EndZ=0
    g4: LineSegment StartX=4e-16 StartY=-3.17543 StartZ=0 EndX=2.75 EndY=-1.58771 EndZ=0
    g5: LineSegment StartX=2.75 StartY=-1.58771 StartZ=0 EndX=2.75 EndY=1.58771 EndZ=0
    g6: Circle CenterX=0 CenterY=0 CenterZ=0 NormalX=0 NormalY=0 NormalZ=1 AngleXU=0 Radius=3.17543
    g7: Circle CenterX=0 CenterY=0 CenterZ=0 NormalX=0 NormalY=0 NormalZ=1 AngleXU=0 Radius=1.75
  constraints (18):
    c: Coincident(g0,g1)
    c: Coincident(g1,g2)
    c: Coincident(g2,g3)
    c: Coincident(g3,g4)
    c: Coincident(g4,g5)
    c: Coincident(g5,g0)
    c: Equal(g0, g1-g5) x5
    c: PointOnObject(g0,g6)
    c: PointOnObject(g1,g6)
    c: PointOnObject(g2,g6)
    c: PointOnObject(g3,g6)
    c: PointOnObject(g4,g6)
    c: PointOnObject(g5,g6)
    c: Coincident(g6,g-1)
    c: Vertical(g5)
    c: Distance(g1,g0) = 5.5
    c: Coincident(g7,g-1)
    c: Diameter(g7) = 3.5
FEATURE [PartDesign::Pad] Pad143
  AllowMultiFace = false
  Direction = (1,1,1)
  Length = 16
  Length2 = 100
  Profile = -> Sketch211
  Type = 0
FEATURE [PartDesign::Body] Body116  label="16mm Standoff003"
  Group = -> [Sketch211,Pad143]
  Origin = -> Origin267
  Placement = pos=(67,-13,126) rot=(1,0,0;1.5708rad)
  Tip = -> Pad143
FEATURE [Sketcher::SketchObject] Sketch212
  FullyConstrained = false
  MapMode = 5
  Support = -> [XY_Plane268]
  sketch-geometry (8):
    g0: LineSegment StartX=2.75 StartY=1.58771 StartZ=0 EndX=-4e-16 EndY=3.17543 EndZ=0
    g1: LineSegment StartX=-4e-16 StartY=3.17543 StartZ=0 EndX=-2.75 EndY=1.58771 EndZ=0
    g2: LineSegment StartX=-2.75 StartY=1.58771 StartZ=0 EndX=-2.75 EndY=-1.58771 EndZ=0
    g3: LineSegment StartX=-2.75 StartY=-1.58771 StartZ=0 EndX=4e-16 EndY=-3.17543 EndZ=0
    g4: LineSegment StartX=4e-16 StartY=-3.17543 StartZ=0 EndX=2.75 EndY=-1.58771 EndZ=0
    g5: LineSegment StartX=2.75 StartY=-1.58771 StartZ=0 EndX=2.75 EndY=1.58771 EndZ=0
    g6: Circle CenterX=0 CenterY=0 CenterZ=0 NormalX=0 NormalY=0 NormalZ=1 AngleXU=0 Radius=3.17543
    g7: Circle CenterX=0 CenterY=0 CenterZ=0 NormalX=0 NormalY=0 NormalZ=1 AngleXU=0 Radius=1.75
  constraints (18):
    c: Coincident(g0,g1)
    c: Coincident(g1,g2)
    c: Coincident(g2,g3)
    c: Coincident(g3,g4)
    c: Coincident(g4,g5)
    c: Coincident(g5,g0)
    c: Equal(g0, g1-g5) x5
    c: PointOnObject(g0,g6)
    c: PointOnObject(g1,g6)
    c: PointOnObject(g2,g6)
    c: PointOnObject(g3,g6)
    c: PointOnObject(g4,g6)
    c: PointOnObject(g5,g6)
    c: Coincident(g6,g-1)
    c: Vertical(g5)
    c: Distance(g1,g0) = 5.5
    c: Coincident(g7,g-1)
    c: Diameter(g7) = 3.5
FEATURE [PartDesign::Pad] Pad144
  AllowMultiFace = false
  Direction = (1,1,1)
  Length = 16
  Length2 = 100
  Profile = -> Sketch212
  Type = 0
FEATURE [PartDesign::Body] Body117  label="16mm Standoff004"
  Group = -> [Sketch212,Pad144]
  Origin = -> Origin268
  Placement = pos=(125,-13,126) rot=(1,0,0;1.5708rad)
  Tip = -> Pad144
FEATURE [Sketcher::SketchObject] Sketch213
  FullyConstrained = false
  MapMode = 5
  Support = -> [XY_Plane269]
  sketch-geometry (8):
    g0: LineSegment StartX=2.75 StartY=1.58771 StartZ=0 EndX=-4e-16 EndY=3.17543 EndZ=0
    g1: LineSegment StartX=-4e-16 StartY=3.17543 StartZ=0 EndX=-2.75 EndY=1.58771 EndZ=0
    g2: LineSegment StartX=-2.75 StartY=1.58771 StartZ=0 EndX=-2.75 EndY=-1.58771 EndZ=0
    g3: LineSegment StartX=-2.75 StartY=-1.58771 StartZ=0 EndX=4e-16 EndY=-3.17543 EndZ=0
    g4: LineSegment StartX=4e-16 StartY=-3.17543 StartZ=0 EndX=2.75 EndY=-1.58771 EndZ=0
    g5: LineSegment StartX=2.75 StartY=-1.58771 StartZ=0 EndX=2.75 EndY=1.58771 EndZ=0
    g6: Circle CenterX=0 CenterY=0 CenterZ=0 NormalX=0 NormalY=0 NormalZ=1 AngleXU=0 Radius=3.17543
    g7: Circle CenterX=0 CenterY=0 CenterZ=0 NormalX=0 NormalY=0 NormalZ=1 AngleXU=0 Radius=1.75
  constraints (18):
    c: Coincident(g0,g1)
    c: Coincident(g1,g2)
    c: Coincident(g2,g3)
    c: Coincident(g3,g4)
    c: Coincident(g4,g5)
    c: Coincident(g5,g0)
    c: Equal(g0, g1-g5) x5
    c: PointOnObject(g0,g6)
    c: PointOnObject(g1,g6)
    c: PointOnObject(g2,g6)
    c: PointOnObject(g3,g6)
    c: PointOnObject(g4,g6)
    c: PointOnObject(g5,g6)
    c: Coincident(g6,g-1)
    c: Vertical(g5)
    c: Distance(g1,g0) = 5.5
    c: Coincident(g7,g-1)
    c: Diameter(g7) = 3.5
FEATURE [PartDesign::Pad] Pad145
  AllowMultiFace = false
  Direction = (1,1,1)
  Length = 16
  Length2 = 100
  Profile = -> Sketch213
  Type = 0
FEATURE [PartDesign::Body] Body118  label="16mm Standoff005"
  Group = -> [Sketch213,Pad145]
  Origin = -> Origin269
  Placement = pos=(125,-13,84) rot=(1,0,0;1.5708rad)
  Tip = -> Pad145
FEATURE [Part::Feature] Shape129  label="U4_SOIC_8_39x49mm_P127mm_5F717A080"
  Placement = pos=(40.25,11.5,0) rot=(0,0,1;0rad)
  shape: bbox 6 x 4.9 x 1.75 mm, 156 faces (baked)
FEATURE [Part::Feature] Shape130  label="U3_LQFP_32_7x7mm_P08mm_5F71845B003"
  Placement = pos=(36.5,25.5,0) rot=(0,0,-1;1.5708rad)
  shape: bbox 9 x 9 x 1.5 mm, 516 faces (baked)
FEATURE [Part::Feature] Shape131  label="C8_C_0603_1608Metric_5F7555CB003"
  Placement = pos=(26,13,0) rot=(0,0,1;3.14159rad)
  shape: bbox 1.6 x 0.8 x 0.8 mm, 28 faces (baked)
FEATURE [Part::Feature] Shape132  label="U5_SOT_23_5_5F717A8C003"
  Placement = pos=(4.5,23,0) rot=(0,0,1;1.5708rad)
  shape: bbox 2.9 x 2.8 x 1.55 mm, 109 faces (baked)
FEATURE [Part::Feature] Shape133  label="C9_C_0603_1608Metric_5F754EF012"
  Placement = pos=(26,17.5,0) rot=(0,0,1;3.14159rad)
  shape: bbox 1.6 x 0.8 x 0.8 mm, 28 faces (baked)
FEATURE [Part::Feature] Shape134  label="J3_PinHeader_1x15_P254mm_Vertical_5F717819"
  Placement = pos=(54,47,-1.6) rot=(0,1,0;3.14159rad)
  shape: bbox 2.54 x 38.1 x 11.54 mm, 364 faces (baked)
FEATURE [PartDesign::CoordinateSystem] Local_CS_d4f006
  AttacherType = Attacher::AttachEngine3D
FEATURE [Part::Feature] Pcb_d4f006
  Placement = pos=(-90,100,0) rot=(0,0,1;0rad)
  shape: bbox 66 x 50 x 1.6 mm, 84 faces (baked)
FEATURE [Sketcher::SketchObject] PCB_Sketch_d4f006
  FullyConstrained = false
  sketch-geometry (8):
    g0: LineSegment StartX=4e-16 StartY=3 StartZ=0 EndX=-3.6e-15 EndY=47 EndZ=0
    g1: LineSegment StartX=63 StartY=8.4e-15 StartZ=0 EndX=3 EndY=4e-16 EndZ=0
    g2: LineSegment StartX=66 StartY=47 StartZ=0 EndX=66 EndY=3 EndZ=0
    g3: LineSegment StartX=3 StartY=50 StartZ=0 EndX=63 EndY=50 EndZ=0
    g4: ArcOfCircle CenterX=63 CenterY=47 CenterZ=0 NormalX=0 NormalY=0 NormalZ=1 AngleXU=0 Radius=3 StartAngle=0 EndAngle=1.5708
    g5: ArcOfCircle CenterX=63 CenterY=3 CenterZ=0 NormalX=0 NormalY=0 NormalZ=1 AngleXU=0 Radius=3 StartAngle=4.71239 EndAngle=6.28319
    g6: ArcOfCircle CenterX=3 CenterY=3 CenterZ=0 NormalX=0 NormalY=0 NormalZ=1 AngleXU=0 Radius=3 StartAngle=3.14159 EndAngle=4.71239
    g7: ArcOfCircle CenterX=3 CenterY=47 CenterZ=0 NormalX=0 NormalY=0 NormalZ=1 AngleXU=0 Radius=3 StartAngle=1.5708 EndAngle=3.14159
  constraints (8):
    c: Coincident(g0,g6)
    c: Coincident(g0,g7)
    c: Coincident(g1,g6)
    c: Coincident(g3,g7)
    c: Coincident(g1,g5)
    c: Coincident(g3,g4)
    c: Coincident(g2,g5)
    c: Coincident(g2,g4)
FEATURE [App::Part] Board_Geoms_d4f006  label="Board_Geoms_d4f009"
  Group = -> [Local_CS_d4f006,Pcb_d4f006,PCB_Sketch_d4f006]
  Origin = -> Origin270
FEATURE [Part::Feature] Shape135  label="U2_SOT_353_SC_70_5_5F717A015"
  Placement = pos=(26,15.25,0) rot=(0,0,1;3.14159rad)
  shape: bbox 2 x 2 x 1.05 mm, 104 faces (baked)
FEATURE [Part::Feature] Shape136  label="U1_SOT_353_SC_70_5_5F7179FD003"
  Placement = pos=(26,19.75,0) rot=(0,0,1;3.14159rad)
  shape: bbox 2 x 2 x 1.05 mm, 104 faces (baked)
FEATURE [Part::Feature] Shape137  label="SW1_SW_PUSH_6mm_5F7179E011"
  Placement = pos=(41.5,37.75,0) rot=(0,0,1;3.14159rad)
  shape: bbox 7.174 x 6 x 7.8 mm, 105 faces (baked)
FEATURE [Part::Feature] Shape138  label="R7_R_0603_1608Metric_5F7179C012"
  Placement = pos=(44.25,36.5,0) rot=(0,0,1;1.5708rad)
  shape: bbox 0.8 x 1.6 x 0.45 mm, 26 faces (baked)
FEATURE [Part::Feature] Shape139  label="R6_R_0603_1608Metric_5F7179B011"
  Placement = pos=(33.25,15.75,0) rot=(0,0,1;1.5708rad)
  shape: bbox 0.8 x 1.6 x 0.45 mm, 26 faces (baked)
FEATURE [Part::Feature] Shape140  label="R5_R_0603_1608Metric_5F7179A010"
  Placement = pos=(30.75,15.75,0) rot=(0,0,1;1.5708rad)
  shape: bbox 0.8 x 1.6 x 0.45 mm, 26 faces (baked)
FEATURE [Part::Feature] Shape141  label="R4_R_0603_1608Metric_5F717999"
  Placement = pos=(15.175,35.57,0) rot=(0,0,1;3.14159rad)
  shape: bbox 1.6 x 0.8 x 0.45 mm, 26 faces (baked)
FEATURE [Part::Feature] Shape142  label="R3_R_0603_1608Metric_5F717988"
  Placement = pos=(15.175,38.11,0) rot=(0,0,1;3.14159rad)
  shape: bbox 1.6 x 0.8 x 0.45 mm, 26 faces (baked)
FEATURE [Part::Feature] Shape143  label="R2_R_0603_1608Metric_5F717977"
  Placement = pos=(15.175,40.65,0) rot=(0,0,1;3.14159rad)
  shape: bbox 1.6 x 0.8 x 0.45 mm, 26 faces (baked)
FEATURE [Part::Feature] Shape144  label="R1_R_0603_1608Metric_5F717966"
  Placement = pos=(15.175,43.19,0) rot=(0,0,1;3.14159rad)
  shape: bbox 1.6 x 0.8 x 0.45 mm, 26 faces (baked)
FEATURE [Part::Feature] Shape145  label="J13_MSTBA_01x02_G_5_08mm_5F717955"
  Placement = pos=(44,3.5,0) rot=(0,0,1;0rad)
  shape: bbox 12.16 x 12 x 12.6 mm, 63 faces (baked)
FEATURE [Part::Feature] Shape146  label="J12_PinHeader_1x06_P254mm_Vertical_5F71792E003"
  Placement = pos=(34.95,46.25,0) rot=(0,0,1;1.5708rad)
  shape: bbox 15.24 x 2.54 x 11.54 mm, 148 faces (baked)
FEATURE [Part::Feature] Shape147  label="J11_PinHeader_1x03_P254mm_Vertical_5F717917"
  Placement = pos=(1.84,13.98,0) rot=(0,0,1;1.5708rad)
  shape: bbox 7.62 x 2.54 x 11.54 mm, 76 faces (baked)
FEATURE [Part::Feature] Shape148  label="J10_PinHeader_1x03_P254mm_Vertical_5F7178FD003"
  Placement = pos=(1.84,16.52,0) rot=(0,0,1;1.5708rad)
  shape: bbox 7.62 x 2.54 x 11.54 mm, 76 faces (baked)
FEATURE [Part::Feature] Shape149  label="J9_MSTBA_01x04_G_5_08mm_5F7178E009"
  Placement = pos=(20.5,3.5,0) rot=(0,0,1;0rad)
  shape: bbox 22.32 x 12 x 12.6 mm, 113 faces (baked)
FEATURE [Part::Feature] Shape150  label="J8_PinSocket_1x15_P254mm_Vertical_5F7178B014"
  Placement = pos=(12,47,-1.6) rot=(0,1,0;3.14159rad)
  shape: bbox 2.54 x 38.1 x 10.1 mm, 475 faces (baked)
FEATURE [App::Part] Bot_d4f006  label="Bot_d4f009"
  Group = -> [Shape134,Shape150]
  Origin = -> Origin274
FEATURE [Part::Feature] Shape151  label="J7_SHF-105-01-L-D-SM-K-TR_5F717898"
  Placement = pos=(48,17.25,0) rot=(0.57735,0.57735,0.57735;2.0944rad)
  shape: bbox 6.502 x 12.7 x 5.588 mm, 207 faces, 4 solids (baked)
FEATURE [Part::Feature] Shape152  label="J6_PinHeader_1x03_P254mm_Vertical_5F717878"
  Placement = pos=(1.84,33.03,0) rot=(0,0,1;1.5708rad)
  shape: bbox 7.62 x 2.54 x 11.54 mm, 76 faces (baked)
FEATURE [Part::Feature] Shape153  label="J5_PinHeader_1x03_P254mm_Vertical_5F723000"
  Placement = pos=(1.84,35.57,0) rot=(0,0,1;1.5708rad)
  shape: bbox 7.62 x 2.54 x 11.54 mm, 76 faces (baked)
FEATURE [Part::Feature] Shape154  label="J4_Molex_AE_6410_06A_5F717850"
  Placement = pos=(61.62,35.57,0) rot=(0,0,-1;1.5708rad)
  shape: bbox 5.8 x 15.24 x 15.26 mm, 169 faces (baked)
FEATURE [Part::Feature] Shape155  label="J2_PinHeader_1x03_P254mm_Vertical_5F7177F003"
  Placement = pos=(1.84,38.11,0) rot=(0,0,1;1.5708rad)
  shape: bbox 7.62 x 2.54 x 11.54 mm, 76 faces (baked)
FEATURE [Part::Feature] Shape156  label="J1_PinHeader_1x03_P254mm_Vertical_5F7228CA003"
  Placement = pos=(1.84,40.65,0) rot=(0,0,1;1.5708rad)
  shape: bbox 7.62 x 2.54 x 11.54 mm, 76 faces (baked)
FEATURE [Part::Feature] Shape157  label="D6_LED_0603_1608Metric_5F71855F003"
  Placement = pos=(33.25,12.25,0) rot=(0,0,1;1.5708rad)
  shape: bbox 0.8 x 1.6 x 1.1 mm, 50 faces (baked)
FEATURE [Part::Feature] Shape158  label="D5_LED_0603_1608Metric_5F71778F003"
  Placement = pos=(30.75,12.25,0) rot=(0,0,1;1.5708rad)
  shape: bbox 0.8 x 1.6 x 1.1 mm, 50 faces (baked)
FEATURE [Part::Feature] Shape159  label="D4_SOT_23_5F71777C003"
  Placement = pos=(18.985,35.57,0) rot=(0,0,1;0rad)
  shape: bbox 2.5 x 3 x 1.2 mm, 76 faces (baked)
FEATURE [Part::Feature] Shape160  label="D3_SOT_23_5F717770"
  Placement = pos=(22.795,38.11,0) rot=(0,0,1;0rad)
  shape: bbox 2.5 x 3 x 1.2 mm, 76 faces (baked)
FEATURE [Part::Feature] Shape161  label="D2_SOT_23_5F717755"
  Placement = pos=(18.985,40.65,0) rot=(0,0,1;0rad)
  shape: bbox 2.5 x 3 x 1.2 mm, 76 faces (baked)
FEATURE [Part::Feature] Shape162  label="D1_SOT_23_5F71773D003"
  Placement = pos=(22.795,43.19,0) rot=(0,0,1;0rad)
  shape: bbox 2.5 x 3 x 1.2 mm, 76 faces (baked)
FEATURE [Part::Feature] Shape163  label="C7_C_0603_1608Metric_5F717731"
  Placement = pos=(4.5,27.5,0) rot=(0,0,1;0rad)
  shape: bbox 1.6 x 0.8 x 0.8 mm, 28 faces (baked)
FEATURE [Part::Feature] Shape164  label="C6_C_0603_1608Metric_5F717720"
  Placement = pos=(6.25,25.75,0) rot=(0,0,1;0rad)
  shape: bbox 1.6 x 0.8 x 0.8 mm, 28 faces (baked)
FEATURE [Part::Feature] Shape165  label="C5_C_0603_1608Metric_5F717709"
  Placement = pos=(4.5,20.25,0) rot=(0,0,1;0rad)
  shape: bbox 1.6 x 0.8 x 0.8 mm, 28 faces (baked)
FEATURE [Part::Feature] Shape166  label="C4_C_0603_1608Metric_5F7176F008"
  Placement = pos=(41.5,15.25,0) rot=(0,0,1;0rad)
  shape: bbox 1.6 x 0.8 x 0.8 mm, 28 faces (baked)
FEATURE [Part::Feature] Shape167  label="C3_C_0603_1608Metric_5F7176E007"
  Placement = pos=(32.5,39.75,0) rot=(0,0,1;1.5708rad)
  shape: bbox 0.8 x 1.6 x 0.8 mm, 28 faces (baked)
FEATURE [Part::Feature] Shape168  label="C2_C_0603_1608Metric_5F7176D006"
  Placement = pos=(38.25,33,0) rot=(0,0,1;0rad)
  shape: bbox 1.6 x 0.8 x 0.8 mm, 28 faces (baked)
FEATURE [Part::Feature] Shape169  label="C1_C_0805_2012Metric_5F7176C005"
  Placement = pos=(38.25,35,0) rot=(0,0,1;0rad)
  shape: bbox 2 x 1.25 x 1.25 mm, 28 faces (baked)
FEATURE [App::Part] Top_d4f006  label="Top_d4f009"
  Group = -> [Shape133,Shape131,Shape132,Shape129,Shape130,Shape135,Shape136,Shape137,Shape138,Shape139,Shape140,Shape141,Shape142,Shape143,Shape144,Shape145,Shape146,Shape147,Shape148,Shape149,Shape151,Shape152,Shape153,Shape154,Shape155,Shape156,Shape157,Shape158,Shape159,Shape160,Shape161,Shape162,Shape163,Shape164,Shape165,Shape166,Shape167,Shape168,Shape169]
  Origin = -> Origin273
FEATURE [App::Part] Step_Models_d4f006  label="Step_Models_d4f009"
  Group = -> [Top_d4f006,Bot_d4f006]
  Origin = -> Origin272
FEATURE [App::Part] Board_d4f006  label="motor_board003"
  Group = -> [Board_Geoms_d4f006,Step_Models_d4f006]
  Origin = -> Origin271
FEATURE [Sketcher::SketchObject] Sketch214
  FullyConstrained = false
  MapMode = 5
  Support = -> [XY_Plane276]
  sketch-geometry (66):
    g0: LineSegment StartX=0 StartY=41.4 StartZ=0 EndX=47.35 EndY=41.4 EndZ=0
    g1: LineSegment StartX=47.35 StartY=41.4 StartZ=0 EndX=47.35 EndY=0 EndZ=0
    g2: LineSegment StartX=47.35 StartY=0 StartZ=0 EndX=0 EndY=0 EndZ=0
    g3: LineSegment StartX=0 StartY=0 StartZ=0 EndX=0 EndY=41.4 EndZ=0
    g4: LineSegment StartX=2.72 StartY=2.92 StartZ=0 EndX=2.72 EndY=5.46 EndZ=0
    g5: LineSegment StartX=2.72 StartY=5.46 StartZ=0 EndX=2.72 EndY=8 EndZ=0
    g6: LineSegment StartX=2.72 StartY=8 StartZ=0 EndX=2.72 EndY=10.54 EndZ=0
    g7: LineSegment StartX=2.72 StartY=10.54 StartZ=0 EndX=2.72 EndY=13.08 EndZ=0
    g8: LineSegment StartX=2.72 StartY=13.08 StartZ=0 EndX=2.72 EndY=15.62 EndZ=0
    g9: LineSegment StartX=2.72 StartY=15.62 StartZ=0 EndX=2.72 EndY=18.16 EndZ=0
    g10: LineSegment StartX=2.72 StartY=18.16 StartZ=0 EndX=2.72 EndY=20.7 EndZ=0
    g11: LineSegment StartX=2.72 StartY=20.7 StartZ=0 EndX=2.72 EndY=23.24 EndZ=0
    g12: LineSegment StartX=2.72 StartY=23.24 StartZ=0 EndX=2.72 EndY=25.78 EndZ=0
    g13: LineSegment StartX=2.72 StartY=25.78 StartZ=0 EndX=2.72 EndY=28.32 EndZ=0
    g14: LineSegment StartX=2.72 StartY=28.32 StartZ=0 EndX=2.72 EndY=30.86 EndZ=0
    g15: LineSegment StartX=2.72 StartY=30.86 StartZ=0 EndX=2.72 EndY=33.4 EndZ=0
    g16: LineSegment StartX=2.72 StartY=33.4 StartZ=0 EndX=2.72 EndY=35.94 EndZ=0
    g17: LineSegment StartX=2.72 StartY=35.94 StartZ=0 EndX=2.72 EndY=38.48 EndZ=0
    g18: LineSegment StartX=44.63 StartY=2.92 StartZ=0 EndX=44.63 EndY=5.46 EndZ=0
    g19: LineSegment StartX=44.63 StartY=5.46 StartZ=0 EndX=44.63 EndY=8 EndZ=0
    g20: LineSegment StartX=44.63 StartY=8 StartZ=0 EndX=44.63 EndY=10.54 EndZ=0
    g21: LineSegment StartX=44.63 StartY=10.54 StartZ=0 EndX=44.63 EndY=13.08 EndZ=0
    g22: LineSegment StartX=44.63 StartY=13.08 StartZ=0 EndX=44.63 EndY=15.62 EndZ=0
    g23: LineSegment StartX=44.63 StartY=15.62 StartZ=0 EndX=44.63 EndY=18.16 EndZ=0
    g24: LineSegment StartX=44.63 StartY=18.16 StartZ=0 EndX=44.63 EndY=20.7 EndZ=0
    g25: LineSegment StartX=44.63 StartY=20.7 StartZ=0 EndX=44.63 EndY=23.24 EndZ=0
    g26: LineSegment StartX=44.63 StartY=23.24 StartZ=0 EndX=44.63 EndY=25.78 EndZ=0
    g27: LineSegment StartX=44.63 StartY=25.78 StartZ=0 EndX=44.63 EndY=28.32 EndZ=0
    g28: LineSegment StartX=44.63 StartY=28.32 StartZ=0 EndX=44.63 EndY=30.86 EndZ=0
    g29: LineSegment StartX=44.63 StartY=30.86 StartZ=0 EndX=44.63 EndY=33.4 EndZ=0
    g30: LineSegment StartX=44.63 StartY=33.4 StartZ=0 EndX=44.63 EndY=35.94 EndZ=0
    g31: LineSegment StartX=44.63 StartY=35.94 StartZ=0 EndX=44.63 EndY=38.48 EndZ=0
    g32: LineSegment StartX=0 StartY=0 StartZ=0 EndX=2.72 EndY=2.92 EndZ=0
    g33: LineSegment StartX=44.63 StartY=2.92 StartZ=0 EndX=47.35 EndY=0 EndZ=0
    g34: LineSegment StartX=44.63 StartY=38.48 StartZ=0 EndX=47.35 EndY=41.4 EndZ=0
    g35: LineSegment StartX=2.72 StartY=38.48 StartZ=0 EndX=0 EndY=41.4 EndZ=0
    g36: Circle CenterX=2.72 CenterY=38.48 CenterZ=0 NormalX=0 NormalY=0 NormalZ=1 AngleXU=0 Radius=0.5
    g37: Circle CenterX=2.72 CenterY=35.94 CenterZ=0 NormalX=0 NormalY=0 NormalZ=1 AngleXU=0 Radius=0.5
    g38: Circle CenterX=2.72 CenterY=33.4 CenterZ=0 NormalX=0 NormalY=0 NormalZ=1 AngleXU=0 Radius=0.5
    g39: Circle CenterX=2.72 CenterY=30.86 CenterZ=0 NormalX=0 NormalY=0 NormalZ=1 AngleXU=0 Radius=0.5
    g40: Circle CenterX=2.72 CenterY=28.32 CenterZ=0 NormalX=0 NormalY=0 NormalZ=1 AngleXU=0 Radius=0.5
    g41: Circle CenterX=2.72 CenterY=25.78 CenterZ=0 NormalX=0 NormalY=0 NormalZ=1 AngleXU=0 Radius=0.5
    g42: Circle CenterX=2.72 CenterY=23.24 CenterZ=0 NormalX=0 NormalY=0 NormalZ=1 AngleXU=0 Radius=0.5
    g43: Circle CenterX=2.72 CenterY=20.7 CenterZ=0 NormalX=0 NormalY=0 NormalZ=1 AngleXU=0 Radius=0.5
    g44: Circle CenterX=2.72 CenterY=18.16 CenterZ=0 NormalX=0 NormalY=0 NormalZ=1 AngleXU=0 Radius=0.5
    g45: Circle CenterX=2.72 CenterY=15.62 CenterZ=0 NormalX=0 NormalY=0 NormalZ=1 AngleXU=0 Radius=0.5
    g46: Circle CenterX=2.72 CenterY=13.08 CenterZ=0 NormalX=0 NormalY=0 NormalZ=1 AngleXU=0 Radius=0.5
    g47: Circle CenterX=2.72 CenterY=10.54 CenterZ=0 NormalX=0 NormalY=0 NormalZ=1 AngleXU=0 Radius=0.5
    g48: Circle CenterX=2.72 CenterY=8 CenterZ=0 NormalX=0 NormalY=0 NormalZ=1 AngleXU=0 Radius=0.5
    g49: Circle CenterX=2.72 CenterY=5.46 CenterZ=0 NormalX=0 NormalY=0 NormalZ=1 AngleXU=0 Radius=0.5
    g50: Circle CenterX=2.72 CenterY=2.92 CenterZ=0 NormalX=0 NormalY=0 NormalZ=1 AngleXU=0 Radius=0.5
    g51: Circle CenterX=44.63 CenterY=38.48 CenterZ=0 NormalX=0 NormalY=0 NormalZ=1 AngleXU=0 Radius=0.5
    g52: Circle CenterX=44.63 CenterY=35.94 CenterZ=0 NormalX=0 NormalY=0 NormalZ=1 AngleXU=0 Radius=0.5
    g53: Circle CenterX=44.63 CenterY=33.4 CenterZ=0 NormalX=0 NormalY=0 NormalZ=1 AngleXU=0 Radius=0.5
    g54: Circle CenterX=44.63 CenterY=30.86 CenterZ=0 NormalX=0 NormalY=0 NormalZ=1 AngleXU=0 Radius=0.5
    g55: Circle CenterX=44.63 CenterY=28.32 CenterZ=0 NormalX=0 NormalY=0 NormalZ=1 AngleXU=0 Radius=0.5
    g56: Circle CenterX=44.63 CenterY=25.78 CenterZ=0 NormalX=0 NormalY=0 NormalZ=1 AngleXU=0 Radius=0.5
    g57: Circle CenterX=44.63 CenterY=23.24 CenterZ=0 NormalX=0 NormalY=0 NormalZ=1 AngleXU=0 Radius=0.5
    g58: Circle CenterX=44.63 CenterY=20.7 CenterZ=0 NormalX=0 NormalY=0 NormalZ=1 AngleXU=0 Radius=0.5
    g59: Circle CenterX=44.63 CenterY=18.16 CenterZ=0 NormalX=0 NormalY=0 NormalZ=1 AngleXU=0 Radius=0.5
    g60: Circle CenterX=44.63 CenterY=15.62 CenterZ=0 NormalX=0 NormalY=0 NormalZ=1 AngleXU=0 Radius=0.5
    g61: Circle CenterX=44.63 CenterY=13.08 CenterZ=0 NormalX=0 NormalY=0 NormalZ=1 AngleXU=0 Radius=0.5
    g62: Circle CenterX=44.63 CenterY=10.54 CenterZ=0 NormalX=0 NormalY=0 NormalZ=1 AngleXU=0 Radius=0.5
    g63: Circle CenterX=44.63 CenterY=8 CenterZ=0 NormalX=0 NormalY=0 NormalZ=1 AngleXU=0 Radius=0.5
    g64: Circle CenterX=44.63 CenterY=5.46 CenterZ=0 NormalX=0 NormalY=0 NormalZ=1 AngleXU=0 Radius=0.5
    g65: Circle CenterX=44.63 CenterY=2.92 CenterZ=0 NormalX=0 NormalY=0 NormalZ=1 AngleXU=0 Radius=0.5
  constraints (152):
    c: Coincident(g0,g1)
    c: Coincident(g1,g2)
    c: Coincident(g2,g3)
    c: Coincident(g3,g0)
    c: Horizontal(g0)
    c: Horizontal(g2)
    c: Vertical(g1)
    c: Vertical(g3)
    c: DistanceX(g0,g0) = 47.35
    c: DistanceY(g1,g1) = 41.4
    c: Coincident(g2,g-1)
    c: Coincident(g4,g5)
    c: Coincident(g5,g6)
    c: Coincident(g6,g7)
    c: Coincident(g7,g8)
    c: Coincident(g8,g9)
    c: Coincident(g9,g10)
    c: Coincident(g10,g11)
    c: Coincident(g11,g12)
    c: Coincident(g12,g13)
    c: Coincident(g13,g14)
    c: Coincident(g14,g15)
    c: Coincident(g15,g16)
    c: Coincident(g16,g17)
    c: Coincident(g18,g19)
    c: Coincident(g19,g20)
    c: Coincident(g20,g21)
    c: Coincident(g21,g22)
    c: Coincident(g22,g23)
    c: Coincident(g23,g24)
    c: Coincident(g24,g25)
    c: Coincident(g25,g26)
    c: Coincident(g26,g27)
    c: Coincident(g27,g28)
    c: Coincident(g28,g29)
    c: Coincident(g29,g30)
    c: Coincident(g30,g31)
    c: Vertical(g17)
    c: Vertical(g16)
    c: Vertical(g15)
    c: Vertical(g14)
    c: Vertical(g13)
    c: Vertical(g12)
    c: Vertical(g11)
    c: Vertical(g10)
    c: Vertical(g9)
    c: Vertical(g8)
    c: Vertical(g7)
    c: Vertical(g6)
    c: Vertical(g5)
    c: Vertical(g4)
    c: Equal(g17,g16)
    c: Equal(g16,g15)
    c: Equal(g15,g14)
    c: Equal(g14,g13)
    c: Equal(g13,g12)
    c: Equal(g12,g11)
    c: Equal(g11,g10)
    c: Equal(g10,g9)
    c: Equal(g9,g8)
    c: Equal(g8,g7)
    c: Equal(g7,g6)
    c: Equal(g6,g5)
    c: Equal(g5,g4)
    c: DistanceY(g4,g4) = 2.54
    c: Vertical(g18)
    c: Vertical(g19)
    c: Vertical(g20)
    c: Vertical(g21)
    c: Vertical(g22)
    c: Vertical(g23)
    c: Vertical(g24)
    c: Vertical(g25)
    c: Vertical(g26)
    c: Vertical(g27)
    c: Vertical(g28)
    c: Vertical(g29)
    c: Vertical(g30)
    c: Vertical(g31)
    c: Equal(g31,g30)
    c: Equal(g30,g29)
    c: Equal(g29,g28)
    c: Equal(g28,g27)
    c: Equal(g27,g26)
    c: Equal(g26,g25)
    c: Equal(g25,g24)
    c: Equal(g24,g23)
    c: Equal(g23,g22)
    c: Equal(g22,g21)
    c: Equal(g21,g20)
    c: Equal(g20,g19)
    c: Equal(g19,g18)
    c: Equal(g18,g4)
    c: DistanceX(g4,g18) = 41.91
    c: Coincident(g33,g1)
    c: Coincident(g33,g18)
    c: Coincident(g4,g32)
    c: Coincident(g32,g2)
    c: Equal(g32,g33)
    c: Coincident(g35,g17)
    c: Coincident(g35,g0)
    c: Coincident(g34,g31)
    c: Coincident(g34,g0)
    c: Equal(g34,g33)
    c: Equal(g33,g35)
    c: Coincident(g50,g4)
    c: Coincident(g49,g4)
    c: Coincident(g48,g5)
    c: Coincident(g47,g6)
    c: Coincident(g46,g7)
    c: Coincident(g45,g8)
    c: Coincident(g44,g9)
    c: Coincident(g43,g10)
    c: Coincident(g42,g11)
    c: Coincident(g41,g12)
    c: Coincident(g40,g13)
    c: Coincident(g39,g14)
    c: Coincident(g38,g15)
    c: Coincident(g37,g16)
    c: Coincident(g36,g17)
    c: Coincident(g65,g18)
    c: Coincident(g64,g18)
    c: Coincident(g63,g19)
    c: Coincident(g62,g20)
    c: Coincident(g61,g21)
    c: Coincident(g60,g22)
    c: Coincident(g59,g23)
    c: Coincident(g58,g24)
    c: Coincident(g57,g25)
    c: Coincident(g56,g26)
    c: Coincident(g55,g27)
    c: Coincident(g54,g28)
    c: Coincident(g53,g29)
    c: Coincident(g52,g30)
    c: Coincident(g51,g31)
    c: Diameter(g36) = 1
    c: Equal(g36, g37-g50) x14
    c: Equal(g36,g65)
    c: Equal(g36,g64)
    c: Equal(g36,g63)
    c: Equal(g36,g62)
    c: Equal(g36,g61)
    c: Equal(g36,g60)
    c: Equal(g36,g59)
    c: Equal(g36,g58)
    c: Equal(g36,g57)
    c: Equal(g36,g56)
    c: Equal(g36,g55)
    c: Equal(g36,g54)
    c: Equal(g36,g53)
    c: Equal(g36,g52)
    c: Equal(g36,g51)
FEATURE [PartDesign::Pad] Pad146
  AllowMultiFace = false
  Direction = (1,1,1)
  Length = 1.6
  Length2 = 100
  Profile = -> Sketch214
  Reversed = true
  Type = 0
FEATURE [PartDesign::Body] Body119  label="PCB003"
  Group = -> [Sketch214,Pad146]
  Origin = -> Origin276
  Tip = -> Pad146
FEATURE [Part::Feature] Shape170  label="J3_PinHeader_1x15_P254mm_Vertical_5F717820"
  Placement = pos=(2.75,38.5,-5.2e-15) rot=(0,0,1;0rad)
  shape: bbox 2.54 x 38.1 x 11.54 mm, 364 faces (baked)
FEATURE [Part::Feature] Shape171  label="J8_PinSocket_1x15_P254mm_Vertical_5F7178B015"
  Placement = pos=(44.65,38.5,4e-15) rot=(0,0,1;0rad)
  shape: bbox 2.54 x 38.1 x 10.1 mm, 475 faces (baked)
FEATURE [Sketcher::SketchObject] Sketch215
  FullyConstrained = false
  MapMode = 5
  Support = -> [XY_Plane277]
  sketch-geometry (1):
    g0: Circle CenterX=0 CenterY=0 CenterZ=0 NormalX=0 NormalY=0 NormalZ=1 AngleXU=0 Radius=4.15
  constraints (2):
    c: Coincident(g0,g-1)
    c: Diameter(g0) = 8.3
FEATURE [PartDesign::Pad] Pad147
  AllowMultiFace = false
  Direction = (1,1,1)
  Length = 10.5
  Length2 = 100
  Profile = -> Sketch215
  Type = 0
FEATURE [PartDesign::Body] Body120  label="Capacitor003"
  Group = -> [Sketch215,Pad147]
  Origin = -> Origin277
  Placement = pos=(10,14.5,-1.6) rot=(0,1,0;3.14159rad)
  Tip = -> Pad147
FEATURE [Sketcher::SketchObject] Sketch216
  FullyConstrained = false
  MapMode = 5
  Placement = pos=(0,0,0) rot=(1,0,0;1.5708rad)
  Support = -> [XZ_Plane277]
  sketch-geometry (1):
    g0: Circle CenterX=10 CenterY=-1.6 CenterZ=0 NormalX=0 NormalY=0 NormalZ=1 AngleXU=0 Radius=4.1
  constraints (3):
    c: DistanceX(g-1,g0) = 10
    c: DistanceY(g0,g-1) = 1.6
    c: Diameter(g0) = 8.2
FEATURE [PartDesign::Pad] Pad148
  AllowMultiFace = false
  Direction = (1,1,1)
  Length = 12
  Length2 = 100
  Placement = pos=(0,0,0) rot=(1,0,0;1.5708rad)
  Profile = -> Sketch216
  Type = 0
FEATURE [PartDesign::Body] Body121  label="AltCap001"
  Group = -> [Sketch216,Pad148]
  Origin = -> Origin279
  Tip = -> Pad148
FEATURE [App::Part] Part016  label="H-bridge003"
  Group = -> [Body119,Shape170,Shape171,Body120,Body121]
  Origin = -> Origin275
  Placement = pos=(9.25,8.5,-11.2) rot=(0,0,1;0rad)
FEATURE [App::Part] Part017  label="motor_driver003"
  Group = -> [Board_d4f006,Part016]
  Origin = -> Origin278
  Placement = pos=(128.9,-30.6,129.9) rot=(0,0.707107,-0.707107;3.14159rad)
FEATURE [Part::Feature] Shape172  label="U4_SOIC_8_39x49mm_P127mm_5F717A081"
  Placement = pos=(40.25,11.5,0) rot=(0,0,1;0rad)
  shape: bbox 6 x 4.9 x 1.75 mm, 156 faces (baked)
FEATURE [Part::Feature] Shape173  label="U3_LQFP_32_7x7mm_P08mm_5F71845B004"
  Placement = pos=(36.5,25.5,0) rot=(0,0,-1;1.5708rad)
  shape: bbox 9 x 9 x 1.5 mm, 516 faces (baked)
FEATURE [Part::Feature] Shape174  label="C8_C_0603_1608Metric_5F7555CB004"
  Placement = pos=(26,13,0) rot=(0,0,1;3.14159rad)
  shape: bbox 1.6 x 0.8 x 0.8 mm, 28 faces (baked)
FEATURE [Part::Feature] Shape175  label="U5_SOT_23_5_5F717A8C004"
  Placement = pos=(4.5,23,0) rot=(0,0,1;1.5708rad)
  shape: bbox 2.9 x 2.8 x 1.55 mm, 109 faces (baked)
FEATURE [Part::Feature] Shape176  label="C9_C_0603_1608Metric_5F754EF013"
  Placement = pos=(26,17.5,0) rot=(0,0,1;3.14159rad)
  shape: bbox 1.6 x 0.8 x 0.8 mm, 28 faces (baked)
FEATURE [Part::Feature] Shape177  label="J3_PinHeader_1x15_P254mm_Vertical_5F717821"
  Placement = pos=(54,47,-1.6) rot=(0,1,0;3.14159rad)
  shape: bbox 2.54 x 38.1 x 11.54 mm, 364 faces (baked)
FEATURE [Part::Part2DObjectPython] InvoluteGear006  # Draft 2D object (typed FeaturePython)
  ExternalGear = true
  HighPrecision = true
  Modules = 2
  NumberOfTeeth = 26
  PressureAngle = 20
FEATURE [PartDesign::Pad] Pad149
  AllowMultiFace = false
  Direction = (1,1,1)
  Length = 5
  Length2 = 100
  Profile = -> InvoluteGear006
  Type = 0
FEATURE [Sketcher::SketchObject] Sketch217
  FullyConstrained = false
  MapMode = 5
  Placement = pos=(0,0,5) rot=(0,0,1;0rad)
  Support = -> [Pad149]
  sketch-geometry (1):
    g0: Circle CenterX=0 CenterY=0 CenterZ=0 NormalX=0 NormalY=0 NormalZ=1 AngleXU=0 Radius=18
  constraints (2):
    c: Coincident(g0,g-1)
    c: Diameter(g0) = 36
FEATURE [PartDesign::Pocket] Pocket051
  AllowMultiFace = false
  BaseFeature = -> Pad149
  Length = 2
  Length2 = 100
  Profile = -> Sketch217
  Type = 0
FEATURE [Sketcher::SketchObject] Sketch218
  FullyConstrained = false
  MapMode = 5
  Placement = pos=(0,0,3) rot=(0,0,1;0rad)
  Support = -> [Pocket051]
  sketch-geometry (1):
    g0: Circle CenterX=0 CenterY=0 CenterZ=0 NormalX=0 NormalY=0 NormalZ=1 AngleXU=0 Radius=5.5
  constraints (2):
    c: Coincident(g0,g-1)
    c: Diameter(g0) = 11
FEATURE [PartDesign::Pocket] Pocket052
  AllowMultiFace = false
  BaseFeature = -> Pocket051
  Length = 0.5
  Length2 = 100
  Profile = -> Sketch218
  Type = 0
FEATURE [Sketcher::SketchObject] Sketch219
  FullyConstrained = false
  MapMode = 5
  Placement = pos=(0,0,2.5) rot=(0,0,1;0rad)
  Support = -> [Pocket052]
  sketch-geometry (1):
    g0: Circle CenterX=0 CenterY=0 CenterZ=0 NormalX=0 NormalY=0 NormalZ=1 AngleXU=0 Radius=4
  constraints (2):
    c: Coincident(g0,g-1)
    c: Diameter(g0) = 8
FEATURE [PartDesign::Pocket] Pocket053
  AllowMultiFace = false
  BaseFeature = -> Pocket052
  Length = 5
  Length2 = 100
  Profile = -> Sketch219
  Type = 0
FEATURE [PartDesign::Body] Body123  label="Servo Gear005"
  Group = -> [InvoluteGear006,Pad149,Sketch217,Pocket051,Sketch218,Pocket052,Sketch219,Pocket053]
  Origin = -> Origin280
  Placement = pos=(-48,-2.22e-14,68) rot=(0,0,-1;1.5708rad)
  Tip = -> Pocket053
FEATURE [PartDesign::FeatureBase] Clone014
  BaseFeature = -> Body123
  Placement = pos=(-48,-2.22e-14,68) rot=(0,0,-1;1.5708rad)
FEATURE [Sketcher::SketchObject] Sketch220
  FullyConstrained = false
  MapMode = 5
  Placement = pos=(0,0,0) rot=(1,0,0;1.5708rad)
  Support = -> [XZ_Plane279]
  sketch-geometry (15):
    g0: LineSegment StartX=-1.5 StartY=0 StartZ=0 EndX=-1.5 EndY=-0.85 EndZ=0
    g1: LineSegment StartX=-1.5 StartY=-0.85 StartZ=0 EndX=-3.85 EndY=-0.85 EndZ=0
    g2: LineSegment StartX=-3.85 StartY=-0.85 StartZ=0 EndX=-3.85 EndY=-1.85 EndZ=0
    g3: LineSegment StartX=-3.85 StartY=-1.85 StartZ=0 EndX=-4.85 EndY=-1.85 EndZ=0
    g4: LineSegment StartX=-4.85 StartY=-1.85 StartZ=0 EndX=-5.35 EndY=-1.35 EndZ=0
    g5: LineSegment StartX=-5.35 StartY=-1.35 StartZ=0 EndX=-17.9 EndY=-1.35 EndZ=0
    g6: LineSegment StartX=-17.9 StartY=-1.35 StartZ=0 EndX=-17.9 EndY=0.65 EndZ=0
    g7: LineSegment StartX=-17.9 StartY=0.65 StartZ=0 EndX=-8 EndY=0.65 EndZ=0
    g8: LineSegment StartX=-8 StartY=0.65 StartZ=0 EndX=-6 EndY=1.45 EndZ=0
    g9: LineSegment StartX=-6 StartY=1.45 StartZ=0 EndX=-4.825 EndY=1.45 EndZ=0
    g10: LineSegment StartX=-4.825 StartY=1.45 StartZ=0 EndX=-4.825 EndY=2.625 EndZ=0
    g11: LineSegment StartX=-4.825 StartY=2.625 StartZ=0 EndX=-4 EndY=3.45 EndZ=0
    g12: LineSegment StartX=-4 StartY=3.45 StartZ=0 EndX=-2.85 EndY=3.45 EndZ=0
    g13: LineSegment StartX=-2.85 StartY=3.45 StartZ=0 EndX=-2.85 EndY=0 EndZ=0
    g14: LineSegment StartX=-2.85 StartY=0 StartZ=0 EndX=-1.5 EndY=0 EndZ=0
  constraints (45):
    c: Coincident(g0,g1)
    c: Coincident(g1,g2)
    c: Coincident(g2,g3)
    c: Coincident(g3,g4)
    c: Coincident(g4,g5)
    c: Coincident(g5,g6)
    c: Coincident(g6,g7)
    c: Coincident(g7,g8)
    c: Coincident(g8,g9)
    c: Coincident(g9,g10)
    c: Coincident(g10,g11)
    c: Coincident(g11,g12)
    c: Coincident(g12,g13)
    c: Coincident(g13,g14)
    c: Coincident(g14,g0)
    c: Horizontal(g5)
    c: Horizontal(g7)
    c: Horizontal(g9)
    c: Horizontal(g12)
    c: Vertical(g13)
    c: Horizontal(g14)
    c: Vertical(g0)
    c: Horizontal(g1)
    c: Vertical(g2)
    c: Horizontal(g3)
    c: Vertical(g10)
    c: Vertical(g6)
    c: DistanceY(g6,g6) = 2
    c: DistanceX(g6,g-1) = 17.9
    c: DistanceY(g3,g4) = 0.5
    c: DistanceX(g3,g3) = 1
    c: DistanceY(g2,g2) = 1
    c: DistanceX(g4,g3) = 0.5
    c: DistanceX(g1,g-1) = 3.85
    c: DistanceX(g0,g-1) = 1.5
    c: DistanceX(g7,g-1) = 8
    c: DistanceX(g8,g-1) = 6
    c: DistanceY(g7,g8) = 0.8
    c: DistanceX(g10,g-1) = 4.825
    c: DistanceX(g12,g-1) = 2.85
    c: DistanceX(g11,g-1) = 4
    c: DistanceY(g2,g12) = 5.3
    c: DistanceY(g13,g13) = 3.45
    c: Angle(g11,g12) = 2.35619
    c: PointOnObject(g0,g-1)
FEATURE [PartDesign::Revolution] Revolution012
  AllowMultiFace = false
  Angle = 360
  Axis = (0,2e-16,1)
  Base = (0,0,0)
  Placement = pos=(0,0,0) rot=(1,0,0;1.5708rad)
  Profile = -> Sketch220
  ReferenceAxis = -> Sketch220 [V_Axis]
FEATURE [PartDesign::Body] Body122  label="Servo Horn005"
  Group = -> [Sketch220,Revolution012]
  Origin = -> Origin281
  Placement = pos=(-48,0,72.5) rot=(0,0,1;0rad)
  Tip = -> Revolution012
FEATURE [PartDesign::FeatureBase] Clone013
  BaseFeature = -> Body122
  Placement = pos=(-48,0,72.5) rot=(0,0,1;0rad)
FEATURE [Sketcher::SketchObject] Sketch221
  FullyConstrained = false
  MapMode = 5
  Support = -> [XY_Plane282]
  sketch-geometry (4):
    g0: LineSegment StartX=-20.35 StartY=10.075 StartZ=0 EndX=20.35 EndY=10.075 EndZ=0
    g1: LineSegment StartX=20.35 StartY=10.075 StartZ=0 EndX=20.35 EndY=-10.075 EndZ=0
    g2: LineSegment StartX=20.35 StartY=-10.075 StartZ=0 EndX=-20.35 EndY=-10.075 EndZ=0
    g3: LineSegment StartX=-20.35 StartY=-10.075 StartZ=0 EndX=-20.35 EndY=10.075 EndZ=0
  constraints (11):
    c: Coincident(g0,g1)
    c: Coincident(g1,g2)
    c: Coincident(g2,g3)
    c: Coincident(g3,g0)
    c: Horizontal(g0)
    c: Horizontal(g2)
    c: Vertical(g1)
    c: Vertical(g3)
    c: Symmetric(g0,g1,g-1)
    c: DistanceX(g0,g0) = 40.7
    c: DistanceY(g3,g3) = 20.15
FEATURE [PartDesign::Pad] Pad150
  AllowMultiFace = false
  Direction = (1,1,1)
  Length = 29
  Length2 = 100
  Profile = -> Sketch221
  Reversed = true
  Type = 0
FEATURE [Sketcher::SketchObject] Sketch222
  FullyConstrained = false
  MapMode = 5
  Support = -> [Pad150]
  sketch-geometry (16):
    g0: LineSegment StartX=-27.2 StartY=10.075 StartZ=0 EndX=27.2 EndY=10.075 EndZ=0
    g1: LineSegment StartX=27.2 StartY=10.075 StartZ=0 EndX=27.2 EndY=6 EndZ=0
    g2: LineSegment StartX=-27.2 StartY=10.075 StartZ=0 EndX=-27.2 EndY=6 EndZ=0
    g3: LineSegment StartX=-27.2 StartY=4 StartZ=0 EndX=-27.2 EndY=-4 EndZ=0
    g4: LineSegment StartX=27.2 StartY=4 StartZ=0 EndX=27.2 EndY=-4 EndZ=0
    g5: LineSegment StartX=27.2 StartY=-6 StartZ=0 EndX=27.2 EndY=-10.075 EndZ=0
    g6: LineSegment StartX=27.2 StartY=-10.075 StartZ=0 EndX=-27.2 EndY=-10.075 EndZ=0
    g7: LineSegment StartX=-27.2 StartY=-10.075 StartZ=0 EndX=-27.2 EndY=-6 EndZ=0
    g8: ArcOfCircle CenterX=-24.5 CenterY=5 CenterZ=0 NormalX=0 NormalY=0 NormalZ=1 AngleXU=0 Radius=2.87924 StartAngle=3.4963 EndAngle=9.07007
    g9: ArcOfCircle CenterX=-24.5 CenterY=-5 CenterZ=0 NormalX=0 NormalY=0 NormalZ=1 AngleXU=0 Radius=2.87924 StartAngle=3.4963 EndAngle=9.07007
    g10: ArcOfCircle CenterX=24.5 CenterY=5 CenterZ=0 NormalX=0 NormalY=0 NormalZ=1 AngleXU=0 Radius=2.87924 StartAngle=0.354706 EndAngle=5.92848
    g11: ArcOfCircle CenterX=24.5 CenterY=-5 CenterZ=0 NormalX=0 NormalY=0 NormalZ=1 AngleXU=0 Radius=2.87924 StartAngle=0.354706 EndAngle=5.92848
    g12: LineSegment StartX=-24.5 StartY=5 StartZ=0 EndX=24.5 EndY=5 EndZ=0
    g13: LineSegment StartX=24.5 StartY=5 StartZ=0 EndX=24.5 EndY=-5 EndZ=0
    g14: LineSegment StartX=24.5 StartY=-5 StartZ=0 EndX=-24.5 EndY=-5 EndZ=0
    g15: LineSegment StartX=-24.5 StartY=-5 StartZ=0 EndX=-24.5 EndY=5 EndZ=0
  constraints (46):
    c: Coincident(g0,g1)
    c: Coincident(g5,g6)
    c: Coincident(g6,g7)
    c: Horizontal(g0)
    c: Horizontal(g6)
    c: Vertical(g4)
    c: Vertical(g1)
    c: Vertical(g5)
    c: Vertical(g7)
    c: Vertical(g3)
    c: Vertical(g2)
    c: Vertical(g7,g3)
    c: Vertical(g3,g2)
    c: Coincident(g2,g0)
    c: Vertical(g1,g4)
    c: Vertical(g4,g5)
    c: DistanceX(g0,g0) = 54.4
    c: Coincident(g10,g1)
    c: Coincident(g10,g4)
    c: Coincident(g11,g4)
    c: Coincident(g11,g5)
    c: Coincident(g9,g7)
    c: Coincident(g9,g3)
    c: Coincident(g8,g3)
    c: Coincident(g8,g2)
    c: Symmetric(g0,g5,g-1)
    c: DistanceY(g6,g0) = 20.15
    c: Equal(g9,g8)
    c: Equal(g8,g10)
    c: Equal(g10,g11)
    c: Coincident(g12,g13)
    c: Coincident(g13,g14)
    c: Coincident(g14,g15)
    c: Coincident(g15,g12)
    c: Horizontal(g12)
    c: Horizontal(g14)
    c: Vertical(g13)
    c: Vertical(g15)
    c: Symmetric(g12,g13,g-1)
    c: DistanceX(g12,g12) = 49
    c: Coincident(g8,g12)
    c: Coincident(g9,g14)
    c: Coincident(g11,g13)
    c: Coincident(g10,g12)
    c: DistanceY(g15,g15) = 10
    c: DistanceY(g3,g2) = 2
FEATURE [PartDesign::Pad] Pad151
  AllowMultiFace = false
  BaseFeature = -> Pad150
  Direction = (1,1,1)
  Length = 2.55
  Length2 = 100
  Profile = -> Sketch222
  Type = 0
FEATURE [Sketcher::SketchObject] Sketch223
  FullyConstrained = false
  MapMode = 5
  Placement = pos=(0,0,2.55) rot=(0,0,1;0rad)
  Support = -> [Pad151]
  sketch-geometry (4):
    g0: LineSegment StartX=-20.35 StartY=10.075 StartZ=0 EndX=20.35 EndY=10.075 EndZ=0
    g1: LineSegment StartX=20.35 StartY=10.075 StartZ=0 EndX=20.35 EndY=-10.075 EndZ=0
    g2: LineSegment StartX=20.35 StartY=-10.075 StartZ=0 EndX=-20.35 EndY=-10.075 EndZ=0
    g3: LineSegment StartX=-20.35 StartY=-10.075 StartZ=0 EndX=-20.35 EndY=10.075 EndZ=0
  constraints (11):
    c: Coincident(g0,g1)
    c: Coincident(g1,g2)
    c: Coincident(g2,g3)
    c: Coincident(g3,g0)
    c: Horizontal(g0)
    c: Horizontal(g2)
    c: Vertical(g1)
    c: Vertical(g3)
    c: Symmetric(g1,g0,g-1)
    c: DistanceX(g0,g0) = 40.7
    c: DistanceY(g3,g3) = 20.15
FEATURE [PartDesign::Pad] Pad152
  AllowMultiFace = false
  BaseFeature = -> Pad151
  Direction = (1,1,1)
  Length = 5.5
  Length2 = 100
  Profile = -> Sketch223
  Type = 0
FEATURE [Sketcher::SketchObject] Sketch224
  FullyConstrained = false
  MapMode = 5
  Placement = pos=(0,0,8.05) rot=(0,0,1;0rad)
  Support = -> [Pad152]
  sketch-geometry (7):
    g0: ArcOfCircle CenterX=10.35 CenterY=0 CenterZ=0 NormalX=0 NormalY=0 NormalZ=1 AngleXU=0 Radius=10 StartAngle=4.26136 EndAngle=8.30501
    g1: LineSegment StartX=5.9911 StartY=9 StartZ=0 EndX=-14.85 EndY=9 EndZ=0
    g2: LineSegment StartX=-14.85 StartY=9 StartZ=0 EndX=-14.85 EndY=5 EndZ=0
    g3: LineSegment StartX=-14.85 StartY=-5 StartZ=0 EndX=-14.85 EndY=-9 EndZ=0
    g4: LineSegment StartX=-14.85 StartY=-9 StartZ=0 EndX=5.9911 EndY=-9 EndZ=0
    g5: ArcOfCircle CenterX=-11.1 CenterY=0 CenterZ=0 NormalX=0 NormalY=0 NormalZ=1 AngleXU=0 Radius=6.25 StartAngle=3.14159 EndAngle=4.06889
    g6: ArcOfCircle CenterX=-11.1 CenterY=0 CenterZ=0 NormalX=0 NormalY=0 NormalZ=1 AngleXU=0 Radius=6.25 StartAngle=2.2143 EndAngle=3.14159
  constraints (23):
    c: PointOnObject(g0,g-1)
    c: Diameter(g0) = 20
    c: DistanceX(g-1,g0) = 10.35
    c: Coincident(g1,g2)
    c: Coincident(g3,g4)
    c: Coincident(g1,g0)
    c: Coincident(g4,g0)
    c: Horizontal(g4)
    c: Horizontal(g1)
    c: Vertical(g2)
    c: Vertical(g3)
    c: DistanceX(g3,g-1) = 14.85
    c: Equal(g1,g4)
    c: Vertical(g3,g2)
    c: DistanceY(g3,g1) = 18
    c: Coincident(g6,g2)
    c: Coincident(g5,g3)
    c: Coincident(g6,g5)
    c: Tangent(g6,g5) = -1.5708
    c: PointOnObject(g5,g-1)
    c: PointOnObject(g5,g-1)
    c: DistanceX(g5,g-1) = 17.35
    c: DistanceY(g3,g2) = 10
FEATURE [PartDesign::Pad] Pad153
  AllowMultiFace = false
  BaseFeature = -> Pad152
  Direction = (1,1,1)
  Length = 2
  Length2 = 100
  Profile = -> Sketch224
  Type = 0
FEATURE [Sketcher::SketchObject] Sketch225
  FullyConstrained = false
  MapMode = 5
  Placement = pos=(0,0,10.05) rot=(0,0,1;0rad)
  Support = -> [Pad153]
  sketch-geometry (1):
    g0: Circle CenterX=10.35 CenterY=0 CenterZ=0 NormalX=0 NormalY=0 NormalZ=1 AngleXU=0 Radius=6.5
  constraints (3):
    c: PointOnObject(g0,g-1)
    c: DistanceX(g-1,g0) = 10.35
    c: Diameter(g0) = 13
FEATURE [PartDesign::Pad] Pad154
  AllowMultiFace = false
  BaseFeature = -> Pad153
  Direction = (1,1,1)
  Length = 1.3
  Length2 = 100
  Profile = -> Sketch225
  Type = 0
FEATURE [Sketcher::SketchObject] Sketch226
  FullyConstrained = false
  MapMode = 5
  Placement = pos=(0,0,11.35) rot=(0,0,1;0rad)
  Support = -> [Pad154]
  sketch-geometry (1):
    g0: Circle CenterX=10.35 CenterY=0 CenterZ=0 NormalX=0 NormalY=0 NormalZ=1 AngleXU=0 Radius=5.5
  constraints (3):
    c: PointOnObject(g0,g-1)
    c: Diameter(g0) = 11
    c: DistanceX(g-1,g0) = 10.35
FEATURE [PartDesign::Pad] Pad155
  AllowMultiFace = false
  BaseFeature = -> Pad154
  Direction = (1,1,1)
  Length = 0.7
  Length2 = 100
  Profile = -> Sketch226
  Type = 0
FEATURE [Sketcher::SketchObject] Sketch227
  FullyConstrained = false
  MapMode = 5
  Placement = pos=(0,0,12.05) rot=(0,0,1;0rad)
  Support = -> [Pad155]
  sketch-geometry (1):
    g0: Circle CenterX=10.35 CenterY=0 CenterZ=0 NormalX=0 NormalY=0 NormalZ=1 AngleXU=0 Radius=3
  constraints (3):
    c: PointOnObject(g0,g-1)
    c: DistanceX(g-1,g0) = 10.35
    c: Diameter(g0) = 6
FEATURE [PartDesign::Pad] Pad156
  AllowMultiFace = false
  BaseFeature = -> Pad155
  Direction = (1,1,1)
  Length = 3.5
  Length2 = 100
  Profile = -> Sketch227
  Type = 0
FEATURE [PartDesign::Body] Body124  label="MG998"
  Group = -> [Sketch221,Pad150,Sketch222,Pad151,Sketch223,Pad152,Sketch224,Pad153,Sketch225,Pad154,Sketch226,Pad155,Sketch227,Pad156]
  Origin = -> Origin282
  Placement = pos=(-58.5,-1e-15,88.5) rot=(1,0,0;3.14159rad)
  Tip = -> Pad156
FEATURE [PartDesign::FeatureBase] Clone016
  BaseFeature = -> Body124
  Placement = pos=(-58.5,-1e-15,88.5) rot=(1,0,0;3.14159rad)
FEATURE [Sketcher::SketchObject] Sketch228
  FullyConstrained = false
  MapMode = 5
  Placement = pos=(0,0,0) rot=(1,0,0;1.5708rad)
  Support = -> [XZ_Plane281]
  sketch-geometry (8):
    g0: LineSegment StartX=-20.5 StartY=40 StartZ=0 EndX=-20.5 EndY=0 EndZ=0
    g1: LineSegment StartX=-20.5 StartY=0 StartZ=0 EndX=13.5 EndY=0 EndZ=0
    g2: LineSegment StartX=13.5 StartY=0 StartZ=0 EndX=13.5 EndY=9 EndZ=0
    g3: LineSegment StartX=13.5 StartY=9 StartZ=0 EndX=20.8 EndY=9 EndZ=0
    g4: LineSegment StartX=20.8 StartY=9 StartZ=0 EndX=20.8 EndY=14 EndZ=0
    g5: LineSegment StartX=20.8 StartY=14 StartZ=0 EndX=13.5 EndY=14 EndZ=0
    g6: LineSegment StartX=13.5 StartY=14 StartZ=0 EndX=13.5 EndY=40 EndZ=0
    g7: LineSegment StartX=13.5 StartY=40 StartZ=0 EndX=-20.5 EndY=40 EndZ=0
  constraints (24):
    c: Coincident(g0,g1)
    c: Coincident(g1,g2)
    c: Coincident(g2,g3)
    c: Coincident(g3,g4)
    c: Coincident(g4,g5)
    c: Coincident(g5,g6)
    c: Coincident(g6,g7)
    c: Coincident(g7,g0)
    c: Horizontal(g7)
    c: Horizontal(g1)
    c: Horizontal(g3)
    c: Horizontal(g5)
    c: Vertical(g6)
    c: Vertical(g2)
    c: Vertical(g4)
    c: Vertical(g0)
    c: Equal(g1,g7)
    c: PointOnObject(g-1,g1)
    c: DistanceX(g1,g1) = 34
    c: DistanceY(g2,g2) = 9
    c: DistanceX(g-1,g1) = 13.5
    c: DistanceX(g3,g3) = 7.3
    c: DistanceY(g4,g4) = 5
    c: DistanceY(g0,g0) = 40
FEATURE [PartDesign::Pad] Pad157
  AllowMultiFace = false
  Direction = (1,1,1)
  Length = 22
  Length2 = 100
  Midplane = true
  Placement = pos=(0,0,0) rot=(1,0,0;1.5708rad)
  Profile = -> Sketch228
  Type = 0
FEATURE [Sketcher::SketchObject] Sketch229
  FullyConstrained = false
  MapMode = 5
  Placement = pos=(0,0,0) rot=(1,0,0;3.14159rad)
  Support = -> [Pad157]
  sketch-geometry (1):
    g0: Circle CenterX=0 CenterY=0 CenterZ=0 NormalX=0 NormalY=0 NormalZ=1 AngleXU=0 Radius=9.75
  constraints (2):
    c: Coincident(g0,g-1)
    c: Diameter(g0) = 19.5
FEATURE [PartDesign::Pocket] Pocket054
  AllowMultiFace = false
  BaseFeature = -> Pad157
  Length = 6
  Length2 = 100
  Placement = pos=(0,0,0) rot=(1,0,0;1.5708rad)
  Profile = -> Sketch229
  Type = 0
FEATURE [Sketcher::SketchObject] Sketch230
  FullyConstrained = false
  MapMode = 5
  Placement = pos=(0,4e-15,6) rot=(1,0,0;3.14159rad)
  Support = -> [Pocket054]
  sketch-geometry (1):
    g0: Circle CenterX=0 CenterY=0 CenterZ=0 NormalX=0 NormalY=0 NormalZ=1 AngleXU=0 Radius=5.5
  constraints (2):
    c: Coincident(g0,g-1)
    c: Diameter(g0) = 11
FEATURE [PartDesign::Pocket] Pocket055
  AllowMultiFace = false
  BaseFeature = -> Pocket054
  Length = 40
  Length2 = 100
  Placement = pos=(0,0,0) rot=(1,0,0;1.5708rad)
  Profile = -> Sketch230
  Type = 0
FEATURE [Sketcher::SketchObject] Sketch231
  FullyConstrained = false
  MapMode = 5
  Placement = pos=(0,1.76e-14,40) rot=(0,0,1;3.14159rad)
  Support = -> [Pocket055]
  sketch-geometry (1):
    g0: Circle CenterX=0 CenterY=0 CenterZ=0 NormalX=0 NormalY=0 NormalZ=1 AngleXU=0 Radius=9.75
  constraints (2):
    c: Coincident(g0,g-1)
    c: Diameter(g0) = 19.5
FEATURE [PartDesign::Pocket] Pocket056
  AllowMultiFace = false
  BaseFeature = -> Pocket055
  Length = 6
  Length2 = 100
  Placement = pos=(0,0,0) rot=(1,0,0;1.5708rad)
  Profile = -> Sketch231
  Type = 0
FEATURE [Sketcher::SketchObject] Sketch232
  FullyConstrained = false
  MapMode = 5
  Placement = pos=(0,-11,2.4e-15) rot=(1,0,0;1.5708rad)
  Support = -> [Pocket056]
  sketch-geometry (3):
    g0: Circle CenterX=-15 CenterY=32.5 CenterZ=0 NormalX=0 NormalY=0 NormalZ=1 AngleXU=0 Radius=2.25
    g1: Circle CenterX=-15 CenterY=7.5 CenterZ=0 NormalX=0 NormalY=0 NormalZ=1 AngleXU=0 Radius=2.25
    g2: LineSegment StartX=-15 StartY=32.5 StartZ=0 EndX=-15 EndY=7.5 EndZ=0
  constraints (8):
    c: Vertical(g2)
    c: Coincident(g2,g0)
    c: Coincident(g1,g2)
    c: DistanceY(g2,g2) = 25
    c: Diameter(g0) = 4.5
    c: Equal(g0,g1)
    c: DistanceX(g1,g-1) = 15
    c: DistanceY(g-1,g1) = 7.5
FEATURE [PartDesign::Pocket] Pocket057
  AllowMultiFace = false
  BaseFeature = -> Pocket056
  Length = 25
  Length2 = 100
  Placement = pos=(0,0,0) rot=(1,0,0;1.5708rad)
  Profile = -> Sketch232
  Type = 0
FEATURE [Sketcher::SketchObject] Sketch233
  FullyConstrained = false
  MapMode = 5
  Placement = pos=(0,4e-15,9) rot=(1,0,0;3.14159rad)
  Support = -> [Pocket057]
  sketch-geometry (6):
    g0: Circle CenterX=16.95 CenterY=5 CenterZ=0 NormalX=0 NormalY=0 NormalZ=1 AngleXU=0 Radius=1.5
    g1: Circle CenterX=16.95 CenterY=-5 CenterZ=0 NormalX=0 NormalY=0 NormalZ=1 AngleXU=0 Radius=1.5
    g2: LineSegment StartX=0 StartY=5 StartZ=0 EndX=16.95 EndY=5 EndZ=0
    g3: LineSegment StartX=16.95 StartY=5 StartZ=0 EndX=16.95 EndY=-5 EndZ=0
    g4: LineSegment StartX=16.95 StartY=-5 StartZ=0 EndX=0 EndY=-5 EndZ=0
    g5: LineSegment StartX=0 StartY=-5 StartZ=0 EndX=0 EndY=5 EndZ=0
  constraints (15):
    c: Coincident(g2,g3)
    c: Coincident(g3,g4)
    c: Coincident(g4,g5)
    c: Coincident(g5,g2)
    c: Horizontal(g2)
    c: Horizontal(g4)
    c: Vertical(g3)
    c: Vertical(g5)
    c: Symmetric(g2,g4,g-1)
    c: DistanceY(g3,g3) = 10
    c: DistanceX(g2,g2) = 16.95
    c: Coincident(g0,g2)
    c: Coincident(g1,g3)
    c: Diameter(g1) = 3
    c: Equal(g1,g0)
FEATURE [PartDesign::Pocket] Pocket058
  AllowMultiFace = false
  BaseFeature = -> Pocket057
  Length = 5
  Length2 = 100
  Placement = pos=(0,0,0) rot=(1,0,0;1.5708rad)
  Profile = -> Sketch233
  Type = 0
FEATURE [PartDesign::Body] Body126  label="End_Bearing_Block005"
  Group = -> [Sketch228,Pad157,Sketch229,Pocket054,Sketch230,Pocket055,Sketch231,Pocket056,Sketch232,Pocket057,Sketch233,Pocket058]
  Origin = -> Origin283
  Placement = pos=(-100,0,81) rot=(0,0,1;0rad)
  Tip = -> Pocket058
FEATURE [PartDesign::FeatureBase] Clone015
  BaseFeature = -> Body126
  Placement = pos=(-100,0,81) rot=(0,0,1;0rad)
FEATURE [Sketcher::SketchObject] Sketch234
  FullyConstrained = false
  MapMode = 5
  Placement = pos=(0,0,0) rot=(1,0,0;1.5708rad)
  Support = -> [XZ_Plane282]
  sketch-geometry (8):
    g0: LineSegment StartX=-1.5 StartY=40 StartZ=0 EndX=-1.5 EndY=0 EndZ=0
    g1: LineSegment StartX=-1.5 StartY=0 StartZ=0 EndX=13.5 EndY=0 EndZ=0
    g2: LineSegment StartX=13.5 StartY=0 StartZ=0 EndX=13.5 EndY=9 EndZ=0
    g3: LineSegment StartX=13.5 StartY=9 StartZ=0 EndX=20.8 EndY=9 EndZ=0
    g4: LineSegment StartX=20.8 StartY=9 StartZ=0 EndX=20.8 EndY=14 EndZ=0
    g5: LineSegment StartX=20.8 StartY=14 StartZ=0 EndX=13.5 EndY=14 EndZ=0
    g6: LineSegment StartX=13.5 StartY=14 StartZ=0 EndX=13.5 EndY=40 EndZ=0
    g7: LineSegment StartX=13.5 StartY=40 StartZ=0 EndX=-1.5 EndY=40 EndZ=0
  constraints (24):
    c: Coincident(g0,g1)
    c: Coincident(g1,g2)
    c: Coincident(g2,g3)
    c: Coincident(g3,g4)
    c: Coincident(g4,g5)
    c: Coincident(g5,g6)
    c: Coincident(g6,g7)
    c: Coincident(g7,g0)
    c: Horizontal(g7)
    c: Horizontal(g1)
    c: Horizontal(g3)
    c: Horizontal(g5)
    c: Vertical(g6)
    c: Vertical(g2)
    c: Vertical(g4)
    c: Vertical(g0)
    c: Equal(g1,g7)
    c: PointOnObject(g-1,g1)
    c: DistanceX(g1,g1) = 15
    c: DistanceY(g2,g2) = 9
    c: DistanceX(g-1,g1) = 13.5
    c: DistanceX(g3,g3) = 7.3
    c: DistanceY(g4,g4) = 5
    c: DistanceY(g0,g0) = 40
FEATURE [PartDesign::Pad] Pad158
  AllowMultiFace = false
  Direction = (1,1,1)
  Length = 22
  Length2 = 100
  Midplane = true
  Placement = pos=(0,0,0) rot=(1,0,0;1.5708rad)
  Profile = -> Sketch234
  Type = 0
FEATURE [Sketcher::SketchObject] Sketch235
  FullyConstrained = false
  MapMode = 5
  Placement = pos=(0,-11,2.4e-15) rot=(1,0,0;1.5708rad)
  Support = -> [Pad158]
  sketch-geometry (3):
    g0: Circle CenterX=3.4 CenterY=32.5 CenterZ=0 NormalX=0 NormalY=0 NormalZ=1 AngleXU=0 Radius=2.25
    g1: Circle CenterX=3.4 CenterY=7.5 CenterZ=0 NormalX=0 NormalY=0 NormalZ=1 AngleXU=0 Radius=2.25
    g2: LineSegment StartX=3.4 StartY=32.5 StartZ=0 EndX=3.4 EndY=7.5 EndZ=0
  constraints (8):
    c: Vertical(g2)
    c: Coincident(g2,g0)
    c: Coincident(g1,g2)
    c: DistanceY(g2,g2) = 25
    c: Diameter(g0) = 4.5
    c: Equal(g0,g1)
    c: DistanceY(g-1,g1) = 7.5
    c: DistanceX(g-1,g1) = 3.4
FEATURE [PartDesign::Pocket] Pocket059
  AllowMultiFace = false
  BaseFeature = -> Pad158
  Length = 25
  Length2 = 100
  Placement = pos=(0,0,0) rot=(1,0,0;1.5708rad)
  Profile = -> Sketch235
  Type = 0
FEATURE [Sketcher::SketchObject] Sketch236
  FullyConstrained = false
  MapMode = 5
  Placement = pos=(0,4e-15,9) rot=(1,0,0;3.14159rad)
  Support = -> [Pocket059]
  sketch-geometry (6):
    g0: Circle CenterX=16.95 CenterY=5 CenterZ=0 NormalX=0 NormalY=0 NormalZ=1 AngleXU=0 Radius=1.5
    g1: Circle CenterX=16.95 CenterY=-5 CenterZ=0 NormalX=0 NormalY=0 NormalZ=1 AngleXU=0 Radius=1.5
    g2: LineSegment StartX=0 StartY=5 StartZ=0 EndX=16.95 EndY=5 EndZ=0
    g3: LineSegment StartX=16.95 StartY=5 StartZ=0 EndX=16.95 EndY=-5 EndZ=0
    g4: LineSegment StartX=16.95 StartY=-5 StartZ=0 EndX=0 EndY=-5 EndZ=0
    g5: LineSegment StartX=0 StartY=-5 StartZ=0 EndX=0 EndY=5 EndZ=0
  constraints (15):
    c: Coincident(g2,g3)
    c: Coincident(g3,g4)
    c: Coincident(g4,g5)
    c: Coincident(g5,g2)
    c: Horizontal(g2)
    c: Horizontal(g4)
    c: Vertical(g3)
    c: Vertical(g5)
    c: Symmetric(g2,g4,g-1)
    c: DistanceY(g3,g3) = 10
    c: DistanceX(g2,g2) = 16.95
    c: Coincident(g0,g2)
    c: Coincident(g1,g3)
    c: Diameter(g1) = 3
    c: Equal(g1,g0)
FEATURE [PartDesign::Pocket] Pocket060
  AllowMultiFace = false
  BaseFeature = -> Pocket059
  Length = 5
  Length2 = 100
  Placement = pos=(0,0,0) rot=(1,0,0;1.5708rad)
  Profile = -> Sketch236
  Type = 0
FEATURE [PartDesign::Body] Body127  label="Servo_Mount_End005"
  Group = -> [Sketch234,Pad158,Sketch235,Pocket059,Sketch236,Pocket060]
  Origin = -> Origin284
  Placement = pos=(-17,-1e-15,81) rot=(0,0,1;3.14159rad)
  Tip = -> Pocket060
FEATURE [PartDesign::FeatureBase] Clone017
  BaseFeature = -> Body127
  Placement = pos=(-17,-1e-15,81) rot=(0,0,1;3.14159rad)
FEATURE [Sketcher::SketchObject] Sketch237
  FullyConstrained = false
  MapMode = 5
  Placement = pos=(0,0,0) rot=(1,0,0;1.5708rad)
  Support = -> [XZ_Plane283]
  sketch-geometry (23):
    g0: LineSegment StartX=-120.4 StartY=121 StartZ=0 EndX=120.4 EndY=121 EndZ=0
    g1: LineSegment StartX=120.4 StartY=121 StartZ=0 EndX=120.4 EndY=81 EndZ=0
    g2: LineSegment StartX=120.4 StartY=81 StartZ=0 EndX=-120.4 EndY=81 EndZ=0
    g3: LineSegment StartX=-120.4 StartY=81 StartZ=0 EndX=-120.4 EndY=121 EndZ=0
    g4: LineSegment StartX=0 StartY=121 StartZ=0 EndX=0 EndY=81 EndZ=0
    g5: LineSegment StartX=-115 StartY=113.5 StartZ=0 EndX=-20.4 EndY=113.5 EndZ=0
    g6: LineSegment StartX=-20.4 StartY=113.5 StartZ=0 EndX=-20.4 EndY=88.5 EndZ=0
    g7: LineSegment StartX=-20.4 StartY=88.5 StartZ=0 EndX=-115 EndY=88.5 EndZ=0
    g8: LineSegment StartX=-115 StartY=88.5 StartZ=0 EndX=-115 EndY=113.5 EndZ=0
    g9: Circle CenterX=-115 CenterY=113.5 CenterZ=0 NormalX=0 NormalY=0 NormalZ=1 AngleXU=0 Radius=2.25
    g10: Circle CenterX=-115 CenterY=88.5 CenterZ=0 NormalX=0 NormalY=0 NormalZ=1 AngleXU=0 Radius=2.25
    g11: Circle CenterX=-20.4 CenterY=88.5 CenterZ=0 NormalX=0 NormalY=0 NormalZ=1 AngleXU=0 Radius=2.25
    g12: Circle CenterX=-20.4 CenterY=113.5 CenterZ=0 NormalX=0 NormalY=0 NormalZ=1 AngleXU=0 Radius=2.25
    g13: LineSegment StartX=20.4 StartY=113.5 StartZ=0 EndX=115 EndY=113.5 EndZ=0
    g14: LineSegment StartX=115 StartY=113.5 StartZ=0 EndX=115 EndY=88.5 EndZ=0
    g15: LineSegment StartX=115 StartY=88.5 StartZ=0 EndX=20.4 EndY=88.5 EndZ=0
    g16: LineSegment StartX=20.4 StartY=88.5 StartZ=0 EndX=20.4 EndY=113.5 EndZ=0
    g17: Circle CenterX=20.4 CenterY=113.5 CenterZ=0 NormalX=0 NormalY=0 NormalZ=1 AngleXU=0 Radius=2.25
    g18: Circle CenterX=115 CenterY=113.5 CenterZ=0 NormalX=0 NormalY=0 NormalZ=1 AngleXU=0 Radius=2.25
    g19: Circle CenterX=20.4 CenterY=88.5 CenterZ=0 NormalX=0 NormalY=0 NormalZ=1 AngleXU=0 Radius=2.25
    g20: Circle CenterX=115 CenterY=88.5 CenterZ=0 NormalX=0 NormalY=0 NormalZ=1 AngleXU=0 Radius=2.25
    g21: LineSegment StartX=-20.4 StartY=88.5 StartZ=0 EndX=20.4 EndY=113.5 EndZ=0
    g22: Circle CenterX=0 CenterY=101 CenterZ=0 NormalX=0 NormalY=0 NormalZ=1 AngleXU=0 Radius=3.25
  constraints (57):
    c: Coincident(g0,g1)
    c: Coincident(g1,g2)
    c: Coincident(g2,g3)
    c: Coincident(g3,g0)
    c: Horizontal(g0)
    c: Horizontal(g2)
    c: Vertical(g1)
    c: Vertical(g3)
    c: Symmetric(g0,g0,g4)
    c: Symmetric(g2,g1,g4)
    c: DistanceX(g2,g4) = 120.4
    c: DistanceY(g4,g4) = 40
    c: DistanceY(g-1,g4) = 81
    c: Coincident(g5,g6)
    c: Coincident(g6,g7)
    c: Coincident(g7,g8)
    c: Coincident(g8,g5)
    c: Horizontal(g5)
    c: Horizontal(g7)
    c: Vertical(g6)
    c: Vertical(g8)
    c: DistanceX(g5,g5) = 94.6
    c: DistanceY(g6,g6) = 25
    c: DistanceX(g2,g7) = 5.4
    c: Coincident(g12,g5)
    c: Coincident(g11,g6)
    c: Coincident(g10,g7)
    c: Coincident(g9,g5)
    c: Diameter(g10) = 4.5
    c: Equal(g10,g9)
    c: Equal(g10,g11)
    c: Equal(g10,g12)
    c: DistanceY(g2,g10) = 7.5
    c: Coincident(g13,g14)
    c: Coincident(g14,g15)
    c: Coincident(g15,g16)
    c: Coincident(g16,g13)
    c: Horizontal(g13)
    c: Horizontal(g15)
    c: Vertical(g14)
    c: Vertical(g16)
    c: Symmetric(g13,g12,g4)
    c: Symmetric(g14,g10,g4)
    c: Coincident(g19,g15)
    c: Coincident(g17,g13)
    c: Coincident(g18,g13)
    c: Coincident(g20,g14)
    c: Diameter(g17) = 4.5
    c: Equal(g17,g19)
    c: Equal(g17,g20)
    c: Equal(g17,g18)
    c: Coincident(g21,g11)
    c: Coincident(g21,g17)
    c: PointOnObject(g22,g21)
    c: PointOnObject(g22,g4)
    c: Diameter(g22) = 6.5
    c: PointOnObject(g22,g-2)
FEATURE [PartDesign::Pad] Pad159
  AllowMultiFace = false
  Direction = (1,1,1)
  Length = 2
  Length2 = 100
  Placement = pos=(0,0,0) rot=(1,0,0;1.5708rad)
  Profile = -> Sketch237
  Type = 0
FEATURE [PartDesign::Body] Body125  label="Outer_Side_Plate002"
  Group = -> [Sketch237,Pad159]
  Origin = -> Origin285
  Placement = pos=(0,13,0) rot=(0,0,1;0rad)
  Tip = -> Pad159
FEATURE [PartDesign::CoordinateSystem] Local_CS_d4f007
  AttacherType = Attacher::AttachEngine3D
FEATURE [Part::Feature] Pcb_d4f007
  Placement = pos=(-90,100,0) rot=(0,0,1;0rad)
  shape: bbox 66 x 50 x 1.6 mm, 84 faces (baked)
FEATURE [Sketcher::SketchObject] PCB_Sketch_d4f007
  FullyConstrained = false
  sketch-geometry (8):
    g0: LineSegment StartX=4e-16 StartY=3 StartZ=0 EndX=-3.6e-15 EndY=47 EndZ=0
    g1: LineSegment StartX=63 StartY=8.4e-15 StartZ=0 EndX=3 EndY=4e-16 EndZ=0
    g2: LineSegment StartX=66 StartY=47 StartZ=0 EndX=66 EndY=3 EndZ=0
    g3: LineSegment StartX=3 StartY=50 StartZ=0 EndX=63 EndY=50 EndZ=0
    g4: ArcOfCircle CenterX=63 CenterY=47 CenterZ=0 NormalX=0 NormalY=0 NormalZ=1 AngleXU=0 Radius=3 StartAngle=0 EndAngle=1.5708
    g5: ArcOfCircle CenterX=63 CenterY=3 CenterZ=0 NormalX=0 NormalY=0 NormalZ=1 AngleXU=0 Radius=3 StartAngle=4.71239 EndAngle=6.28319
    g6: ArcOfCircle CenterX=3 CenterY=3 CenterZ=0 NormalX=0 NormalY=0 NormalZ=1 AngleXU=0 Radius=3 StartAngle=3.14159 EndAngle=4.71239
    g7: ArcOfCircle CenterX=3 CenterY=47 CenterZ=0 NormalX=0 NormalY=0 NormalZ=1 AngleXU=0 Radius=3 StartAngle=1.5708 EndAngle=3.14159
  constraints (8):
    c: Coincident(g0,g6)
    c: Coincident(g0,g7)
    c: Coincident(g1,g6)
    c: Coincident(g3,g7)
    c: Coincident(g1,g5)
    c: Coincident(g3,g4)
    c: Coincident(g2,g5)
    c: Coincident(g2,g4)
FEATURE [App::Part] Board_Geoms_d4f007  label="Board_Geoms_d4f011"
  Group = -> [Local_CS_d4f007,Pcb_d4f007,PCB_Sketch_d4f007]
  Origin = -> Origin286
FEATURE [Part::Feature] Shape178  label="U2_SOT_353_SC_70_5_5F717A016"
  Placement = pos=(26,15.25,0) rot=(0,0,1;3.14159rad)
  shape: bbox 2 x 2 x 1.05 mm, 104 faces (baked)
FEATURE [Part::Feature] Shape179  label="U1_SOT_353_SC_70_5_5F7179FD004"
  Placement = pos=(26,19.75,0) rot=(0,0,1;3.14159rad)
  shape: bbox 2 x 2 x 1.05 mm, 104 faces (baked)
FEATURE [Part::Feature] Shape180  label="SW1_SW_PUSH_6mm_5F7179E012"
  Placement = pos=(41.5,37.75,0) rot=(0,0,1;3.14159rad)
  shape: bbox 7.174 x 6 x 7.8 mm, 105 faces (baked)
FEATURE [Part::Feature] Shape181  label="R7_R_0603_1608Metric_5F7179C013"
  Placement = pos=(44.25,36.5,0) rot=(0,0,1;1.5708rad)
  shape: bbox 0.8 x 1.6 x 0.45 mm, 26 faces (baked)
FEATURE [Part::Feature] Shape182  label="R6_R_0603_1608Metric_5F7179B012"
  Placement = pos=(33.25,15.75,0) rot=(0,0,1;1.5708rad)
  shape: bbox 0.8 x 1.6 x 0.45 mm, 26 faces (baked)
FEATURE [Part::Feature] Shape183  label="R5_R_0603_1608Metric_5F7179A011"
  Placement = pos=(30.75,15.75,0) rot=(0,0,1;1.5708rad)
  shape: bbox 0.8 x 1.6 x 0.45 mm, 26 faces (baked)
FEATURE [Part::Feature] Shape184  label="R4_R_0603_1608Metric_5F718000"
  Placement = pos=(15.175,35.57,0) rot=(0,0,1;3.14159rad)
  shape: bbox 1.6 x 0.8 x 0.45 mm, 26 faces (baked)
FEATURE [Part::Feature] Shape185  label="R3_R_0603_1608Metric_5F717989"
  Placement = pos=(15.175,38.11,0) rot=(0,0,1;3.14159rad)
  shape: bbox 1.6 x 0.8 x 0.45 mm, 26 faces (baked)
FEATURE [Part::Feature] Shape186  label="R2_R_0603_1608Metric_5F717978"
  Placement = pos=(15.175,40.65,0) rot=(0,0,1;3.14159rad)
  shape: bbox 1.6 x 0.8 x 0.45 mm, 26 faces (baked)
FEATURE [Part::Feature] Shape187  label="R1_R_0603_1608Metric_5F717967"
  Placement = pos=(15.175,43.19,0) rot=(0,0,1;3.14159rad)
  shape: bbox 1.6 x 0.8 x 0.45 mm, 26 faces (baked)
FEATURE [Part::Feature] Shape188  label="J13_MSTBA_01x02_G_5_08mm_5F717956"
  Placement = pos=(44,3.5,0) rot=(0,0,1;0rad)
  shape: bbox 12.16 x 12 x 12.6 mm, 63 faces (baked)
FEATURE [Part::Feature] Shape189  label="J12_PinHeader_1x06_P254mm_Vertical_5F71792E004"
  Placement = pos=(34.95,46.25,0) rot=(0,0,1;1.5708rad)
  shape: bbox 15.24 x 2.54 x 11.54 mm, 148 faces (baked)
FEATURE [Part::Feature] Shape190  label="J11_PinHeader_1x03_P254mm_Vertical_5F717918"
  Placement = pos=(1.84,13.98,0) rot=(0,0,1;1.5708rad)
  shape: bbox 7.62 x 2.54 x 11.54 mm, 76 faces (baked)
FEATURE [Part::Feature] Shape191  label="J10_PinHeader_1x03_P254mm_Vertical_5F7178FD004"
  Placement = pos=(1.84,16.52,0) rot=(0,0,1;1.5708rad)
  shape: bbox 7.62 x 2.54 x 11.54 mm, 76 faces (baked)
FEATURE [Part::Feature] Shape192  label="J9_MSTBA_01x04_G_5_08mm_5F7178E010"
  Placement = pos=(20.5,3.5,0) rot=(0,0,1;0rad)
  shape: bbox 22.32 x 12 x 12.6 mm, 113 faces (baked)
FEATURE [Part::Feature] Shape193  label="J8_PinSocket_1x15_P254mm_Vertical_5F7178B016"
  Placement = pos=(12,47,-1.6) rot=(0,1,0;3.14159rad)
  shape: bbox 2.54 x 38.1 x 10.1 mm, 475 faces (baked)
FEATURE [App::Part] Bot_d4f007  label="Bot_d4f011"
  Group = -> [Shape177,Shape193]
  Origin = -> Origin290
FEATURE [Part::Feature] Shape194  label="J7_SHF-105-01-L-D-SM-K-TR_5F717899"
  Placement = pos=(48,17.25,0) rot=(0.57735,0.57735,0.57735;2.0944rad)
  shape: bbox 6.502 x 12.7 x 5.588 mm, 207 faces, 4 solids (baked)
FEATURE [Part::Feature] Shape195  label="J6_PinHeader_1x03_P254mm_Vertical_5F717879"
  Placement = pos=(1.84,33.03,0) rot=(0,0,1;1.5708rad)
  shape: bbox 7.62 x 2.54 x 11.54 mm, 76 faces (baked)
FEATURE [Part::Feature] Shape196  label="J5_PinHeader_1x03_P254mm_Vertical_5F723001"
  Placement = pos=(1.84,35.57,0) rot=(0,0,1;1.5708rad)
  shape: bbox 7.62 x 2.54 x 11.54 mm, 76 faces (baked)
FEATURE [Part::Feature] Shape197  label="J4_Molex_AE_6410_06A_5F717851"
  Placement = pos=(61.62,35.57,0) rot=(0,0,-1;1.5708rad)
  shape: bbox 5.8 x 15.24 x 15.26 mm, 169 faces (baked)
FEATURE [Part::Feature] Shape198  label="J2_PinHeader_1x03_P254mm_Vertical_5F7177F004"
  Placement = pos=(1.84,38.11,0) rot=(0,0,1;1.5708rad)
  shape: bbox 7.62 x 2.54 x 11.54 mm, 76 faces (baked)
FEATURE [Part::Feature] Shape199  label="J1_PinHeader_1x03_P254mm_Vertical_5F7228CA004"
  Placement = pos=(1.84,40.65,0) rot=(0,0,1;1.5708rad)
  shape: bbox 7.62 x 2.54 x 11.54 mm, 76 faces (baked)
FEATURE [Part::Feature] Shape200  label="D6_LED_0603_1608Metric_5F71855F004"
  Placement = pos=(33.25,12.25,0) rot=(0,0,1;1.5708rad)
  shape: bbox 0.8 x 1.6 x 1.1 mm, 50 faces (baked)
FEATURE [Part::Feature] Shape201  label="D5_LED_0603_1608Metric_5F71778F004"
  Placement = pos=(30.75,12.25,0) rot=(0,0,1;1.5708rad)
  shape: bbox 0.8 x 1.6 x 1.1 mm, 50 faces (baked)
FEATURE [Part::Feature] Shape202  label="D4_SOT_23_5F71777C004"
  Placement = pos=(18.985,35.57,0) rot=(0,0,1;0rad)
  shape: bbox 2.5 x 3 x 1.2 mm, 76 faces (baked)
FEATURE [Part::Feature] Shape203  label="D3_SOT_23_5F717771"
  Placement = pos=(22.795,38.11,0) rot=(0,0,1;0rad)
  shape: bbox 2.5 x 3 x 1.2 mm, 76 faces (baked)
FEATURE [Part::Feature] Shape204  label="D2_SOT_23_5F717756"
  Placement = pos=(18.985,40.65,0) rot=(0,0,1;0rad)
  shape: bbox 2.5 x 3 x 1.2 mm, 76 faces (baked)
FEATURE [Part::Feature] Shape205  label="D1_SOT_23_5F71773D004"
  Placement = pos=(22.795,43.19,0) rot=(0,0,1;0rad)
  shape: bbox 2.5 x 3 x 1.2 mm, 76 faces (baked)
FEATURE [Part::Feature] Shape206  label="C7_C_0603_1608Metric_5F717732"
  Placement = pos=(4.5,27.5,0) rot=(0,0,1;0rad)
  shape: bbox 1.6 x 0.8 x 0.8 mm, 28 faces (baked)
FEATURE [Part::Feature] Shape207  label="C6_C_0603_1608Metric_5F717721"
  Placement = pos=(6.25,25.75,0) rot=(0,0,1;0rad)
  shape: bbox 1.6 x 0.8 x 0.8 mm, 28 faces (baked)
FEATURE [Part::Feature] Shape208  label="C5_C_0603_1608Metric_5F717710"
  Placement = pos=(4.5,20.25,0) rot=(0,0,1;0rad)
  shape: bbox 1.6 x 0.8 x 0.8 mm, 28 faces (baked)
FEATURE [Part::Feature] Shape209  label="C4_C_0603_1608Metric_5F7176F009"
  Placement = pos=(41.5,15.25,0) rot=(0,0,1;0rad)
  shape: bbox 1.6 x 0.8 x 0.8 mm, 28 faces (baked)
FEATURE [Part::Feature] Shape210  label="C3_C_0603_1608Metric_5F7176E008"
  Placement = pos=(32.5,39.75,0) rot=(0,0,1;1.5708rad)
  shape: bbox 0.8 x 1.6 x 0.8 mm, 28 faces (baked)
FEATURE [Part::Feature] Shape211  label="C2_C_0603_1608Metric_5F7176D007"
  Placement = pos=(38.25,33,0) rot=(0,0,1;0rad)
  shape: bbox 1.6 x 0.8 x 0.8 mm, 28 faces (baked)
FEATURE [Part::Feature] Shape212  label="C1_C_0805_2012Metric_5F7176C006"
  Placement = pos=(38.25,35,0) rot=(0,0,1;0rad)
  shape: bbox 2 x 1.25 x 1.25 mm, 28 faces (baked)
FEATURE [App::Part] Top_d4f007  label="Top_d4f011"
  Group = -> [Shape176,Shape174,Shape175,Shape172,Shape173,Shape178,Shape179,Shape180,Shape181,Shape182,Shape183,Shape184,Shape185,Shape186,Shape187,Shape188,Shape189,Shape190,Shape191,Shape192,Shape194,Shape195,Shape196,Shape197,Shape198,Shape199,Shape200,Shape201,Shape202,Shape203,Shape204,Shape205,Shape206,Shape207,Shape208,Shape209,Shape210,Shape211,Shape212]
  Origin = -> Origin289
FEATURE [App::Part] Step_Models_d4f007  label="Step_Models_d4f011"
  Group = -> [Top_d4f007,Bot_d4f007]
  Origin = -> Origin288
FEATURE [App::Part] Board_d4f007  label="motor_board004"
  Group = -> [Board_Geoms_d4f007,Step_Models_d4f007]
  Origin = -> Origin287
FEATURE [Sketcher::SketchObject] Sketch238
  FullyConstrained = false
  MapMode = 5
  Support = -> [XY_Plane292]
  sketch-geometry (66):
    g0: LineSegment StartX=0 StartY=41.4 StartZ=0 EndX=47.35 EndY=41.4 EndZ=0
    g1: LineSegment StartX=47.35 StartY=41.4 StartZ=0 EndX=47.35 EndY=0 EndZ=0
    g2: LineSegment StartX=47.35 StartY=0 StartZ=0 EndX=0 EndY=0 EndZ=0
    g3: LineSegment StartX=0 StartY=0 StartZ=0 EndX=0 EndY=41.4 EndZ=0
    g4: LineSegment StartX=2.72 StartY=2.92 StartZ=0 EndX=2.72 EndY=5.46 EndZ=0
    g5: LineSegment StartX=2.72 StartY=5.46 StartZ=0 EndX=2.72 EndY=8 EndZ=0
    g6: LineSegment StartX=2.72 StartY=8 StartZ=0 EndX=2.72 EndY=10.54 EndZ=0
    g7: LineSegment StartX=2.72 StartY=10.54 StartZ=0 EndX=2.72 EndY=13.08 EndZ=0
    g8: LineSegment StartX=2.72 StartY=13.08 StartZ=0 EndX=2.72 EndY=15.62 EndZ=0
    g9: LineSegment StartX=2.72 StartY=15.62 StartZ=0 EndX=2.72 EndY=18.16 EndZ=0
    g10: LineSegment StartX=2.72 StartY=18.16 StartZ=0 EndX=2.72 EndY=20.7 EndZ=0
    g11: LineSegment StartX=2.72 StartY=20.7 StartZ=0 EndX=2.72 EndY=23.24 EndZ=0
    g12: LineSegment StartX=2.72 StartY=23.24 StartZ=0 EndX=2.72 EndY=25.78 EndZ=0
    g13: LineSegment StartX=2.72 StartY=25.78 StartZ=0 EndX=2.72 EndY=28.32 EndZ=0
    g14: LineSegment StartX=2.72 StartY=28.32 StartZ=0 EndX=2.72 EndY=30.86 EndZ=0
    g15: LineSegment StartX=2.72 StartY=30.86 StartZ=0 EndX=2.72 EndY=33.4 EndZ=0
    g16: LineSegment StartX=2.72 StartY=33.4 StartZ=0 EndX=2.72 EndY=35.94 EndZ=0
    g17: LineSegment StartX=2.72 StartY=35.94 StartZ=0 EndX=2.72 EndY=38.48 EndZ=0
    g18: LineSegment StartX=44.63 StartY=2.92 StartZ=0 EndX=44.63 EndY=5.46 EndZ=0
    g19: LineSegment StartX=44.63 StartY=5.46 StartZ=0 EndX=44.63 EndY=8 EndZ=0
    g20: LineSegment StartX=44.63 StartY=8 StartZ=0 EndX=44.63 EndY=10.54 EndZ=0
    g21: LineSegment StartX=44.63 StartY=10.54 StartZ=0 EndX=44.63 EndY=13.08 EndZ=0
    g22: LineSegment StartX=44.63 StartY=13.08 StartZ=0 EndX=44.63 EndY=15.62 EndZ=0
    g23: LineSegment StartX=44.63 StartY=15.62 StartZ=0 EndX=44.63 EndY=18.16 EndZ=0
    g24: LineSegment StartX=44.63 StartY=18.16 StartZ=0 EndX=44.63 EndY=20.7 EndZ=0
    g25: LineSegment StartX=44.63 StartY=20.7 StartZ=0 EndX=44.63 EndY=23.24 EndZ=0
    g26: LineSegment StartX=44.63 StartY=23.24 StartZ=0 EndX=44.63 EndY=25.78 EndZ=0
    g27: LineSegment StartX=44.63 StartY=25.78 StartZ=0 EndX=44.63 EndY=28.32 EndZ=0
    g28: LineSegment StartX=44.63 StartY=28.32 StartZ=0 EndX=44.63 EndY=30.86 EndZ=0
    g29: LineSegment StartX=44.63 StartY=30.86 StartZ=0 EndX=44.63 EndY=33.4 EndZ=0
    g30: LineSegment StartX=44.63 StartY=33.4 StartZ=0 EndX=44.63 EndY=35.94 EndZ=0
    g31: LineSegment StartX=44.63 StartY=35.94 StartZ=0 EndX=44.63 EndY=38.48 EndZ=0
    g32: LineSegment StartX=0 StartY=0 StartZ=0 EndX=2.72 EndY=2.92 EndZ=0
    g33: LineSegment StartX=44.63 StartY=2.92 StartZ=0 EndX=47.35 EndY=0 EndZ=0
    g34: LineSegment StartX=44.63 StartY=38.48 StartZ=0 EndX=47.35 EndY=41.4 EndZ=0
    g35: LineSegment StartX=2.72 StartY=38.48 StartZ=0 EndX=0 EndY=41.4 EndZ=0
    g36: Circle CenterX=2.72 CenterY=38.48 CenterZ=0 NormalX=0 NormalY=0 NormalZ=1 AngleXU=0 Radius=0.5
    g37: Circle CenterX=2.72 CenterY=35.94 CenterZ=0 NormalX=0 NormalY=0 NormalZ=1 AngleXU=0 Radius=0.5
    g38: Circle CenterX=2.72 CenterY=33.4 CenterZ=0 NormalX=0 NormalY=0 NormalZ=1 AngleXU=0 Radius=0.5
    g39: Circle CenterX=2.72 CenterY=30.86 CenterZ=0 NormalX=0 NormalY=0 NormalZ=1 AngleXU=0 Radius=0.5
    g40: Circle CenterX=2.72 CenterY=28.32 CenterZ=0 NormalX=0 NormalY=0 NormalZ=1 AngleXU=0 Radius=0.5
    g41: Circle CenterX=2.72 CenterY=25.78 CenterZ=0 NormalX=0 NormalY=0 NormalZ=1 AngleXU=0 Radius=0.5
    g42: Circle CenterX=2.72 CenterY=23.24 CenterZ=0 NormalX=0 NormalY=0 NormalZ=1 AngleXU=0 Radius=0.5
    g43: Circle CenterX=2.72 CenterY=20.7 CenterZ=0 NormalX=0 NormalY=0 NormalZ=1 AngleXU=0 Radius=0.5
    g44: Circle CenterX=2.72 CenterY=18.16 CenterZ=0 NormalX=0 NormalY=0 NormalZ=1 AngleXU=0 Radius=0.5
    g45: Circle CenterX=2.72 CenterY=15.62 CenterZ=0 NormalX=0 NormalY=0 NormalZ=1 AngleXU=0 Radius=0.5
    g46: Circle CenterX=2.72 CenterY=13.08 CenterZ=0 NormalX=0 NormalY=0 NormalZ=1 AngleXU=0 Radius=0.5
    g47: Circle CenterX=2.72 CenterY=10.54 CenterZ=0 NormalX=0 NormalY=0 NormalZ=1 AngleXU=0 Radius=0.5
    g48: Circle CenterX=2.72 CenterY=8 CenterZ=0 NormalX=0 NormalY=0 NormalZ=1 AngleXU=0 Radius=0.5
    g49: Circle CenterX=2.72 CenterY=5.46 CenterZ=0 NormalX=0 NormalY=0 NormalZ=1 AngleXU=0 Radius=0.5
    g50: Circle CenterX=2.72 CenterY=2.92 CenterZ=0 NormalX=0 NormalY=0 NormalZ=1 AngleXU=0 Radius=0.5
    g51: Circle CenterX=44.63 CenterY=38.48 CenterZ=0 NormalX=0 NormalY=0 NormalZ=1 AngleXU=0 Radius=0.5
    g52: Circle CenterX=44.63 CenterY=35.94 CenterZ=0 NormalX=0 NormalY=0 NormalZ=1 AngleXU=0 Radius=0.5
    g53: Circle CenterX=44.63 CenterY=33.4 CenterZ=0 NormalX=0 NormalY=0 NormalZ=1 AngleXU=0 Radius=0.5
    g54: Circle CenterX=44.63 CenterY=30.86 CenterZ=0 NormalX=0 NormalY=0 NormalZ=1 AngleXU=0 Radius=0.5
    g55: Circle CenterX=44.63 CenterY=28.32 CenterZ=0 NormalX=0 NormalY=0 NormalZ=1 AngleXU=0 Radius=0.5
    g56: Circle CenterX=44.63 CenterY=25.78 CenterZ=0 NormalX=0 NormalY=0 NormalZ=1 AngleXU=0 Radius=0.5
    g57: Circle CenterX=44.63 CenterY=23.24 CenterZ=0 NormalX=0 NormalY=0 NormalZ=1 AngleXU=0 Radius=0.5
    g58: Circle CenterX=44.63 CenterY=20.7 CenterZ=0 NormalX=0 NormalY=0 NormalZ=1 AngleXU=0 Radius=0.5
    g59: Circle CenterX=44.63 CenterY=18.16 CenterZ=0 NormalX=0 NormalY=0 NormalZ=1 AngleXU=0 Radius=0.5
    g60: Circle CenterX=44.63 CenterY=15.62 CenterZ=0 NormalX=0 NormalY=0 NormalZ=1 AngleXU=0 Radius=0.5
    g61: Circle CenterX=44.63 CenterY=13.08 CenterZ=0 NormalX=0 NormalY=0 NormalZ=1 AngleXU=0 Radius=0.5
    g62: Circle CenterX=44.63 CenterY=10.54 CenterZ=0 NormalX=0 NormalY=0 NormalZ=1 AngleXU=0 Radius=0.5
    g63: Circle CenterX=44.63 CenterY=8 CenterZ=0 NormalX=0 NormalY=0 NormalZ=1 AngleXU=0 Radius=0.5
    g64: Circle CenterX=44.63 CenterY=5.46 CenterZ=0 NormalX=0 NormalY=0 NormalZ=1 AngleXU=0 Radius=0.5
    g65: Circle CenterX=44.63 CenterY=2.92 CenterZ=0 NormalX=0 NormalY=0 NormalZ=1 AngleXU=0 Radius=0.5
  constraints (152):
    c: Coincident(g0,g1)
    c: Coincident(g1,g2)
    c: Coincident(g2,g3)
    c: Coincident(g3,g0)
    c: Horizontal(g0)
    c: Horizontal(g2)
    c: Vertical(g1)
    c: Vertical(g3)
    c: DistanceX(g0,g0) = 47.35
    c: DistanceY(g1,g1) = 41.4
    c: Coincident(g2,g-1)
    c: Coincident(g4,g5)
    c: Coincident(g5,g6)
    c: Coincident(g6,g7)
    c: Coincident(g7,g8)
    c: Coincident(g8,g9)
    c: Coincident(g9,g10)
    c: Coincident(g10,g11)
    c: Coincident(g11,g12)
    c: Coincident(g12,g13)
    c: Coincident(g13,g14)
    c: Coincident(g14,g15)
    c: Coincident(g15,g16)
    c: Coincident(g16,g17)
    c: Coincident(g18,g19)
    c: Coincident(g19,g20)
    c: Coincident(g20,g21)
    c: Coincident(g21,g22)
    c: Coincident(g22,g23)
    c: Coincident(g23,g24)
    c: Coincident(g24,g25)
    c: Coincident(g25,g26)
    c: Coincident(g26,g27)
    c: Coincident(g27,g28)
    c: Coincident(g28,g29)
    c: Coincident(g29,g30)
    c: Coincident(g30,g31)
    c: Vertical(g17)
    c: Vertical(g16)
    c: Vertical(g15)
    c: Vertical(g14)
    c: Vertical(g13)
    c: Vertical(g12)
    c: Vertical(g11)
    c: Vertical(g10)
    c: Vertical(g9)
    c: Vertical(g8)
    c: Vertical(g7)
    c: Vertical(g6)
    c: Vertical(g5)
    c: Vertical(g4)
    c: Equal(g17,g16)
    c: Equal(g16,g15)
    c: Equal(g15,g14)
    c: Equal(g14,g13)
    c: Equal(g13,g12)
    c: Equal(g12,g11)
    c: Equal(g11,g10)
    c: Equal(g10,g9)
    c: Equal(g9,g8)
    c: Equal(g8,g7)
    c: Equal(g7,g6)
    c: Equal(g6,g5)
    c: Equal(g5,g4)
    c: DistanceY(g4,g4) = 2.54
    c: Vertical(g18)
    c: Vertical(g19)
    c: Vertical(g20)
    c: Vertical(g21)
    c: Vertical(g22)
    c: Vertical(g23)
    c: Vertical(g24)
    c: Vertical(g25)
    c: Vertical(g26)
    c: Vertical(g27)
    c: Vertical(g28)
    c: Vertical(g29)
    c: Vertical(g30)
    c: Vertical(g31)
    c: Equal(g31,g30)
    c: Equal(g30,g29)
    c: Equal(g29,g28)
    c: Equal(g28,g27)
    c: Equal(g27,g26)
    c: Equal(g26,g25)
    c: Equal(g25,g24)
    c: Equal(g24,g23)
    c: Equal(g23,g22)
    c: Equal(g22,g21)
    c: Equal(g21,g20)
    c: Equal(g20,g19)
    c: Equal(g19,g18)
    c: Equal(g18,g4)
    c: DistanceX(g4,g18) = 41.91
    c: Coincident(g33,g1)
    c: Coincident(g33,g18)
    c: Coincident(g4,g32)
    c: Coincident(g32,g2)
    c: Equal(g32,g33)
    c: Coincident(g35,g17)
    c: Coincident(g35,g0)
    c: Coincident(g34,g31)
    c: Coincident(g34,g0)
    c: Equal(g34,g33)
    c: Equal(g33,g35)
    c: Coincident(g50,g4)
    c: Coincident(g49,g4)
    c: Coincident(g48,g5)
    c: Coincident(g47,g6)
    c: Coincident(g46,g7)
    c: Coincident(g45,g8)
    c: Coincident(g44,g9)
    c: Coincident(g43,g10)
    c: Coincident(g42,g11)
    c: Coincident(g41,g12)
    c: Coincident(g40,g13)
    c: Coincident(g39,g14)
    c: Coincident(g38,g15)
    c: Coincident(g37,g16)
    c: Coincident(g36,g17)
    c: Coincident(g65,g18)
    c: Coincident(g64,g18)
    c: Coincident(g63,g19)
    c: Coincident(g62,g20)
    c: Coincident(g61,g21)
    c: Coincident(g60,g22)
    c: Coincident(g59,g23)
    c: Coincident(g58,g24)
    c: Coincident(g57,g25)
    c: Coincident(g56,g26)
    c: Coincident(g55,g27)
    c: Coincident(g54,g28)
    c: Coincident(g53,g29)
    c: Coincident(g52,g30)
    c: Coincident(g51,g31)
    c: Diameter(g36) = 1
    c: Equal(g36, g37-g50) x14
    c: Equal(g36,g65)
    c: Equal(g36,g64)
    c: Equal(g36,g63)
    c: Equal(g36,g62)
    c: Equal(g36,g61)
    c: Equal(g36,g60)
    c: Equal(g36,g59)
    c: Equal(g36,g58)
    c: Equal(g36,g57)
    c: Equal(g36,g56)
    c: Equal(g36,g55)
    c: Equal(g36,g54)
    c: Equal(g36,g53)
    c: Equal(g36,g52)
    c: Equal(g36,g51)
FEATURE [PartDesign::Pad] Pad160
  AllowMultiFace = false
  Direction = (1,1,1)
  Length = 1.6
  Length2 = 100
  Profile = -> Sketch238
  Reversed = true
  Type = 0
FEATURE [PartDesign::Body] Body128  label="PCB004"
  Group = -> [Sketch238,Pad160]
  Origin = -> Origin292
  Tip = -> Pad160
FEATURE [Part::Feature] Shape213  label="J3_PinHeader_1x15_P254mm_Vertical_5F717822"
  Placement = pos=(2.75,38.5,-5.2e-15) rot=(0,0,1;0rad)
  shape: bbox 2.54 x 38.1 x 11.54 mm, 364 faces (baked)
FEATURE [Part::Feature] Shape214  label="J8_PinSocket_1x15_P254mm_Vertical_5F7178B017"
  Placement = pos=(44.65,38.5,4e-15) rot=(0,0,1;0rad)
  shape: bbox 2.54 x 38.1 x 10.1 mm, 475 faces (baked)
FEATURE [Sketcher::SketchObject] Sketch239
  FullyConstrained = false
  MapMode = 5
  Support = -> [XY_Plane293]
  sketch-geometry (1):
    g0: Circle CenterX=0 CenterY=0 CenterZ=0 NormalX=0 NormalY=0 NormalZ=1 AngleXU=0 Radius=4.15
  constraints (2):
    c: Coincident(g0,g-1)
    c: Diameter(g0) = 8.3
FEATURE [PartDesign::Pad] Pad161
  AllowMultiFace = false
  Direction = (1,1,1)
  Length = 10.5
  Length2 = 100
  Profile = -> Sketch239
  Type = 0
FEATURE [PartDesign::Body] Body129  label="Capacitor004"
  Group = -> [Sketch239,Pad161]
  Origin = -> Origin293
  Placement = pos=(10,14.5,-1.6) rot=(0,1,0;3.14159rad)
  Tip = -> Pad161
FEATURE [Sketcher::SketchObject] Sketch240
  FullyConstrained = false
  MapMode = 5
  Placement = pos=(0,0,0) rot=(1,0,0;1.5708rad)
  Support = -> [XZ_Plane293]
  sketch-geometry (31):
    g0: LineSegment StartX=-128 StartY=129 StartZ=0 EndX=128 EndY=129 EndZ=0
    g1: LineSegment StartX=128 StartY=129 StartZ=0 EndX=128 EndY=81 EndZ=0
    g2: LineSegment StartX=128 StartY=81 StartZ=0 EndX=-128 EndY=81 EndZ=0
    g3: LineSegment StartX=-128 StartY=81 StartZ=0 EndX=-128 EndY=129 EndZ=0
    g4: LineSegment StartX=0 StartY=129 StartZ=0 EndX=0 EndY=81 EndZ=0
    g5: LineSegment StartX=-115 StartY=113.5 StartZ=0 EndX=-20.4 EndY=113.5 EndZ=0
    g6: LineSegment StartX=-20.4 StartY=113.5 StartZ=0 EndX=-20.4 EndY=88.5 EndZ=0
    g7: LineSegment StartX=-20.4 StartY=88.5 StartZ=0 EndX=-115 EndY=88.5 EndZ=0
    g8: LineSegment StartX=-115 StartY=88.5 StartZ=0 EndX=-115 EndY=113.5 EndZ=0
    g9: Circle CenterX=-115 CenterY=113.5 CenterZ=0 NormalX=0 NormalY=0 NormalZ=1 AngleXU=0 Radius=2.25
    g10: Circle CenterX=-115 CenterY=88.5 CenterZ=0 NormalX=0 NormalY=0 NormalZ=1 AngleXU=0 Radius=2.25
    g11: Circle CenterX=-20.4 CenterY=88.5 CenterZ=0 NormalX=0 NormalY=0 NormalZ=1 AngleXU=0 Radius=2.25
    g12: Circle CenterX=-20.4 CenterY=113.5 CenterZ=0 NormalX=0 NormalY=0 NormalZ=1 AngleXU=0 Radius=2.25
    g13: LineSegment StartX=20.4 StartY=113.5 StartZ=0 EndX=115 EndY=113.5 EndZ=0
    g14: LineSegment StartX=115 StartY=113.5 StartZ=0 EndX=115 EndY=88.5 EndZ=0
    g15: LineSegment StartX=115 StartY=88.5 StartZ=0 EndX=20.4 EndY=88.5 EndZ=0
    g16: LineSegment StartX=20.4 StartY=88.5 StartZ=0 EndX=20.4 EndY=113.5 EndZ=0
    g17: Circle CenterX=20.4 CenterY=113.5 CenterZ=0 NormalX=0 NormalY=0 NormalZ=1 AngleXU=0 Radius=2.25
    g18: Circle CenterX=115 CenterY=113.5 CenterZ=0 NormalX=0 NormalY=0 NormalZ=1 AngleXU=0 Radius=2.25
    g19: Circle CenterX=20.4 CenterY=88.5 CenterZ=0 NormalX=0 NormalY=0 NormalZ=1 AngleXU=0 Radius=2.25
    g20: Circle CenterX=115 CenterY=88.5 CenterZ=0 NormalX=0 NormalY=0 NormalZ=1 AngleXU=0 Radius=2.25
    g21: Circle CenterX=-125 CenterY=126 CenterZ=0 NormalX=0 NormalY=0 NormalZ=1 AngleXU=0 Radius=1.75
    g22: Circle CenterX=-125 CenterY=84 CenterZ=0 NormalX=0 NormalY=0 NormalZ=1 AngleXU=0 Radius=1.75
    g23: Circle CenterX=-67 CenterY=126 CenterZ=0 NormalX=0 NormalY=0 NormalZ=1 AngleXU=0 Radius=1.75
    g24: Circle CenterX=67 CenterY=126 CenterZ=0 NormalX=0 NormalY=0 NormalZ=1 AngleXU=0 Radius=1.75
    g25: Circle CenterX=125 CenterY=126 CenterZ=0 NormalX=0 NormalY=0 NormalZ=1 AngleXU=0 Radius=1.75
    g26: Circle CenterX=125 CenterY=84 CenterZ=0 NormalX=0 NormalY=0 NormalZ=1 AngleXU=0 Radius=1.75
    g27: Circle CenterX=0 CenterY=101 CenterZ=0 NormalX=0 NormalY=0 NormalZ=1 AngleXU=0 Radius=3.25
    g28: LineSegment StartX=-20.4 StartY=88.5 StartZ=0 EndX=20.4 EndY=113.5 EndZ=0
    g29: Circle CenterX=60 CenterY=124 CenterZ=0 NormalX=0 NormalY=0 NormalZ=1 AngleXU=0 Radius=2.25
    g30: Circle CenterX=-60 CenterY=124 CenterZ=0 NormalX=0 NormalY=0 NormalZ=1 AngleXU=0 Radius=2.25
  constraints (77):
    c: Coincident(g0,g1)
    c: Coincident(g1,g2)
    c: Coincident(g2,g3)
    c: Coincident(g3,g0)
    c: Horizontal(g0)
    c: Horizontal(g2)
    c: Vertical(g1)
    c: Vertical(g3)
    c: Symmetric(g0,g0,g4)
    c: Symmetric(g2,g1,g4)
    c: DistanceX(g2,g4) = 128
    c: DistanceY(g4,g4) = 48
    c: DistanceY(g-1,g4) = 81
    c: Coincident(g5,g6)
    c: Coincident(g6,g7)
    c: Coincident(g7,g8)
    c: Coincident(g8,g5)
    c: Horizontal(g5)
    c: Horizontal(g7)
    c: Vertical(g6)
    c: Vertical(g8)
    c: DistanceX(g5,g5) = 94.6
    c: DistanceY(g6,g6) = 25
    c: DistanceX(g2,g7) = 13
    c: Coincident(g12,g5)
    c: Coincident(g11,g6)
    c: Coincident(g10,g7)
    c: Coincident(g9,g5)
    c: Diameter(g10) = 4.5
    c: Equal(g10,g9)
    c: Equal(g10,g11)
    c: Equal(g10,g12)
    c: DistanceY(g2,g10) = 7.5
    c: Coincident(g13,g14)
    c: Coincident(g14,g15)
    c: Coincident(g15,g16)
    c: Coincident(g16,g13)
    c: Horizontal(g13)
    c: Horizontal(g15)
    c: Vertical(g14)
    c: Vertical(g16)
    c: Symmetric(g13,g12,g4)
    c: Symmetric(g14,g10,g4)
    c: Coincident(g19,g15)
    c: Coincident(g17,g13)
    c: Coincident(g18,g13)
    c: Coincident(g20,g14)
    c: Diameter(g17) = 4.5
    c: Equal(g17,g19)
    c: Equal(g17,g20)
    c: Equal(g17,g18)
    c: DistanceY(g22,g21) = 42
    c: Horizontal(g23,g21)
    c: DistanceX(g21,g23) = 58
    c: Vertical(g22,g21)
    c: DistanceX(g22,g10) = 10
    c: DistanceY(g2,g22) = 3
    c: Diameter(g23) = 3.5
    c: Equal(g23,g21)
    c: Equal(g23,g22)
    c: Diameter(g24) = 3.5
    c: Equal(g24,g25)
    c: Equal(g24,g26)
    c: Symmetric(g24,g23,g4)
    c: Symmetric(g25,g21,g4)
    c: Symmetric(g26,g22,g4)
    c: PointOnObject(g27,g4)
    c: Coincident(g28,g11)
    c: Coincident(g28,g17)
    c: PointOnObject(g27,g28)
    c: Diameter(g27) = 6.5
    c: PointOnObject(g27,g-2)
    c: Diameter(g29) = 4.5
    c: Equal(g29,g30)
    c: DistanceX(g-1,g29) = 60
    c: DistanceY(g-1,g29) = 124
    c: Symmetric(g29,g30,g-2)
FEATURE [PartDesign::Pad] Pad162
  AllowMultiFace = false
  Direction = (1,1,1)
  Length = 2
  Length2 = 100
  Placement = pos=(0,0,0) rot=(1,0,0;1.5708rad)
  Profile = -> Sketch240
  Type = 0
FEATURE [PartDesign::Body] Body130  label="Inner_Side_Plate002"
  Group = -> [Sketch240,Pad162]
  Origin = -> Origin295
  Placement = pos=(0,-11,0) rot=(0,0,1;0rad)
  Tip = -> Pad162
FEATURE [Sketcher::SketchObject] Sketch241
  FullyConstrained = false
  MapMode = 5
  Support = -> [XY_Plane296]
  sketch-geometry (8):
    g0: LineSegment StartX=2.75 StartY=1.58771 StartZ=0 EndX=-4e-16 EndY=3.17543 EndZ=0
    g1: LineSegment StartX=-4e-16 StartY=3.17543 StartZ=0 EndX=-2.75 EndY=1.58771 EndZ=0
    g2: LineSegment StartX=-2.75 StartY=1.58771 StartZ=0 EndX=-2.75 EndY=-1.58771 EndZ=0
    g3: LineSegment StartX=-2.75 StartY=-1.58771 StartZ=0 EndX=4e-16 EndY=-3.17543 EndZ=0
    g4: LineSegment StartX=4e-16 StartY=-3.17543 StartZ=0 EndX=2.75 EndY=-1.58771 EndZ=0
    g5: LineSegment StartX=2.75 StartY=-1.58771 StartZ=0 EndX=2.75 EndY=1.58771 EndZ=0
    g6: Circle CenterX=0 CenterY=0 CenterZ=0 NormalX=0 NormalY=0 NormalZ=1 AngleXU=0 Radius=3.17543
    g7: Circle CenterX=0 CenterY=0 CenterZ=0 NormalX=0 NormalY=0 NormalZ=1 AngleXU=0 Radius=1.75
  constraints (18):
    c: Coincident(g0,g1)
    c: Coincident(g1,g2)
    c: Coincident(g2,g3)
    c: Coincident(g3,g4)
    c: Coincident(g4,g5)
    c: Coincident(g5,g0)
    c: Equal(g0, g1-g5) x5
    c: PointOnObject(g0,g6)
    c: PointOnObject(g1,g6)
    c: PointOnObject(g2,g6)
    c: PointOnObject(g3,g6)
    c: PointOnObject(g4,g6)
    c: PointOnObject(g5,g6)
    c: Coincident(g6,g-1)
    c: Vertical(g5)
    c: Distance(g1,g0) = 5.5
    c: Coincident(g7,g-1)
    c: Diameter(g7) = 3.5
FEATURE [PartDesign::Pad] Pad163
  AllowMultiFace = false
  Direction = (1,1,1)
  Length = 16
  Length2 = 100
  Profile = -> Sketch241
  Type = 0
FEATURE [PartDesign::Body] Body131  label="16mm Standoff006"
  Group = -> [Sketch241,Pad163]
  Origin = -> Origin296
  Placement = pos=(-125,-13,84) rot=(1,0,0;1.5708rad)
  Tip = -> Pad163
FEATURE [Sketcher::SketchObject] Sketch242
  FullyConstrained = false
  MapMode = 5
  Support = -> [XY_Plane297]
  sketch-geometry (8):
    g0: LineSegment StartX=2.75 StartY=1.58771 StartZ=0 EndX=-4e-16 EndY=3.17543 EndZ=0
    g1: LineSegment StartX=-4e-16 StartY=3.17543 StartZ=0 EndX=-2.75 EndY=1.58771 EndZ=0
    g2: LineSegment StartX=-2.75 StartY=1.58771 StartZ=0 EndX=-2.75 EndY=-1.58771 EndZ=0
    g3: LineSegment StartX=-2.75 StartY=-1.58771 StartZ=0 EndX=4e-16 EndY=-3.17543 EndZ=0
    g4: LineSegment StartX=4e-16 StartY=-3.17543 StartZ=0 EndX=2.75 EndY=-1.58771 EndZ=0
    g5: LineSegment StartX=2.75 StartY=-1.58771 StartZ=0 EndX=2.75 EndY=1.58771 EndZ=0
    g6: Circle CenterX=0 CenterY=0 CenterZ=0 NormalX=0 NormalY=0 NormalZ=1 AngleXU=0 Radius=3.17543
    g7: Circle CenterX=0 CenterY=0 CenterZ=0 NormalX=0 NormalY=0 NormalZ=1 AngleXU=0 Radius=1.75
  constraints (18):
    c: Coincident(g0,g1)
    c: Coincident(g1,g2)
    c: Coincident(g2,g3)
    c: Coincident(g3,g4)
    c: Coincident(g4,g5)
    c: Coincident(g5,g0)
    c: Equal(g0, g1-g5) x5
    c: PointOnObject(g0,g6)
    c: PointOnObject(g1,g6)
    c: PointOnObject(g2,g6)
    c: PointOnObject(g3,g6)
    c: PointOnObject(g4,g6)
    c: PointOnObject(g5,g6)
    c: Coincident(g6,g-1)
    c: Vertical(g5)
    c: Distance(g1,g0) = 5.5
    c: Coincident(g7,g-1)
    c: Diameter(g7) = 3.5
FEATURE [PartDesign::Pad] Pad164
  AllowMultiFace = false
  Direction = (1,1,1)
  Length = 16
  Length2 = 100
  Profile = -> Sketch242
  Type = 0
FEATURE [PartDesign::Body] Body132  label="16mm Standoff007"
  Group = -> [Sketch242,Pad164]
  Origin = -> Origin297
  Placement = pos=(-125,-13,126) rot=(1,0,0;1.5708rad)
  Tip = -> Pad164
FEATURE [Sketcher::SketchObject] Sketch243
  FullyConstrained = false
  MapMode = 5
  Support = -> [XY_Plane298]
  sketch-geometry (8):
    g0: LineSegment StartX=2.75 StartY=1.58771 StartZ=0 EndX=-4e-16 EndY=3.17543 EndZ=0
    g1: LineSegment StartX=-4e-16 StartY=3.17543 StartZ=0 EndX=-2.75 EndY=1.58771 EndZ=0
    g2: LineSegment StartX=-2.75 StartY=1.58771 StartZ=0 EndX=-2.75 EndY=-1.58771 EndZ=0
    g3: LineSegment StartX=-2.75 StartY=-1.58771 StartZ=0 EndX=4e-16 EndY=-3.17543 EndZ=0
    g4: LineSegment StartX=4e-16 StartY=-3.17543 StartZ=0 EndX=2.75 EndY=-1.58771 EndZ=0
    g5: LineSegment StartX=2.75 StartY=-1.58771 StartZ=0 EndX=2.75 EndY=1.58771 EndZ=0
    g6: Circle CenterX=0 CenterY=0 CenterZ=0 NormalX=0 NormalY=0 NormalZ=1 AngleXU=0 Radius=3.17543
    g7: Circle CenterX=0 CenterY=0 CenterZ=0 NormalX=0 NormalY=0 NormalZ=1 AngleXU=0 Radius=1.75
  constraints (18):
    c: Coincident(g0,g1)
    c: Coincident(g1,g2)
    c: Coincident(g2,g3)
    c: Coincident(g3,g4)
    c: Coincident(g4,g5)
    c: Coincident(g5,g0)
    c: Equal(g0, g1-g5) x5
    c: PointOnObject(g0,g6)
    c: PointOnObject(g1,g6)
    c: PointOnObject(g2,g6)
    c: PointOnObject(g3,g6)
    c: PointOnObject(g4,g6)
    c: PointOnObject(g5,g6)
    c: Coincident(g6,g-1)
    c: Vertical(g5)
    c: Distance(g1,g0) = 5.5
    c: Coincident(g7,g-1)
    c: Diameter(g7) = 3.5
FEATURE [PartDesign::Pad] Pad165
  AllowMultiFace = false
  Direction = (1,1,1)
  Length = 16
  Length2 = 100
  Profile = -> Sketch243
  Type = 0
FEATURE [PartDesign::Body] Body133  label="16mm Standoff008"
  Group = -> [Sketch243,Pad165]
  Origin = -> Origin298
  Placement = pos=(-67,-13,126) rot=(1,0,0;1.5708rad)
  Tip = -> Pad165
FEATURE [PartDesign::Body] Body134  label="Servo_Mount_End006"
  BaseFeature = -> Body127
  Group = -> [Clone017]
  Origin = -> Origin300
  Placement = pos=(0,0,0) rot=(0,0,1;3.14159rad)
  Tip = -> Clone017
FEATURE [PartDesign::Body] Body135  label="MG996_004"
  BaseFeature = -> Body124
  Group = -> [Clone016]
  Origin = -> Origin301
  Placement = pos=(0,0,0) rot=(0,0,1;3.14159rad)
  Tip = -> Clone016
FEATURE [PartDesign::Body] Body136  label="End_Bearing_Block006"
  BaseFeature = -> Body126
  Group = -> [Clone015]
  Origin = -> Origin302
  Placement = pos=(0,0,0) rot=(0,0,1;3.14159rad)
  Tip = -> Clone015
FEATURE [PartDesign::Body] Body137  label="Servo Gear006"
  BaseFeature = -> Body123
  Group = -> [Clone014]
  Origin = -> Origin303
  Placement = pos=(96,0,0) rot=(0,0,1;0rad)
  Tip = -> Clone014
FEATURE [PartDesign::Body] Body138  label="Servo Horn006"
  BaseFeature = -> Body122
  Group = -> [Clone013]
  Origin = -> Origin304
  Placement = pos=(96,0,0) rot=(0,0,1;0rad)
  Tip = -> Clone013
FEATURE [Part::Feature] Pcb_d4f008
  Placement = pos=(-90,100,0) rot=(0,0,1;0rad)
  shape: bbox 66 x 50 x 1.6 mm, 84 faces (baked)
FEATURE [Sketcher::SketchObject] Sketch244
  FullyConstrained = false
  MapMode = 5
  Placement = pos=(0,0,0) rot=(1,0,0;1.5708rad)
  Support = -> [XZ_Plane305]
  sketch-geometry (1):
    g0: Circle CenterX=10 CenterY=-1.6 CenterZ=0 NormalX=0 NormalY=0 NormalZ=1 AngleXU=0 Radius=4.1
  constraints (3):
    c: DistanceX(g-1,g0) = 10
    c: DistanceY(g0,g-1) = 1.6
    c: Diameter(g0) = 8.2
FEATURE [Part::Feature] Shape215  label="D5_LED_0603_1608Metric_5F71778F005"
  Placement = pos=(30.75,12.25,0) rot=(0,0,1;1.5708rad)
  shape: bbox 0.8 x 1.6 x 1.1 mm, 50 faces (baked)
FEATURE [Part::Feature] Shape216  label="J7_SHF-105-01-L-D-SM-K-TR_5F717900"
  Placement = pos=(48,17.25,0) rot=(0.57735,0.57735,0.57735;2.0944rad)
  shape: bbox 6.502 x 12.7 x 5.588 mm, 207 faces, 4 solids (baked)
FEATURE [Part::Feature] Shape217  label="J8_PinSocket_1x15_P254mm_Vertical_5F7178B018"
  Placement = pos=(12,47,-1.6) rot=(0,1,0;3.14159rad)
  shape: bbox 2.54 x 38.1 x 10.1 mm, 475 faces (baked)
FEATURE [Part::Feature] Shape218  label="R5_R_0603_1608Metric_5F7179A012"
  Placement = pos=(30.75,15.75,0) rot=(0,0,1;1.5708rad)
  shape: bbox 0.8 x 1.6 x 0.45 mm, 26 faces (baked)
FEATURE [Part::Feature] Shape219  label="R6_R_0603_1608Metric_5F7179B013"
  Placement = pos=(33.25,15.75,0) rot=(0,0,1;1.5708rad)
  shape: bbox 0.8 x 1.6 x 0.45 mm, 26 faces (baked)
FEATURE [Sketcher::SketchObject] Sketch245
  FullyConstrained = false
  MapMode = 5
  Support = -> [XY_Plane305]
  sketch-geometry (8):
    g0: LineSegment StartX=2.75 StartY=1.58771 StartZ=0 EndX=-4e-16 EndY=3.17543 EndZ=0
    g1: LineSegment StartX=-4e-16 StartY=3.17543 StartZ=0 EndX=-2.75 EndY=1.58771 EndZ=0
    g2: LineSegment StartX=-2.75 StartY=1.58771 StartZ=0 EndX=-2.75 EndY=-1.58771 EndZ=0
    g3: LineSegment StartX=-2.75 StartY=-1.58771 StartZ=0 EndX=4e-16 EndY=-3.17543 EndZ=0
    g4: LineSegment StartX=4e-16 StartY=-3.17543 StartZ=0 EndX=2.75 EndY=-1.58771 EndZ=0
    g5: LineSegment StartX=2.75 StartY=-1.58771 StartZ=0 EndX=2.75 EndY=1.58771 EndZ=0
    g6: Circle CenterX=0 CenterY=0 CenterZ=0 NormalX=0 NormalY=0 NormalZ=1 AngleXU=0 Radius=3.17543
    g7: Circle CenterX=0 CenterY=0 CenterZ=0 NormalX=0 NormalY=0 NormalZ=1 AngleXU=0 Radius=1.75
  constraints (18):
    c: Coincident(g0,g1)
    c: Coincident(g1,g2)
    c: Coincident(g2,g3)
    c: Coincident(g3,g4)
    c: Coincident(g4,g5)
    c: Coincident(g5,g0)
    c: Equal(g0, g1-g5) x5
    c: PointOnObject(g0,g6)
    c: PointOnObject(g1,g6)
    c: PointOnObject(g2,g6)
    c: PointOnObject(g3,g6)
    c: PointOnObject(g4,g6)
    c: PointOnObject(g5,g6)
    c: Coincident(g6,g-1)
    c: Vertical(g5)
    c: Distance(g1,g0) = 5.5
    c: Coincident(g7,g-1)
    c: Diameter(g7) = 3.5
FEATURE [Sketcher::SketchObject] Sketch246
  FullyConstrained = false
  MapMode = 5
  Support = -> [XY_Plane306]
  sketch-geometry (8):
    g0: LineSegment StartX=2.75 StartY=1.58771 StartZ=0 EndX=-4e-16 EndY=3.17543 EndZ=0
    g1: LineSegment StartX=-4e-16 StartY=3.17543 StartZ=0 EndX=-2.75 EndY=1.58771 EndZ=0
    g2: LineSegment StartX=-2.75 StartY=1.58771 StartZ=0 EndX=-2.75 EndY=-1.58771 EndZ=0
    g3: LineSegment StartX=-2.75 StartY=-1.58771 StartZ=0 EndX=4e-16 EndY=-3.17543 EndZ=0
    g4: LineSegment StartX=4e-16 StartY=-3.17543 StartZ=0 EndX=2.75 EndY=-1.58771 EndZ=0
    g5: LineSegment StartX=2.75 StartY=-1.58771 StartZ=0 EndX=2.75 EndY=1.58771 EndZ=0
    g6: Circle CenterX=0 CenterY=0 CenterZ=0 NormalX=0 NormalY=0 NormalZ=1 AngleXU=0 Radius=3.17543
    g7: Circle CenterX=0 CenterY=0 CenterZ=0 NormalX=0 NormalY=0 NormalZ=1 AngleXU=0 Radius=1.75
  constraints (18):
    c: Coincident(g0,g1)
    c: Coincident(g1,g2)
    c: Coincident(g2,g3)
    c: Coincident(g3,g4)
    c: Coincident(g4,g5)
    c: Coincident(g5,g0)
    c: Equal(g0, g1-g5) x5
    c: PointOnObject(g0,g6)
    c: PointOnObject(g1,g6)
    c: PointOnObject(g2,g6)
    c: PointOnObject(g3,g6)
    c: PointOnObject(g4,g6)
    c: PointOnObject(g5,g6)
    c: Coincident(g6,g-1)
    c: Vertical(g5)
    c: Distance(g1,g0) = 5.5
    c: Coincident(g7,g-1)
    c: Diameter(g7) = 3.5
FEATURE [PartDesign::Pad] Pad169
  AllowMultiFace = false
  Direction = (1,1,1)
  Length = 16
  Length2 = 100
  Profile = -> Sketch246
  Type = 0
FEATURE [Sketcher::SketchObject] Sketch247
  FullyConstrained = false
  MapMode = 5
  Placement = pos=(0,0,0) rot=(1,0,0;1.5708rad)
  Support = -> [XZ_Plane308]
  sketch-geometry (1):
    g0: Circle CenterX=10 CenterY=-1.6 CenterZ=0 NormalX=0 NormalY=0 NormalZ=1 AngleXU=0 Radius=4.1
  constraints (3):
    c: DistanceX(g-1,g0) = 10
    c: DistanceY(g0,g-1) = 1.6
    c: Diameter(g0) = 8.2
FEATURE [PartDesign::Pad] Pad166
  AllowMultiFace = false
  Direction = (1,1,1)
  Length = 12
  Length2 = 100
  Placement = pos=(0,0,0) rot=(1,0,0;1.5708rad)
  Profile = -> Sketch247
  Type = 0
FEATURE [PartDesign::Body] Body139  label="AltCap002"
  Group = -> [Sketch247,Pad166]
  Origin = -> Origin306
  Tip = -> Pad166
FEATURE [Part::Feature] Shape220  label="C9_C_0603_1608Metric_5F754EF014"
  Placement = pos=(26,17.5,0) rot=(0,0,1;3.14159rad)
  shape: bbox 1.6 x 0.8 x 0.8 mm, 28 faces (baked)
FEATURE [Sketcher::SketchObject] Sketch248
  FullyConstrained = false
  MapMode = 5
  Support = -> [XY_Plane312]
  sketch-geometry (8):
    g0: LineSegment StartX=2.75 StartY=1.58771 StartZ=0 EndX=-4e-16 EndY=3.17543 EndZ=0
    g1: LineSegment StartX=-4e-16 StartY=3.17543 StartZ=0 EndX=-2.75 EndY=1.58771 EndZ=0
    g2: LineSegment StartX=-2.75 StartY=1.58771 StartZ=0 EndX=-2.75 EndY=-1.58771 EndZ=0
    g3: LineSegment StartX=-2.75 StartY=-1.58771 StartZ=0 EndX=4e-16 EndY=-3.17543 EndZ=0
    g4: LineSegment StartX=4e-16 StartY=-3.17543 StartZ=0 EndX=2.75 EndY=-1.58771 EndZ=0
    g5: LineSegment StartX=2.75 StartY=-1.58771 StartZ=0 EndX=2.75 EndY=1.58771 EndZ=0
    g6: Circle CenterX=0 CenterY=0 CenterZ=0 NormalX=0 NormalY=0 NormalZ=1 AngleXU=0 Radius=3.17543
    g7: Circle CenterX=0 CenterY=0 CenterZ=0 NormalX=0 NormalY=0 NormalZ=1 AngleXU=0 Radius=1.75
  constraints (18):
    c: Coincident(g0,g1)
    c: Coincident(g1,g2)
    c: Coincident(g2,g3)
    c: Coincident(g3,g4)
    c: Coincident(g4,g5)
    c: Coincident(g5,g0)
    c: Equal(g0, g1-g5) x5
    c: PointOnObject(g0,g6)
    c: PointOnObject(g1,g6)
    c: PointOnObject(g2,g6)
    c: PointOnObject(g3,g6)
    c: PointOnObject(g4,g6)
    c: PointOnObject(g5,g6)
    c: Coincident(g6,g-1)
    c: Vertical(g5)
    c: Distance(g1,g0) = 5.5
    c: Coincident(g7,g-1)
    c: Diameter(g7) = 3.5
FEATURE [PartDesign::Pad] Pad167
  AllowMultiFace = false
  Direction = (1,1,1)
  Length = 16
  Length2 = 100
  Profile = -> Sketch248
  Type = 0
FEATURE [Sketcher::SketchObject] PCB_Sketch_d4f008
  FullyConstrained = false
  sketch-geometry (8):
    g0: LineSegment StartX=4e-16 StartY=3 StartZ=0 EndX=-3.6e-15 EndY=47 EndZ=0
    g1: LineSegment StartX=63 StartY=8.4e-15 StartZ=0 EndX=3 EndY=4e-16 EndZ=0
    g2: LineSegment StartX=66 StartY=47 StartZ=0 EndX=66 EndY=3 EndZ=0
    g3: LineSegment StartX=3 StartY=50 StartZ=0 EndX=63 EndY=50 EndZ=0
    g4: ArcOfCircle CenterX=63 CenterY=47 CenterZ=0 NormalX=0 NormalY=0 NormalZ=1 AngleXU=0 Radius=3 StartAngle=0 EndAngle=1.5708
    g5: ArcOfCircle CenterX=63 CenterY=3 CenterZ=0 NormalX=0 NormalY=0 NormalZ=1 AngleXU=0 Radius=3 StartAngle=4.71239 EndAngle=6.28319
    g6: ArcOfCircle CenterX=3 CenterY=3 CenterZ=0 NormalX=0 NormalY=0 NormalZ=1 AngleXU=0 Radius=3 StartAngle=3.14159 EndAngle=4.71239
    g7: ArcOfCircle CenterX=3 CenterY=47 CenterZ=0 NormalX=0 NormalY=0 NormalZ=1 AngleXU=0 Radius=3 StartAngle=1.5708 EndAngle=3.14159
  constraints (8):
    c: Coincident(g0,g6)
    c: Coincident(g0,g7)
    c: Coincident(g1,g6)
    c: Coincident(g3,g7)
    c: Coincident(g1,g5)
    c: Coincident(g3,g4)
    c: Coincident(g2,g5)
    c: Coincident(g2,g4)
FEATURE [Sketcher::SketchObject] Sketch249
  FullyConstrained = false
  MapMode = 5
  Support = -> [XY_Plane311]
  sketch-geometry (1):
    g0: Circle CenterX=0 CenterY=0 CenterZ=0 NormalX=0 NormalY=0 NormalZ=1 AngleXU=0 Radius=4.15
  constraints (2):
    c: Coincident(g0,g-1)
    c: Diameter(g0) = 8.3
FEATURE [PartDesign::Pad] Pad168
  AllowMultiFace = false
  Direction = (1,1,1)
  Length = 10.5
  Length2 = 100
  Profile = -> Sketch249
  Type = 0
FEATURE [Part::Feature] Shape221  label="U5_SOT_23_5_5F717A8C005"
  Placement = pos=(4.5,23,0) rot=(0,0,1;1.5708rad)
  shape: bbox 2.9 x 2.8 x 1.55 mm, 109 faces (baked)
FEATURE [Part::Feature] Shape222  label="U4_SOIC_8_39x49mm_P127mm_5F717A082"
  Placement = pos=(40.25,11.5,0) rot=(0,0,1;0rad)
  shape: bbox 6 x 4.9 x 1.75 mm, 156 faces (baked)
FEATURE [Part::Feature] Shape223  label="J3_PinHeader_1x15_P254mm_Vertical_5F717823"
  Placement = pos=(54,47,-1.6) rot=(0,1,0;3.14159rad)
  shape: bbox 2.54 x 38.1 x 11.54 mm, 364 faces (baked)
FEATURE [Part::Feature] Shape224  label="R4_R_0603_1608Metric_5F718001"
  Placement = pos=(15.175,35.57,0) rot=(0,0,1;3.14159rad)
  shape: bbox 1.6 x 0.8 x 0.45 mm, 26 faces (baked)
FEATURE [Part::Feature] Shape225  label="U2_SOT_353_SC_70_5_5F717A017"
  Placement = pos=(26,15.25,0) rot=(0,0,1;3.14159rad)
  shape: bbox 2 x 2 x 1.05 mm, 104 faces (baked)
FEATURE [PartDesign::Body] Body141  label="16mm Standoff010"
  Group = -> [Sketch248,Pad167]
  Origin = -> Origin315
  Placement = pos=(125,-13,84) rot=(1,0,0;1.5708rad)
  Tip = -> Pad167
FEATURE [PartDesign::CoordinateSystem] Local_CS_d4f008
  AttacherType = Attacher::AttachEngine3D
FEATURE [Part::Feature] Shape226  label="D6_LED_0603_1608Metric_5F71855F005"
  Placement = pos=(33.25,12.25,0) rot=(0,0,1;1.5708rad)
  shape: bbox 0.8 x 1.6 x 1.1 mm, 50 faces (baked)
FEATURE [Part::Feature] Shape227  label="J11_PinHeader_1x03_P254mm_Vertical_5F717919"
  Placement = pos=(1.84,13.98,0) rot=(0,0,1;1.5708rad)
  shape: bbox 7.62 x 2.54 x 11.54 mm, 76 faces (baked)
FEATURE [Part::Feature] Shape228  label="J9_MSTBA_01x04_G_5_08mm_5F7178E011"
  Placement = pos=(20.5,3.5,0) rot=(0,0,1;0rad)
  shape: bbox 22.32 x 12 x 12.6 mm, 113 faces (baked)
FEATURE [Part::Feature] Shape229  label="R3_R_0603_1608Metric_5F717990"
  Placement = pos=(15.175,38.11,0) rot=(0,0,1;3.14159rad)
  shape: bbox 1.6 x 0.8 x 0.45 mm, 26 faces (baked)
FEATURE [Part::Feature] Shape230  label="J4_Molex_AE_6410_06A_5F717852"
  Placement = pos=(61.62,35.57,0) rot=(0,0,-1;1.5708rad)
  shape: bbox 5.8 x 15.24 x 15.26 mm, 169 faces (baked)
FEATURE [Part::Feature] Shape231  label="J5_PinHeader_1x03_P254mm_Vertical_5F723002"
  Placement = pos=(1.84,35.57,0) rot=(0,0,1;1.5708rad)
  shape: bbox 7.62 x 2.54 x 11.54 mm, 76 faces (baked)
FEATURE [Part::Feature] Shape232  label="U1_SOT_353_SC_70_5_5F7179FD005"
  Placement = pos=(26,19.75,0) rot=(0,0,1;3.14159rad)
  shape: bbox 2 x 2 x 1.05 mm, 104 faces (baked)
FEATURE [Part::Feature] Shape233  label="J3_PinHeader_1x15_P254mm_Vertical_5F717824"
  Placement = pos=(2.75,38.5,-5.2e-15) rot=(0,0,1;0rad)
  shape: bbox 2.54 x 38.1 x 11.54 mm, 364 faces (baked)
FEATURE [Part::Feature] Shape234  label="U3_LQFP_32_7x7mm_P08mm_5F71845B005"
  Placement = pos=(36.5,25.5,0) rot=(0,0,-1;1.5708rad)
  shape: bbox 9 x 9 x 1.5 mm, 516 faces (baked)
FEATURE [Sketcher::SketchObject] Sketch250
  FullyConstrained = false
  MapMode = 5
  Support = -> [XY_Plane318]
  sketch-geometry (66):
    g0: LineSegment StartX=0 StartY=41.4 StartZ=0 EndX=47.35 EndY=41.4 EndZ=0
    g1: LineSegment StartX=47.35 StartY=41.4 StartZ=0 EndX=47.35 EndY=0 EndZ=0
    g2: LineSegment StartX=47.35 StartY=0 StartZ=0 EndX=0 EndY=0 EndZ=0
    g3: LineSegment StartX=0 StartY=0 StartZ=0 EndX=0 EndY=41.4 EndZ=0
    g4: LineSegment StartX=2.72 StartY=2.92 StartZ=0 EndX=2.72 EndY=5.46 EndZ=0
    g5: LineSegment StartX=2.72 StartY=5.46 StartZ=0 EndX=2.72 EndY=8 EndZ=0
    g6: LineSegment StartX=2.72 StartY=8 StartZ=0 EndX=2.72 EndY=10.54 EndZ=0
    g7: LineSegment StartX=2.72 StartY=10.54 StartZ=0 EndX=2.72 EndY=13.08 EndZ=0
    g8: LineSegment StartX=2.72 StartY=13.08 StartZ=0 EndX=2.72 EndY=15.62 EndZ=0
    g9: LineSegment StartX=2.72 StartY=15.62 StartZ=0 EndX=2.72 EndY=18.16 EndZ=0
    g10: LineSegment StartX=2.72 StartY=18.16 StartZ=0 EndX=2.72 EndY=20.7 EndZ=0
    g11: LineSegment StartX=2.72 StartY=20.7 StartZ=0 EndX=2.72 EndY=23.24 EndZ=0
    g12: LineSegment StartX=2.72 StartY=23.24 StartZ=0 EndX=2.72 EndY=25.78 EndZ=0
    g13: LineSegment StartX=2.72 StartY=25.78 StartZ=0 EndX=2.72 EndY=28.32 EndZ=0
    g14: LineSegment StartX=2.72 StartY=28.32 StartZ=0 EndX=2.72 EndY=30.86 EndZ=0
    g15: LineSegment StartX=2.72 StartY=30.86 StartZ=0 EndX=2.72 EndY=33.4 EndZ=0
    g16: LineSegment StartX=2.72 StartY=33.4 StartZ=0 EndX=2.72 EndY=35.94 EndZ=0
    g17: LineSegment StartX=2.72 StartY=35.94 StartZ=0 EndX=2.72 EndY=38.48 EndZ=0
    g18: LineSegment StartX=44.63 StartY=2.92 StartZ=0 EndX=44.63 EndY=5.46 EndZ=0
    g19: LineSegment StartX=44.63 StartY=5.46 StartZ=0 EndX=44.63 EndY=8 EndZ=0
    g20: LineSegment StartX=44.63 StartY=8 StartZ=0 EndX=44.63 EndY=10.54 EndZ=0
    g21: LineSegment StartX=44.63 StartY=10.54 StartZ=0 EndX=44.63 EndY=13.08 EndZ=0
    g22: LineSegment StartX=44.63 StartY=13.08 StartZ=0 EndX=44.63 EndY=15.62 EndZ=0
    g23: LineSegment StartX=44.63 StartY=15.62 StartZ=0 EndX=44.63 EndY=18.16 EndZ=0
    g24: LineSegment StartX=44.63 StartY=18.16 StartZ=0 EndX=44.63 EndY=20.7 EndZ=0
    g25: LineSegment StartX=44.63 StartY=20.7 StartZ=0 EndX=44.63 EndY=23.24 EndZ=0
    g26: LineSegment StartX=44.63 StartY=23.24 StartZ=0 EndX=44.63 EndY=25.78 EndZ=0
    g27: LineSegment StartX=44.63 StartY=25.78 StartZ=0 EndX=44.63 EndY=28.32 EndZ=0
    g28: LineSegment StartX=44.63 StartY=28.32 StartZ=0 EndX=44.63 EndY=30.86 EndZ=0
    g29: LineSegment StartX=44.63 StartY=30.86 StartZ=0 EndX=44.63 EndY=33.4 EndZ=0
    g30: LineSegment StartX=44.63 StartY=33.4 StartZ=0 EndX=44.63 EndY=35.94 EndZ=0
    g31: LineSegment StartX=44.63 StartY=35.94 StartZ=0 EndX=44.63 EndY=38.48 EndZ=0
    g32: LineSegment StartX=0 StartY=0 StartZ=0 EndX=2.72 EndY=2.92 EndZ=0
    g33: LineSegment StartX=44.63 StartY=2.92 StartZ=0 EndX=47.35 EndY=0 EndZ=0
    g34: LineSegment StartX=44.63 StartY=38.48 StartZ=0 EndX=47.35 EndY=41.4 EndZ=0
    g35: LineSegment StartX=2.72 StartY=38.48 StartZ=0 EndX=0 EndY=41.4 EndZ=0
    g36: Circle CenterX=2.72 CenterY=38.48 CenterZ=0 NormalX=0 NormalY=0 NormalZ=1 AngleXU=0 Radius=0.5
    g37: Circle CenterX=2.72 CenterY=35.94 CenterZ=0 NormalX=0 NormalY=0 NormalZ=1 AngleXU=0 Radius=0.5
    g38: Circle CenterX=2.72 CenterY=33.4 CenterZ=0 NormalX=0 NormalY=0 NormalZ=1 AngleXU=0 Radius=0.5
    g39: Circle CenterX=2.72 CenterY=30.86 CenterZ=0 NormalX=0 NormalY=0 NormalZ=1 AngleXU=0 Radius=0.5
    g40: Circle CenterX=2.72 CenterY=28.32 CenterZ=0 NormalX=0 NormalY=0 NormalZ=1 AngleXU=0 Radius=0.5
    g41: Circle CenterX=2.72 CenterY=25.78 CenterZ=0 NormalX=0 NormalY=0 NormalZ=1 AngleXU=0 Radius=0.5
    g42: Circle CenterX=2.72 CenterY=23.24 CenterZ=0 NormalX=0 NormalY=0 NormalZ=1 AngleXU=0 Radius=0.5
    g43: Circle CenterX=2.72 CenterY=20.7 CenterZ=0 NormalX=0 NormalY=0 NormalZ=1 AngleXU=0 Radius=0.5
    g44: Circle CenterX=2.72 CenterY=18.16 CenterZ=0 NormalX=0 NormalY=0 NormalZ=1 AngleXU=0 Radius=0.5
    g45: Circle CenterX=2.72 CenterY=15.62 CenterZ=0 NormalX=0 NormalY=0 NormalZ=1 AngleXU=0 Radius=0.5
    g46: Circle CenterX=2.72 CenterY=13.08 CenterZ=0 NormalX=0 NormalY=0 NormalZ=1 AngleXU=0 Radius=0.5
    g47: Circle CenterX=2.72 CenterY=10.54 CenterZ=0 NormalX=0 NormalY=0 NormalZ=1 AngleXU=0 Radius=0.5
    g48: Circle CenterX=2.72 CenterY=8 CenterZ=0 NormalX=0 NormalY=0 NormalZ=1 AngleXU=0 Radius=0.5
    g49: Circle CenterX=2.72 CenterY=5.46 CenterZ=0 NormalX=0 NormalY=0 NormalZ=1 AngleXU=0 Radius=0.5
    g50: Circle CenterX=2.72 CenterY=2.92 CenterZ=0 NormalX=0 NormalY=0 NormalZ=1 AngleXU=0 Radius=0.5
    g51: Circle CenterX=44.63 CenterY=38.48 CenterZ=0 NormalX=0 NormalY=0 NormalZ=1 AngleXU=0 Radius=0.5
    g52: Circle CenterX=44.63 CenterY=35.94 CenterZ=0 NormalX=0 NormalY=0 NormalZ=1 AngleXU=0 Radius=0.5
    g53: Circle CenterX=44.63 CenterY=33.4 CenterZ=0 NormalX=0 NormalY=0 NormalZ=1 AngleXU=0 Radius=0.5
    g54: Circle CenterX=44.63 CenterY=30.86 CenterZ=0 NormalX=0 NormalY=0 NormalZ=1 AngleXU=0 Radius=0.5
    g55: Circle CenterX=44.63 CenterY=28.32 CenterZ=0 NormalX=0 NormalY=0 NormalZ=1 AngleXU=0 Radius=0.5
    g56: Circle CenterX=44.63 CenterY=25.78 CenterZ=0 NormalX=0 NormalY=0 NormalZ=1 AngleXU=0 Radius=0.5
    g57: Circle CenterX=44.63 CenterY=23.24 CenterZ=0 NormalX=0 NormalY=0 NormalZ=1 AngleXU=0 Radius=0.5
    g58: Circle CenterX=44.63 CenterY=20.7 CenterZ=0 NormalX=0 NormalY=0 NormalZ=1 AngleXU=0 Radius=0.5
    g59: Circle CenterX=44.63 CenterY=18.16 CenterZ=0 NormalX=0 NormalY=0 NormalZ=1 AngleXU=0 Radius=0.5
    g60: Circle CenterX=44.63 CenterY=15.62 CenterZ=0 NormalX=0 NormalY=0 NormalZ=1 AngleXU=0 Radius=0.5
    g61: Circle CenterX=44.63 CenterY=13.08 CenterZ=0 NormalX=0 NormalY=0 NormalZ=1 AngleXU=0 Radius=0.5
    g62: Circle CenterX=44.63 CenterY=10.54 CenterZ=0 NormalX=0 NormalY=0 NormalZ=1 AngleXU=0 Radius=0.5
    g63: Circle CenterX=44.63 CenterY=8 CenterZ=0 NormalX=0 NormalY=0 NormalZ=1 AngleXU=0 Radius=0.5
    g64: Circle CenterX=44.63 CenterY=5.46 CenterZ=0 NormalX=0 NormalY=0 NormalZ=1 AngleXU=0 Radius=0.5
    g65: Circle CenterX=44.63 CenterY=2.92 CenterZ=0 NormalX=0 NormalY=0 NormalZ=1 AngleXU=0 Radius=0.5
  constraints (152):
    c: Coincident(g0,g1)
    c: Coincident(g1,g2)
    c: Coincident(g2,g3)
    c: Coincident(g3,g0)
    c: Horizontal(g0)
    c: Horizontal(g2)
    c: Vertical(g1)
    c: Vertical(g3)
    c: DistanceX(g0,g0) = 47.35
    c: DistanceY(g1,g1) = 41.4
    c: Coincident(g2,g-1)
    c: Coincident(g4,g5)
    c: Coincident(g5,g6)
    c: Coincident(g6,g7)
    c: Coincident(g7,g8)
    c: Coincident(g8,g9)
    c: Coincident(g9,g10)
    c: Coincident(g10,g11)
    c: Coincident(g11,g12)
    c: Coincident(g12,g13)
    c: Coincident(g13,g14)
    c: Coincident(g14,g15)
    c: Coincident(g15,g16)
    c: Coincident(g16,g17)
    c: Coincident(g18,g19)
    c: Coincident(g19,g20)
    c: Coincident(g20,g21)
    c: Coincident(g21,g22)
    c: Coincident(g22,g23)
    c: Coincident(g23,g24)
    c: Coincident(g24,g25)
    c: Coincident(g25,g26)
    c: Coincident(g26,g27)
    c: Coincident(g27,g28)
    c: Coincident(g28,g29)
    c: Coincident(g29,g30)
    c: Coincident(g30,g31)
    c: Vertical(g17)
    c: Vertical(g16)
    c: Vertical(g15)
    c: Vertical(g14)
    c: Vertical(g13)
    c: Vertical(g12)
    c: Vertical(g11)
    c: Vertical(g10)
    c: Vertical(g9)
    c: Vertical(g8)
    c: Vertical(g7)
    c: Vertical(g6)
    c: Vertical(g5)
    c: Vertical(g4)
    c: Equal(g17,g16)
    c: Equal(g16,g15)
    c: Equal(g15,g14)
    c: Equal(g14,g13)
    c: Equal(g13,g12)
    c: Equal(g12,g11)
    c: Equal(g11,g10)
    c: Equal(g10,g9)
    c: Equal(g9,g8)
    c: Equal(g8,g7)
    c: Equal(g7,g6)
    c: Equal(g6,g5)
    c: Equal(g5,g4)
    c: DistanceY(g4,g4) = 2.54
    c: Vertical(g18)
    c: Vertical(g19)
    c: Vertical(g20)
    c: Vertical(g21)
    c: Vertical(g22)
    c: Vertical(g23)
    c: Vertical(g24)
    c: Vertical(g25)
    c: Vertical(g26)
    c: Vertical(g27)
    c: Vertical(g28)
    c: Vertical(g29)
    c: Vertical(g30)
    c: Vertical(g31)
    c: Equal(g31,g30)
    c: Equal(g30,g29)
    c: Equal(g29,g28)
    c: Equal(g28,g27)
    c: Equal(g27,g26)
    c: Equal(g26,g25)
    c: Equal(g25,g24)
    c: Equal(g24,g23)
    c: Equal(g23,g22)
    c: Equal(g22,g21)
    c: Equal(g21,g20)
    c: Equal(g20,g19)
    c: Equal(g19,g18)
    c: Equal(g18,g4)
    c: DistanceX(g4,g18) = 41.91
    c: Coincident(g33,g1)
    c: Coincident(g33,g18)
    c: Coincident(g4,g32)
    c: Coincident(g32,g2)
    c: Equal(g32,g33)
    c: Coincident(g35,g17)
    c: Coincident(g35,g0)
    c: Coincident(g34,g31)
    c: Coincident(g34,g0)
    c: Equal(g34,g33)
    c: Equal(g33,g35)
    c: Coincident(g50,g4)
    c: Coincident(g49,g4)
    c: Coincident(g48,g5)
    c: Coincident(g47,g6)
    c: Coincident(g46,g7)
    c: Coincident(g45,g8)
    c: Coincident(g44,g9)
    c: Coincident(g43,g10)
    c: Coincident(g42,g11)
    c: Coincident(g41,g12)
    c: Coincident(g40,g13)
    c: Coincident(g39,g14)
    c: Coincident(g38,g15)
    c: Coincident(g37,g16)
    c: Coincident(g36,g17)
    c: Coincident(g65,g18)
    c: Coincident(g64,g18)
    c: Coincident(g63,g19)
    c: Coincident(g62,g20)
    c: Coincident(g61,g21)
    c: Coincident(g60,g22)
    c: Coincident(g59,g23)
    c: Coincident(g58,g24)
    c: Coincident(g57,g25)
    c: Coincident(g56,g26)
    c: Coincident(g55,g27)
    c: Coincident(g54,g28)
    c: Coincident(g53,g29)
    c: Coincident(g52,g30)
    c: Coincident(g51,g31)
    c: Diameter(g36) = 1
    c: Equal(g36, g37-g50) x14
    c: Equal(g36,g65)
    c: Equal(g36,g64)
    c: Equal(g36,g63)
    c: Equal(g36,g62)
    c: Equal(g36,g61)
    c: Equal(g36,g60)
    c: Equal(g36,g59)
    c: Equal(g36,g58)
    c: Equal(g36,g57)
    c: Equal(g36,g56)
    c: Equal(g36,g55)
    c: Equal(g36,g54)
    c: Equal(g36,g53)
    c: Equal(g36,g52)
    c: Equal(g36,g51)
FEATURE [Part::Feature] Shape235  label="C7_C_0603_1608Metric_5F717733"
  Placement = pos=(4.5,27.5,0) rot=(0,0,1;0rad)
  shape: bbox 1.6 x 0.8 x 0.8 mm, 28 faces (baked)
FEATURE [Part::Feature] Shape236  label="C8_C_0603_1608Metric_5F7555CB005"
  Placement = pos=(26,13,0) rot=(0,0,1;3.14159rad)
  shape: bbox 1.6 x 0.8 x 0.8 mm, 28 faces (baked)
FEATURE [Part::Feature] Shape237  label="R7_R_0603_1608Metric_5F7179C014"
  Placement = pos=(44.25,36.5,0) rot=(0,0,1;1.5708rad)
  shape: bbox 0.8 x 1.6 x 0.45 mm, 26 faces (baked)
FEATURE [Part::Feature] Shape238  label="SW1_SW_PUSH_6mm_5F7179E013"
  Placement = pos=(41.5,37.75,0) rot=(0,0,1;3.14159rad)
  shape: bbox 7.174 x 6 x 7.8 mm, 105 faces (baked)
FEATURE [Part::Feature] Shape239  label="R2_R_0603_1608Metric_5F717979"
  Placement = pos=(15.175,40.65,0) rot=(0,0,1;3.14159rad)
  shape: bbox 1.6 x 0.8 x 0.45 mm, 26 faces (baked)
FEATURE [Part::Feature] Shape240  label="J8_PinSocket_1x15_P254mm_Vertical_5F7178B019"
  Placement = pos=(44.65,38.5,4e-15) rot=(0,0,1;0rad)
  shape: bbox 2.54 x 38.1 x 10.1 mm, 475 faces (baked)
FEATURE [Part::Feature] Shape241  label="D4_SOT_23_5F71777C005"
  Placement = pos=(18.985,35.57,0) rot=(0,0,1;0rad)
  shape: bbox 2.5 x 3 x 1.2 mm, 76 faces (baked)
FEATURE [Part::Feature] Shape242  label="J12_PinHeader_1x06_P254mm_Vertical_5F71792E005"
  Placement = pos=(34.95,46.25,0) rot=(0,0,1;1.5708rad)
  shape: bbox 15.24 x 2.54 x 11.54 mm, 148 faces (baked)
FEATURE [App::Part] Board_Geoms_d4f008  label="Board_Geoms_d4f014"
  Group = -> [Local_CS_d4f008,Pcb_d4f008,PCB_Sketch_d4f008]
  Origin = -> Origin309
FEATURE [Part::Feature] Shape243  label="C3_C_0603_1608Metric_5F7176E009"
  Placement = pos=(32.5,39.75,0) rot=(0,0,1;1.5708rad)
  shape: bbox 0.8 x 1.6 x 0.8 mm, 28 faces (baked)
FEATURE [Part::Feature] Shape244  label="J6_PinHeader_1x03_P254mm_Vertical_5F717880"
  Placement = pos=(1.84,33.03,0) rot=(0,0,1;1.5708rad)
  shape: bbox 7.62 x 2.54 x 11.54 mm, 76 faces (baked)
FEATURE [PartDesign::Pad] Pad170
  AllowMultiFace = false
  Direction = (1,1,1)
  Length = 12
  Length2 = 100
  Placement = pos=(0,0,0) rot=(1,0,0;1.5708rad)
  Profile = -> Sketch244
  Type = 0
FEATURE [PartDesign::Pad] Pad171
  AllowMultiFace = false
  Direction = (1,1,1)
  Length = 1.6
  Length2 = 100
  Profile = -> Sketch250
  Reversed = true
  Type = 0
FEATURE [Part::Feature] Shape245  label="J2_PinHeader_1x03_P254mm_Vertical_5F7177F005"
  Placement = pos=(1.84,38.11,0) rot=(0,0,1;1.5708rad)
  shape: bbox 7.62 x 2.54 x 11.54 mm, 76 faces (baked)
FEATURE [Part::Feature] Shape246  label="J13_MSTBA_01x02_G_5_08mm_5F717957"
  Placement = pos=(44,3.5,0) rot=(0,0,1;0rad)
  shape: bbox 12.16 x 12 x 12.6 mm, 63 faces (baked)
FEATURE [Part::Feature] Shape247  label="C1_C_0805_2012Metric_5F7176C007"
  Placement = pos=(38.25,35,0) rot=(0,0,1;0rad)
  shape: bbox 2 x 1.25 x 1.25 mm, 28 faces (baked)
FEATURE [Part::Feature] Shape248  label="R1_R_0603_1608Metric_5F717968"
  Placement = pos=(15.175,43.19,0) rot=(0,0,1;3.14159rad)
  shape: bbox 1.6 x 0.8 x 0.45 mm, 26 faces (baked)
FEATURE [App::Part] Bot_d4f008  label="Bot_d4f014"
  Group = -> [Shape223,Shape217]
  Origin = -> Origin313
FEATURE [Part::Feature] Shape249  label="J10_PinHeader_1x03_P254mm_Vertical_5F7178FD005"
  Placement = pos=(1.84,16.52,0) rot=(0,0,1;1.5708rad)
  shape: bbox 7.62 x 2.54 x 11.54 mm, 76 faces (baked)
FEATURE [Part::Feature] Shape250  label="C2_C_0603_1608Metric_5F7176D008"
  Placement = pos=(38.25,33,0) rot=(0,0,1;0rad)
  shape: bbox 1.6 x 0.8 x 0.8 mm, 28 faces (baked)
FEATURE [Part::Feature] Shape251  label="D2_SOT_23_5F717757"
  Placement = pos=(18.985,40.65,0) rot=(0,0,1;0rad)
  shape: bbox 2.5 x 3 x 1.2 mm, 76 faces (baked)
FEATURE [Part::Feature] Shape252  label="D3_SOT_23_5F717772"
  Placement = pos=(22.795,38.11,0) rot=(0,0,1;0rad)
  shape: bbox 2.5 x 3 x 1.2 mm, 76 faces (baked)
FEATURE [Part::Feature] Shape253  label="D1_SOT_23_5F71773D005"
  Placement = pos=(22.795,43.19,0) rot=(0,0,1;0rad)
  shape: bbox 2.5 x 3 x 1.2 mm, 76 faces (baked)
FEATURE [Part::Feature] Shape254  label="J1_PinHeader_1x03_P254mm_Vertical_5F7228CA005"
  Placement = pos=(1.84,40.65,0) rot=(0,0,1;1.5708rad)
  shape: bbox 7.62 x 2.54 x 11.54 mm, 76 faces (baked)
FEATURE [PartDesign::Pad] Pad172
  AllowMultiFace = false
  Direction = (1,1,1)
  Length = 16
  Length2 = 100
  Profile = -> Sketch245
  Type = 0
FEATURE [PartDesign::Body] Body140  label="16mm Standoff009"
  Group = -> [Sketch245,Pad172]
  Origin = -> Origin317
  Placement = pos=(67,-13,126) rot=(1,0,0;1.5708rad)
  Tip = -> Pad172
FEATURE [Part::Feature] Shape255  label="C6_C_0603_1608Metric_5F717722"
  Placement = pos=(6.25,25.75,0) rot=(0,0,1;0rad)
  shape: bbox 1.6 x 0.8 x 0.8 mm, 28 faces (baked)
FEATURE [Part::Feature] Shape256  label="C5_C_0603_1608Metric_5F717711"
  Placement = pos=(4.5,20.25,0) rot=(0,0,1;0rad)
  shape: bbox 1.6 x 0.8 x 0.8 mm, 28 faces (baked)
FEATURE [Part::Feature] Shape257  label="C4_C_0603_1608Metric_5F7176F010"
  Placement = pos=(41.5,15.25,0) rot=(0,0,1;0rad)
  shape: bbox 1.6 x 0.8 x 0.8 mm, 28 faces (baked)
FEATURE [App::Part] Top_d4f008  label="Top_d4f013"
  Group = -> [Shape220,Shape236,Shape221,Shape222,Shape234,Shape225,Shape232,Shape238,Shape237,Shape219,Shape218,Shape224,Shape229,Shape239,Shape248,Shape246,Shape242,Shape227,Shape249,Shape228,Shape216,Shape244,Shape231,Shape230,Shape245,Shape254,Shape226,Shape215,Shape241,Shape252,Shape251,Shape253,Shape235,Shape255,Shape256,Shape257,Shape243,Shape250,Shape247]
  Origin = -> Origin316
FEATURE [App::Part] Step_Models_d4f008  label="Step_Models_d4f013"
  Group = -> [Top_d4f008,Bot_d4f008]
  Origin = -> Origin318
FEATURE [App::Part] Board_d4f008  label="motor_board005"
  Group = -> [Board_Geoms_d4f008,Step_Models_d4f008]
  Origin = -> Origin311
FEATURE [PartDesign::Body] Body142  label="PCB005"
  Group = -> [Sketch250,Pad171]
  Origin = -> Origin308
  Tip = -> Pad171
FEATURE [PartDesign::Body] Body143  label="16mm Standoff011"
  Group = -> [Sketch246,Pad169]
  Origin = -> Origin314
  Placement = pos=(125,-13,126) rot=(1,0,0;1.5708rad)
  Tip = -> Pad169
FEATURE [PartDesign::Body] Body144  label="Capacitor005"
  Group = -> [Sketch249,Pad168]
  Origin = -> Origin310
  Placement = pos=(10,14.5,-1.6) rot=(0,1,0;3.14159rad)
  Tip = -> Pad168
FEATURE [App::Part] Part021  label="H-bridge005"
  Group = -> [Body142,Shape233,Shape240,Body144,Body139]
  Origin = -> Origin312
  Placement = pos=(9.25,8.5,-11.2) rot=(0,0,1;0rad)
FEATURE [App::Part] Part022  label="motor_driver005"
  Group = -> [Board_d4f008,Part021]
  Origin = -> Origin307
  Placement = pos=(128.9,-30.6,129.9) rot=(0,0.707107,-0.707107;3.14159rad)
FEATURE [PartDesign::Body] Body145  label="AltCap003"
  Group = -> [Sketch244,Pad170]
  Origin = -> Origin305
  Tip = -> Pad170
FEATURE [App::Part] Part018  label="H-bridge004"
  Group = -> [Body128,Shape213,Shape214,Body129,Body145]
  Origin = -> Origin291
  Placement = pos=(9.25,8.5,-11.2) rot=(0,0,1;0rad)
FEATURE [App::Part] Part019  label="motor_driver004"
  Group = -> [Board_d4f007,Part018]
  Origin = -> Origin294
  Placement = pos=(-63.1,-30.6,129.9) rot=(0,0.707107,-0.707107;3.14159rad)
FEATURE [App::Part] Part020  label="side plate002"
  Group = -> [Body130,Body125,Body126,Body124,Body127,Body134,Body135,Body136,Body131,Body132,Body133,Part019,Body122,Body123,Body137,Body138,Body140,Body143,Body141,Part022]
  Origin = -> Origin299
  Placement = pos=(-1.72e-14,-72,0) rot=(0,0,1;3.14159rad)
FEATURE [Part::Feature] Part__Feature  label="SOLID"
  shape: bbox 1.6 x 0.8 x 0.45 mm, 26 faces (baked)
FEATURE [App::Part] R_0603_1608Metric
  Group = -> [Part__Feature]
  Origin = -> Origin319
  Placement = pos=(-38.25,47.25,1.65) rot=(0,0,1;3.14159rad)
FEATURE [Part::Feature] Part__Feature111  label="SOLID094"
  shape: bbox 1.6 x 0.8 x 0.45 mm, 26 faces (baked)
FEATURE [App::Part] R_0603_1608Metric009
  Group = -> [Part__Feature111]
  Origin = -> Origin320
  Placement = pos=(-38.25,43.75,1.65) rot=(0,0,1;3.14159rad)
FEATURE [Part::Feature] Part__Feature112  label="SOLID095"
  shape: bbox 2.54 x 15.24 x 11.54 mm, 148 faces (baked)
FEATURE [App::Part] PinHeader_1x06_P2_54mm_Vertical  label="PinHeader_1x06_P2.54mm_Vertical"
  Group = -> [Part__Feature112]
  Origin = -> Origin321
  Placement = pos=(-32,25,-0.05) rot=(-0.382683,0.92388,0;3.14159rad)
FEATURE [Part::Feature] Part__Feature113  label="SOLID096"
  shape: bbox 5.4 x 15.25 x 19.9 mm, 33 faces (baked)
FEATURE [App::Part] LED_D5_0mm_Horizontal_O6_35mm_Z15_0mm  label="LED_D5.0mm_Horizontal_O6.35mm_Z15.0mm"
  Group = -> [Part__Feature113]
  Origin = -> Origin322
  Placement = pos=(-30,87,1.65) rot=(0,0,1;3.14159rad)
FEATURE [Part::Feature] Part__Feature114  label="SOLID097"
  shape: bbox 5.4 x 15.25 x 19.9 mm, 33 faces (baked)
FEATURE [App::Part] LED_D5_0mm_Horizontal_O6_35mm_Z15_0mm001  label="LED_D5.0mm_Horizontal_O6.35mm_Z15.0mm001"
  Group = -> [Part__Feature114]
  Origin = -> Origin323
  Placement = pos=(-20,87,1.65) rot=(0,0,1;3.14159rad)
FEATURE [Part::Feature] Part__Feature115  label="SOLID098"
  shape: bbox 5.4 x 15.25 x 19.9 mm, 33 faces (baked)
FEATURE [App::Part] LED_D5_0mm_Horizontal_O6_35mm_Z15_0mm002  label="LED_D5.0mm_Horizontal_O6.35mm_Z15.0mm002"
  Group = -> [Part__Feature115]
  Origin = -> Origin324
  Placement = pos=(-10,87,1.65) rot=(0,0,1;3.14159rad)
FEATURE [Part::Feature] Part__Feature116  label="SOLID099"
  shape: bbox 30.6 x 5.8 x 16.6 mm, 66 faces (baked)
FEATURE [App::Part] power_module
  Group = -> [Part__Feature116]
  Origin = -> Origin325
  Placement = pos=(-12,34,1.65) rot=(0,0,1;1.5708rad)
FEATURE [Part::Feature] Part__Feature117  label="SOLID100"
  shape: bbox 6 x 4.9 x 1.75 mm, 156 faces (baked)
FEATURE [App::Part] SOIC_8_3_9x4_9mm_P1_27mm  label="SOIC-8_3.9x4.9mm_P1.27mm"
  Group = -> [Part__Feature117]
  Origin = -> Origin326
  Placement = pos=(-30,78,1.65) rot=(0,0,1;0rad)
FEATURE [Part::Feature] Part__Feature118  label="SOLID101"
  shape: bbox 1.6 x 0.8 x 0.45 mm, 26 faces (baked)
FEATURE [App::Part] R_0603_1608Metric010
  Group = -> [Part__Feature118]
  Origin = -> Origin327
  Placement = pos=(-36.25,87,1.65) rot=(0,0,1;0rad)
FEATURE [Part::Feature] Part__Feature119  label="SOLID102"
  shape: bbox 1.6 x 0.8 x 0.45 mm, 26 faces (baked)
FEATURE [App::Part] R_0603_1608Metric011
  Group = -> [Part__Feature119]
  Origin = -> Origin328
  Placement = pos=(-26.25,87,1.65) rot=(0,0,1;0rad)
FEATURE [Part::Feature] Part__Feature120  label="SOLID103"
  shape: bbox 1.6 x 0.8 x 0.45 mm, 26 faces (baked)
FEATURE [App::Part] R_0603_1608Metric012
  Group = -> [Part__Feature120]
  Origin = -> Origin329
  Placement = pos=(-16.25,87,1.65) rot=(0,0,1;0rad)
FEATURE [Part::Feature] Part__Feature121  label="SOLID104"
  shape: bbox 1.6 x 0.8 x 0.45 mm, 26 faces (baked)
FEATURE [App::Part] R_0603_1608Metric013
  Group = -> [Part__Feature121]
  Origin = -> Origin330
  Placement = pos=(-27.5,90,1.65) rot=(0,0,1;0rad)
FEATURE [Part::Feature] Part__Feature122  label="SOLID105"
  shape: bbox 1.6 x 0.8 x 0.45 mm, 26 faces (baked)
FEATURE [App::Part] R_0603_1608Metric014
  Group = -> [Part__Feature122]
  Origin = -> Origin331
  Placement = pos=(-32.75,90,1.65) rot=(0,0,1;3.14159rad)
FEATURE [Part::Feature] Part__Feature123  label="SOLID106"
  shape: bbox 1.6 x 0.8 x 0.45 mm, 26 faces (baked)
FEATURE [App::Part] R_0603_1608Metric015
  Group = -> [Part__Feature123]
  Origin = -> Origin332
  Placement = pos=(-22.5,90,1.65) rot=(0,0,1;3.14159rad)
FEATURE [Part::Feature] Part__Feature124  label="SOLID107"
  shape: bbox 1.6 x 0.8 x 0.45 mm, 26 faces (baked)
FEATURE [App::Part] R_0603_1608Metric016
  Group = -> [Part__Feature124]
  Origin = -> Origin333
  Placement = pos=(-28,82,1.65) rot=(0,0,1;3.14159rad)
FEATURE [Part::Feature] Part__Feature125  label="SOLID108"
  shape: bbox 1.6 x 0.8 x 0.45 mm, 26 faces (baked)
FEATURE [App::Part] R_0603_1608Metric017
  Group = -> [Part__Feature125]
  Origin = -> Origin334
  Placement = pos=(-28,84,1.65) rot=(0,0,1;3.14159rad)
FEATURE [Part::Feature] Part__Feature126  label="SOLID109"
  shape: bbox 1.6 x 0.8 x 0.45 mm, 26 faces (baked)
FEATURE [App::Part] R_0603_1608Metric018
  Group = -> [Part__Feature126]
  Origin = -> Origin335
  Placement = pos=(-52,97.25,-0.05) rot=(0,1,0;3.14159rad)
FEATURE [Part::Feature] Part__Feature127  label="SOLID110"
  shape: bbox 1.6 x 0.8 x 0.45 mm, 26 faces (baked)
FEATURE [App::Part] R_0603_1608Metric019
  Group = -> [Part__Feature127]
  Origin = -> Origin336
  Placement = pos=(-55.75,97.25,-0.05) rot=(0,1,0;3.14159rad)
FEATURE [Part::Feature] Part__Feature128  label="SOLID111"
  shape: bbox 1.6 x 0.8 x 0.45 mm, 26 faces (baked)
FEATURE [App::Part] R_0603_1608Metric020
  Group = -> [Part__Feature128]
  Origin = -> Origin337
  Placement = pos=(-40.5,85.5,1.65) rot=(0,0,1;1.5708rad)
FEATURE [Part::Feature] Part__Feature129  label="SOLID112"
  shape: bbox 1.6 x 0.8 x 0.45 mm, 26 faces (baked)
FEATURE [App::Part] R_0603_1608Metric021
  Group = -> [Part__Feature129]
  Origin = -> Origin338
  Placement = pos=(-36,80,1.65) rot=(0,0,1;3.14159rad)
FEATURE [Part::Feature] Part__Feature130  label="SOLID113"
  shape: bbox 15.37 x 15.37 x 27.6 mm, 9 faces (baked)
FEATURE [App::Part] L_Radial_D14_2mm_P10_00mm_Neosid_SD14  label="L_Radial_D14.2mm_P10.00mm_Neosid_SD14"
  Group = -> [Part__Feature130]
  Origin = -> Origin339
  Placement = pos=(-25.75,55,1.65) rot=(0,0,-1;1.5708rad)
FEATURE [Part::Feature] Part__Feature131  label="SOLID114"
  shape: bbox 12.16 x 12 x 12.6 mm, 63 faces (baked)
FEATURE [App::Part] PhoenixContact_MSTBA_2_5_2_G_5_08_1x02_P5_08mm_Horizontal  label="PhoenixContact_MSTBA_2,5_2-G-5,08_1x02_P5.08mm_Horizontal"
  Group = -> [Part__Feature131]
  Origin = -> Origin340
  Placement = pos=(-5,94,1.65) rot=(0,0,1;3.14159rad)
FEATURE [Part::Feature] Part__Feature132  label="SOLID115"
  shape: bbox 2.54 x 2.54 x 11.54 mm, 28 faces (baked)
FEATURE [App::Part] PinHeader_1x01_P2_54mm_Vertical  label="PinHeader_1x01_P2.54mm_Vertical"
  Group = -> [Part__Feature132]
  Origin = -> Origin341
  Placement = pos=(-12.5,16,1.65) rot=(0,0,1;0rad)
FEATURE [Part::Feature] Part__Feature133  label="SOLID116"
  shape: bbox 2.54 x 2.54 x 11.54 mm, 28 faces (baked)
FEATURE [App::Part] PinHeader_1x01_P2_54mm_Vertical001  label="PinHeader_1x01_P2.54mm_Vertical001"
  Group = -> [Part__Feature133]
  Origin = -> Origin342
  Placement = pos=(-8,48,1.65) rot=(0,0,1;0rad)
FEATURE [Part::Feature] Part__Feature134  label="SOLID117"
  shape: bbox 2.54 x 22.86 x 11.54 mm, 220 faces (baked)
FEATURE [App::Part] PinHeader_1x09_P2_54mm_Vertical  label="PinHeader_1x09_P2.54mm_Vertical"
  Group = -> [Part__Feature134]
  Origin = -> Origin343
  Placement = pos=(-39.5,76.5,1.65) rot=(0,0,1;0rad)
FEATURE [Part::Feature] Part__Feature135  label="SOLID118"
  shape: bbox 2.54 x 15.24 x 10.1 mm, 196 faces (baked)
FEATURE [App::Part] PinSocket_1x06_P2_54mm_Vertical  label="PinSocket_1x06_P2.54mm_Vertical"
  Group = -> [Part__Feature135]
  Origin = -> Origin344
  Placement = pos=(-15,67,1.65) rot=(0,0,1;0rad)
FEATURE [Part::Feature] Part__Feature136  label="SOLID119"
  shape: bbox 2.54 x 10.16 x 11.54 mm, 100 faces (baked)
FEATURE [App::Part] PinHeader_1x04_P2_54mm_Vertical  label="PinHeader_1x04_P2.54mm_Vertical"
  Group = -> [Part__Feature136]
  Origin = -> Origin345
  Placement = pos=(-13,6,-0.05) rot=(0.92388,0.382683,0;3.14159rad)
FEATURE [Part::Feature] Part__Feature137  label="SOLID120"
  shape: bbox 5.08 x 50.8 x 10.1 mm, 1250 faces (baked)
FEATURE [App::Part] PinSocket_2x20_P2_54mm_Vertical  label="PinSocket_2x20_P2.54mm_Vertical"
  Group = -> [Part__Feature137]
  Origin = -> Origin346
  Placement = pos=(-45,35,1.65) rot=(0,0,1;3.14159rad)
FEATURE [Part::Feature] Part__Feature138  label="SOLID121"
  shape: bbox 22.32 x 12 x 12.6 mm, 113 faces (baked)
FEATURE [App::Part] PhoenixContact_MSTBA_2_5_4_G_5_08_1x04_P5_08mm_Horizontal001  label="PhoenixContact_MSTBA_2,5_4-G-5,08_1x04_P5.08mm_Horizontal001"
  Group = -> [Part__Feature138]
  Origin = -> Origin347
  Placement = pos=(-20,94,1.65) rot=(0,0,1;3.14159rad)
FEATURE [Part::Feature] Part__Feature139  label="SOLID122"
  shape: bbox 9 x 2.5 x 11.1 mm, 6 faces (baked)
FEATURE [App::Part] C_Disc_D9_0mm_W2_5mm_P5_00mm  label="C_Disc_D9.0mm_W2.5mm_P5.00mm"
  Group = -> [Part__Feature139]
  Origin = -> Origin348
  Placement = pos=(-5,89,1.65) rot=(0,0,-1;1.5708rad)
FEATURE [Part::Feature] Part__Feature140  label="SOLID123"
  shape: bbox 9.886 x 10.23 x 10 mm, 54 faces (baked)
FEATURE [App::Part] CP_Radial_D8_0mm_P3_50mm  label="CP_Radial_D8.0mm_P3.50mm"
  Group = -> [Part__Feature140]
  Origin = -> Origin349
  Placement = pos=(-15,78,1.65) rot=(0,0,1;1.5708rad)
FEATURE [Part::Feature] Part__Feature141  label="SOLID124"
  shape: bbox 13.47 x 13.66 x 10.5 mm, 41 faces (baked)
FEATURE [App::Part] CP_Elec_10x10_5  label="CP_Elec_10x10.5"
  Group = -> [Part__Feature141]
  Origin = -> Origin350
  Placement = pos=(-23.75,34.5,1.65) rot=(0,0,-1;1.5708rad)
FEATURE [Part::Feature] Part__Feature142  label="SOLID125"
  shape: bbox 13.47 x 13.66 x 10.5 mm, 41 faces (baked)
FEATURE [App::Part] CP_Elec_10x10_5001  label="CP_Elec_10x10.006"
  Group = -> [Part__Feature142]
  Origin = -> Origin351
  Placement = pos=(-25.75,65.5,1.65) rot=(0,0,1;1.5708rad)
FEATURE [Part::Feature] Part__Feature143  label="SOLID126"
  shape: bbox 2 x 1.25 x 1.25 mm, 28 faces (baked)
FEATURE [App::Part] C_0805_2012Metric
  Group = -> [Part__Feature143]
  Origin = -> Origin352
  Placement = pos=(-8,29,1.65) rot=(0,0,1;1.5708rad)
FEATURE [Part::Feature] Part__Feature144  label="SOLID127"
  shape: bbox 1.6 x 0.8 x 0.8 mm, 28 faces (baked)
FEATURE [App::Part] C_0603_1608Metric
  Group = -> [Part__Feature144]
  Origin = -> Origin353
  Placement = pos=(-55.75,99,-0.05) rot=(0,1,0;3.14159rad)
FEATURE [Part::Feature] Part__Feature145  label="SOLID128"
  shape: bbox 1.6 x 0.8 x 0.8 mm, 28 faces (baked)
FEATURE [App::Part] C_0603_1608Metric004
  Group = -> [Part__Feature145]
  Origin = -> Origin354
  Placement = pos=(-23.875,82,1.65) rot=(0,0,1;0rad)
FEATURE [Part::Feature] Part__Feature146  label="COMPOUND009"
  shape: bbox 110 x 100 x 1.6 mm, 115 faces (baked)
FEATURE [App::Part] Open_CASCADE_STEP_translator_7_3_1004  label="Open CASCADE STEP translator 7.3 006"
  Group = -> [R_0603_1608Metric,R_0603_1608Metric009,PinHeader_1x06_P2_54mm_Vertical,LED_D5_0mm_Horizontal_O6_35mm_Z15_0mm,LED_D5_0mm_Horizontal_O6_35mm_Z15_0mm001,LED_D5_0mm_Horizontal_O6_35mm_Z15_0mm002,power_module,SOIC_8_3_9x4_9mm_P1_27mm,R_0603_1608Metric010,R_0603_1608Metric011,R_0603_1608Metric012,R_0603_1608Metric013,R_0603_1608Metric014,R_0603_1608Metric015,R_0603_1608Metric016,R_0603_1608Metric017,+21 more]
  Origin = -> Origin355
  Placement = pos=(70,17,30) rot=(1,0,0;1.5708rad)
FEATURE [Sketcher::SketchObject] Sketch251
  FullyConstrained = false
  MapMode = 5
  Support = -> [XY_Plane356]
  sketch-geometry (1):
    g0: Circle CenterX=0 CenterY=0 CenterZ=0 NormalX=0 NormalY=0 NormalZ=1 AngleXU=0 Radius=3.4
  constraints (2):
    c: Coincident(g0,g-1)
    c: Diameter(g0) = 6.8
FEATURE [PartDesign::Pad] Pad173
  AllowMultiFace = false
  Direction = (1,1,1)
  Length = 54
  Length2 = 100
  Midplane = true
  Profile = -> Sketch251
  Type = 0
FEATURE [Sketcher::SketchObject] Sketch252
  FullyConstrained = false
  MapMode = 5
  Placement = pos=(0,0,0) rot=(1,0,0;1.5708rad)
  Support = -> [XZ_Plane354]
  sketch-geometry (6):
    g0: ArcOfCircle CenterX=-4e-16 CenterY=31.5 CenterZ=0 NormalX=0 NormalY=0 NormalZ=1 AngleXU=0 Radius=3.4 StartAngle=5.36697 EndAngle=10.341
    g1: ArcOfCircle CenterX=4e-16 CenterY=-31.5 CenterZ=0 NormalX=0 NormalY=0 NormalZ=1 AngleXU=0 Radius=3.4 StartAngle=2.22537 EndAngle=7.1994
    g2: LineSegment StartX=-2.07 StartY=28.8028 StartZ=0 EndX=-2.07 EndY=-28.8028 EndZ=0
    g3: LineSegment StartX=2.07 StartY=-28.8028 StartZ=0 EndX=2.07 EndY=28.8028 EndZ=0
    g4: Circle CenterX=-4e-16 CenterY=31.5 CenterZ=0 NormalX=0 NormalY=0 NormalZ=1 AngleXU=0 Radius=2.75
    g5: Circle CenterX=4e-16 CenterY=-31.5 CenterZ=0 NormalX=0 NormalY=0 NormalZ=1 AngleXU=0 Radius=2.75
  constraints (16):
    c: Vertical(g3)
    c: Coincident(g3,g0)
    c: Coincident(g3,g1)
    c: Coincident(g1,g2)
    c: Coincident(g2,g0)
    c: Symmetric(g0,g0,g-2)
    c: Symmetric(g1,g1,g-2)
    c: DistanceY(g1,g0) = 63
    c: Diameter(g0) = 6.8
    c: Equal(g0,g1)
    c: Symmetric(g1,g0,g-1)
    c: DistanceX(g1,g1) = 4.14
    c: Coincident(g5,g1)
    c: Coincident(g4,g0)
    c: Diameter(g4) = 5.5
    c: Equal(g4,g5)
FEATURE [PartDesign::Pad] Pad174
  AllowMultiFace = false
  BaseFeature = -> Pad173
  Direction = (1,1,1)
  Length = 0.7
  Length2 = 100
  Midplane = true
  Profile = -> Sketch252
  Type = 0
FEATURE [PartDesign::Body] Body146  label="Spring1"
  Group = -> [Sketch251,Pad173,Sketch252,Pad174]
  Origin = -> Origin356
  Placement = pos=(32.1244,-46,140.641) rot=(0,-1,0;1.0472rad)
  Tip = -> Pad174
FEATURE [PartDesign::FeatureBase] Clone018
  BaseFeature = -> Body146
  Placement = pos=(32.1244,-51,140.641) rot=(0,-1,0;1.0472rad)
FEATURE [PartDesign::Body] Body147  label="Spring2"
  BaseFeature = -> Body146
  Group = -> [Clone018]
  Origin = -> Origin357
  Placement = pos=(0,98,0) rot=(0,0,1;0rad)
  Tip = -> Clone018
FEATURE [PartDesign::FeatureBase] Clone019
  BaseFeature = -> Body146
  Placement = pos=(32.1244,-47,140.641) rot=(0,-1,0;1.0472rad)
FEATURE [PartDesign::Body] Body148  label="Spring3"
  BaseFeature = -> Body146
  Group = -> [Clone019]
  Origin = -> Origin358
  Placement = pos=(0,-2.5,0) rot=(0,0,1;3.14159rad)
  Tip = -> Clone019
FEATURE [PartDesign::FeatureBase] Clone020
  BaseFeature = -> Body147
  Placement = pos=(0,98,0) rot=(0,0,1;0rad)
FEATURE [PartDesign::Body] Body149  label="Spring4"
  BaseFeature = -> Body147
  Group = -> [Clone020]
  Origin = -> Origin359
  Placement = pos=(0,0,0) rot=(0,0,1;3.14159rad)
  Tip = -> Clone020
FEATURE [TechDraw::DrawSVGTemplate] Template
  EditableTexts = Designed_by_Name=Designed by Name; Drawing_number=Drawing number; FC-Date=Date; FC-SC=Scale; FC-SH=Sheet; FC-Title=Title; Subtitle=Subtitle; Weight=Weight
  Height = 210
  Orientation = 1
  Width = 297
FEATURE [TechDraw::DrawViewPart] View001
  CoarseView = false
  Direction = (0,1,0)
  Focus = 100
  HardHidden = false
  IsoCount = 0
  IsoHidden = false
  IsoVisible = false
  LockPosition = false
  Perspective = false
  Rotation = 0
  ScaleType = 0
  SeamHidden = false
  SeamVisible = false
  SmoothHidden = false
  SmoothVisible = false
  Source = -> [Body024]
  X = 148.5
  XDirection = (-1,0,0)
  Y = 105
FEATURE [TechDraw::DrawViewSymbol] Symbol
  LockPosition = false
  Rotation = 0
  ScaleType = 2
  Symbol = <blob: 300471 chars omitted>
  X = 45.3246
  Y = 42.6303
FEATURE [TechDraw::DrawViewSymbol] Symbol001
  LockPosition = false
  Rotation = 0
  ScaleType = 2
  Symbol = <blob: 300471 chars omitted>
  X = 108.358
  Y = 42.6303
FEATURE [Part::Feature] Part__Feature147  label="YAAJ_DCDC_StepDown_LM2596_cp"
  Placement = pos=(-80.5,9,140) rot=(0,0,1;0rad)
  shape: bbox 43.84 x 21.3 x 15.15 mm, 2679 faces, 80 solids (baked)
FEATURE [PartDesign::Chamfer] Chamfer001
  Angle = 45
  Base = -> Pad043 [Edge74,Edge71,Edge65,Edge68]
  BaseFeature = -> Pad043
  ChamferType = 0
  FlipDirection = false
  Placement = pos=(0,0,0) rot=(1,0,0;1.5708rad)
  Size = 1.8
  Size2 = 1
  SupportTransform = false
FEATURE [PartDesign::Body] Body028  label="Inner_Side_Plate"
  Group = -> [Sketch071,Pad043,Chamfer001]
  Origin = -> Origin040
  Placement = pos=(0,-11,0) rot=(0,0,1;0rad)
  Tip = -> Chamfer001
FEATURE [TechDraw::DrawViewPart] View
  CoarseView = false
  Direction = (0,1,0)
  Focus = 100
  HardHidden = false
  IsoCount = 0
  IsoHidden = false
  IsoVisible = false
  LockPosition = false
  Perspective = false
  Rotation = 0
  ScaleType = 0
  SeamHidden = false
  SeamVisible = false
  SmoothHidden = false
  SmoothVisible = false
  Source = -> [Body028]
  X = 148.832
  XDirection = (-1,0,0)
  Y = 167.37
FEATURE [Part::Feature] Part__Feature148  label="YAAJ_DCDC_StepDown_LM2596_cp001"
  Placement = pos=(54.5,-15,123.5) rot=(0.57735,0.57735,-0.57735;2.0944rad)
  shape: bbox 21.3 x 15.15 x 43.84 mm, 2679 faces, 80 solids (baked)
FEATURE [Sketcher::SketchObject] Sketch253
  FullyConstrained = false
  MapMode = 5
  Support = -> [XY_Plane360]
  sketch-geometry (8):
    g0: LineSegment StartX=-1.58771 StartY=2.75 StartZ=0 EndX=-3.17543 EndY=5.92e-13 EndZ=0
    g1: LineSegment StartX=-3.17543 StartY=5.922e-13 StartZ=0 EndX=-1.58771 EndY=-2.75 EndZ=0
    g2: LineSegment StartX=-1.58771 StartY=-2.75 StartZ=0 EndX=1.58771 EndY=-2.75 EndZ=0
    g3: LineSegment StartX=1.58771 StartY=-2.75 StartZ=0 EndX=3.17543 EndY=3.237e-13 EndZ=0
    g4: LineSegment StartX=3.17543 StartY=3.237e-13 StartZ=0 EndX=1.58771 EndY=2.75 EndZ=0
    g5: LineSegment StartX=1.58771 StartY=2.75 StartZ=0 EndX=-1.58771 EndY=2.75 EndZ=0
    g6: Circle CenterX=0 CenterY=0 CenterZ=0 NormalX=0 NormalY=0 NormalZ=1 AngleXU=0 Radius=3.17543
    g7: Circle CenterX=0 CenterY=0 CenterZ=0 NormalX=0 NormalY=0 NormalZ=1 AngleXU=0 Radius=1.75
  constraints (18):
    c: Coincident(g0,g1)
    c: Coincident(g1,g2)
    c: Coincident(g2,g3)
    c: Coincident(g3,g4)
    c: Coincident(g4,g5)
    c: Coincident(g5,g0)
    c: Equal(g0, g1-g5) x5
    c: PointOnObject(g0,g6)
    c: PointOnObject(g1,g6)
    c: PointOnObject(g2,g6)
    c: PointOnObject(g3,g6)
    c: PointOnObject(g4,g6)
    c: PointOnObject(g5,g6)
    c: Coincident(g6,g7)
    c: Coincident(g6,g-1)
    c: Horizontal(g5)
    c: Distance(g0,g1) = 5.5
    c: Diameter(g7) = 3.5
FEATURE [PartDesign::Pad] Pad175
  AllowMultiFace = false
  Direction = (1,1,1)
  Length = 2
  Length2 = 100
  Profile = -> Sketch253
  Type = 0
FEATURE [PartDesign::Body] Body150  label="2mm_standoff"
  Group = -> [Sketch253,Pad175]
  Origin = -> Origin360
  Placement = pos=(-37.5,-13,118.5) rot=(1,0,0;1.5708rad)
  Tip = -> Pad175
FEATURE [PartDesign::FeatureBase] Clone021
  BaseFeature = -> Body150
  Placement = pos=(-37.5,-13,118.5) rot=(1,0,0;1.5708rad)
FEATURE [PartDesign::Body] Body151  label="2mm_standoff2"
  BaseFeature = -> Body150
  Group = -> [Clone021]
  Origin = -> Origin361
  Placement = pos=(-16,0,-30.5) rot=(0,0,1;0rad)
  Tip = -> Clone021
FEATURE [Sketcher::SketchObject] Sketch254
  FullyConstrained = false
  MapMode = 5
  Support = -> [XY_Plane362]
  sketch-geometry (2):
    g0: Circle CenterX=0 CenterY=0 CenterZ=0 NormalX=0 NormalY=0 NormalZ=1 AngleXU=0 Radius=3.5
    g1: Circle CenterX=0 CenterY=0 CenterZ=0 NormalX=0 NormalY=0 NormalZ=1 AngleXU=0 Radius=2.25
  constraints (4):
    c: Coincident(g1,g0)
    c: Coincident(g1,g-1)
    c: Diameter(g1) = 4.5
    c: Diameter(g0) = 7
FEATURE [PartDesign::Pad] Pad176
  AllowMultiFace = false
  Direction = (1,1,1)
  Length = 10
  Length2 = 100
  Profile = -> Sketch254
  Type = 0
FEATURE [PartDesign::Body] Body152  label="SpringSpacer"
  Group = -> [Sketch254,Pad176]
  Origin = -> Origin362
  Placement = pos=(-60,-13,124) rot=(1,0,0;1.5708rad)
  Tip = -> Pad176
FEATURE [TechDraw::DrawViewDimension] Dimension
  Arbitrary = false
  ArbitraryTolerances = false
  EqualTolerance = false
  FormatSpec = %.2f
  FormatSpecOverTolerance = %+.2f
  FormatSpecUnderTolerance = %+.2f
  Inverted = false
  LockPosition = false
  MeasureType = 1
  OverTolerance = 0
  References2D = -> [View]
  Rotation = 0
  ScaleType = 0
  TheoreticalExact = false
  Type = 1
  UnderTolerance = 0
  X = -6.95146
  Y = 27.9463
FEATURE [TechDraw::DrawViewDimension] Dimension001
  Arbitrary = false
  ArbitraryTolerances = false
  EqualTolerance = false
  FormatSpec = %.2f
  FormatSpecOverTolerance = %+.2f
  FormatSpecUnderTolerance = %+.2f
  Inverted = false
  LockPosition = false
  MeasureType = 1
  OverTolerance = 0
  References2D = -> [View]
  Rotation = 0
  ScaleType = 0
  TheoreticalExact = false
  Type = 1
  UnderTolerance = 0
  X = -45.75
  Y = -1.75
FEATURE [TechDraw::DrawViewDimension] Dimension002
  Arbitrary = false
  ArbitraryTolerances = false
  EqualTolerance = false
  FormatSpec = %.2f
  FormatSpecOverTolerance = %+.2f
  FormatSpecUnderTolerance = %+.2f
  Inverted = false
  LockPosition = false
  MeasureType = 1
  OverTolerance = 0
  References2D = -> [View]
  Rotation = 0
  ScaleType = 0
  TheoreticalExact = false
  Type = 2
  UnderTolerance = 0
  X = -73.1817
  Y = 0.684762
FEATURE [TechDraw::DrawViewDimension] Dimension003
  Arbitrary = false
  ArbitraryTolerances = false
  EqualTolerance = false
  FormatSpec = %.2f
  FormatSpecOverTolerance = %+.2f
  FormatSpecUnderTolerance = %+.2f
  Inverted = false
  LockPosition = false
  MeasureType = 1
  OverTolerance = 0
  References2D = -> [View]
  Rotation = 0
  ScaleType = 0
  TheoreticalExact = false
  Type = 1
  UnderTolerance = 0
  X = -18.75
  Y = -4.65657
FEATURE [TechDraw::DrawViewDimension] Dimension004
  Arbitrary = false
  ArbitraryTolerances = false
  EqualTolerance = false
  FormatSpec = %.2f
  FormatSpecOverTolerance = %+.2f
  FormatSpecUnderTolerance = %+.2f
  Inverted = false
  LockPosition = false
  MeasureType = 1
  OverTolerance = 0
  References2D = -> [View]
  Rotation = 0
  ScaleType = 0
  TheoreticalExact = false
  Type = 2
  UnderTolerance = 0
  X = -81.5813
  Y = -14.267
FEATURE [TechDraw::DrawPage] Page
  KeepUpdated = true
  NextBalloonIndex = 1
  ProjectionType = 0
  Template = -> Template
  Views = -> [View,View001,Symbol,Symbol001,Dimension,Dimension001,Dimension002,Dimension003,Dimension004]
FEATURE [Sketcher::SketchObject] Sketch255
  FullyConstrained = false
  MapMode = 5
  Support = -> [XY_Plane364]
  sketch-geometry (13):
    g0: LineSegment StartX=-15 StartY=21 StartZ=0 EndX=15 EndY=21 EndZ=0
    g1: LineSegment StartX=15 StartY=21 StartZ=0 EndX=15 EndY=-16 EndZ=0
    g2: LineSegment StartX=15 StartY=-16 StartZ=0 EndX=-15 EndY=-16 EndZ=0
    g3: LineSegment StartX=-15 StartY=-16 StartZ=0 EndX=-15 EndY=21 EndZ=0
    g4: Circle CenterX=0 CenterY=0 CenterZ=0 NormalX=0 NormalY=0 NormalZ=1 AngleXU=0 Radius=3.25
    g5: Circle CenterX=-10 CenterY=10 CenterZ=0 NormalX=0 NormalY=0 NormalZ=1 AngleXU=0 Radius=1.75
    g6: Circle CenterX=10 CenterY=10 CenterZ=0 NormalX=0 NormalY=0 NormalZ=1 AngleXU=0 Radius=1.75
    g7: Circle CenterX=10 CenterY=-10 CenterZ=0 NormalX=0 NormalY=0 NormalZ=1 AngleXU=0 Radius=1.75
    g8: Circle CenterX=-10 CenterY=-10 CenterZ=0 NormalX=0 NormalY=0 NormalZ=1 AngleXU=0 Radius=1.75
    g9: LineSegment StartX=-10 StartY=10 StartZ=0 EndX=10 EndY=10 EndZ=0
    g10: LineSegment StartX=10 StartY=10 StartZ=0 EndX=10 EndY=-10 EndZ=0
    g11: LineSegment StartX=10 StartY=-10 StartZ=0 EndX=-10 EndY=-10 EndZ=0
    g12: LineSegment StartX=-10 StartY=-10 StartZ=0 EndX=-10 EndY=10 EndZ=0
  constraints (32):
    c: Coincident(g0,g1)
    c: Coincident(g1,g2)
    c: Coincident(g2,g3)
    c: Coincident(g3,g0)
    c: Horizontal(g2)
    c: Vertical(g1)
    c: Vertical(g3)
    c: DistanceY(g-1,g0) = 21
    c: DistanceY(g3,g3) = 37
    c: DistanceX(g0,g0) = 30
    c: Symmetric(g0,g0,g-2)
    c: Coincident(g4,g-1)
    c: Diameter(g4) = 6.5
    c: Coincident(g9,g10)
    c: Coincident(g10,g11)
    c: Coincident(g11,g12)
    c: Coincident(g12,g9)
    c: Horizontal(g9)
    c: Horizontal(g11)
    c: Vertical(g10)
    c: Vertical(g12)
    c: Symmetric(g9,g10,g4)
    c: DistanceX(g9,g9) = 20
    c: DistanceY(g12,g12) = 20
    c: Coincident(g5,g9)
    c: Coincident(g6,g9)
    c: Coincident(g7,g10)
    c: Coincident(g8,g11)
    c: Diameter(g8) = 3.5
    c: Equal(g8,g5)
    c: Equal(g8,g6)
    c: Equal(g8,g7)
FEATURE [PartDesign::Pad] Pad177
  AllowMultiFace = false
  Direction = (1,1,1)
  Length = 25
  Length2 = 100
  Profile = -> Sketch255
  Type = 0
FEATURE [PartDesign::Chamfer] Chamfer002
  Angle = 45
  Base = -> Pad177 [Edge4]
  BaseFeature = -> Pad177
  ChamferType = 0
  FlipDirection = false
  Size = 2
  Size2 = 1
  SupportTransform = false
FEATURE [Sketcher::SketchObject] Sketch256
  FullyConstrained = false
  MapMode = 5
  Placement = pos=(0,0,0) rot=(1,0,0;3.14159rad)
  Support = -> [Chamfer002]
  sketch-geometry (39):
    g0: LineSegment StartX=3.31976 StartY=5.75 StartZ=0 EndX=-3.31976 EndY=5.75 EndZ=0
    g1: LineSegment StartX=-3.31976 StartY=5.75 StartZ=0 EndX=-6.63953 EndY=-5.925e-12 EndZ=0
    g2: LineSegment StartX=-6.63953 StartY=-5.925e-12 StartZ=0 EndX=-3.31976 EndY=-5.75 EndZ=0
    g3: LineSegment StartX=-3.31976 StartY=-5.75 StartZ=0 EndX=3.31976 EndY=-5.75 EndZ=0
    g4: LineSegment StartX=3.31976 StartY=-5.75 StartZ=0 EndX=6.63953 EndY=-5.8877e-12 EndZ=0
    g5: LineSegment StartX=6.63953 StartY=-5.8877e-12 StartZ=0 EndX=3.31976 EndY=5.75 EndZ=0
    g6: Circle CenterX=0 CenterY=0 CenterZ=0 NormalX=0 NormalY=0 NormalZ=1 AngleXU=0 Radius=6.63953
    g7: LineSegment StartX=11.6454 StartY=7.15 StartZ=0 EndX=13.2909 EndY=10 EndZ=0
    g8: LineSegment StartX=13.2909 StartY=10 StartZ=0 EndX=11.6454 EndY=12.85 EndZ=0
    g9: LineSegment StartX=11.6454 StartY=12.85 StartZ=0 EndX=8.35455 EndY=12.85 EndZ=0
    g10: LineSegment StartX=8.35455 StartY=12.85 StartZ=0 EndX=6.7091 EndY=10 EndZ=0
    g11: LineSegment StartX=6.7091 StartY=10 StartZ=0 EndX=8.35455 EndY=7.15 EndZ=0
    g12: LineSegment StartX=8.35455 StartY=7.15 StartZ=0 EndX=11.6454 EndY=7.15 EndZ=0
    g13: Circle CenterX=10 CenterY=10 CenterZ=0 NormalX=0 NormalY=0 NormalZ=1 AngleXU=0 Radius=3.2909
    g14: LineSegment StartX=-8.35455 StartY=7.15 StartZ=0 EndX=-6.7091 EndY=10 EndZ=0
    g15: LineSegment StartX=-6.7091 StartY=10 StartZ=0 EndX=-8.35455 EndY=12.85 EndZ=0
    g16: LineSegment StartX=-8.35455 StartY=12.85 StartZ=0 EndX=-11.6454 EndY=12.85 EndZ=0
    g17: LineSegment StartX=-11.6454 StartY=12.85 StartZ=0 EndX=-13.2909 EndY=10 EndZ=0
    g18: LineSegment StartX=-13.2909 StartY=10 StartZ=0 EndX=-11.6454 EndY=7.15 EndZ=0
    g19: LineSegment StartX=-11.6454 StartY=7.15 StartZ=0 EndX=-8.35455 EndY=7.15 EndZ=0
    g20: Circle CenterX=-10 CenterY=10 CenterZ=0 NormalX=0 NormalY=0 NormalZ=1 AngleXU=0 Radius=3.2909
    g21: LineSegment StartX=-8.35455 StartY=-12.85 StartZ=0 EndX=-6.7091 EndY=-10 EndZ=0
    g22: LineSegment StartX=-6.7091 StartY=-10 StartZ=0 EndX=-8.35455 EndY=-7.15 EndZ=0
    g23: LineSegment StartX=-8.35455 StartY=-7.15 StartZ=0 EndX=-11.6454 EndY=-7.15 EndZ=0
    g24: LineSegment StartX=-11.6454 StartY=-7.15 StartZ=0 EndX=-13.2909 EndY=-10 EndZ=0
    g25: LineSegment StartX=-13.2909 StartY=-10 StartZ=0 EndX=-11.6454 EndY=-12.85 EndZ=0
    g26: LineSegment StartX=-11.6454 StartY=-12.85 StartZ=0 EndX=-8.35455 EndY=-12.85 EndZ=0
    g27: Circle CenterX=-10 CenterY=-10 CenterZ=0 NormalX=0 NormalY=0 NormalZ=1 AngleXU=0 Radius=3.2909
    g28: LineSegment StartX=11.6454 StartY=-12.85 StartZ=0 EndX=13.2909 EndY=-10 EndZ=0
    g29: LineSegment StartX=13.2909 StartY=-10 StartZ=0 EndX=11.6454 EndY=-7.15 EndZ=0
    g30: LineSegment StartX=11.6454 StartY=-7.15 StartZ=0 EndX=8.35455 EndY=-7.15 EndZ=0
    g31: LineSegment StartX=8.35455 StartY=-7.15 StartZ=0 EndX=6.7091 EndY=-10 EndZ=0
    g32: LineSegment StartX=6.7091 StartY=-10 StartZ=0 EndX=8.35455 EndY=-12.85 EndZ=0
    g33: LineSegment StartX=8.35455 StartY=-12.85 StartZ=0 EndX=11.6454 EndY=-12.85 EndZ=0
    g34: Circle CenterX=10 CenterY=-10 CenterZ=0 NormalX=0 NormalY=0 NormalZ=1 AngleXU=0 Radius=3.2909
    g35: LineSegment StartX=-10 StartY=10 StartZ=0 EndX=10 EndY=10 EndZ=0
    g36: LineSegment StartX=10 StartY=10 StartZ=0 EndX=10 EndY=-10 EndZ=0
    g37: LineSegment StartX=10 StartY=-10 StartZ=0 EndX=-10 EndY=-10 EndZ=0
    g38: LineSegment StartX=-10 StartY=-10 StartZ=0 EndX=-10 EndY=10 EndZ=0
  constraints (91):
    c: Coincident(g0,g1)
    c: Coincident(g1,g2)
    c: Coincident(g2,g3)
    c: Coincident(g3,g4)
    c: Coincident(g4,g5)
    c: Coincident(g5,g0)
    c: Equal(g0, g1-g5) x5
    c: PointOnObject(g0,g6)
    c: PointOnObject(g1,g6)
    c: PointOnObject(g2,g6)
    c: PointOnObject(g3,g6)
    c: PointOnObject(g4,g6)
    c: PointOnObject(g5,g6)
    c: Coincident(g6,g-1)
    c: Horizontal(g3)
    c: DistanceY(g3,g0) = 11.5
    c: Coincident(g7,g8)
    c: Coincident(g8,g9)
    c: Coincident(g9,g10)
    c: Coincident(g10,g11)
    c: Coincident(g11,g12)
    c: Coincident(g12,g7)
    c: Equal(g7, g8-g12) x5
    c: PointOnObject(g7,g13)
    c: PointOnObject(g8,g13)
    c: PointOnObject(g9,g13)
    c: PointOnObject(g10,g13)
    c: PointOnObject(g11,g13)
    c: PointOnObject(g12,g13)
    c: Coincident(g14,g15)
    c: Coincident(g15,g16)
    c: Coincident(g16,g17)
    c: Coincident(g17,g18)
    c: Coincident(g18,g19)
    c: Coincident(g19,g14)
    c: Equal(g14, g15-g19) x5
    c: PointOnObject(g14,g20)
    c: PointOnObject(g15,g20)
    c: PointOnObject(g16,g20)
    c: PointOnObject(g17,g20)
    c: PointOnObject(g18,g20)
    c: PointOnObject(g19,g20)
    c: Coincident(g21,g22)
    c: Coincident(g22,g23)
    c: Coincident(g23,g24)
    c: Coincident(g24,g25)
    c: Coincident(g25,g26)
    c: Coincident(g26,g21)
    c: Equal(g21, g22-g26) x5
    c: PointOnObject(g21,g27)
    c: PointOnObject(g22,g27)
    c: PointOnObject(g23,g27)
    c: PointOnObject(g24,g27)
    c: PointOnObject(g25,g27)
    c: PointOnObject(g26,g27)
    c: Coincident(g28,g29)
    c: Coincident(g29,g30)
    c: Coincident(g30,g31)
    c: Coincident(g31,g32)
    c: Coincident(g32,g33)
    c: Coincident(g33,g28)
    c: Equal(g28, g29-g33) x5
    c: PointOnObject(g28,g34)
    c: PointOnObject(g29,g34)
    c: PointOnObject(g30,g34)
    c: PointOnObject(g31,g34)
    c: PointOnObject(g32,g34)
    c: PointOnObject(g33,g34)
    c: Coincident(g35,g36)
    c: Coincident(g36,g37)
    c: Coincident(g37,g38)
    c: Coincident(g38,g35)
    c: Horizontal(g35)
    c: Horizontal(g37)
    c: Vertical(g36)
    c: Vertical(g38)
    c: Symmetric(g35,g36,g-1)
    c: DistanceX(g35,g35) = 20
    c: DistanceY(g38,g38) = 20
    c: Coincident(g20,g35)
    c: Coincident(g27,g37)
    c: Coincident(g34,g36)
    c: Coincident(g13,g35)
    c: Horizontal(g19)
    c: Horizontal(g12)
    c: Horizontal(g33)
    c: Horizontal(g26)
    c: DistanceY(g14,g15) = 5.7
    c: Equal(g13,g20)
    c: Equal(g20,g27)
    c: Equal(g27,g34)
FEATURE [PartDesign::Pocket] Pocket061
  AllowMultiFace = false
  BaseFeature = -> Chamfer002
  Length = 20
  Length2 = 100
  Profile = -> Sketch256
  Type = 0
FEATURE [Sketcher::SketchObject] Sketch257
  FullyConstrained = false
  MapMode = 5
  Placement = pos=(-15,0,0) rot=(0.57735,-0.57735,-0.57735;2.0944rad)
  Support = -> [Pocket061]
  sketch-geometry (5):
    g0: LineSegment StartX=-21 StartY=0 StartZ=0 EndX=-8 EndY=10 EndZ=0
    g1: LineSegment StartX=-8 StartY=10 StartZ=0 EndX=25.31 EndY=10 EndZ=0
    g2: LineSegment StartX=25.31 StartY=10 StartZ=0 EndX=25.31 EndY=-10 EndZ=0
    g3: LineSegment StartX=25.31 StartY=-10 StartZ=0 EndX=-21 EndY=-10 EndZ=0
    g4: LineSegment StartX=-21 StartY=-10 StartZ=0 EndX=-21 EndY=0 EndZ=0
  constraints (15):
    c: Coincident(g0,g1)
    c: Coincident(g1,g2)
    c: Coincident(g2,g3)
    c: Coincident(g3,g4)
    c: Coincident(g4,g0)
    c: PointOnObject(g0,g-1)
    c: DistanceX(g0,g-1) = 21
    c: Vertical(g4)
    c: Vertical(g2)
    c: Horizontal(g3)
    c: Horizontal(g1)
    c: DistanceX(g0,g0) = 13
    c: DistanceX(g3,g3) = 46.31
    c: DistanceY(g0,g0) = 10
    c: DistanceY(g2,g2) = 20
FEATURE [PartDesign::Pocket] Pocket062
  AllowMultiFace = false
  BaseFeature = -> Pocket061
  Length = 40
  Length2 = 100
  Profile = -> Sketch257
  Type = 0
FEATURE [Sketcher::SketchObject] Sketch258
  FullyConstrained = false
  MapMode = 5
  Placement = pos=(0,-16,0) rot=(1,0,0;1.5708rad)
  Support = -> [Pocket062]
  sketch-geometry (2):
    g0: Circle CenterX=-10 CenterY=6 CenterZ=0 NormalX=0 NormalY=0 NormalZ=1 AngleXU=0 Radius=1.76639
    g1: Circle CenterX=10 CenterY=6 CenterZ=0 NormalX=0 NormalY=0 NormalZ=1 AngleXU=0 Radius=1.65415
  constraints (3):
    c: DistanceX(g0,g1) = 20
    c: Symmetric(g0,g1,g-2)
    c: DistanceY(g-1,g0) = 6
FEATURE [PartDesign::Pocket] Pocket063
  AllowMultiFace = false
  BaseFeature = -> Pocket062
  Length = 40
  Length2 = 100
  Profile = -> Sketch258
  Type = 0
FEATURE [Sketcher::SketchObject] Sketch259
  FullyConstrained = false
  MapMode = 5
  Placement = pos=(0,-16,0) rot=(1,0,0;1.5708rad)
  Support = -> [Pocket063]
  sketch-geometry (14):
    g0: LineSegment StartX=-6.7091 StartY=6 StartZ=0 EndX=-8.35455 EndY=8.85 EndZ=0
    g1: LineSegment StartX=-8.35455 StartY=8.85 StartZ=0 EndX=-11.6454 EndY=8.85 EndZ=0
    g2: LineSegment StartX=-11.6454 StartY=8.85 StartZ=0 EndX=-13.2909 EndY=6 EndZ=0
    g3: LineSegment StartX=-13.2909 StartY=6 StartZ=0 EndX=-11.6454 EndY=3.15 EndZ=0
    g4: LineSegment StartX=-11.6454 StartY=3.15 StartZ=0 EndX=-8.35455 EndY=3.15 EndZ=0
    g5: LineSegment StartX=-8.35455 StartY=3.15 StartZ=0 EndX=-6.7091 EndY=6 EndZ=0
    g6: Circle CenterX=-10 CenterY=6 CenterZ=0 NormalX=0 NormalY=0 NormalZ=1 AngleXU=0 Radius=3.2909
    g7: LineSegment StartX=11.6454 StartY=8.85 StartZ=0 EndX=8.35455 EndY=8.85 EndZ=0
    g8: LineSegment StartX=8.35455 StartY=8.85 StartZ=0 EndX=6.7091 EndY=6 EndZ=0
    g9: LineSegment StartX=6.7091 StartY=6 StartZ=0 EndX=8.35455 EndY=3.15 EndZ=0
    g10: LineSegment StartX=8.35455 StartY=3.15 StartZ=0 EndX=11.6454 EndY=3.15 EndZ=0
    g11: LineSegment StartX=11.6454 StartY=3.15 StartZ=0 EndX=13.2909 EndY=6 EndZ=0
    g12: LineSegment StartX=13.2909 StartY=6 StartZ=0 EndX=11.6454 EndY=8.85 EndZ=0
    g13: Circle CenterX=10 CenterY=6 CenterZ=0 NormalX=0 NormalY=0 NormalZ=1 AngleXU=0 Radius=3.2909
  constraints (33):
    c: Coincident(g0,g1)
    c: Coincident(g1,g2)
    c: Coincident(g2,g3)
    c: Coincident(g3,g4)
    c: Coincident(g4,g5)
    c: Coincident(g5,g0)
    c: Equal(g0, g1-g5) x5
    c: PointOnObject(g0,g6)
    c: PointOnObject(g1,g6)
    c: PointOnObject(g2,g6)
    c: PointOnObject(g3,g6)
    c: PointOnObject(g4,g6)
    c: PointOnObject(g5,g6)
    c: Coincident(g7,g8)
    c: Coincident(g8,g9)
    c: Coincident(g9,g10)
    c: Coincident(g10,g11)
    c: Coincident(g11,g12)
    c: Coincident(g12,g7)
    c: Equal(g7, g8-g12) x5
    c: PointOnObject(g7,g13)
    c: PointOnObject(g8,g13)
    c: PointOnObject(g9,g13)
    c: PointOnObject(g10,g13)
    c: PointOnObject(g11,g13)
    c: PointOnObject(g12,g13)
    c: DistanceX(g6,g13) = 20
    c: Symmetric(g6,g13,g-2)
    c: DistanceY(g-1,g6) = 6
    c: Horizontal(g4)
    c: Horizontal(g10)
    c: DistanceY(g4,g0) = 5.7
    c: Equal(g6,g13)
FEATURE [PartDesign::Pocket] Pocket064
  AllowMultiFace = false
  BaseFeature = -> Pocket063
  Length = 32
  Length2 = 100
  Profile = -> Sketch259
  Type = 0
FEATURE [Sketcher::SketchObject] Sketch260
  FullyConstrained = false
  MapMode = 5
  Placement = pos=(0,-16,0) rot=(1,0,0;1.5708rad)
  Support = -> [Pocket064]
  sketch-geometry (6):
    g0: ArcOfCircle CenterX=-20 CenterY=15 CenterZ=0 NormalX=0 NormalY=0 NormalZ=1 AngleXU=0 Radius=5 StartAngle=1.5708 EndAngle=4.71239
    g1: ArcOfCircle CenterX=20 CenterY=15 CenterZ=0 NormalX=0 NormalY=0 NormalZ=1 AngleXU=0 Radius=5 StartAngle=4.71239 EndAngle=7.85398
    g2: LineSegment StartX=-20 StartY=10 StartZ=0 EndX=20 EndY=10 EndZ=0
    g3: LineSegment StartX=-20 StartY=20 StartZ=0 EndX=20 EndY=20 EndZ=0
    g4: Circle CenterX=-20 CenterY=15 CenterZ=0 NormalX=0 NormalY=0 NormalZ=1 AngleXU=0 Radius=2.25
    g5: Circle CenterX=20 CenterY=15 CenterZ=0 NormalX=0 NormalY=0 NormalZ=1 AngleXU=0 Radius=2.25
  constraints (13):
    c: Tangent(g0,g3) = 1.5708
    c: Tangent(g0,g2) = -1.5708
    c: Tangent(g2,g1) = -1.5708
    c: Tangent(g3,g1) = 1.5708
    c: Horizontal(g2)
    c: DistanceY(g-1,g1) = 10
    c: DistanceX(g0,g1) = 40
    c: Diameter(g1) = 10
    c: Symmetric(g0,g1,g-2)
    c: Coincident(g5,g1)
    c: Coincident(g4,g0)
    c: Diameter(g4) = 4.5
    c: Equal(g4,g5)
FEATURE [PartDesign::Pad] Pad178
  AllowMultiFace = false
  BaseFeature = -> Pocket064
  Direction = (1,1,1)
  Length = 10
  Length2 = 100
  Profile = -> Sketch260
  Reversed = true
  Type = 0
FEATURE [PartDesign::Body] Body153
  Group = -> [Sketch255,Pad177,Chamfer002,Sketch256,Pocket061,Sketch257,Pocket062,Sketch258,Pocket063,Sketch259,Pocket064,Sketch260,Pad178]
  Origin = -> Origin364
  Tip = -> Pad178
FEATURE [App::Part] Part023
  Group = -> [Body153]
  Origin = -> Origin363
  Placement = pos=(-100,-68,40) rot=(0,0,1;0rad)
FEATURE [Sketcher::SketchObject] Sketch261
  FullyConstrained = false
  MapMode = 5
  Placement = pos=(-5.01868,0,0) rot=(0.707107,0,-0.707107;3.14159rad)
  Support = -> [Pocket021]
  sketch-geometry (14):
    g0: LineSegment StartX=-15.3638 StartY=3.7 StartZ=0 EndX=-19.6362 EndY=3.7 EndZ=0
    g1: LineSegment StartX=-19.6362 StartY=3.7 StartZ=0 EndX=-21.7724 EndY=9e-16 EndZ=0
    g2: LineSegment StartX=-21.7724 StartY=9e-16 StartZ=0 EndX=-19.6362 EndY=-3.7 EndZ=0
    g3: LineSegment StartX=-19.6362 StartY=-3.7 StartZ=0 EndX=-15.3638 EndY=-3.7 EndZ=0
    g4: LineSegment StartX=-15.3638 StartY=-3.7 StartZ=0 EndX=-13.2276 EndY=-9e-16 EndZ=0
    g5: LineSegment StartX=-13.2276 StartY=-9e-16 StartZ=0 EndX=-15.3638 EndY=3.7 EndZ=0
    g6: Circle CenterX=-17.5 CenterY=0 CenterZ=0 NormalX=0 NormalY=0 NormalZ=1 AngleXU=0 Radius=4.27239
    g7: LineSegment StartX=9.6362 StartY=3.7 StartZ=0 EndX=5.3638 EndY=3.7 EndZ=0
    g8: LineSegment StartX=5.3638 StartY=3.7 StartZ=0 EndX=3.22761 EndY=-4e-16 EndZ=0
    g9: LineSegment StartX=3.22761 StartY=-4e-16 StartZ=0 EndX=5.3638 EndY=-3.7 EndZ=0
    g10: LineSegment StartX=5.3638 StartY=-3.7 StartZ=0 EndX=9.6362 EndY=-3.7 EndZ=0
    g11: LineSegment StartX=9.6362 StartY=-3.7 StartZ=0 EndX=11.7724 EndY=-4e-16 EndZ=0
    g12: LineSegment StartX=11.7724 StartY=-4e-16 StartZ=0 EndX=9.6362 EndY=3.7 EndZ=0
    g13: Circle CenterX=7.5 CenterY=0 CenterZ=0 NormalX=0 NormalY=0 NormalZ=1 AngleXU=0 Radius=4.27239
  constraints (34):
    c: Coincident(g0,g1)
    c: Coincident(g1,g2)
    c: Coincident(g2,g3)
    c: Coincident(g3,g4)
    c: Coincident(g4,g5)
    c: Coincident(g5,g0)
    c: Equal(g0, g1-g5) x5
    c: PointOnObject(g0,g6)
    c: PointOnObject(g1,g6)
    c: PointOnObject(g2,g6)
    c: PointOnObject(g3,g6)
    c: PointOnObject(g4,g6)
    c: PointOnObject(g5,g6)
    c: Coincident(g7,g8)
    c: Coincident(g8,g9)
    c: Coincident(g9,g10)
    c: Coincident(g10,g11)
    c: Coincident(g11,g12)
    c: Coincident(g12,g7)
    c: Equal(g7, g8-g12) x5
    c: PointOnObject(g7,g13)
    c: PointOnObject(g8,g13)
    c: PointOnObject(g9,g13)
    c: PointOnObject(g10,g13)
    c: PointOnObject(g11,g13)
    c: PointOnObject(g12,g13)
    c: PointOnObject(g13,g-1)
    c: PointOnObject(g6,g-1)
    c: DistanceX(g6,g13) = 25
    c: DistanceX(g-1,g13) = 7.5
    c: Horizontal(g3)
    c: Horizontal(g10)
    c: DistanceY(g9,g7) = 7.4
    c: Equal(g6,g13)
FEATURE [PartDesign::Pocket] Pocket065
  AllowMultiFace = false
  BaseFeature = -> Pocket021
  Length = 3.5
  Length2 = 100
  Placement = pos=(0,0,0) rot=(1,0,0;1.5708rad)
  Profile = -> Sketch261
  Type = 0
FEATURE [Sketcher::SketchObject] Sketch262
  FullyConstrained = false
  MapMode = 5
  Placement = pos=(4.98132,0,0) rot=(0.707107,0,0.707107;3.14159rad)
  Support = -> [Pocket065]
  sketch-geometry (32):
    g0: LineSegment StartX=-25 StartY=10 StartZ=0 EndX=35 EndY=10 EndZ=0
    g1: LineSegment StartX=35 StartY=10 StartZ=0 EndX=35 EndY=-10 EndZ=0
    g2: LineSegment StartX=35 StartY=-10 StartZ=0 EndX=-25 EndY=-10 EndZ=0
    g3: LineSegment StartX=-25 StartY=-10 StartZ=0 EndX=-25 EndY=10 EndZ=0
    g4: LineSegment StartX=36.6743 StartY=12.9 StartZ=0 EndX=33.3257 EndY=12.9 EndZ=0
    g5: LineSegment StartX=33.3257 StartY=12.9 StartZ=0 EndX=31.6514 EndY=10 EndZ=0
    g6: LineSegment StartX=31.6514 StartY=10 StartZ=0 EndX=33.3257 EndY=7.1 EndZ=0
    g7: LineSegment StartX=33.3257 StartY=7.1 StartZ=0 EndX=36.6743 EndY=7.1 EndZ=0
    g8: LineSegment StartX=36.6743 StartY=7.1 StartZ=0 EndX=38.3486 EndY=10 EndZ=0
    g9: LineSegment StartX=38.3486 StartY=10 StartZ=0 EndX=36.6743 EndY=12.9 EndZ=0
    g10: Circle CenterX=35 CenterY=10 CenterZ=0 NormalX=0 NormalY=0 NormalZ=1 AngleXU=0 Radius=3.34863
    g11: LineSegment StartX=36.6743 StartY=-7.1 StartZ=0 EndX=33.3257 EndY=-7.1 EndZ=0
    g12: LineSegment StartX=33.3257 StartY=-7.1 StartZ=0 EndX=31.6514 EndY=-10 EndZ=0
    g13: LineSegment StartX=31.6514 StartY=-10 StartZ=0 EndX=33.3257 EndY=-12.9 EndZ=0
    g14: LineSegment StartX=33.3257 StartY=-12.9 StartZ=0 EndX=36.6743 EndY=-12.9 EndZ=0
    g15: LineSegment StartX=36.6743 StartY=-12.9 StartZ=0 EndX=38.3486 EndY=-10 EndZ=0
    g16: LineSegment StartX=38.3486 StartY=-10 StartZ=0 EndX=36.6743 EndY=-7.1 EndZ=0
    g17: Circle CenterX=35 CenterY=-10 CenterZ=0 NormalX=0 NormalY=0 NormalZ=1 AngleXU=0 Radius=3.34863
    g18: LineSegment StartX=-23.3257 StartY=-7.1 StartZ=0 EndX=-26.6743 EndY=-7.1 EndZ=0
    g19: LineSegment StartX=-26.6743 StartY=-7.1 StartZ=0 EndX=-28.3486 EndY=-10 EndZ=0
    g20: LineSegment StartX=-28.3486 StartY=-10 StartZ=0 EndX=-26.6743 EndY=-12.9 EndZ=0
    g21: LineSegment StartX=-26.6743 StartY=-12.9 StartZ=0 EndX=-23.3257 EndY=-12.9 EndZ=0
    g22: LineSegment StartX=-23.3257 StartY=-12.9 StartZ=0 EndX=-21.6514 EndY=-10 EndZ=0
    g23: LineSegment StartX=-21.6514 StartY=-10 StartZ=0 EndX=-23.3257 EndY=-7.1 EndZ=0
    g24: Circle CenterX=-25 CenterY=-10 CenterZ=0 NormalX=0 NormalY=0 NormalZ=1 AngleXU=0 Radius=3.34863
    g25: LineSegment StartX=-21.6514 StartY=10 StartZ=0 EndX=-23.3257 EndY=12.9 EndZ=0
    g26: LineSegment StartX=-23.3257 StartY=12.9 StartZ=0 EndX=-26.6743 EndY=12.9 EndZ=0
    g27: LineSegment StartX=-26.6743 StartY=12.9 StartZ=0 EndX=-28.3486 EndY=10 EndZ=0
    g28: LineSegment StartX=-28.3486 StartY=10 StartZ=0 EndX=-26.6743 EndY=7.1 EndZ=0
    g29: LineSegment StartX=-26.6743 StartY=7.1 StartZ=0 EndX=-23.3257 EndY=7.1 EndZ=0
    g30: LineSegment StartX=-23.3257 StartY=7.1 StartZ=0 EndX=-21.6514 EndY=10 EndZ=0
    g31: Circle CenterX=-25 CenterY=10 CenterZ=0 NormalX=0 NormalY=0 NormalZ=1 AngleXU=0 Radius=3.34863
  constraints (75):
    c: Coincident(g0,g1)
    c: Coincident(g1,g2)
    c: Coincident(g2,g3)
    c: Coincident(g3,g0)
    c: Horizontal(g0)
    c: Horizontal(g2)
    c: Vertical(g3)
    c: Symmetric(g0,g1,g-1)
    c: DistanceX(g0,g0) = 60
    c: DistanceY(g1,g1) = 20
    c: DistanceX(g0,g-1) = 25
    c: Coincident(g4,g5)
    c: Coincident(g5,g6)
    c: Coincident(g6,g7)
    c: Coincident(g7,g8)
    c: Coincident(g8,g9)
    c: Coincident(g9,g4)
    c: Equal(g4, g5-g9) x5
    c: PointOnObject(g4,g10)
    c: PointOnObject(g5,g10)
    c: PointOnObject(g6,g10)
    c: PointOnObject(g7,g10)
    c: PointOnObject(g8,g10)
    c: PointOnObject(g9,g10)
    c: Coincident(g11,g12)
    c: Coincident(g12,g13)
    c: Coincident(g13,g14)
    c: Coincident(g14,g15)
    c: Coincident(g15,g16)
    c: Coincident(g16,g11)
    c: Equal(g11, g12-g16) x5
    c: PointOnObject(g11,g17)
    c: PointOnObject(g12,g17)
    c: PointOnObject(g13,g17)
    c: PointOnObject(g14,g17)
    c: PointOnObject(g15,g17)
    c: PointOnObject(g16,g17)
    c: Coincident(g18,g19)
    c: Coincident(g19,g20)
    c: Coincident(g20,g21)
    c: Coincident(g21,g22)
    c: Coincident(g22,g23)
    c: Coincident(g23,g18)
    c: Equal(g18, g19-g23) x5
    c: PointOnObject(g18,g24)
    c: PointOnObject(g19,g24)
    c: PointOnObject(g20,g24)
    c: PointOnObject(g21,g24)
    c: PointOnObject(g22,g24)
    c: PointOnObject(g23,g24)
    c: Coincident(g25,g26)
    c: Coincident(g26,g27)
    c: Coincident(g27,g28)
    c: Coincident(g28,g29)
    c: Coincident(g29,g30)
    c: Coincident(g30,g25)
    c: Equal(g25, g26-g30) x5
    c: PointOnObject(g25,g31)
    c: PointOnObject(g26,g31)
    c: PointOnObject(g27,g31)
    c: PointOnObject(g28,g31)
    c: PointOnObject(g29,g31)
    c: PointOnObject(g30,g31)
    c: Coincident(g31,g0)
    c: Horizontal(g29)
    c: Horizontal(g21)
    c: Coincident(g24,g2)
    c: Coincident(g17,g1)
    c: Horizontal(g14)
    c: Coincident(g10,g0)
    c: Horizontal(g7)
    c: Equal(g31,g24)
    c: Equal(g24,g17)
    c: Equal(g17,g10)
    c: DistanceY(g29,g25) = 5.8
FEATURE [PartDesign::Pocket] Pocket066
  AllowMultiFace = false
  BaseFeature = -> Pocket065
  Length = 4
  Length2 = 100
  Placement = pos=(0,0,0) rot=(1,0,0;1.5708rad)
  Profile = -> Sketch262
  Type = 0
FEATURE [PartDesign::Body] Body043  label="Mounting_Point"
  Group = -> [Sketch086,Pad058,Sketch087,Pocket021,Sketch261,Pocket065,Sketch262,Pocket066]
  Origin = -> Origin058
  Placement = pos=(-35,0,90) rot=(0,0,1;0rad)
  Tip = -> Pocket066
FEATURE [Sketcher::SketchObject] Sketch263
  FullyConstrained = false
  MapMode = 5
  Support = -> [XY_Plane365]
  sketch-geometry (2):
    g0: Circle CenterX=0 CenterY=0 CenterZ=0 NormalX=0 NormalY=0 NormalZ=1 AngleXU=0 Radius=5
    g1: Circle CenterX=0 CenterY=0 CenterZ=0 NormalX=0 NormalY=0 NormalZ=1 AngleXU=0 Radius=2.25
  constraints (4):
    c: Coincident(g1,g0)
    c: Coincident(g1,g-1)
    c: Diameter(g1) = 4.5
    c: Diameter(g0) = 10
FEATURE [PartDesign::Pad] Pad179
  AllowMultiFace = false
  Direction = (1,1,1)
  Length = 30
  Length2 = 100
  Profile = -> Sketch263
  Type = 0
FEATURE [PartDesign::Body] Body154  label="Board Spacer"
  Group = -> [Sketch263,Pad179]
  Origin = -> Origin365
  Placement = pos=(65,15,45) rot=(1,0,0;1.5708rad)
  Tip = -> Pad179
FEATURE [PartDesign::FeatureBase] Clone022
  BaseFeature = -> Body154
  Placement = pos=(65,15,45) rot=(1,0,0;1.5708rad)
FEATURE [PartDesign::Body] Body155
  BaseFeature = -> Body154
  Group = -> [Clone022]
  Origin = -> Origin366
  Placement = pos=(0,0,60) rot=(0,0,1;0rad)
  Tip = -> Clone022
FEATURE [Sketcher::SketchObject] Sketch264
  FullyConstrained = false
  MapMode = 5
  Support = -> [XY_Plane367]
  sketch-geometry (2):
    g0: Circle CenterX=0 CenterY=0 CenterZ=0 NormalX=0 NormalY=0 NormalZ=1 AngleXU=0 Radius=2.25
    g1: Circle CenterX=0 CenterY=0 CenterZ=0 NormalX=0 NormalY=0 NormalZ=1 AngleXU=0 Radius=5
  constraints (4):
    c: Coincident(g1,g0)
    c: Coincident(g1,g-1)
    c: Diameter(g0) = 4.5
    c: Diameter(g1) = 10
FEATURE [PartDesign::Pad] Pad180
  AllowMultiFace = false
  Direction = (1,1,1)
  Length = 20
  Length2 = 100
  Midplane = true
  Profile = -> Sketch264
  Type = 0
FEATURE [PartDesign::Body] Body156  label="BatterySpace"
  Group = -> [Sketch264,Pad180]
  Origin = -> Origin367
  Placement = pos=(65,-27,45) rot=(1,0,0;1.5708rad)
  Tip = -> Pad180
FEATURE [PartDesign::FeatureBase] Clone023
  BaseFeature = -> Body156
  Placement = pos=(65,-27,45) rot=(1,0,0;1.5708rad)
FEATURE [PartDesign::Body] Body157  label="BatterySpacer2"
  BaseFeature = -> Body156
  Group = -> [Clone023]
  Origin = -> Origin368
  Placement = pos=(0,0,60) rot=(0,0,1;0rad)
  Tip = -> Clone023
FEATURE [Sketcher::SketchObject] Sketch265
  FullyConstrained = true
  MapMode = 3
  Placement = pos=(0,0,0) rot=(1,0,0;1.5708rad)
  Support = -> [Sketch026]
  sketch-geometry (8):
    g0: LineSegment StartX=-150 StartY=358 StartZ=0 EndX=150 EndY=358 EndZ=0
    g1: LineSegment StartX=150 StartY=358 StartZ=0 EndX=150 EndY=-42 EndZ=0
    g2: LineSegment StartX=150 StartY=-42 StartZ=0 EndX=-150 EndY=-42 EndZ=0
    g3: LineSegment StartX=-150 StartY=-42 StartZ=0 EndX=-150 EndY=358 EndZ=0
    g4: LineSegment StartX=-250 StartY=458 StartZ=0 EndX=150 EndY=458 EndZ=0
    g5: LineSegment StartX=150 StartY=458 StartZ=0 EndX=150 EndY=-42 EndZ=0
    g6: LineSegment StartX=150 StartY=-42 StartZ=0 EndX=-250 EndY=-42 EndZ=0
    g7: LineSegment StartX=-250 StartY=-42 StartZ=0 EndX=-250 EndY=458 EndZ=0
  constraints (22):
    c: Coincident(g0,g1)
    c: Coincident(g1,g2)
    c: Coincident(g2,g3)
    c: Coincident(g3,g0)
    c: Horizontal(g0)
    c: Vertical(g1)
    c: Vertical(g3)
    c: DistanceX(g2,g2) = 300
    c: Symmetric(g2,g1,g-2)
    c: DistanceY(g1,g1) = 400
    c: DistanceY(g2,g-1) = 42
    c: Coincident(g4,g5)
    c: Coincident(g5,g6)
    c: Coincident(g6,g7)
    c: Coincident(g7,g4)
    c: Horizontal(g4)
    c: Horizontal(g6)
    c: Vertical(g5)
    c: Vertical(g7)
    c: Coincident(g5,g1)
    c: DistanceX(g4,g4) = 400
    c: DistanceY(g7,g7) = 500
FEATURE [Mesh::Feature] Hungry_Cattle_trough__with_fancy_sides_  label="Hungry Cattle trough (with fancy sides)"
  Placement = pos=(1061,74,-44) rot=(0,0,1;0rad)
FEATURE [Sketcher::SketchObject] Sketch266
  FullyConstrained = true
  MapMode = 5
  Support = -> [XY_Plane370]
  sketch-geometry (25):
    g0: LineSegment StartX=-31 StartY=-42 StartZ=0 EndX=10 EndY=-42 EndZ=0
    g1: LineSegment StartX=10 StartY=-42 StartZ=0 EndX=10 EndY=-64 EndZ=0
    g2: LineSegment StartX=10 StartY=-64 StartZ=0 EndX=22 EndY=-64 EndZ=0
    g3: LineSegment StartX=22 StartY=-64 StartZ=0 EndX=52 EndY=-15 EndZ=0
    g4: LineSegment StartX=52 StartY=-15 StartZ=0 EndX=52 EndY=15 EndZ=0
    g5: LineSegment StartX=52 StartY=15 StartZ=0 EndX=21 EndY=30 EndZ=0
    g6: LineSegment StartX=21 StartY=30 StartZ=0 EndX=-24 EndY=30 EndZ=0
    g7: LineSegment StartX=-24 StartY=30 StartZ=0 EndX=-39 EndY=15 EndZ=0
    g8: LineSegment StartX=-39 StartY=15 StartZ=0 EndX=-39 EndY=-64 EndZ=0
    g9: LineSegment StartX=-39 StartY=-64 StartZ=0 EndX=-31 EndY=-64 EndZ=0
    g10: LineSegment StartX=-31 StartY=-64 StartZ=0 EndX=-31 EndY=-42 EndZ=0
    g11: LineSegment StartX=-35 StartY=-48 StartZ=0 EndX=14 EndY=-48 EndZ=0
    g12: LineSegment StartX=14 StartY=-48 StartZ=0 EndX=14 EndY=-58 EndZ=0
    g13: LineSegment StartX=14 StartY=-58 StartZ=0 EndX=-35 EndY=-58 EndZ=0
    g14: LineSegment StartX=-35 StartY=-58 StartZ=0 EndX=-35 EndY=-48 EndZ=0
    g15: Circle CenterX=14 CenterY=-48 CenterZ=0 NormalX=0 NormalY=0 NormalZ=1 AngleXU=0 Radius=1.5
    g16: Circle CenterX=14 CenterY=-58 CenterZ=0 NormalX=0 NormalY=0 NormalZ=1 AngleXU=0 Radius=1.5
    g17: Circle CenterX=-35 CenterY=-58 CenterZ=0 NormalX=0 NormalY=0 NormalZ=1 AngleXU=0 Radius=1.5
    g18: Circle CenterX=-35 CenterY=-48 CenterZ=0 NormalX=0 NormalY=0 NormalZ=1 AngleXU=0 Radius=1.5
    g19: LineSegment StartX=-35 StartY=-48 StartZ=0 EndX=-31 EndY=-42 EndZ=0
    g20: LineSegment StartX=-35 StartY=-58 StartZ=0 EndX=-31 EndY=-64 EndZ=0
    g21: LineSegment StartX=10 StartY=-64 StartZ=0 EndX=14 EndY=-58 EndZ=0
    g22: LineSegment StartX=10 StartY=-42 StartZ=0 EndX=14 EndY=-48 EndZ=0
    g23: Circle CenterX=41 CenterY=10 CenterZ=0 NormalX=0 NormalY=0 NormalZ=1 AngleXU=0 Radius=2.25
    g24: Circle CenterX=41 CenterY=-10 CenterZ=0 NormalX=0 NormalY=0 NormalZ=1 AngleXU=0 Radius=2.25
  constraints (65):
    c: Horizontal(g0)
    c: Coincident(g0,g1)
    c: Vertical(g1)
    c: Coincident(g1,g2)
    c: Horizontal(g2)
    c: Coincident(g2,g3)
    c: Coincident(g3,g4)
    c: Coincident(g4,g5)
    c: Coincident(g5,g6)
    c: Horizontal(g6)
    c: Coincident(g6,g7)
    c: Coincident(g7,g8)
    c: Vertical(g8)
    c: Coincident(g8,g9)
    c: Horizontal(g9)
    c: Coincident(g9,g10)
    c: Coincident(g10,g0)
    c: Vertical(g10)
    c: Coincident(g11,g12)
    c: Coincident(g12,g13)
    c: Coincident(g13,g14)
    c: Coincident(g14,g11)
    c: Horizontal(g11)
    c: Horizontal(g13)
    c: Vertical(g12)
    c: Vertical(g14)
    c: DistanceX(g11,g11) = 49
    c: DistanceY(g12,g12) = 10
    c: Coincident(g18,g11)
    c: Coincident(g17,g13)
    c: Coincident(g16,g12)
    c: Coincident(g15,g11)
    c: Diameter(g15) = 3
    c: Equal(g15,g16)
    c: Equal(g15,g18)
    c: Equal(g15,g17)
    c: DistanceX(g0,g0) = 41
    c: Coincident(g19,g18)
    c: Coincident(g19,g0)
    c: Coincident(g20,g17)
    c: Coincident(g20,g9)
    c: Coincident(g21,g1)
    c: Coincident(g21,g16)
    c: Coincident(g22,g0)
    c: Coincident(g22,g15)
    c: Equal(g21,g22)
    c: Equal(g22,g19)
    c: Equal(g19,g20)
    c: DistanceY(g10,g10) = 22
    c: DistanceX(g9,g9) = 8
    c: DistanceY(g4,g4) = 30
    c: Symmetric(g3,g4,g-1)
    c: DistanceY(g0,g-1) = 42
    c: DistanceX(g2,g2) = 12
    c: DistanceX(g6,g6) = 45
    c: DistanceY(g-1,g5) = 30
    c: DistanceX(g7,g6) = 15
    c: DistanceY(g7,g6) = 15
    c: DistanceX(g-1,g16) = 14
    c: DistanceX(g-1,g3) = 52
    c: Symmetric(g23,g24,g-1)
    c: DistanceY(g24,g23) = 20
    c: DistanceX(g-1,g23) = 41
    c: Diameter(g24) = 4.5
    c: Equal(g24,g23)
FEATURE [PartDesign::Pad] Pad181
  Direction = (1,1,1)
  Length = 5
  Length2 = 100
  Profile = -> Sketch266
  Type = 0
FEATURE [Sketcher::SketchObject] Sketch267
  FullyConstrained = false
  MapMode = 5
  Support = -> [XY_Plane371]
  sketch-geometry (4):
    g0: LineSegment StartX=-20.35 StartY=10.075 StartZ=0 EndX=20.35 EndY=10.075 EndZ=0
    g1: LineSegment StartX=20.35 StartY=10.075 StartZ=0 EndX=20.35 EndY=-10.075 EndZ=0
    g2: LineSegment StartX=20.35 StartY=-10.075 StartZ=0 EndX=-20.35 EndY=-10.075 EndZ=0
    g3: LineSegment StartX=-20.35 StartY=-10.075 StartZ=0 EndX=-20.35 EndY=10.075 EndZ=0
  constraints (11):
    c: Coincident(g0,g1)
    c: Coincident(g1,g2)
    c: Coincident(g2,g3)
    c: Coincident(g3,g0)
    c: Horizontal(g0)
    c: Horizontal(g2)
    c: Vertical(g1)
    c: Vertical(g3)
    c: Symmetric(g0,g1,g-1)
    c: DistanceX(g0,g0) = 40.7
    c: DistanceY(g3,g3) = 20.15
FEATURE [PartDesign::Pad] Pad182
  AllowMultiFace = false
  Direction = (1,1,1)
  Length = 29
  Length2 = 100
  Profile = -> Sketch267
  Reversed = true
  Type = 0
FEATURE [Sketcher::SketchObject] Sketch268
  FullyConstrained = false
  MapMode = 5
  Support = -> [Pad182]
  sketch-geometry (16):
    g0: LineSegment StartX=-27.2 StartY=10.075 StartZ=0 EndX=27.2 EndY=10.075 EndZ=0
    g1: LineSegment StartX=27.2 StartY=10.075 StartZ=0 EndX=27.2 EndY=6 EndZ=0
    g2: LineSegment StartX=-27.2 StartY=10.075 StartZ=0 EndX=-27.2 EndY=6 EndZ=0
    g3: LineSegment StartX=-27.2 StartY=4 StartZ=0 EndX=-27.2 EndY=-4 EndZ=0
    g4: LineSegment StartX=27.2 StartY=4 StartZ=0 EndX=27.2 EndY=-4 EndZ=0
    g5: LineSegment StartX=27.2 StartY=-6 StartZ=0 EndX=27.2 EndY=-10.075 EndZ=0
    g6: LineSegment StartX=27.2 StartY=-10.075 StartZ=0 EndX=-27.2 EndY=-10.075 EndZ=0
    g7: LineSegment StartX=-27.2 StartY=-10.075 StartZ=0 EndX=-27.2 EndY=-6 EndZ=0
    g8: ArcOfCircle CenterX=-24.5 CenterY=5 CenterZ=0 NormalX=0 NormalY=0 NormalZ=1 AngleXU=0 Radius=2.87924 StartAngle=3.4963 EndAngle=9.07007
    g9: ArcOfCircle CenterX=-24.5 CenterY=-5 CenterZ=0 NormalX=0 NormalY=0 NormalZ=1 AngleXU=0 Radius=2.87924 StartAngle=3.4963 EndAngle=9.07007
    g10: ArcOfCircle CenterX=24.5 CenterY=5 CenterZ=0 NormalX=0 NormalY=0 NormalZ=1 AngleXU=0 Radius=2.87924 StartAngle=0.354706 EndAngle=5.92848
    g11: ArcOfCircle CenterX=24.5 CenterY=-5 CenterZ=0 NormalX=0 NormalY=0 NormalZ=1 AngleXU=0 Radius=2.87924 StartAngle=0.354706 EndAngle=5.92848
    g12: LineSegment StartX=-24.5 StartY=5 StartZ=0 EndX=24.5 EndY=5 EndZ=0
    g13: LineSegment StartX=24.5 StartY=5 StartZ=0 EndX=24.5 EndY=-5 EndZ=0
    g14: LineSegment StartX=24.5 StartY=-5 StartZ=0 EndX=-24.5 EndY=-5 EndZ=0
    g15: LineSegment StartX=-24.5 StartY=-5 StartZ=0 EndX=-24.5 EndY=5 EndZ=0
  constraints (46):
    c: Coincident(g0,g1)
    c: Coincident(g5,g6)
    c: Coincident(g6,g7)
    c: Horizontal(g0)
    c: Horizontal(g6)
    c: Vertical(g4)
    c: Vertical(g1)
    c: Vertical(g5)
    c: Vertical(g7)
    c: Vertical(g3)
    c: Vertical(g2)
    c: Vertical(g7,g3)
    c: Vertical(g3,g2)
    c: Coincident(g2,g0)
    c: Vertical(g1,g4)
    c: Vertical(g4,g5)
    c: DistanceX(g0,g0) = 54.4
    c: Coincident(g10,g1)
    c: Coincident(g10,g4)
    c: Coincident(g11,g4)
    c: Coincident(g11,g5)
    c: Coincident(g9,g7)
    c: Coincident(g9,g3)
    c: Coincident(g8,g3)
    c: Coincident(g8,g2)
    c: Symmetric(g0,g5,g-1)
    c: DistanceY(g6,g0) = 20.15
    c: Equal(g9,g8)
    c: Equal(g8,g10)
    c: Equal(g10,g11)
    c: Coincident(g12,g13)
    c: Coincident(g13,g14)
    c: Coincident(g14,g15)
    c: Coincident(g15,g12)
    c: Horizontal(g12)
    c: Horizontal(g14)
    c: Vertical(g13)
    c: Vertical(g15)
    c: Symmetric(g12,g13,g-1)
    c: DistanceX(g12,g12) = 49
    c: Coincident(g8,g12)
    c: Coincident(g9,g14)
    c: Coincident(g11,g13)
    c: Coincident(g10,g12)
    c: DistanceY(g15,g15) = 10
    c: DistanceY(g3,g2) = 2
FEATURE [PartDesign::Pad] Pad183
  AllowMultiFace = false
  BaseFeature = -> Pad182
  Direction = (1,1,1)
  Length = 2.55
  Length2 = 100
  Profile = -> Sketch268
  Type = 0
FEATURE [Sketcher::SketchObject] Sketch269
  FullyConstrained = false
  MapMode = 5
  Placement = pos=(0,0,2.55) rot=(0,0,1;0rad)
  Support = -> [Pad183]
  sketch-geometry (4):
    g0: LineSegment StartX=-20.35 StartY=10.075 StartZ=0 EndX=20.35 EndY=10.075 EndZ=0
    g1: LineSegment StartX=20.35 StartY=10.075 StartZ=0 EndX=20.35 EndY=-10.075 EndZ=0
    g2: LineSegment StartX=20.35 StartY=-10.075 StartZ=0 EndX=-20.35 EndY=-10.075 EndZ=0
    g3: LineSegment StartX=-20.35 StartY=-10.075 StartZ=0 EndX=-20.35 EndY=10.075 EndZ=0
  constraints (11):
    c: Coincident(g0,g1)
    c: Coincident(g1,g2)
    c: Coincident(g2,g3)
    c: Coincident(g3,g0)
    c: Horizontal(g0)
    c: Horizontal(g2)
    c: Vertical(g1)
    c: Vertical(g3)
    c: Symmetric(g1,g0,g-1)
    c: DistanceX(g0,g0) = 40.7
    c: DistanceY(g3,g3) = 20.15
FEATURE [PartDesign::Pad] Pad184
  AllowMultiFace = false
  BaseFeature = -> Pad183
  Direction = (1,1,1)
  Length = 5.5
  Length2 = 100
  Profile = -> Sketch269
  Type = 0
FEATURE [Sketcher::SketchObject] Sketch270
  FullyConstrained = false
  MapMode = 5
  Placement = pos=(0,0,8.05) rot=(0,0,1;0rad)
  Support = -> [Pad184]
  sketch-geometry (7):
    g0: ArcOfCircle CenterX=10.35 CenterY=0 CenterZ=0 NormalX=0 NormalY=0 NormalZ=1 AngleXU=0 Radius=10 StartAngle=4.26136 EndAngle=8.30501
    g1: LineSegment StartX=5.9911 StartY=9 StartZ=0 EndX=-14.85 EndY=9 EndZ=0
    g2: LineSegment StartX=-14.85 StartY=9 StartZ=0 EndX=-14.85 EndY=5 EndZ=0
    g3: LineSegment StartX=-14.85 StartY=-5 StartZ=0 EndX=-14.85 EndY=-9 EndZ=0
    g4: LineSegment StartX=-14.85 StartY=-9 StartZ=0 EndX=5.9911 EndY=-9 EndZ=0
    g5: ArcOfCircle CenterX=-11.1 CenterY=0 CenterZ=0 NormalX=0 NormalY=0 NormalZ=1 AngleXU=0 Radius=6.25 StartAngle=3.14159 EndAngle=4.06889
    g6: ArcOfCircle CenterX=-11.1 CenterY=0 CenterZ=0 NormalX=0 NormalY=0 NormalZ=1 AngleXU=0 Radius=6.25 StartAngle=2.2143 EndAngle=3.14159
  constraints (23):
    c: PointOnObject(g0,g-1)
    c: Diameter(g0) = 20
    c: DistanceX(g-1,g0) = 10.35
    c: Coincident(g1,g2)
    c: Coincident(g3,g4)
    c: Coincident(g1,g0)
    c: Coincident(g4,g0)
    c: Horizontal(g4)
    c: Horizontal(g1)
    c: Vertical(g2)
    c: Vertical(g3)
    c: DistanceX(g3,g-1) = 14.85
    c: Equal(g1,g4)
    c: Vertical(g3,g2)
    c: DistanceY(g3,g1) = 18
    c: Coincident(g6,g2)
    c: Coincident(g5,g3)
    c: Coincident(g6,g5)
    c: Tangent(g6,g5) = -1.5708
    c: PointOnObject(g5,g-1)
    c: PointOnObject(g5,g-1)
    c: DistanceX(g5,g-1) = 17.35
    c: DistanceY(g3,g2) = 10
FEATURE [PartDesign::Pad] Pad185
  AllowMultiFace = false
  BaseFeature = -> Pad184
  Direction = (1,1,1)
  Length = 2
  Length2 = 100
  Profile = -> Sketch270
  Type = 0
FEATURE [Sketcher::SketchObject] Sketch271
  FullyConstrained = false
  MapMode = 5
  Placement = pos=(0,0,10.05) rot=(0,0,1;0rad)
  Support = -> [Pad185]
  sketch-geometry (1):
    g0: Circle CenterX=10.35 CenterY=0 CenterZ=0 NormalX=0 NormalY=0 NormalZ=1 AngleXU=0 Radius=6.5
  constraints (3):
    c: PointOnObject(g0,g-1)
    c: DistanceX(g-1,g0) = 10.35
    c: Diameter(g0) = 13
FEATURE [PartDesign::Pad] Pad186
  AllowMultiFace = false
  BaseFeature = -> Pad185
  Direction = (1,1,1)
  Length = 1.3
  Length2 = 100
  Profile = -> Sketch271
  Type = 0
FEATURE [Sketcher::SketchObject] Sketch272
  FullyConstrained = false
  MapMode = 5
  Placement = pos=(0,0,11.35) rot=(0,0,1;0rad)
  Support = -> [Pad186]
  sketch-geometry (1):
    g0: Circle CenterX=10.35 CenterY=0 CenterZ=0 NormalX=0 NormalY=0 NormalZ=1 AngleXU=0 Radius=5.5
  constraints (3):
    c: PointOnObject(g0,g-1)
    c: Diameter(g0) = 11
    c: DistanceX(g-1,g0) = 10.35
FEATURE [PartDesign::Pad] Pad187
  AllowMultiFace = false
  BaseFeature = -> Pad186
  Direction = (1,1,1)
  Length = 0.7
  Length2 = 100
  Profile = -> Sketch272
  Type = 0
FEATURE [Sketcher::SketchObject] Sketch273
  FullyConstrained = false
  MapMode = 5
  Placement = pos=(0,0,12.05) rot=(0,0,1;0rad)
  Support = -> [Pad187]
  sketch-geometry (1):
    g0: Circle CenterX=10.35 CenterY=0 CenterZ=0 NormalX=0 NormalY=0 NormalZ=1 AngleXU=0 Radius=3
  constraints (3):
    c: PointOnObject(g0,g-1)
    c: DistanceX(g-1,g0) = 10.35
    c: Diameter(g0) = 6
FEATURE [PartDesign::Pad] Pad188
  AllowMultiFace = false
  BaseFeature = -> Pad187
  Direction = (1,1,1)
  Length = 3.5
  Length2 = 100
  Profile = -> Sketch273
  Type = 0
FEATURE [PartDesign::Body] Body159  label="MG999"
  Group = -> [Sketch267,Pad182,Sketch268,Pad183,Sketch269,Pad184,Sketch270,Pad185,Sketch271,Pad186,Sketch272,Pad187,Sketch273,Pad188]
  Origin = -> Origin371
  Placement = pos=(-17.5,-53,42.5) rot=(0,1,0;3.14159rad)
  Tip = -> Pad188
FEATURE [Sketcher::SketchObject] Sketch275
  FullyConstrained = true
  MapMode = 5
  Placement = pos=(0,0,0) rot=(1,0,0;1.5708rad)
  Support = -> [XZ_Plane371]
  sketch-geometry (12):
    g0: LineSegment StartX=-12 StartY=0 StartZ=0 EndX=-12 EndY=15 EndZ=0
    g1: LineSegment StartX=-12 StartY=15 StartZ=0 EndX=-16.5 EndY=15 EndZ=0
    g2: LineSegment StartX=-16.5 StartY=15 StartZ=0 EndX=-16.5 EndY=17 EndZ=0
    g3: LineSegment StartX=-16.5 StartY=17 StartZ=0 EndX=-13 EndY=17 EndZ=0
    g4: LineSegment StartX=-13 StartY=17 StartZ=0 EndX=-13 EndY=24 EndZ=0
    g5: ArcOfCircle CenterX=0 CenterY=62.8844 CenterZ=0 NormalX=0 NormalY=0 NormalZ=1 AngleXU=0 Radius=41 StartAngle=3.14159 EndAngle=4.38975
    g6: LineSegment StartX=-41 StartY=62.8844 StartZ=0 EndX=-41 EndY=202.884 EndZ=0
    g7: LineSegment StartX=-41 StartY=202.884 StartZ=0 EndX=-40.5 EndY=202.884 EndZ=0
    g8: LineSegment StartX=-40.5 StartY=202.884 StartZ=0 EndX=-40.5 EndY=62.8844 EndZ=0
    g9: LineSegment StartX=-12 StartY=0 StartZ=0 EndX=-11.2 EndY=0 EndZ=0
    g10: LineSegment StartX=-11.2 StartY=0 StartZ=0 EndX=-11.2 EndY=23.9639 EndZ=0
    g11: ArcOfCircle CenterX=0 CenterY=62.8844 CenterZ=0 NormalX=0 NormalY=0 NormalZ=1 AngleXU=0 Radius=40.5 StartAngle=3.14159 EndAngle=4.43219
  constraints (35):
    c: PointOnObject(g0,g-1)
    c: Vertical(g0)
    c: Coincident(g0,g1)
    c: Coincident(g1,g2)
    c: Vertical(g2)
    c: Coincident(g2,g3)
    c: Horizontal(g3)
    c: Coincident(g3,g4)
    c: Vertical(g4)
    c: Vertical(g6)
    c: Coincident(g4,g5)
    c: DistanceY(g6,g6) = 140
    c: DistanceX(g4,g-1) = 13
    c: DistanceX(g2,g-1) = 16.5
    c: DistanceY(g2,g2) = 2
    c: DistanceX(g0,g-1) = 12
    c: DistanceY(g0,g0) = 15
    c: DistanceY(g4,g4) = 7
    c: Horizontal(g1)
    c: PointOnObject(g5,g-2)
    c: Tangent(g6,g5) = 1.5708
    c: DistanceX(g5,g5) = 41
    c: Coincident(g6,g7)
    c: Horizontal(g7)
    c: Coincident(g7,g8)
    c: Vertical(g8)
    c: Coincident(g0,g9)
    c: Horizontal(g9)
    c: Coincident(g9,g10)
    c: Vertical(g10)
    c: Tangent(g11,g8) = -1.5708
    c: Coincident(g11,g10)
    c: Coincident(g11,g5)
    c: DistanceX(g7,g7) = 0.5
    c: DistanceX(g9,g9) = 0.8
FEATURE [PartDesign::Revolution] Revolution014
  Angle = 360
  Axis = (0,2e-16,1)
  Base = (0,0,0)
  Placement = pos=(0,0,0) rot=(1,0,0;1.5708rad)
  Profile = -> Sketch275
  ReferenceAxis = -> Sketch275 [V_Axis]
FEATURE [PartDesign::Body] Body161
  Group = -> [Sketch275,Revolution014]
  Origin = -> Origin373
  Placement = pos=(-7,0,33) rot=(0,0,1;0rad)
  Tip = -> Revolution014
FEATURE [Sketcher::SketchObject] Sketch277
  FullyConstrained = true
  MapMode = 5
  Placement = pos=(0,0,0) rot=(1,0,0;3.14159rad)
  Support = -> [Pad181]
  sketch-geometry (1):
    g0: Circle CenterX=0 CenterY=0 CenterZ=0 NormalX=0 NormalY=0 NormalZ=1 AngleXU=0 Radius=27
  constraints (2):
    c: Coincident(g0,g-1)
    c: Diameter(g0) = 54
FEATURE [PartDesign::Pad] Pad190
  BaseFeature = -> Pad181
  Direction = (1,1,1)
  Length = 12
  Length2 = 100
  Profile = -> Sketch277
  Type = 0
FEATURE [Sketcher::SketchObject] Sketch278
  FullyConstrained = true
  MapMode = 5
  Placement = pos=(0,0,-12) rot=(1,0,0;3.14159rad)
  Support = -> [Pad190]
  sketch-geometry (2):
    g0: Circle CenterX=0 CenterY=0 CenterZ=0 NormalX=0 NormalY=0 NormalZ=1 AngleXU=0 Radius=14.25
    g1: Circle CenterX=-21 CenterY=0 CenterZ=0 NormalX=0 NormalY=0 NormalZ=1 AngleXU=0 Radius=2.25
  constraints (5):
    c: PointOnObject(g1,g-1)
    c: Coincident(g0,g-1)
    c: DistanceX(g1,g0) = 21
    c: Diameter(g1) = 4.5
    c: Diameter(g0) = 28.5
FEATURE [PartDesign::Pocket] Pocket067
  BaseFeature = -> Pad190
  Length = 20
  Length2 = 100
  Profile = -> Sketch278
  Type = 0
FEATURE [Sketcher::SketchObject] Sketch279
  FullyConstrained = true
  MapMode = 5
  Support = -> [XY_Plane374]
  sketch-geometry (13):
    g0: Circle CenterX=0 CenterY=0 CenterZ=0 NormalX=0 NormalY=0 NormalZ=1 AngleXU=0 Radius=2.25
    g1: ArcOfCircle CenterX=21 CenterY=0 CenterZ=0 NormalX=0 NormalY=0 NormalZ=1 AngleXU=0 Radius=17.5 StartAngle=4.13287 EndAngle=8.4335
    g2: ArcOfCircle CenterX=0 CenterY=0 CenterZ=0 NormalX=0 NormalY=0 NormalZ=1 AngleXU=0 Radius=6 StartAngle=2.15031 EndAngle=2.42521
    g3: LineSegment StartX=-3.28571 StartY=5.02037 StartZ=0 EndX=11.4167 EndY=14.6427 EndZ=0
    g4: LineSegment StartX=0.798591 StartY=-7.69345 StartZ=0 EndX=11.4167 EndY=-14.6427 EndZ=0
    g5: ArcOfCircle CenterX=-20.5061 CenterY=-20.5061 CenterZ=0 NormalX=0 NormalY=0 NormalZ=1 AngleXU=0 Radius=4 StartAngle=2.42521 EndAngle=5.41544
    g6: LineSegment StartX=-4.52514 StartY=3.93994 StartZ=0 EndX=-23.5229 EndY=-17.8795 EndZ=0
    g7: LineSegment StartX=0.798591 StartY=-7.69345 StartZ=0 EndX=-17.9199 EndY=-23.5576 EndZ=0
    g8: LineSegment StartX=-4.52514 StartY=3.93994 StartZ=0 EndX=0 EndY=0 EndZ=0
    g9: LineSegment StartX=0.798591 StartY=-7.69345 StartZ=0 EndX=-3.28571 EndY=-5.02037 EndZ=0
    g10: LineSegment StartX=0 StartY=0 StartZ=0 EndX=-3.28571 EndY=-5.02037 EndZ=0
    g11: Circle CenterX=-20.5061 CenterY=-20.5061 CenterZ=0 NormalX=0 NormalY=0 NormalZ=1 AngleXU=0 Radius=1.5
    g12: LineSegment StartX=-20.5061 StartY=-20.5061 StartZ=0 EndX=0 EndY=0 EndZ=0
  constraints (30):
    c: Diameter(g1) = 35
    c: Diameter(g2) = 12
    c: Diameter(g0) = 4.5
    c: DistanceX(g0,g1) = 21
    c: Coincident(g2,g0)
    c: Tangent(g4,g1) = -1.5708
    c: Tangent(g2,g3) = 1.5708
    c: Tangent(g3,g1) = 1.5708
    c: PointOnObject(g1,g-1)
    c: Coincident(g0,g-1)
    c: Tangent(g6,g5) = -1.5708
    c: Tangent(g7,g5) = 1.5708
    c: Diameter(g5) = 8
    c: Coincident(g6,g8)
    c: Coincident(g8,g0)
    c: Tangent(g2,g6) = -1.5708
    c: Coincident(g7,g4)
    c: Coincident(g9,g4)
    c: Coincident(g10,g0)
    c: Coincident(g10,g9)
    c: Parallel(g9,g4)
    c: Distance(g10) = 6
    c: Distance(g0,g5) = 29
    c: Perpendicular(g9,g10)
    c: Coincident(g11,g5)
    c: Diameter(g11) = 3
    c: Distance(g4) = 12.69
    c: Coincident(g12,g5)
    c: Coincident(g12,g0)
    c: Angle(g12,g-1) = 2.35619
FEATURE [PartDesign::Pad] Pad191
  Direction = (1,1,1)
  Length = 1.5
  Length2 = 100
  Profile = -> Sketch279
  Type = 0
FEATURE [PartDesign::Body] Body162
  Group = -> [Sketch279,Pad191]
  Origin = -> Origin374
  Placement = pos=(-28,0,29) rot=(0,0,1;0rad)
  Tip = -> Pad191
FEATURE [Part::Feature] Solid  label="Servo horn"
  Placement = pos=(-28,-53,26.5) rot=(0.862856,0.357407,0.357407;1.71777rad)
  shape: bbox 30.51 x 30.51 x 6.2 mm, 24 faces (baked)
FEATURE [Sketcher::SketchObject] Sketch280
  FullyConstrained = true
  MapMode = 5
  Support = -> [XY_Plane375]
  sketch-geometry (6):
    g0: LineSegment StartX=-45 StartY=-73.5 StartZ=0 EndX=-45 EndY=-20.5 EndZ=0
    g1: LineSegment StartX=-38 StartY=-73.5 StartZ=0 EndX=-38 EndY=-20.5 EndZ=0
    g2: ArcOfCircle CenterX=-41.5 CenterY=-73.5 CenterZ=0 NormalX=0 NormalY=0 NormalZ=1 AngleXU=0 Radius=3.5 StartAngle=3.14159 EndAngle=6.28319
    g3: ArcOfCircle CenterX=-41.5 CenterY=-20.5 CenterZ=0 NormalX=0 NormalY=0 NormalZ=1 AngleXU=0 Radius=3.5 StartAngle=0 EndAngle=3.14159
    g4: Circle CenterX=-41.5 CenterY=-73.5 CenterZ=0 NormalX=0 NormalY=0 NormalZ=1 AngleXU=0 Radius=1.5
    g5: Circle CenterX=-41.5 CenterY=-20.5 CenterZ=0 NormalX=0 NormalY=0 NormalZ=1 AngleXU=0 Radius=1.5
  constraints (14):
    c: Vertical(g0)
    c: Vertical(g1)
    c: Tangent(g2,g0) = 1.5708
    c: Tangent(g2,g1) = -1.5708
    c: Tangent(g0,g3) = 1.5708
    c: Tangent(g1,g3) = -1.5708
    c: Diameter(g3) = 7
    c: Coincident(g4,g2)
    c: Diameter(g4) = 3
    c: Coincident(g5,g3)
    c: Diameter(g5) = 3
    c: DistanceX(g3,g-1) = 41.5
    c: DistanceY(g3,g-1) = 20.5
    c: DistanceY(g2,g3) = 53
FEATURE [PartDesign::Pad] Pad192
  Direction = (1,1,1)
  Length = 2
  Length2 = 100
  Profile = -> Sketch280
  Type = 0
FEATURE [Sketcher::SketchObject] Sketch281
  FullyConstrained = true
  MapMode = 5
  Placement = pos=(0,0,2) rot=(0,0,1;0rad)
  Support = -> [Pad192]
  sketch-geometry (2):
    g0: Circle CenterX=-41.5 CenterY=-20.5 CenterZ=0 NormalX=0 NormalY=0 NormalZ=1 AngleXU=0 Radius=3.5
    g1: Circle CenterX=-41.5 CenterY=-20.5 CenterZ=0 NormalX=0 NormalY=0 NormalZ=1 AngleXU=0 Radius=1.5
  constraints (5):
    c: Diameter(g0) = 7
    c: Coincident(g1,g0)
    c: Diameter(g1) = 3
    c: DistanceY(g0,g-1) = 20.5
    c: DistanceX(g0,g-1) = 41.5
FEATURE [PartDesign::Pad] Pad193
  BaseFeature = -> Pad192
  Direction = (1,1,1)
  Length = 4
  Length2 = 100
  Profile = -> Sketch281
  Type = 0
FEATURE [PartDesign::Body] Body163
  Group = -> [Sketch280,Pad192,Sketch281,Pad193]
  Origin = -> Origin375
  Placement = pos=(-7,0,23) rot=(0,0,1;0rad)
  Tip = -> Pad193
FEATURE [Sketcher::SketchObject] Sketch283
  FullyConstrained = true
  MapMode = 5
  Placement = pos=(0,0,-12) rot=(1,0,0;3.14159rad)
  Support = -> [Pocket067]
  sketch-geometry (6):
    g0: ArcOfCircle CenterX=0 CenterY=0 CenterZ=0 NormalX=0 NormalY=0 NormalZ=1 AngleXU=0 Radius=18 StartAngle=4.13294 EndAngle=6.28319
    g1: ArcOfCircle CenterX=0 CenterY=0 CenterZ=0 NormalX=0 NormalY=0 NormalZ=1 AngleXU=0 Radius=27 StartAngle=3.61998 EndAngle=7.53929
    g2: LineSegment StartX=-9.85614 StartY=-15.0618 StartZ=0 EndX=-19.9778 EndY=-8.43831 EndZ=0
    g3: ArcOfCircle CenterX=-21 CenterY=0 CenterZ=0 NormalX=0 NormalY=0 NormalZ=1 AngleXU=0 Radius=39 StartAngle=0 EndAngle=0.718571
    g4: LineSegment StartX=-19.9778 StartY=-8.43831 StartZ=0 EndX=-23.9689 EndY=-12.4294 EndZ=0
    g5: LineSegment StartX=-21 StartY=0 StartZ=0 EndX=-19.9778 EndY=-8.43831 EndZ=0
  constraints (16):
    c: Coincident(g0,g-1)
    c: Coincident(g1,g0)
    c: Diameter(g0) = 36
    c: Diameter(g1) = 54
    c: PointOnObject(g3,g-1)
    c: Tangent(g3,g0) = -1.5708
    c: DistanceX(g3,g0) = 21
    c: Coincident(g3,g1)
    c: Tangent(g0,g2) = 1.5708
    c: Angle(g4,g-1) = 2.35619
    c: Coincident(g5,g3)
    c: Coincident(g5,g4)
    c: Distance(g5) = 8.5
    c: Angle(g2,g-1) = 0.579449
    c: Coincident(g2,g4)
    c: Coincident(g1,g4)
FEATURE [PartDesign::Pad] Pad194
  BaseFeature = -> Pocket067
  Direction = (1,1,1)
  Length = 2.5
  Length2 = 100
  Profile = -> Sketch283
  Type = 0
FEATURE [Sketcher::SketchObject] Sketch284
  FullyConstrained = true
  MapMode = 5
  Placement = pos=(0,0,-14.5) rot=(1,0,0;3.14159rad)
  Support = -> [Pad194]
  sketch-geometry (2):
    g0: Circle CenterX=21 CenterY=0 CenterZ=0 NormalX=0 NormalY=0 NormalZ=1 AngleXU=0 Radius=2.25
    g1: Circle CenterX=0 CenterY=-21 CenterZ=0 NormalX=0 NormalY=0 NormalZ=1 AngleXU=0 Radius=2.25
  constraints (6):
    c: PointOnObject(g1,g-2)
    c: PointOnObject(g0,g-1)
    c: DistanceX(g-1,g0) = 21
    c: DistanceY(g1,g-1) = 21
    c: Diameter(g1) = 4.5
    c: Equal(g1,g0)
FEATURE [PartDesign::Pocket] Pocket069
  BaseFeature = -> Pad194
  Length = 20
  Length2 = 100
  Profile = -> Sketch284
  Type = 0
FEATURE [Sketcher::SketchObject] Sketch285
  FullyConstrained = true
  MapMode = 5
  Support = -> [XY_Plane376]
  sketch-geometry (6):
    g0: Circle CenterX=0 CenterY=0 CenterZ=0 NormalX=0 NormalY=0 NormalZ=1 AngleXU=0 Radius=11.5
    g1: Circle CenterX=0 CenterY=21 CenterZ=0 NormalX=0 NormalY=0 NormalZ=1 AngleXU=0 Radius=2.25
    g2: Circle CenterX=21 CenterY=0 CenterZ=0 NormalX=0 NormalY=0 NormalZ=1 AngleXU=0 Radius=2.25
    g3: Circle CenterX=-21 CenterY=0 CenterZ=0 NormalX=0 NormalY=0 NormalZ=1 AngleXU=0 Radius=2.25
    g4: Circle CenterX=0 CenterY=0 CenterZ=0 NormalX=0 NormalY=0 NormalZ=1 AngleXU=0 Radius=21
    g5: Circle CenterX=0 CenterY=0 CenterZ=0 NormalX=0 NormalY=0 NormalZ=1 AngleXU=0 Radius=27
  constraints (15):
    c: Coincident(g0,g-1)
    c: Diameter(g0) = 23
    c: PointOnObject(g1,g-2)
    c: PointOnObject(g2,g-1)
    c: PointOnObject(g3,g-1)
    c: Coincident(g4,g0)
    c: PointOnObject(g1,g4)
    c: PointOnObject(g2,g4)
    c: PointOnObject(g3,g4)
    c: Diameter(g4) = 42
    c: Diameter(g3) = 4.5
    c: Equal(g3,g2)
    c: Equal(g3,g1)
    c: Coincident(g5,g0)
    c: Diameter(g5) = 54
FEATURE [PartDesign::Pad] Pad195
  Direction = (1,1,1)
  Length = 2
  Length2 = 100
  Profile = -> Sketch285
  Type = 0
FEATURE [PartDesign::Body] Body164
  Group = -> [Sketch285,Pad195]
  Origin = -> Origin376
  Placement = pos=(-7,0,26.5) rot=(0,0,1;0rad)
  Tip = -> Pad195
FEATURE [Sketcher::SketchObject] Sketch286
  FullyConstrained = true
  MapMode = 5
  Placement = pos=(0,0,0) rot=(1,0,0;1.5708rad)
  Support = -> [XZ_Plane375]
  sketch-geometry (6):
    g0: LineSegment StartX=45 StartY=140 StartZ=0 EndX=45 EndY=48 EndZ=0
    g1: LineSegment StartX=45 StartY=48 StartZ=0 EndX=10 EndY=48 EndZ=0
    g2: LineSegment StartX=10 StartY=48 StartZ=0 EndX=10 EndY=53 EndZ=0
    g3: LineSegment StartX=45 StartY=140 StartZ=0 EndX=40 EndY=140 EndZ=0
    g4: LineSegment StartX=40 StartY=140 StartZ=0 EndX=40 EndY=83 EndZ=0
    g5: ArcOfCircle CenterX=10 CenterY=83 CenterZ=0 NormalX=0 NormalY=0 NormalZ=1 AngleXU=0 Radius=30 StartAngle=4.71239 EndAngle=6.28319
  constraints (18):
    c: Vertical(g0)
    c: Coincident(g0,g1)
    c: Horizontal(g1)
    c: Coincident(g1,g2)
    c: Vertical(g2)
    c: Coincident(g0,g3)
    c: Coincident(g3,g4)
    c: Vertical(g4)
    c: Tangent(g5,g4) = 1.5708
    c: Coincident(g5,g2)
    c: DistanceY(g-1,g1) = 48
    c: Horizontal(g3)
    c: DistanceX(g-1,g0) = 45
    c: DistanceX(g1,g1) = 35
    c: DistanceY(g2,g2) = 5
    c: DistanceX(g3,g3) = 5
    c: DistanceY(g0,g0) = 92
    c: Vertical(g2,g5)
FEATURE [PartDesign::Pad] Pad196
  Direction = (1,1,1)
  Length = 30
  Length2 = 100
  Midplane = true
  Placement = pos=(0,0,0) rot=(1,0,0;1.5708rad)
  Profile = -> Sketch286
  Type = 0
FEATURE [Sketcher::SketchObject] Sketch287
  FullyConstrained = true
  MapMode = 5
  Placement = pos=(0,0,140) rot=(0,0,1;3.14159rad)
  Support = -> [Pad196]
  sketch-geometry (3):
    g0: Circle CenterX=-34 CenterY=10 CenterZ=0 NormalX=0 NormalY=0 NormalZ=1 AngleXU=0 Radius=4
    g1: Circle CenterX=-34 CenterY=-10 CenterZ=0 NormalX=0 NormalY=0 NormalZ=1 AngleXU=0 Radius=4
    g2: Circle CenterX=-14 CenterY=0 CenterZ=0 NormalX=0 NormalY=0 NormalZ=1 AngleXU=0 Radius=4
  constraints (8):
    c: Symmetric(g1,g0,g-1)
    c: Diameter(g1) = 8
    c: Equal(g1,g0)
    c: DistanceY(g1,g0) = 20
    c: DistanceX(g1,g-1) = 34
    c: PointOnObject(g2,g-1)
    c: Equal(g2,g0)
    c: DistanceX(g2,g-1) = 14
FEATURE [PartDesign::Pocket] Pocket070
  BaseFeature = -> Pad196
  Length = 87
  Length2 = 100
  Placement = pos=(0,0,0) rot=(1,0,0;1.5708rad)
  Profile = -> Sketch287
  Type = 0
FEATURE [Sketcher::SketchObject] Sketch288
  FullyConstrained = true
  MapMode = 5
  Placement = pos=(0,0,140) rot=(0,0,1;3.14159rad)
  Support = -> [Pocket070]
  sketch-geometry (3):
    g0: Circle CenterX=-34 CenterY=10 CenterZ=0 NormalX=0 NormalY=0 NormalZ=1 AngleXU=0 Radius=2.25
    g1: Circle CenterX=-34 CenterY=-10 CenterZ=0 NormalX=0 NormalY=0 NormalZ=1 AngleXU=0 Radius=2.25
    g2: Circle CenterX=-14 CenterY=0 CenterZ=0 NormalX=0 NormalY=0 NormalZ=1 AngleXU=0 Radius=2.25
  constraints (8):
    c: Symmetric(g0,g1,g-1)
    c: Diameter(g1) = 4.5
    c: Equal(g1,g0)
    c: DistanceY(g1,g0) = 20
    c: DistanceX(g1,g-1) = 34
    c: PointOnObject(g2,g-1)
    c: Equal(g2,g1)
    c: DistanceX(g2,g-1) = 14
FEATURE [PartDesign::Pocket] Pocket071
  BaseFeature = -> Pocket070
  Length = 95
  Length2 = 100
  Placement = pos=(0,0,0) rot=(1,0,0;1.5708rad)
  Profile = -> Sketch288
  Type = 0
FEATURE [Sketcher::SketchObject] Sketch289
  FullyConstrained = true
  MapMode = 5
  Placement = pos=(40,0,0) rot=(0.707107,0,-0.707107;3.14159rad)
  Support = -> [Pocket071]
  sketch-geometry (2):
    g0: Circle CenterX=-135 CenterY=10 CenterZ=0 NormalX=0 NormalY=0 NormalZ=1 AngleXU=0 Radius=1.75
    g1: Circle CenterX=-135 CenterY=-10 CenterZ=0 NormalX=0 NormalY=0 NormalZ=1 AngleXU=0 Radius=1.75
  constraints (5):
    c: Symmetric(g1,g0,g-1)
    c: DistanceY(g1,g0) = 20
    c: Diameter(g1) = 3.5
    c: Equal(g1,g0)
    c: DistanceX(g0,g-1) = 135
FEATURE [PartDesign::Pocket] Pocket072
  BaseFeature = -> Pocket071
  Length = 10
  Length2 = 100
  Placement = pos=(0,0,0) rot=(1,0,0;1.5708rad)
  Profile = -> Sketch289
  Type = 0
FEATURE [Sketcher::SketchObject] Sketch290
  FullyConstrained = true
  MapMode = 5
  Support = -> [XY_Plane378]
  sketch-geometry (5):
    g0: Circle CenterX=0 CenterY=0 CenterZ=0 NormalX=0 NormalY=0 NormalZ=1 AngleXU=0 Radius=42.5
    g1: ArcOfCircle CenterX=0 CenterY=0 CenterZ=0 NormalX=0 NormalY=0 NormalZ=1 AngleXU=0 Radius=47.5 StartAngle=0.321289 EndAngle=5.9619
    g2: LineSegment StartX=45.0694 StartY=-15 StartZ=0 EndX=47 EndY=-15 EndZ=0
    g3: LineSegment StartX=47 StartY=-15 StartZ=0 EndX=47 EndY=15 EndZ=0
    g4: LineSegment StartX=47 StartY=15 StartZ=0 EndX=45.0694 EndY=15 EndZ=0
  constraints (13):
    c: Coincident(g0,g-1)
    c: Coincident(g1,g0)
    c: Diameter(g0) = 85
    c: Diameter(g1) = 95
    c: Horizontal(g2)
    c: Coincident(g2,g3)
    c: Coincident(g3,g4)
    c: Coincident(g2,g1)
    c: Horizontal(g4)
    c: Coincident(g4,g1)
    c: DistanceX(g0,g3) = 47
    c: DistanceY(g3,g3) = 30
    c: Symmetric(g2,g3,g-1)
FEATURE [PartDesign::Pad] Pad197
  Direction = (1,1,1)
  Length = 10
  Length2 = 100
  Midplane = true
  Profile = -> Sketch290
  Type = 0
FEATURE [Sketcher::SketchObject] Sketch291
  FullyConstrained = true
  MapMode = 5
  Support = -> [XY_Plane378]
  sketch-geometry (4):
    g0: LineSegment StartX=44.4 StartY=10.85 StartZ=0 EndX=39 EndY=16.25 EndZ=0
    g1: LineSegment StartX=31 StartY=10 StartZ=0 EndX=51 EndY=10 EndZ=0
    g2: LineSegment StartX=39 StartY=16.25 StartZ=0 EndX=39 EndY=10.85 EndZ=0
    g3: LineSegment StartX=39 StartY=10.85 StartZ=0 EndX=44.4 EndY=10.85 EndZ=0
  constraints (13):
    c: Horizontal(g1)
    c: DistanceX(g1,g1) = 20
    c: DistanceY(g-1,g1) = 10
    c: DistanceY(g-1,g0) = 16.25
    c: DistanceX(g-1,g0) = 39
    c: Coincident(g0,g2)
    c: Vertical(g2)
    c: Coincident(g2,g3)
    c: Horizontal(g3)
    c: Coincident(g0,g3)
    c: Equal(g2,g3)
    c: DistanceY(g2,g2) = 5.4
    c: DistanceX(g-1,g1) = 31
FEATURE [PartDesign::Groove] Groove004
  Angle = 360
  Axis = (20,0,0)
  Base = (31,10,0)
  BaseFeature = -> Pad197
  Profile = -> Sketch291
  ReferenceAxis = -> Sketch291 [Axis0]
  Reversed = true
FEATURE [Sketcher::SketchObject] Sketch292
  FullyConstrained = true
  MapMode = 5
  Support = -> [XY_Plane378]
  sketch-geometry (4):
    g0: LineSegment StartX=44.4 StartY=-9.15 StartZ=0 EndX=39 EndY=-3.75 EndZ=0
    g1: LineSegment StartX=31 StartY=-10 StartZ=0 EndX=51 EndY=-10 EndZ=0
    g2: LineSegment StartX=39 StartY=-3.75 StartZ=0 EndX=39 EndY=-9.15 EndZ=0
    g3: LineSegment StartX=39 StartY=-9.15 StartZ=0 EndX=44.4 EndY=-9.15 EndZ=0
  constraints (13):
    c: Horizontal(g1)
    c: DistanceX(g1,g1) = 20
    c: DistanceX(g-1,g0) = 39
    c: Coincident(g0,g2)
    c: Vertical(g2)
    c: Coincident(g2,g3)
    c: Horizontal(g3)
    c: Coincident(g0,g3)
    c: Equal(g2,g3)
    c: DistanceY(g2,g2) = 5.4
    c: DistanceX(g-1,g1) = 31
    c: DistanceY(g0,g-1) = 3.75
    c: DistanceY(g1,g-1) = 10
FEATURE [PartDesign::Groove] Groove005
  Angle = 360
  Axis = (20,0,0)
  Base = (31,-10,0)
  BaseFeature = -> Groove004
  Profile = -> Sketch292
  ReferenceAxis = -> Sketch292 [Axis0]
  Reversed = true
FEATURE [Sketcher::SketchObject] Sketch293
  FullyConstrained = true
  MapMode = 5
  Placement = pos=(47,0,0) rot=(0.57735,0.57735,0.57735;2.0944rad)
  Support = -> [Groove005]
  sketch-geometry (2):
    g0: Circle CenterX=10 CenterY=0 CenterZ=0 NormalX=0 NormalY=0 NormalZ=1 AngleXU=0 Radius=1.75
    g1: Circle CenterX=-10 CenterY=0 CenterZ=0 NormalX=0 NormalY=0 NormalZ=1 AngleXU=0 Radius=1.75
  constraints (5):
    c: PointOnObject(g0,g-1)
    c: Symmetric(g1,g0,g-1)
    c: DistanceX(g1,g0) = 20
    c: Diameter(g1) = 3.5
    c: Equal(g1,g0)
FEATURE [PartDesign::Pocket] Pocket073
  BaseFeature = -> Groove005
  Length = 10
  Length2 = 100
  Profile = -> Sketch293
  Type = 0
FEATURE [PartDesign::Body] Body166
  Group = -> [Sketch290,Pad197,Sketch291,Groove004,Sketch292,Groove005,Sketch293,Pocket073]
  Origin = -> Origin378
  Placement = pos=(-7,0,135) rot=(0,0,1;0rad)
  Tip = -> Pocket073
FEATURE [Sketcher::SketchObject] Sketch294
  FullyConstrained = true
  MapMode = 5
  Placement = pos=(40,0,0) rot=(0.707107,0,-0.707107;3.14159rad)
  Support = -> [Pocket072]
  sketch-geometry (2):
    g0: Circle CenterX=-82.5 CenterY=0 CenterZ=0 NormalX=0 NormalY=0 NormalZ=1 AngleXU=0 Radius=2.25
    g1: Circle CenterX=-107.5 CenterY=0 CenterZ=0 NormalX=0 NormalY=0 NormalZ=1 AngleXU=0 Radius=2.25
  constraints (6):
    c: PointOnObject(g1,g-1)
    c: PointOnObject(g0,g-1)
    c: DistanceX(g1,g0) = 25
    c: Diameter(g1) = 4.5
    c: Equal(g1,g0)
    c: DistanceX(g0,g-1) = 82.5
FEATURE [PartDesign::Pocket] Pocket074
  BaseFeature = -> Pocket072
  Length = 20
  Length2 = 100
  Midplane = true
  Placement = pos=(0,0,0) rot=(1,0,0;1.5708rad)
  Profile = -> Sketch294
  Type = 0
FEATURE [PartDesign::Chamfer] Chamfer003
  Angle = 45
  Base = -> Pocket074 [Edge28,Edge31,Edge30,Edge32]
  BaseFeature = -> Pocket074
  ChamferType = 0
  FlipDirection = false
  Placement = pos=(0,0,0) rot=(1,0,0;1.5708rad)
  Size = 2
  Size2 = 1
  SupportTransform = false
FEATURE [PartDesign::Body] Body165
  Group = -> [Sketch286,Pad196,Sketch287,Pocket070,Sketch288,Pocket071,Sketch289,Pocket072,Sketch294,Pocket074,Chamfer003]
  Origin = -> Origin377
  Tip = -> Chamfer003
FEATURE [Sketcher::SketchObject] Sketch295
  FullyConstrained = true
  MapMode = 5
  Placement = pos=(0,0,0) rot=(1,0,0;1.5708rad)
  Support = -> [XZ_Plane368]
  sketch-geometry (4):
    g0: LineSegment StartX=-14.75 StartY=-1.5 StartZ=0 EndX=-12.75 EndY=-1.85 EndZ=0
    g1: LineSegment StartX=-12.75 StartY=-1.85 StartZ=0 EndX=-12.75 EndY=-2.65 EndZ=0
    g2: LineSegment StartX=-12.75 StartY=-2.65 StartZ=0 EndX=-14.75 EndY=-3 EndZ=0
    g3: LineSegment StartX=-14.75 StartY=-1.5 StartZ=0 EndX=-14.75 EndY=-3 EndZ=0
  constraints (12):
    c: Coincident(g0,g1)
    c: Vertical(g1)
    c: Coincident(g1,g2)
    c: Coincident(g3,g0)
    c: Coincident(g3,g2)
    c: Vertical(g3)
    c: Equal(g2,g0)
    c: DistanceX(g2,g1) = 2
    c: DistanceY(g1,g1) = 0.8
    c: DistanceY(g3,g3) = 1.5
    c: DistanceX(g2,g-1) = 14.75
    c: DistanceY(g0,g-1) = 1.5
FEATURE [PartDesign::AdditiveHelix] AdditiveHelix
  Angle = 0
  Axis = (0,-2e-16,1)
  Base = (0,0,0)
  BaseFeature = -> Pocket069
  HasBeenEdited = true
  Height = 8.25
  LeftHanded = false
  Mode = 0
  Outside = false
  Pitch = 2.5
  Profile = -> Sketch295
  ReferenceAxis = -> Sketch295 [V_Axis]
  Reversed = true
  Turns = 3
FEATURE [PartDesign::Body] Body158
  Group = -> [Sketch266,Pad181,Sketch277,Pad190,Sketch278,Pocket067,Sketch283,Pad194,Sketch284,Pocket069,Sketch295,AdditiveHelix]
  Origin = -> Origin370
  Placement = pos=(-7,0,43) rot=(0,0,1;0rad)
  Tip = -> AdditiveHelix
FEATURE [App::Part] Part024
  Group = -> [Body158,Body159,Body161,Body162,Solid,Body163,Body164,Body165,Body166]
  Origin = -> Origin369
  Placement = pos=(-187,0,0) rot=(0,0,1;0rad)
FEATURE [TechDraw::DrawSVGTemplate] Template001
  EditableTexts = Designed_by_Name=Designed by Name; Drawing_number=Drawing number; FC-Date=Date; FC-SC=Scale; FC-SH=Sheet; FC-Title=Title; Subtitle=Subtitle; Weight=Weight
  Height = 210
  Orientation = 1
  Width = 297
FEATURE [TechDraw::DrawViewPart] View002
  CoarseView = false
  Direction = (0,1,0)
  Focus = 100
  HardHidden = false
  IsoCount = 0
  IsoHidden = false
  IsoVisible = false
  LockPosition = false
  Perspective = false
  Rotation = 0
  ScaleType = 0
  SeamHidden = false
  SeamVisible = true
  SmoothHidden = false
  SmoothVisible = true
  Source = -> [Body036]
  X = 60.9723
  XDirection = (-1,0,0)
  Y = 116.648
FEATURE [TechDraw::DrawViewPart] View003
  CoarseView = false
  Direction = (0,1,0)
  Focus = 100
  HardHidden = false
  IsoCount = 0
  IsoHidden = false
  IsoVisible = false
  LockPosition = false
  Perspective = false
  Rotation = 0
  ScaleType = 0
  SeamHidden = false
  SeamVisible = true
  SmoothHidden = false
  SmoothVisible = true
  Source = -> [Body036]
  X = 198.853
  XDirection = (0,0,-1)
  Y = 155.526
FEATURE [Sketcher::SketchObject] Sketch296
  FullyConstrained = true
  MapMode = 5
  Placement = pos=(0,0,0) rot=(0.57735,0.57735,0.57735;2.0944rad)
  Support = -> [YZ_Plane376]
  sketch-geometry (14):
    g0: LineSegment StartX=-15 StartY=130 StartZ=0 EndX=15 EndY=130 EndZ=0
    g1: LineSegment StartX=15 StartY=130 StartZ=0 EndX=15 EndY=60 EndZ=0
    g2: LineSegment StartX=15 StartY=60 StartZ=0 EndX=-15 EndY=60 EndZ=0
    g3: LineSegment StartX=-15 StartY=60 StartZ=0 EndX=-15 EndY=130 EndZ=0
    g4: Circle CenterX=0 CenterY=107.5 CenterZ=0 NormalX=0 NormalY=0 NormalZ=1 AngleXU=0 Radius=2.25
    g5: Circle CenterX=0 CenterY=82.5 CenterZ=0 NormalX=0 NormalY=0 NormalZ=1 AngleXU=0 Radius=2.25
    g6: Circle CenterX=-10 CenterY=125 CenterZ=0 NormalX=0 NormalY=0 NormalZ=1 AngleXU=0 Radius=1.6
    g7: Circle CenterX=10 CenterY=125 CenterZ=0 NormalX=0 NormalY=0 NormalZ=1 AngleXU=0 Radius=1.6
    g8: Circle CenterX=10 CenterY=65 CenterZ=0 NormalX=0 NormalY=0 NormalZ=1 AngleXU=0 Radius=1.6
    g9: Circle CenterX=-10 CenterY=65 CenterZ=0 NormalX=0 NormalY=0 NormalZ=1 AngleXU=0 Radius=1.6
    g10: LineSegment StartX=-10 StartY=125 StartZ=0 EndX=10 EndY=125 EndZ=0
    g11: LineSegment StartX=10 StartY=125 StartZ=0 EndX=10 EndY=65 EndZ=0
    g12: LineSegment StartX=10 StartY=65 StartZ=0 EndX=-10 EndY=65 EndZ=0
    g13: LineSegment StartX=-10 StartY=65 StartZ=0 EndX=-10 EndY=125 EndZ=0
  constraints (36):
    c: Coincident(g0,g1)
    c: Coincident(g1,g2)
    c: Coincident(g2,g3)
    c: Coincident(g3,g0)
    c: Horizontal(g0)
    c: Vertical(g1)
    c: Vertical(g3)
    c: DistanceX(g2,g2) = 30
    c: DistanceY(g1,g1) = 70
    c: DistanceY(g-1,g2) = 60
    c: Symmetric(g2,g1,g-2)
    c: PointOnObject(g4,g-2)
    c: PointOnObject(g5,g-2)
    c: Coincident(g10,g11)
    c: Coincident(g11,g12)
    c: Coincident(g12,g13)
    c: Coincident(g13,g10)
    c: Horizontal(g10)
    c: Vertical(g11)
    c: Vertical(g13)
    c: Coincident(g10,g6)
    c: Coincident(g11,g8)
    c: Coincident(g7,g10)
    c: Coincident(g9,g12)
    c: DistanceX(g10,g10) = 20
    c: DistanceY(g11,g11) = 60
    c: Symmetric(g8,g9,g-2)
    c: DistanceY(g2,g9) = 5
    c: DistanceY(g5,g4) = 25
    c: DistanceY(g2,g5) = 22.5
    c: Diameter(g5) = 4.5
    c: Equal(g5,g4)
    c: Diameter(g9) = 3.2
    c: Equal(g9,g8)
    c: Equal(g9,g7)
    c: Equal(g9,g6)
FEATURE [PartDesign::Pad] Pad198
  Direction = (1,1,1)
  Length = 2
  Length2 = 100
  Placement = pos=(0,0,0) rot=(0.57735,0.57735,0.57735;2.0944rad)
  Profile = -> Sketch296
  Type = 0
FEATURE [PartDesign::Chamfer] Chamfer004
  Angle = 45
  Base = -> Pad198 [Edge20,Edge23,Edge26,Edge29]
  BaseFeature = -> Pad198
  ChamferType = 0
  FlipDirection = false
  Placement = pos=(0,0,0) rot=(0.57735,0.57735,0.57735;2.0944rad)
  Size = 1.5
  Size2 = 1
  SupportTransform = false
FEATURE [PartDesign::Body] Body167
  Group = -> [Sketch296,Pad198,Chamfer004]
  Origin = -> Origin379
  Placement = pos=(-42,0,0) rot=(0,0,1;0rad)
  Tip = -> Chamfer004
FEATURE [App::Part] Part003  label="front_attach"
  Group = -> [Body040,Body041,Body043,Open_CASCADE_STEP_translator_7_3_1004,Body154,Body155,Body156,Body157,Body167]
  Origin = -> Origin053
  Placement = pos=(-100,0,0) rot=(0,0,1;0rad)
FEATURE [TechDraw::DrawSVGTemplate] Template002
  EditableTexts = Designed_by_Name=Designed by Name; Drawing_number=Drawing number; FC-Date=Date; FC-SC=Scale; FC-SH=Sheet; FC-Title=Title; Subtitle=Subtitle; Weight=Weight
  Height = 210
  Orientation = 1
  Width = 297
FEATURE [TechDraw::DrawPage] Page002
  KeepUpdated = true
  NextBalloonIndex = 1
  ProjectionType = 0
  Template = -> Template002
FEATURE [TechDraw::DrawViewPart] View004
  CoarseView = false
  Direction = (-1,0,0)
  Focus = 100
  HardHidden = false
  IsoCount = 0
  IsoHidden = false
  IsoVisible = false
  LockPosition = false
  Perspective = false
  Rotation = 0
  ScaleType = 0
  SeamHidden = false
  SeamVisible = true
  SmoothHidden = false
  SmoothVisible = true
  Source = -> [Body167]
  X = 159.741
  XDirection = (0,0,1)
  Y = 86.1639
FEATURE [TechDraw::DrawViewPart] View005
  CoarseView = false
  Direction = (-1,0,0)
  Focus = 100
  HardHidden = false
  IsoCount = 0
  IsoHidden = false
  IsoVisible = false
  LockPosition = false
  Perspective = false
  Rotation = 0
  ScaleType = 0
  SeamHidden = false
  SeamVisible = true
  SmoothHidden = false
  SmoothVisible = true
  Source = -> [Body167]
  X = 236.908
  XDirection = (0,0,1)
  Y = 86.4677
FEATURE [TechDraw::DrawPage] Page001
  KeepUpdated = true
  NextBalloonIndex = 1
  ProjectionType = 0
  Template = -> Template001
  Views = -> [View002,View003,View004,View005]
FEATURE [Sketcher::SketchObject] Sketch297
  FullyConstrained = true
  MapMode = 5
  Support = -> [XY_Plane380]
  sketch-geometry (4):
    g0: LineSegment StartX=-80 StartY=16 StartZ=0 EndX=80 EndY=16 EndZ=0
    g1: LineSegment StartX=80 StartY=16 StartZ=0 EndX=80 EndY=-11 EndZ=0
    g2: LineSegment StartX=80 StartY=-11 StartZ=0 EndX=-80 EndY=-11 EndZ=0
    g3: LineSegment StartX=-80 StartY=-11 StartZ=0 EndX=-80 EndY=16 EndZ=0
  constraints (11):
    c: Coincident(g0,g1)
    c: Coincident(g1,g2)
    c: Coincident(g2,g3)
    c: Coincident(g3,g0)
    c: Horizontal(g2)
    c: Vertical(g1)
    c: Vertical(g3)
    c: Symmetric(g0,g0,g-2)
    c: DistanceY(g2,g-1) = 11
    c: DistanceY(g3,g3) = 27
    c: DistanceX(g0,g0) = 160
FEATURE [PartDesign::Pad] Pad199
  Direction = (1,1,1)
  Length = 3
  Length2 = 100
  Profile = -> Sketch297
  Type = 0
FEATURE [Sketcher::SketchObject] Sketch298
  FullyConstrained = true
  MapMode = 5
  Placement = pos=(0,0,0) rot=(1,0,0;3.14159rad)
  Support = -> [Pad199]
  sketch-geometry (4):
    g0: LineSegment StartX=-30 StartY=-13 StartZ=0 EndX=30 EndY=-13 EndZ=0
    g1: LineSegment StartX=30 StartY=-13 StartZ=0 EndX=30 EndY=-16 EndZ=0
    g2: LineSegment StartX=30 StartY=-16 StartZ=0 EndX=-30 EndY=-16 EndZ=0
    g3: LineSegment StartX=-30 StartY=-16 StartZ=0 EndX=-30 EndY=-13 EndZ=0
  constraints (11):
    c: Coincident(g0,g1)
    c: Coincident(g1,g2)
    c: Coincident(g2,g3)
    c: Coincident(g3,g0)
    c: Horizontal(g0)
    c: Vertical(g1)
    c: Vertical(g3)
    c: Symmetric(g2,g1,g-2)
    c: DistanceX(g2,g2) = 60
    c: DistanceY(g0,g-1) = 13
    c: DistanceY(g1,g1) = 3
FEATURE [PartDesign::Pad] Pad200
  BaseFeature = -> Pad199
  Direction = (1,1,1)
  Length = 15
  Length2 = 100
  Profile = -> Sketch298
  Type = 0
FEATURE [Sketcher::SketchObject] Sketch299
  FullyConstrained = true
  MapMode = 5
  Placement = pos=(0,16,0) rot=(0,0.707107,0.707107;3.14159rad)
  Support = -> [Pad200]
  sketch-geometry (3):
    g0: Circle CenterX=-20.4 CenterY=-8.5 CenterZ=0 NormalX=0 NormalY=0 NormalZ=1 AngleXU=0 Radius=2.25
    g1: Circle CenterX=20.4 CenterY=-8.5 CenterZ=0 NormalX=0 NormalY=0 NormalZ=1 AngleXU=0 Radius=2.25
    g2: Circle CenterX=0 CenterY=-21 CenterZ=0 NormalX=0 NormalY=0 NormalZ=1 AngleXU=0 Radius=12.5
  constraints (8):
    c: Symmetric(g1,g0,g-2)
    c: DistanceX(g0,g1) = 40.8
    c: DistanceY(g0,g-1) = 8.5
    c: Diameter(g0) = 4.5
    c: Equal(g0,g1)
    c: PointOnObject(g2,g-2)
    c: DistanceY(g2,g-1) = 21
    c: Diameter(g2) = 25
FEATURE [PartDesign::Pocket] Pocket075
  BaseFeature = -> Pad200
  Length = 5
  Length2 = 100
  Profile = -> Sketch299
  Type = 0
FEATURE [Sketcher::SketchObject] Sketch300
  FullyConstrained = true
  MapMode = 5
  Placement = pos=(0,0,3) rot=(0,0,1;0rad)
  Support = -> [Pocket075]
  sketch-geometry (14):
    g0: Circle CenterX=-10 CenterY=-4 CenterZ=0 NormalX=0 NormalY=0 NormalZ=1 AngleXU=0 Radius=3
    g1: Circle CenterX=10 CenterY=-4 CenterZ=0 NormalX=0 NormalY=0 NormalZ=1 AngleXU=0 Radius=3
    g2: Circle CenterX=-75.5 CenterY=8.25 CenterZ=0 NormalX=0 NormalY=0 NormalZ=1 AngleXU=0 Radius=1.75
    g3: Circle CenterX=-45 CenterY=-8.25 CenterZ=0 NormalX=0 NormalY=0 NormalZ=1 AngleXU=0 Radius=1.75
    g4: Circle CenterX=45 CenterY=8.25 CenterZ=0 NormalX=0 NormalY=0 NormalZ=1 AngleXU=0 Radius=1.75
    g5: Circle CenterX=75.5 CenterY=-8.25 CenterZ=0 NormalX=0 NormalY=0 NormalZ=1 AngleXU=0 Radius=1.75
    g6: ArcOfCircle CenterX=57 CenterY=-11 CenterZ=0 NormalX=0 NormalY=0 NormalZ=1 AngleXU=0 Radius=4 StartAngle=1.5708 EndAngle=4.71239
    g7: ArcOfCircle CenterX=67 CenterY=-11 CenterZ=0 NormalX=0 NormalY=0 NormalZ=1 AngleXU=0 Radius=4 StartAngle=4.71239 EndAngle=7.85398
    g8: LineSegment StartX=57 StartY=-15 StartZ=0 EndX=67 EndY=-15 EndZ=0
    g9: LineSegment StartX=57 StartY=-7 StartZ=0 EndX=67 EndY=-7 EndZ=0
    g10: ArcOfCircle CenterX=-67 CenterY=-11 CenterZ=0 NormalX=0 NormalY=0 NormalZ=1 AngleXU=0 Radius=4 StartAngle=1.5708 EndAngle=4.71239
    g11: ArcOfCircle CenterX=-57 CenterY=-11 CenterZ=0 NormalX=0 NormalY=0 NormalZ=1 AngleXU=0 Radius=4 StartAngle=4.71239 EndAngle=7.85398
    g12: LineSegment StartX=-67 StartY=-15 StartZ=0 EndX=-57 EndY=-15 EndZ=0
    g13: LineSegment StartX=-67 StartY=-7 StartZ=0 EndX=-57 EndY=-7 EndZ=0
  constraints (37):
    c: Symmetric(g1,g0,g-2)
    c: DistanceX(g0,g1) = 20
    c: Diameter(g1) = 6
    c: Equal(g1,g0)
    c: DistanceY(g1,g-1) = 4
    c: DistanceY(g3,g2) = 16.5
    c: Diameter(g2) = 3.5
    c: Equal(g2,g3)
    c: DistanceX(g2,g3) = 30.5
    c: DistanceY(g3,g-1) = 8.25
    c: DistanceX(g3,g-1) = 45
    c: DistanceX(g4,g5) = 30.5
    c: DistanceY(g5,g4) = 16.5
    c: Diameter(g4) = 3.5
    c: Equal(g4,g5)
    c: DistanceX(g-1,g4) = 45
    c: DistanceY(g-1,g4) = 8.25
    c: Tangent(g6,g9) = 1.5708
    c: Tangent(g6,g8) = -1.5708
    c: Tangent(g8,g7) = -1.5708
    c: Tangent(g9,g7) = 1.5708
    c: Horizontal(g8)
    c: Equal(g6,g7)
    c: DistanceX(g-1,g6) = 57
    c: DistanceX(g9,g9) = 10
    c: DistanceY(g6,g-1) = 11
    c: Diameter(g7) = 8
    c: Tangent(g10,g13) = 1.5708
    c: Tangent(g10,g12) = -1.5708
    c: Tangent(g12,g11) = -1.5708
    c: Tangent(g13,g11) = 1.5708
    c: Horizontal(g12)
    c: Equal(g10,g11)
    c: DistanceX(g11,g-1) = 57
    c: DistanceX(g12,g12) = 10
    c: Diameter(g11) = 8
    c: DistanceY(g11,g-1) = 11
FEATURE [PartDesign::Pocket] Pocket076
  BaseFeature = -> Pocket075
  Length = 5
  Length2 = 100
  Profile = -> Sketch300
  Type = 0
FEATURE [PartDesign::Body] Body168
  Group = -> [Sketch297,Pad199,Sketch298,Pad200,Sketch299,Pocket075,Sketch300,Pocket076]
  Origin = -> Origin380
  Placement = pos=(0,0,122) rot=(0,0,1;0rad)
  Tip = -> Pocket076
FEATURE [Sketcher::SketchObject] Sketch302
  FullyConstrained = true
  MapMode = 5
  Placement = pos=(0,0,0) rot=(0.57735,0.57735,0.57735;2.0944rad)
  Support = -> [YZ_Plane378]
  sketch-geometry (10):
    g0: LineSegment StartX=-9.25 StartY=0 StartZ=0 EndX=-9.25 EndY=15 EndZ=0
    g1: LineSegment StartX=-9.25 StartY=15 StartZ=0 EndX=9.25 EndY=15 EndZ=0
    g2: LineSegment StartX=9.25 StartY=15 StartZ=0 EndX=9.25 EndY=0 EndZ=0
    g3: LineSegment StartX=9.25 StartY=0 StartZ=0 EndX=7.25 EndY=0 EndZ=0
    g4: LineSegment StartX=7.25 StartY=0 StartZ=0 EndX=7.25 EndY=10.5 EndZ=0
    g5: LineSegment StartX=5.25 StartY=12.5 StartZ=0 EndX=-5.25 EndY=12.5 EndZ=0
    g6: LineSegment StartX=-7.25 StartY=10.5 StartZ=0 EndX=-7.25 EndY=0 EndZ=0
    g7: LineSegment StartX=-7.25 StartY=0 StartZ=0 EndX=-9.25 EndY=0 EndZ=0
    g8: ArcOfCircle CenterX=5.25 CenterY=10.5 CenterZ=0 NormalX=0 NormalY=0 NormalZ=1 AngleXU=0 Radius=2 StartAngle=0 EndAngle=1.5708
    g9: ArcOfCircle CenterX=-5.25 CenterY=10.5 CenterZ=0 NormalX=0 NormalY=0 NormalZ=1 AngleXU=0 Radius=2 StartAngle=1.5708 EndAngle=3.14159
  constraints (27):
    c: Vertical(g0)
    c: Coincident(g0,g1)
    c: Coincident(g1,g2)
    c: PointOnObject(g2,g-1)
    c: Vertical(g2)
    c: Coincident(g2,g3)
    c: PointOnObject(g3,g-1)
    c: Vertical(g4)
    c: Horizontal(g5)
    c: PointOnObject(g6,g-1)
    c: Coincident(g6,g7)
    c: Coincident(g7,g0)
    c: PointOnObject(g0,g-1)
    c: Vertical(g6)
    c: DistanceX(g7,g7) = 2
    c: DistanceX(g3,g3) = 2
    c: DistanceY(g2,g2) = 15
    c: DistanceX(g6,g3) = 14.5
    c: Tangent(g5,g8) = -1.5708
    c: Tangent(g4,g8) = -1.5708
    c: Tangent(g5,g9) = -1.5708
    c: Tangent(g6,g9) = -1.5708
    c: Diameter(g9) = 4
    c: Equal(g9,g8)
    c: DistanceY(g5,g1) = 2.5
    c: Coincident(g4,g3)
    c: Symmetric(g1,g0,g-2)
FEATURE [PartDesign::Pad] Pad201
  Direction = (1,1,1)
  Length = 32.5
  Length2 = 100
  Midplane = true
  Placement = pos=(0,0,0) rot=(0.57735,0.57735,0.57735;2.0944rad)
  Profile = -> Sketch302
  Type = 0
FEATURE [Sketcher::SketchObject] Sketch303
  FullyConstrained = true
  MapMode = 5
  Placement = pos=(4.1e-15,9.25,-2e-15) rot=(0.57735,0.57735,0.57735;4.18879rad)
  Support = -> [Pad201]
  sketch-geometry (6):
    g0: LineSegment StartX=0 StartY=14.25 StartZ=0 EndX=10.5 EndY=14.25 EndZ=0
    g1: LineSegment StartX=12.5 StartY=12.25 StartZ=0 EndX=12.5 EndY=-12.25 EndZ=0
    g2: LineSegment StartX=10.5 StartY=-14.25 StartZ=0 EndX=0 EndY=-14.25 EndZ=0
    g3: LineSegment StartX=0 StartY=-14.25 StartZ=0 EndX=0 EndY=14.25 EndZ=0
    g4: ArcOfCircle CenterX=10.5 CenterY=12.25 CenterZ=0 NormalX=0 NormalY=0 NormalZ=1 AngleXU=0 Radius=2 StartAngle=-9e-16 EndAngle=1.5708
    g5: ArcOfCircle CenterX=10.5 CenterY=-12.25 CenterZ=0 NormalX=0 NormalY=0 NormalZ=1 AngleXU=0 Radius=2 StartAngle=4.71239 EndAngle=6.28319
  constraints (15):
    c: Coincident(g2,g3)
    c: Coincident(g3,g0)
    c: Horizontal(g0)
    c: Horizontal(g2)
    c: Vertical(g1)
    c: Vertical(g3)
    c: DistanceY(g3,g3) = 28.5
    c: Symmetric(g0,g2,g-1)
    c: Tangent(g0,g4) = 1.5708
    c: Tangent(g1,g4) = 1.5708
    c: Tangent(g2,g5) = 1.5708
    c: Tangent(g1,g5) = 1.5708
    c: Diameter(g5) = 4
    c: Equal(g5,g4)
    c: DistanceX(g2,g1) = 12.5
FEATURE [PartDesign::Pocket] Pocket077
  BaseFeature = -> Pad201
  Length = 20
  Length2 = 100
  Placement = pos=(0,0,0) rot=(0.57735,0.57735,0.57735;2.0944rad)
  Profile = -> Sketch303
  Type = 0
FEATURE [Sketcher::SketchObject] Sketch304
  FullyConstrained = true
  MapMode = 5
  Placement = pos=(-4.2e-15,6.6e-15,15) rot=(0,0,-1;1.5708rad)
  Support = -> [Pocket077]
  sketch-geometry (4):
    g0: LineSegment StartX=5 StartY=14.25 StartZ=0 EndX=10 EndY=14.25 EndZ=0
    g1: LineSegment StartX=10 StartY=14.25 StartZ=0 EndX=10 EndY=-14.25 EndZ=0
    g2: LineSegment StartX=10 StartY=-14.25 StartZ=0 EndX=5 EndY=-14.25 EndZ=0
    g3: LineSegment StartX=5 StartY=-14.25 StartZ=0 EndX=5 EndY=14.25 EndZ=0
  constraints (11):
    c: Coincident(g0,g1)
    c: Coincident(g1,g2)
    c: Coincident(g2,g3)
    c: Coincident(g3,g0)
    c: Horizontal(g0)
    c: Horizontal(g2)
    c: Vertical(g3)
    c: DistanceY(g3,g3) = 28.5
    c: Symmetric(g0,g1,g-1)
    c: DistanceX(g-1,g0) = 5
    c: DistanceX(g0,g0) = 5
FEATURE [PartDesign::Pocket] Pocket078
  BaseFeature = -> Pocket077
  Length = 5
  Length2 = 100
  Placement = pos=(0,0,0) rot=(0.57735,0.57735,0.57735;2.0944rad)
  Profile = -> Sketch304
  Type = 0
FEATURE [Sketcher::SketchObject] Sketch305
  FullyConstrained = true
  MapMode = 5
  Support = -> [XY_Plane381]
  sketch-geometry (32):
    g0: LineSegment StartX=-13.6623 StartY=11 StartZ=0 EndX=-16.8377 EndY=11 EndZ=0
    g1: LineSegment StartX=-16.8377 StartY=11 StartZ=0 EndX=-18.4254 EndY=8.25 EndZ=0
    g2: LineSegment StartX=-18.4254 StartY=8.25 StartZ=0 EndX=-16.8377 EndY=5.5 EndZ=0
    g3: LineSegment StartX=-16.8377 StartY=5.5 StartZ=0 EndX=-13.6623 EndY=5.5 EndZ=0
    g4: LineSegment StartX=-13.6623 StartY=5.5 StartZ=0 EndX=-12.0746 EndY=8.25 EndZ=0
    g5: LineSegment StartX=-12.0746 StartY=8.25 StartZ=0 EndX=-13.6623 EndY=11 EndZ=0
    g6: Circle CenterX=-15.25 CenterY=8.25 CenterZ=0 NormalX=0 NormalY=0 NormalZ=1 AngleXU=0 Radius=3.17543
    g7: LineSegment StartX=16.8377 StartY=11 StartZ=0 EndX=13.6623 EndY=11 EndZ=0
    g8: LineSegment StartX=13.6623 StartY=11 StartZ=0 EndX=12.0746 EndY=8.25 EndZ=0
    g9: LineSegment StartX=12.0746 StartY=8.25 StartZ=0 EndX=13.6623 EndY=5.5 EndZ=0
    g10: LineSegment StartX=13.6623 StartY=5.5 StartZ=0 EndX=16.8377 EndY=5.5 EndZ=0
    g11: LineSegment StartX=16.8377 StartY=5.5 StartZ=0 EndX=18.4254 EndY=8.25 EndZ=0
    g12: LineSegment StartX=18.4254 StartY=8.25 StartZ=0 EndX=16.8377 EndY=11 EndZ=0
    g13: Circle CenterX=15.25 CenterY=8.25 CenterZ=0 NormalX=0 NormalY=0 NormalZ=1 AngleXU=0 Radius=3.17543
    g14: LineSegment StartX=-13.6623 StartY=-11 StartZ=0 EndX=-12.0746 EndY=-8.25 EndZ=0
    g15: LineSegment StartX=-12.0746 StartY=-8.25 StartZ=0 EndX=-13.6623 EndY=-5.5 EndZ=0
    g16: LineSegment StartX=-13.6623 StartY=-5.5 StartZ=0 EndX=-16.8377 EndY=-5.5 EndZ=0
    g17: LineSegment StartX=-16.8377 StartY=-5.5 StartZ=0 EndX=-18.4254 EndY=-8.25 EndZ=0
    g18: LineSegment StartX=-18.4254 StartY=-8.25 StartZ=0 EndX=-16.8377 EndY=-11 EndZ=0
    g19: LineSegment StartX=-16.8377 StartY=-11 StartZ=0 EndX=-13.6623 EndY=-11 EndZ=0
    g20: Circle CenterX=-15.25 CenterY=-8.25 CenterZ=0 NormalX=0 NormalY=0 NormalZ=1 AngleXU=0 Radius=3.17543
    g21: LineSegment StartX=16.8377 StartY=-11 StartZ=0 EndX=18.4254 EndY=-8.25 EndZ=0
    g22: LineSegment StartX=18.4254 StartY=-8.25 StartZ=0 EndX=16.8377 EndY=-5.5 EndZ=0
    g23: LineSegment StartX=16.8377 StartY=-5.5 StartZ=0 EndX=13.6623 EndY=-5.5 EndZ=0
    g24: LineSegment StartX=13.6623 StartY=-5.5 StartZ=0 EndX=12.0746 EndY=-8.25 EndZ=0
    g25: LineSegment StartX=12.0746 StartY=-8.25 StartZ=0 EndX=13.6623 EndY=-11 EndZ=0
    g26: LineSegment StartX=13.6623 StartY=-11 StartZ=0 EndX=16.8377 EndY=-11 EndZ=0
    g27: Circle CenterX=15.25 CenterY=-8.25 CenterZ=0 NormalX=0 NormalY=0 NormalZ=1 AngleXU=0 Radius=3.17543
    g28: LineSegment StartX=-15.25 StartY=8.25 StartZ=0 EndX=15.25 EndY=8.25 EndZ=0
    g29: LineSegment StartX=15.25 StartY=8.25 StartZ=0 EndX=15.25 EndY=-8.25 EndZ=0
    g30: LineSegment StartX=15.25 StartY=-8.25 StartZ=0 EndX=-15.25 EndY=-8.25 EndZ=0
    g31: LineSegment StartX=-15.25 StartY=-8.25 StartZ=0 EndX=-15.25 EndY=8.25 EndZ=0
  constraints (75):
    c: Coincident(g0,g1)
    c: Coincident(g1,g2)
    c: Coincident(g2,g3)
    c: Coincident(g3,g4)
    c: Coincident(g4,g5)
    c: Coincident(g5,g0)
    c: Equal(g0, g1-g5) x5
    c: PointOnObject(g0,g6)
    c: PointOnObject(g1,g6)
    c: PointOnObject(g2,g6)
    c: PointOnObject(g3,g6)
    c: PointOnObject(g4,g6)
    c: PointOnObject(g5,g6)
    c: Coincident(g7,g8)
    c: Coincident(g8,g9)
    c: Coincident(g9,g10)
    c: Coincident(g10,g11)
    c: Coincident(g11,g12)
    c: Coincident(g12,g7)
    c: Equal(g7, g8-g12) x5
    c: PointOnObject(g7,g13)
    c: PointOnObject(g8,g13)
    c: PointOnObject(g9,g13)
    c: PointOnObject(g10,g13)
    c: PointOnObject(g11,g13)
    c: PointOnObject(g12,g13)
    c: Coincident(g14,g15)
    c: Coincident(g15,g16)
    c: Coincident(g16,g17)
    c: Coincident(g17,g18)
    c: Coincident(g18,g19)
    c: Coincident(g19,g14)
    c: Equal(g14, g15-g19) x5
    c: PointOnObject(g14,g20)
    c: PointOnObject(g15,g20)
    c: PointOnObject(g16,g20)
    c: PointOnObject(g17,g20)
    c: PointOnObject(g18,g20)
    c: PointOnObject(g19,g20)
    c: Coincident(g21,g22)
    c: Coincident(g22,g23)
    c: Coincident(g23,g24)
    c: Coincident(g24,g25)
    c: Coincident(g25,g26)
    c: Coincident(g26,g21)
    c: Equal(g21, g22-g26) x5
    c: PointOnObject(g21,g27)
    c: PointOnObject(g22,g27)
    c: PointOnObject(g23,g27)
    c: PointOnObject(g24,g27)
    c: PointOnObject(g25,g27)
    c: PointOnObject(g26,g27)
    c: Horizontal(g26)
    c: Horizontal(g19)
    c: Horizontal(g0)
    c: Horizontal(g7)
    c: Coincident(g28,g29)
    c: Coincident(g29,g30)
    c: Coincident(g30,g31)
    c: Coincident(g31,g28)
    c: Horizontal(g28)
    c: Horizontal(g30)
    c: Vertical(g29)
    c: Vertical(g31)
    c: Coincident(g28,g6)
    c: Coincident(g29,g27)
    c: Coincident(g20,g30)
    c: Coincident(g13,g28)
    c: DistanceY(g29,g29) = 16.5
    c: DistanceX(g28,g28) = 30.5
    c: Equal(g6,g20)
    c: Equal(g20,g27)
    c: Equal(g27,g13)
    c: DistanceY(g10,g7) = 5.5
    c: Symmetric(g20,g13,g-1)
FEATURE [PartDesign::Pad] Pad202
  BaseFeature = -> Pocket078
  Direction = (1,1,1)
  Length = 15
  Length2 = 100
  Placement = pos=(0,0,0) rot=(0.57735,0.57735,0.57735;2.0944rad)
  Profile = -> Sketch305
  Type = 0
FEATURE [Sketcher::SketchObject] Sketch306
  FullyConstrained = true
  MapMode = 5
  Placement = pos=(-4.2e-15,6.6e-15,15) rot=(0,0,-1;1.5708rad)
  Support = -> [Pad202]
  sketch-geometry (6):
    g0: LineSegment StartX=-8.25 StartY=15.25 StartZ=0 EndX=8.25 EndY=15.25 EndZ=0
    g1: LineSegment StartX=8.25 StartY=15.25 StartZ=0 EndX=8.25 EndY=-15.25 EndZ=0
    g2: LineSegment StartX=8.25 StartY=-15.25 StartZ=0 EndX=-8.25 EndY=-15.25 EndZ=0
    g3: LineSegment StartX=-8.25 StartY=-15.25 StartZ=0 EndX=-8.25 EndY=15.25 EndZ=0
    g4: Circle CenterX=8.25 CenterY=15.25 CenterZ=0 NormalX=0 NormalY=0 NormalZ=1 AngleXU=0 Radius=1.75
    g5: Circle CenterX=-8.25 CenterY=-15.25 CenterZ=0 NormalX=0 NormalY=0 NormalZ=1 AngleXU=0 Radius=1.75
  constraints (15):
    c: Coincident(g0,g1)
    c: Coincident(g1,g2)
    c: Coincident(g2,g3)
    c: Coincident(g3,g0)
    c: Horizontal(g0)
    c: Horizontal(g2)
    c: Vertical(g1)
    c: Vertical(g3)
    c: Symmetric(g1,g0,g-1)
    c: Coincident(g4,g0)
    c: Coincident(g5,g2)
    c: Diameter(g5) = 3.5
    c: Equal(g5,g4)
    c: DistanceX(g2,g2) = 16.5
    c: DistanceY(g3,g3) = 30.5
FEATURE [PartDesign::Pocket] Pocket079
  BaseFeature = -> Pad202
  Length = 20
  Length2 = 100
  Placement = pos=(0,0,0) rot=(0.57735,0.57735,0.57735;2.0944rad)
  Profile = -> Sketch306
  Type = 0
FEATURE [PartDesign::Body] Body169  label="DC_Support"
  Group = -> [Sketch302,Pad201,Sketch303,Pocket077,Sketch304,Pocket078,Sketch305,Pad202,Sketch306,Pocket079]
  Origin = -> Origin381
  Placement = pos=(-60.25,0,125) rot=(0,0,1;0rad)
  Tip = -> Pocket079
FEATURE [Sketcher::SketchObject] Sketch307
  FullyConstrained = true
  MapMode = 5
  Placement = pos=(0,0,0) rot=(1,0,0;1.5708rad)
  Support = -> [XZ_Plane380]
  sketch-geometry (21):
    g0: LineSegment StartX=-30.5 StartY=40 StartZ=0 EndX=30.5 EndY=40 EndZ=0
    g1: LineSegment StartX=30.5 StartY=40 StartZ=0 EndX=30.5 EndY=14 EndZ=0
    g2: LineSegment StartX=30.5 StartY=14 StartZ=0 EndX=37.8 EndY=14 EndZ=0
    g3: LineSegment StartX=37.8 StartY=14 StartZ=0 EndX=37.8 EndY=9 EndZ=0
    g4: LineSegment StartX=37.8 StartY=9 StartZ=0 EndX=30.5 EndY=9 EndZ=0
    g5: LineSegment StartX=30.5 StartY=9 StartZ=0 EndX=30.5 EndY=0 EndZ=0
    g6: LineSegment StartX=30.5 StartY=0 StartZ=0 EndX=-30.5 EndY=0 EndZ=0
    g7: LineSegment StartX=-30.5 StartY=0 StartZ=0 EndX=-30.5 EndY=9 EndZ=0
    g8: LineSegment StartX=-30.5 StartY=9 StartZ=0 EndX=-37.8 EndY=9 EndZ=0
    g9: LineSegment StartX=-37.8 StartY=9 StartZ=0 EndX=-37.8 EndY=14 EndZ=0
    g10: LineSegment StartX=-37.8 StartY=14 StartZ=0 EndX=-30.5 EndY=14 EndZ=0
    g11: LineSegment StartX=-30.5 StartY=14 StartZ=0 EndX=-30.5 EndY=40 EndZ=0
    g12: Circle CenterX=0 CenterY=20 CenterZ=0 NormalX=0 NormalY=0 NormalZ=1 AngleXU=0 Radius=5.5
    g13: LineSegment StartX=-20.4 StartY=32.5 StartZ=0 EndX=20.4 EndY=32.5 EndZ=0
    g14: LineSegment StartX=20.4 StartY=32.5 StartZ=0 EndX=20.4 EndY=7.5 EndZ=0
    g15: LineSegment StartX=20.4 StartY=7.5 StartZ=0 EndX=-20.4 EndY=7.5 EndZ=0
    g16: LineSegment StartX=-20.4 StartY=7.5 StartZ=0 EndX=-20.4 EndY=32.5 EndZ=0
    g17: Circle CenterX=20.4 CenterY=32.5 CenterZ=0 NormalX=0 NormalY=0 NormalZ=1 AngleXU=0 Radius=2.25
    g18: Circle CenterX=20.4 CenterY=7.5 CenterZ=0 NormalX=0 NormalY=0 NormalZ=1 AngleXU=0 Radius=2.25
    g19: Circle CenterX=-20.4 CenterY=32.5 CenterZ=0 NormalX=0 NormalY=0 NormalZ=1 AngleXU=0 Radius=2.25
    g20: Circle CenterX=-20.4 CenterY=7.5 CenterZ=0 NormalX=0 NormalY=0 NormalZ=1 AngleXU=0 Radius=2.25
  constraints (54):
    c: Coincident(g0,g1)
    c: Vertical(g1)
    c: Coincident(g1,g2)
    c: Coincident(g2,g3)
    c: Vertical(g3)
    c: Coincident(g3,g4)
    c: Coincident(g4,g5)
    c: Vertical(g5)
    c: Coincident(g5,g6)
    c: Coincident(g6,g7)
    c: Coincident(g7,g8)
    c: Coincident(g8,g9)
    c: Coincident(g9,g10)
    c: Horizontal(g10)
    c: Coincident(g10,g11)
    c: Coincident(g11,g0)
    c: Vertical(g11)
    c: Symmetric(g0,g0,g-2)
    c: Symmetric(g6,g5,g-2)
    c: DistanceY(g5,g0) = 40
    c: Equal(g8,g10)
    c: Symmetric(g3,g8,g-2)
    c: Symmetric(g4,g7,g-2)
    c: Horizontal(g8)
    c: Vertical(g9)
    c: Equal(g9,g3)
    c: Horizontal(g2)
    c: DistanceY(g9,g9) = 5
    c: DistanceX(g10,g10) = 7.3
    c: DistanceX(g6,g6) = 61
    c: PointOnObject(g6,g-1)
    c: DistanceY(g7,g7) = 9
    c: PointOnObject(g12,g-2)
    c: DistanceY(g-1,g12) = 20
    c: Diameter(g12) = 11
    c: Coincident(g13,g14)
    c: Coincident(g14,g15)
    c: Coincident(g15,g16)
    c: Coincident(g16,g13)
    c: Horizontal(g13)
    c: Horizontal(g15)
    c: Vertical(g14)
    c: Vertical(g16)
    c: Coincident(g17,g13)
    c: Coincident(g18,g14)
    c: Coincident(g19,g13)
    c: Coincident(g20,g15)
    c: Diameter(g20) = 4.5
    c: Equal(g20,g19)
    c: Equal(g20,g17)
    c: Equal(g20,g18)
    c: DistanceX(g15,g15) = 40.8
    c: DistanceY(g16,g16) = 25
    c: Symmetric(g19,g18,g12)
FEATURE [PartDesign::Pad] Pad203
  Direction = (1,1,1)
  Length = 22
  Length2 = 100
  Midplane = true
  Placement = pos=(0,0,0) rot=(1,0,0;1.5708rad)
  Profile = -> Sketch307
  Type = 0
FEATURE [Sketcher::SketchObject] Sketch308
  FullyConstrained = true
  MapMode = 5
  Placement = pos=(0,4e-15,9) rot=(1,0,0;3.14159rad)
  Support = -> [Pad203]
  sketch-geometry (8):
    g0: Circle CenterX=33.95 CenterY=5 CenterZ=0 NormalX=0 NormalY=0 NormalZ=1 AngleXU=0 Radius=1.5
    g1: Circle CenterX=33.95 CenterY=-5 CenterZ=0 NormalX=0 NormalY=0 NormalZ=1 AngleXU=0 Radius=1.5
    g2: Circle CenterX=-33.95 CenterY=5 CenterZ=0 NormalX=0 NormalY=0 NormalZ=1 AngleXU=0 Radius=1.5
    g3: Circle CenterX=-33.95 CenterY=-5 CenterZ=0 NormalX=0 NormalY=0 NormalZ=1 AngleXU=0 Radius=1.5
    g4: LineSegment StartX=-33.95 StartY=5 StartZ=0 EndX=33.95 EndY=5 EndZ=0
    g5: LineSegment StartX=33.95 StartY=5 StartZ=0 EndX=33.95 EndY=-5 EndZ=0
    g6: LineSegment StartX=33.95 StartY=-5 StartZ=0 EndX=-33.95 EndY=-5 EndZ=0
    g7: LineSegment StartX=-33.95 StartY=-5 StartZ=0 EndX=-33.95 EndY=5 EndZ=0
  constraints (18):
    c: Coincident(g4,g5)
    c: Coincident(g5,g6)
    c: Coincident(g6,g7)
    c: Coincident(g7,g4)
    c: Horizontal(g6)
    c: Vertical(g5)
    c: Coincident(g4,g2)
    c: Coincident(g5,g1)
    c: Coincident(g0,g4)
    c: Coincident(g3,g6)
    c: DistanceY(g7,g7) = 10
    c: Symmetric(g2,g3,g-1)
    c: Diameter(g3) = 3
    c: Equal(g3,g2)
    c: Equal(g3,g1)
    c: Equal(g3,g0)
    c: DistanceX(g4,g4) = 67.9
    c: Symmetric(g0,g2,g-2)
FEATURE [PartDesign::Pocket] Pocket080
  BaseFeature = -> Pad203
  Length = 5
  Length2 = 100
  Placement = pos=(0,0,0) rot=(1,0,0;1.5708rad)
  Profile = -> Sketch308
  Type = 0
FEATURE [Sketcher::SketchObject] Sketch309
  FullyConstrained = true
  MapMode = 5
  Placement = pos=(0,-11,2.4e-15) rot=(1,0,0;1.5708rad)
  Support = -> [Pocket080]
  sketch-geometry (1):
    g0: Circle CenterX=0 CenterY=20 CenterZ=0 NormalX=0 NormalY=0 NormalZ=1 AngleXU=0 Radius=9.75
  constraints (3):
    c: PointOnObject(g0,g-2)
    c: Diameter(g0) = 19.5
    c: DistanceY(g-1,g0) = 20
FEATURE [PartDesign::Pocket] Pocket081
  BaseFeature = -> Pocket080
  Length = 4
  Length2 = 100
  Placement = pos=(0,0,0) rot=(1,0,0;1.5708rad)
  Profile = -> Sketch309
  Type = 0
FEATURE [Sketcher::SketchObject] Sketch310
  FullyConstrained = true
  MapMode = 5
  Placement = pos=(0,11,-2.4e-15) rot=(-1,0,0;1.5708rad)
  Support = -> [Pocket081]
  sketch-geometry (1):
    g0: Circle CenterX=0 CenterY=-20 CenterZ=0 NormalX=0 NormalY=0 NormalZ=1 AngleXU=0 Radius=9.75
  constraints (3):
    c: PointOnObject(g0,g-2)
    c: DistanceY(g0,g-1) = 20
    c: Diameter(g0) = 19.5
FEATURE [PartDesign::Pocket] Pocket082
  BaseFeature = -> Pocket081
  Length = 4
  Length2 = 100
  Placement = pos=(0,0,0) rot=(1,0,0;1.5708rad)
  Profile = -> Sketch310
  Type = 0
FEATURE [PartDesign::Body] Body170  label="bearing_and_servo_holder"
  Group = -> [Sketch307,Pad203,Sketch308,Pocket080,Sketch309,Pocket081,Sketch310,Pocket082]
  Origin = -> Origin382
  Placement = pos=(0,0,81) rot=(0,0,1;0rad)
  Tip = -> Pocket082
FEATURE [App::Part] Part006  label="side plate"
  Group = -> [Body028,Body024,Body019,Body013,Body023,Body045,Body046,Body047,Body029,Body030,Body031,Part001,Body012,Body010,Body048,Body049,Body116,Body117,Body118,Part017,Part__Feature147,Part__Feature148,Body150,Body151,Body152,Body168,Body169,Body170]
  Origin = -> Origin060
  Placement = pos=(0,72,0) rot=(0,0,1;0rad)
FEATURE [Sketcher::SketchObject] Sketch311
  FullyConstrained = true
  MapMode = 5
  Placement = pos=(0,0,0) rot=(1,0,0;1.5708rad)
  Support = -> [XZ_Plane381]
  sketch-geometry (6):
    g0: Circle CenterX=-35 CenterY=4 CenterZ=0 NormalX=0 NormalY=0 NormalZ=1 AngleXU=0 Radius=2.25
    g1: Circle CenterX=35 CenterY=4 CenterZ=0 NormalX=0 NormalY=0 NormalZ=1 AngleXU=0 Radius=2.25
    g2: ArcOfCircle CenterX=-35 CenterY=4 CenterZ=0 NormalX=0 NormalY=0 NormalZ=1 AngleXU=0 Radius=5 StartAngle=1.5708 EndAngle=4.71239
    g3: ArcOfCircle CenterX=35 CenterY=4 CenterZ=0 NormalX=0 NormalY=0 NormalZ=1 AngleXU=0 Radius=5 StartAngle=4.71239 EndAngle=7.85398
    g4: LineSegment StartX=-35 StartY=-1 StartZ=0 EndX=35 EndY=-1 EndZ=0
    g5: LineSegment StartX=-35 StartY=9 StartZ=0 EndX=35 EndY=9 EndZ=0
  constraints (13):
    c: DistanceX(g0,g1) = 70
    c: DistanceY(g-1,g1) = 4
    c: Symmetric(g1,g0,g-2)
    c: Diameter(g0) = 4.5
    c: Equal(g0,g1)
    c: Tangent(g2,g5) = 1.5708
    c: Tangent(g2,g4) = -1.5708
    c: Tangent(g4,g3) = -1.5708
    c: Tangent(g5,g3) = 1.5708
    c: Horizontal(g4)
    c: Coincident(g2,g0)
    c: Coincident(g3,g1)
    c: Diameter(g2) = 10
FEATURE [PartDesign::Pad] Pad204
  Direction = (1,1,1)
  Length = 6
  Length2 = 100
  Placement = pos=(0,0,0) rot=(1,0,0;1.5708rad)
  Profile = -> Sketch311
  Type = 0
FEATURE [Sketcher::SketchObject] Sketch312
  FullyConstrained = true
  MapMode = 5
  Placement = pos=(0,0,0) rot=(1,0,0;1.5708rad)
  Support = -> [XZ_Plane381]
  sketch-geometry (4):
    g0: ArcOfCircle CenterX=0 CenterY=0 CenterZ=0 NormalX=0 NormalY=0 NormalZ=1 AngleXU=0 Radius=10 StartAngle=3.14159 EndAngle=6.28319
    g1: ArcOfCircle CenterX=3.526e-13 CenterY=18 CenterZ=0 NormalX=0 NormalY=0 NormalZ=1 AngleXU=0 Radius=10 StartAngle=0 EndAngle=3.14159
    g2: LineSegment StartX=10 StartY=-6.73e-14 StartZ=0 EndX=10 EndY=18 EndZ=0
    g3: LineSegment StartX=-10 StartY=1.84001e-11 StartZ=0 EndX=-10 EndY=18 EndZ=0
  constraints (9):
    c: Tangent(g0,g3) = 1.5708
    c: Tangent(g0,g2) = -1.5708
    c: Tangent(g2,g1) = -1.5708
    c: Tangent(g3,g1) = 1.5708
    c: Vertical(g2)
    c: Equal(g0,g1)
    c: Diameter(g1) = 20
    c: DistanceY(g-1,g1) = 18
    c: Coincident(g0,g-1)
FEATURE [PartDesign::Pad] Pad205
  BaseFeature = -> Pad204
  Direction = (1,1,1)
  Length = 15
  Length2 = 100
  Placement = pos=(0,0,0) rot=(1,0,0;1.5708rad)
  Profile = -> Sketch312
  Type = 0
FEATURE [Sketcher::SketchObject] Sketch313
  FullyConstrained = true
  MapMode = 5
  Placement = pos=(0,-15,6.6e-15) rot=(1,0,0;1.5708rad)
  Support = -> [Pad205]
  sketch-geometry (1):
    g0: Circle CenterX=0 CenterY=0 CenterZ=0 NormalX=0 NormalY=0 NormalZ=1 AngleXU=0 Radius=7.5
  constraints (2):
    c: Coincident(g0,g-1)
    c: Diameter(g0) = 15
FEATURE [PartDesign::Pad] Pad206
  BaseFeature = -> Pad205
  Direction = (1,1,1)
  Length = 4
  Length2 = 100
  Placement = pos=(0,0,0) rot=(1,0,0;1.5708rad)
  Profile = -> Sketch313
  Type = 0
FEATURE [Sketcher::SketchObject] Sketch314
  FullyConstrained = true
  MapMode = 5
  Placement = pos=(0,-19,1.98e-14) rot=(1,0,0;1.5708rad)
  Support = -> [Pad206]
  sketch-geometry (7):
    g0: LineSegment StartX=5.25 StartY=3.03109 StartZ=0 EndX=-7.4136e-12 EndY=6.06218 EndZ=0
    g1: LineSegment StartX=-7.4136e-12 StartY=6.06218 StartZ=0 EndX=-5.25 EndY=3.03109 EndZ=0
    g2: LineSegment StartX=-5.25 StartY=3.03109 StartZ=0 EndX=-5.25 EndY=-3.03109 EndZ=0
    g3: LineSegment StartX=-5.25 StartY=-3.03109 StartZ=0 EndX=-5.8504e-12 EndY=-6.06218 EndZ=0
    g4: LineSegment StartX=-5.8504e-12 StartY=-6.06218 StartZ=0 EndX=5.25 EndY=-3.03109 EndZ=0
    g5: LineSegment StartX=5.25 StartY=-3.03109 StartZ=0 EndX=5.25 EndY=3.03109 EndZ=0
    g6: Circle CenterX=0 CenterY=0 CenterZ=0 NormalX=0 NormalY=0 NormalZ=1 AngleXU=0 Radius=6.06218
  constraints (16):
    c: Coincident(g0,g1)
    c: Coincident(g1,g2)
    c: Coincident(g2,g3)
    c: Coincident(g3,g4)
    c: Coincident(g4,g5)
    c: Coincident(g5,g0)
    c: Equal(g0, g1-g5) x5
    c: PointOnObject(g0,g6)
    c: PointOnObject(g1,g6)
    c: PointOnObject(g2,g6)
    c: PointOnObject(g3,g6)
    c: PointOnObject(g4,g6)
    c: PointOnObject(g5,g6)
    c: Coincident(g6,g-1)
    c: Vertical(g2)
    c: DistanceX(g1,g0) = 10.5
FEATURE [PartDesign::Pocket] Pocket083
  BaseFeature = -> Pad206
  Length = 5
  Length2 = 100
  Placement = pos=(0,0,0) rot=(1,0,0;1.5708rad)
  Profile = -> Sketch314
  Type = 0
FEATURE [Sketcher::SketchObject] Sketch315
  FullyConstrained = true
  MapMode = 5
  Placement = pos=(0,-14,1.95e-14) rot=(1,0,0;1.5708rad)
  Support = -> [Pocket083]
  sketch-geometry (1):
    g0: Circle CenterX=0 CenterY=0 CenterZ=0 NormalX=0 NormalY=0 NormalZ=1 AngleXU=0 Radius=3.5
  constraints (2):
    c: Coincident(g0,g-1)
    c: Diameter(g0) = 7
FEATURE [PartDesign::Pocket] Pocket084
  BaseFeature = -> Pocket083
  Length = 15
  Length2 = 100
  Placement = pos=(0,0,0) rot=(1,0,0;1.5708rad)
  Profile = -> Sketch315
  Type = 0
FEATURE [Sketcher::SketchObject] Sketch316
  FullyConstrained = true
  MapMode = 5
  Placement = pos=(0,-6,2.7e-15) rot=(1,0,0;1.5708rad)
  Support = -> [Pocket084]
  sketch-geometry (8):
    g0: LineSegment StartX=-40 StartY=9 StartZ=0 EndX=-30 EndY=9 EndZ=0
    g1: LineSegment StartX=-30 StartY=9 StartZ=0 EndX=-30 EndY=-1 EndZ=0
    g2: LineSegment StartX=-30 StartY=-1 StartZ=0 EndX=-40 EndY=-1 EndZ=0
    g3: LineSegment StartX=-40 StartY=-1 StartZ=0 EndX=-40 EndY=9 EndZ=0
    g4: LineSegment StartX=30 StartY=9 StartZ=0 EndX=40 EndY=9 EndZ=0
    g5: LineSegment StartX=40 StartY=9 StartZ=0 EndX=40 EndY=-1 EndZ=0
    g6: LineSegment StartX=40 StartY=-1 StartZ=0 EndX=30 EndY=-1 EndZ=0
    g7: LineSegment StartX=30 StartY=-1 StartZ=0 EndX=30 EndY=9 EndZ=0
  constraints (23):
    c: Coincident(g0,g1)
    c: Coincident(g1,g2)
    c: Coincident(g2,g3)
    c: Coincident(g3,g0)
    c: Horizontal(g0)
    c: Horizontal(g2)
    c: Vertical(g1)
    c: Vertical(g3)
    c: Coincident(g4,g5)
    c: Coincident(g5,g6)
    c: Coincident(g6,g7)
    c: Coincident(g7,g4)
    c: Horizontal(g4)
    c: Horizontal(g6)
    c: Vertical(g5)
    c: Vertical(g7)
    c: DistanceX(g0,g0) = 10
    c: DistanceY(g3,g3) = 10
    c: DistanceX(g6,g6) = 10
    c: DistanceY(g5,g5) = 10
    c: DistanceY(g6,g-1) = 1
    c: DistanceX(g1,g6) = 60
    c: Symmetric(g1,g6,g-2)
FEATURE [PartDesign::Pocket] Pocket085
  BaseFeature = -> Pocket084
  Length = 4
  Length2 = 100
  Placement = pos=(0,0,0) rot=(1,0,0;1.5708rad)
  Profile = -> Sketch316
  Type = 0
FEATURE [Sketcher::SketchObject] Sketch317
  FullyConstrained = true
  MapMode = 5
  Placement = pos=(0,0,0) rot=(-1,0,0;1.5708rad)
  Support = -> [Pocket085]
  sketch-geometry (8):
    g0: LineSegment StartX=22.5 StartY=1 StartZ=0 EndX=25.5 EndY=1 EndZ=0
    g1: LineSegment StartX=25.5 StartY=1 StartZ=0 EndX=25.5 EndY=-9 EndZ=0
    g2: LineSegment StartX=25.5 StartY=-9 StartZ=0 EndX=22.5 EndY=-9 EndZ=0
    g3: LineSegment StartX=22.5 StartY=-9 StartZ=0 EndX=22.5 EndY=1 EndZ=0
    g4: LineSegment StartX=-25.5 StartY=1 StartZ=0 EndX=-22.5 EndY=1 EndZ=0
    g5: LineSegment StartX=-22.5 StartY=1 StartZ=0 EndX=-22.5 EndY=-9 EndZ=0
    g6: LineSegment StartX=-22.5 StartY=-9 StartZ=0 EndX=-25.5 EndY=-9 EndZ=0
    g7: LineSegment StartX=-25.5 StartY=-9 StartZ=0 EndX=-25.5 EndY=1 EndZ=0
  constraints (22):
    c: Coincident(g0,g1)
    c: Coincident(g1,g2)
    c: Coincident(g2,g3)
    c: Coincident(g3,g0)
    c: Horizontal(g0)
    c: Horizontal(g2)
    c: Vertical(g1)
    c: Vertical(g3)
    c: Coincident(g4,g5)
    c: Coincident(g5,g6)
    c: Coincident(g6,g7)
    c: Coincident(g7,g4)
    c: Horizontal(g4)
    c: Horizontal(g6)
    c: Vertical(g7)
    c: DistanceX(g4,g4) = 3
    c: Equal(g0,g4)
    c: Symmetric(g4,g0,g-2)
    c: Symmetric(g5,g2,g-2)
    c: DistanceY(g5,g5) = 10
    c: DistanceY(g-1,g0) = 1
    c: DistanceX(g4,g0) = 45
FEATURE [PartDesign::Pocket] Pocket086
  BaseFeature = -> Pocket085
  Length = 1.5
  Length2 = 100
  Placement = pos=(0,0,0) rot=(1,0,0;1.5708rad)
  Profile = -> Sketch317
  Type = 0
FEATURE [Sketcher::SketchObject] Sketch318
  FullyConstrained = true
  MapMode = 5
  Support = -> [XY_Plane383]
  sketch-geometry (4):
    g0: LineSegment StartX=-10 StartY=-6 StartZ=0 EndX=-8.5 EndY=-6 EndZ=0
    g1: LineSegment StartX=-8.5 StartY=-6 StartZ=0 EndX=-8.5 EndY=-11 EndZ=0
    g2: LineSegment StartX=-8.5 StartY=-11 StartZ=0 EndX=-10 EndY=-11 EndZ=0
    g3: LineSegment StartX=-10 StartY=-11 StartZ=0 EndX=-10 EndY=-6 EndZ=0
  constraints (12):
    c: Coincident(g0,g1)
    c: Coincident(g1,g2)
    c: Coincident(g2,g3)
    c: Coincident(g3,g0)
    c: Horizontal(g0)
    c: Horizontal(g2)
    c: Vertical(g1)
    c: Vertical(g3)
    c: DistanceY(g0,g-1) = 6
    c: DistanceX(g0,g0) = 1.5
    c: DistanceY(g1,g1) = 5
    c: DistanceX(g0,g-1) = 10
FEATURE [PartDesign::Groove] Groove006
  Angle = 180
  Axis = (0,1,0)
  Base = (0,0,0)
  BaseFeature = -> Pocket086
  Placement = pos=(0,0,0) rot=(1,0,0;1.5708rad)
  Profile = -> Sketch318
  ReferenceAxis = -> Sketch318 [V_Axis]
  Reversed = true
FEATURE [Sketcher::SketchObject] Sketch319
  FullyConstrained = true
  MapMode = 5
  Support = -> [XY_Plane383]
  sketch-geometry (8):
    g0: LineSegment StartX=-10 StartY=-6 StartZ=0 EndX=-8.5 EndY=-6 EndZ=0
    g1: LineSegment StartX=-8.5 StartY=-6 StartZ=0 EndX=-8.5 EndY=-11 EndZ=0
    g2: LineSegment StartX=-8.5 StartY=-11 StartZ=0 EndX=-10 EndY=-11 EndZ=0
    g3: LineSegment StartX=-10 StartY=-11 StartZ=0 EndX=-10 EndY=-6 EndZ=0
    g4: LineSegment StartX=10 StartY=-6 StartZ=0 EndX=8.5 EndY=-6 EndZ=0
    g5: LineSegment StartX=8.5 StartY=-6 StartZ=0 EndX=8.5 EndY=-11 EndZ=0
    g6: LineSegment StartX=8.5 StartY=-11 StartZ=0 EndX=10 EndY=-11 EndZ=0
    g7: LineSegment StartX=10 StartY=-11 StartZ=0 EndX=10 EndY=-6 EndZ=0
  constraints (22):
    c: Coincident(g0,g1)
    c: Coincident(g1,g2)
    c: Coincident(g2,g3)
    c: Coincident(g3,g0)
    c: Horizontal(g0)
    c: Horizontal(g2)
    c: Vertical(g1)
    c: Vertical(g3)
    c: Coincident(g4,g5)
    c: Coincident(g5,g6)
    c: Coincident(g6,g7)
    c: Coincident(g7,g4)
    c: Horizontal(g4)
    c: Horizontal(g6)
    c: Equal(g4,g0)
    c: DistanceX(g2,g2) = 1.5
    c: DistanceY(g3,g3) = 5
    c: DistanceY(g0,g-1) = 6
    c: DistanceX(g2,g-1) = 10
    c: Vertical(g7)
    c: Symmetric(g5,g1,g-2)
    c: Symmetric(g0,g4,g-2)
FEATURE [PartDesign::Pocket] Pocket087
  BaseFeature = -> Groove006
  Length = 18
  Length2 = 100
  Placement = pos=(0,0,0) rot=(1,0,0;1.5708rad)
  Profile = -> Sketch319
  Reversed = true
  Type = 0
FEATURE [Sketcher::SketchObject] Sketch320
  FullyConstrained = true
  MapMode = 5
  Placement = pos=(0,4e-15,18) rot=(1,0,0;3.14159rad)
  Support = -> [Pocket087]
  sketch-geometry (4):
    g0: LineSegment StartX=-10 StartY=11 StartZ=0 EndX=-8.5 EndY=11 EndZ=0
    g1: LineSegment StartX=-8.5 StartY=11 StartZ=0 EndX=-8.5 EndY=6 EndZ=0
    g2: LineSegment StartX=-8.5 StartY=6 StartZ=0 EndX=-10 EndY=6 EndZ=0
    g3: LineSegment StartX=-10 StartY=6 StartZ=0 EndX=-10 EndY=11 EndZ=0
  constraints (12):
    c: Coincident(g0,g1)
    c: Coincident(g1,g2)
    c: Coincident(g2,g3)
    c: Coincident(g3,g0)
    c: Horizontal(g0)
    c: Horizontal(g2)
    c: Vertical(g1)
    c: Vertical(g3)
    c: DistanceX(g0,g0) = 1.5
    c: DistanceY(g3,g3) = 5
    c: DistanceY(g-1,g1) = 6
    c: DistanceX(g2,g-1) = 10
FEATURE [PartDesign::Groove] Groove007
  Angle = 180
  Axis = (0,-1,4e-16)
  Base = (0,8e-15,18)
  BaseFeature = -> Pocket087
  Placement = pos=(0,0,0) rot=(1,0,0;1.5708rad)
  Profile = -> Sketch320
  ReferenceAxis = -> Sketch320 [V_Axis]
  Reversed = true
FEATURE [PartDesign::Chamfer] Chamfer005
  Angle = 45
  Base = -> Groove007 [Edge115,Edge110,Edge137,Edge133]
  BaseFeature = -> Groove007
  ChamferType = 0
  FlipDirection = false
  Placement = pos=(0,0,0) rot=(1,0,0;1.5708rad)
  Size = 1.49
  Size2 = 1
  SupportTransform = false
FEATURE [PartDesign::Body] Body171  label="Side_Spacer"
  Group = -> [Sketch311,Pad204,Sketch312,Pad205,Sketch313,Pad206,Sketch314,Pocket083,Sketch315,Pocket084,Sketch316,Pocket085,Sketch317,Pocket086,Sketch318,Groove006,Sketch319,Pocket087,Sketch320,Groove007,Chamfer005]
  Origin = -> Origin383
  Placement = pos=(0,-39,101) rot=(0,0,1;0rad)
  Tip = -> Chamfer005
FEATURE [App::Part] Part004  label="battery_holder"
  Group = -> [Body036,Body042,Body033,Body034,Body035,Body039,Body051,Body052,Body171]
  Origin = -> Origin055
